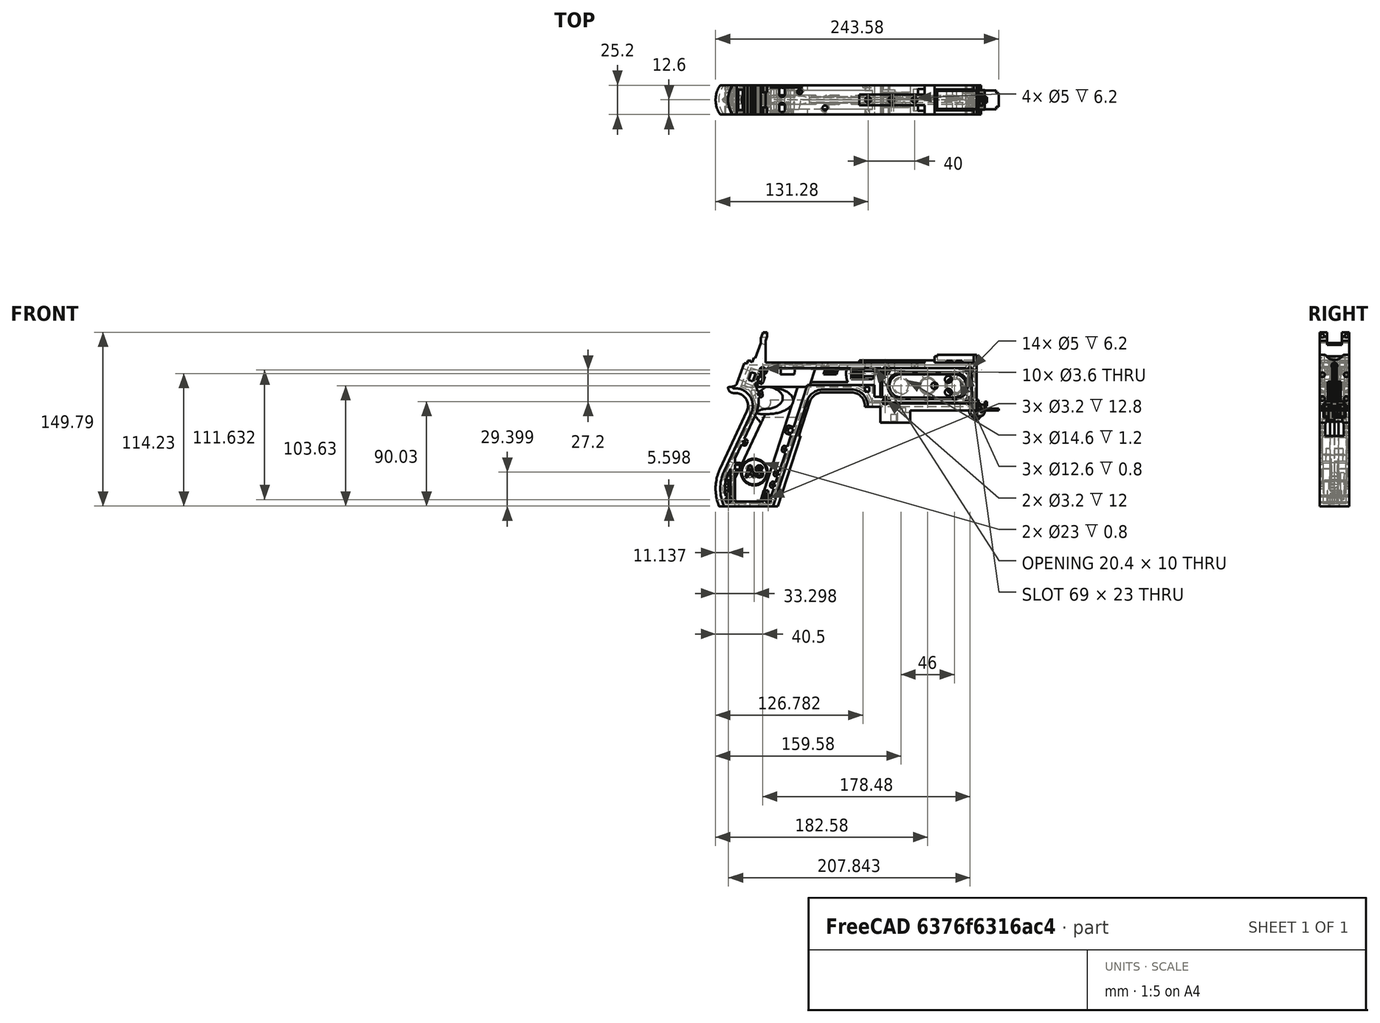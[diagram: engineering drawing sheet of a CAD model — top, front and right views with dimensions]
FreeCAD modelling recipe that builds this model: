
FCSTD DOCUMENT  (FreeCAD 1.0R39319 (Git))
Label: PICON-OF_ver_60
License: All rights reserved
LicenseURL: https://en.wikipedia.org/wiki/All_rights_reserved
objects: Sketcher::SketchObject×129, Part::Extrusion×65, Part::Cut×49, PartDesign::Pad×32, PartDesign::Pocket×21, PartDesign::Chamfer×15, PartDesign::Body×11, Part::MultiFuse×6, PartDesign::Fillet×6, Part::Part2DObjectPython×4, PartDesign::SubtractivePipe×4, PartDesign::SubtractiveLoft×4, PartDesign::Plane×3, PartDesign::SubShapeBinder×2, Part::Sweep×1, PartDesign::ShapeBinder×1, Mesh::Feature×1, PartDesign::Point×1, PartDesign::Groove×1
note: 650 computed .brp shape members not serialized (recipe doc carries the construction recipe); baked Part::Feature solids carry a one-line shape summary decoded from their .brp

FEATURE [Sketcher::SketchObject] Sketch  label="corpo principale"
  ArcFitTolerance = 1e-06
  AttacherType = Attacher::AttachEngine3D
  AttachmentSupport = -> [XZ_Plane]
  FullyConstrained = true
  MakeInternals = false
  MapMode = 5
  Placement = pos=(0,0,0) rot=(1,0,0;1.5708rad)
  sketch-geometry (65):
    g0: LineSegment StartX=0 StartY=0 StartZ=0 EndX=-57.2 EndY=0 EndZ=0
    g1: LineSegment StartX=-57.2 StartY=0 StartZ=0 EndX=-57.2 EndY=-10.4 EndZ=0
    g2: LineSegment StartX=-57.2 StartY=-10.4 StartZ=0 EndX=-82.8 EndY=-10.4 EndZ=0
    g3: LineSegment StartX=-82.8 StartY=-10.4 StartZ=0 EndX=-82.8 EndY=3.2 EndZ=0
    g4: LineSegment StartX=-82.8 StartY=3.2 StartZ=0 EndX=-93.6 EndY=3.2 EndZ=0
    g5: LineSegment StartX=-93.6 StartY=3.2 StartZ=0 EndX=-93.6 EndY=4 EndZ=0
    g6: LineSegment StartX=-107.6 StartY=18 StartZ=0 EndX=-132.428 EndY=18 EndZ=0
    g7: LineSegment StartX=-145.743 StartY=8.32624 StartZ=0 EndX=-175.232 EndY=-82.4316 EndZ=0
    g8: LineSegment StartX=-175.232 StartY=-82.4316 StartZ=0 EndX=-217.232 EndY=-82.4316 EndZ=0
    g9: LineSegment StartX=-217.232 StartY=-52.1862 StartZ=0 EndX=-193.988 EndY=-2.33927 EndZ=0
    g10: LineSegment StartX=-206.196 StartY=23.0857 StartZ=0 EndX=-199.861 EndY=40.4914 EndZ=0
    g11: LineSegment StartX=-199.861 StartY=40.4914 StartZ=0 EndX=-197.061 EndY=40.4914 EndZ=0
    g12: LineSegment StartX=-197.061 StartY=40.4914 StartZ=0 EndX=-197.061 EndY=42.8914 EndZ=0
    g13: LineSegment StartX=-197.061 StartY=42.8914 StartZ=0 EndX=-194.261 EndY=42.8914 EndZ=0
    g14: LineSegment StartX=-194.261 StartY=42.8914 StartZ=0 EndX=-194.535 EndY=42.1397 EndZ=0
    g15: LineSegment StartX=-194.535 StartY=42.1397 StartZ=0 EndX=-193.031 EndY=41.5924 EndZ=0
    g16: LineSegment StartX=-193.031 StartY=41.5924 StartZ=0 EndX=-191.663 EndY=45.3512 EndZ=0
    g17: LineSegment StartX=-191.663 StartY=45.3512 StartZ=0 EndX=-190.536 EndY=44.9408 EndZ=0
    g18: LineSegment StartX=-190.536 StartY=44.9408 StartZ=0 EndX=-185.747 EndY=58.0965 EndZ=0
    g19: LineSegment StartX=-185.747 StartY=58.0965 StartZ=0 EndX=-185.747 EndY=62.0965 EndZ=0
    g20: LineSegment StartX=-185.747 StartY=62.0965 StartZ=0 EndX=-183.832 EndY=67.3588 EndZ=0
    g21: LineSegment StartX=-183.832 StartY=67.3588 StartZ=0 EndX=-180.232 EndY=67.3588 EndZ=0
    g22: LineSegment StartX=-180.232 StartY=67.3588 StartZ=0 EndX=-180.232 EndY=63.7588 EndZ=0
    g23: LineSegment StartX=-180.232 StartY=63.7588 StartZ=0 EndX=-181.6 EndY=60 EndZ=0
    g24: LineSegment StartX=-181.6 StartY=60 StartZ=0 EndX=-181.6 EndY=41.2 EndZ=0
    g25: LineSegment StartX=-181.6 StartY=41.2 StartZ=0 EndX=-100.8 EndY=41.2 EndZ=0
    g26: LineSegment StartX=-36 StartY=43.2 StartZ=0 EndX=-36 EndY=41.2 EndZ=0
    g27: LineSegment StartX=0 StartY=48 StartZ=0 EndX=0 EndY=0 EndZ=0
    g28: LineSegment StartX=-209.901 StartY=19.85 StartZ=0 EndX=-209.901 EndY=20.1 EndZ=0
    g29: LineSegment StartX=-208.001 StartY=22 StartZ=0 EndX=-207.747 EndY=22 EndZ=0
    g30: LineSegment StartX=-207.583 StartY=19 StartZ=0 EndX=-209.051 EndY=19 EndZ=0
    g31: ArcOfCircle CenterX=-208.001 CenterY=20.1 CenterZ=0 NormalX=0 NormalY=0 NormalZ=1 AngleXU=0 Radius=1.9 StartAngle=1.5708 EndAngle=3.14159
    g32: GeomPoint [constr] X=-209.901 Y=22 Z=0
    g33: ArcOfCircle CenterX=-209.051 CenterY=19.85 CenterZ=0 NormalX=0 NormalY=0 NormalZ=1 AngleXU=0 Radius=0.85 StartAngle=3.14159 EndAngle=4.71239
    g34: GeomPoint [constr] X=-209.901 Y=19 Z=0
    g35: ArcOfCircle CenterX=-207.747 CenterY=23.65 CenterZ=0 NormalX=0 NormalY=0 NormalZ=1 AngleXU=0 Radius=1.65 StartAngle=4.71239 EndAngle=5.93412
    g36: GeomPoint [constr] X=-206.591 Y=22 Z=0
    g37: LineSegment StartX=-4 StartY=6 StartZ=0 EndX=-4 EndY=36.4 EndZ=0
    g38: LineSegment StartX=-4 StartY=36.4 StartZ=0 EndX=-185.2 EndY=36.4 EndZ=0
    g39: LineSegment StartX=-185.2 StartY=36.4 StartZ=0 EndX=-190.441 EndY=22 EndZ=0
    g40: LineSegment StartX=-214.575 StartY=-78.4316 StartZ=0 EndX=-178.142 EndY=-78.4316 EndZ=0
    g41: LineSegment StartX=-178.142 StartY=-78.4316 StartZ=0 EndX=-145.51 EndY=22 EndZ=0
    g42: LineSegment StartX=-145.51 StartY=22 StartZ=0 EndX=-87.91 EndY=22 EndZ=0
    g43: LineSegment StartX=-87.91 StartY=22 StartZ=0 EndX=-87.91 EndY=11.6 EndZ=0
    g44: LineSegment StartX=-87.91 StartY=11.6 StartZ=0 EndX=-80.11 EndY=11.6 EndZ=0
    g45: LineSegment StartX=-80.11 StartY=11.6 StartZ=0 EndX=-80.11 EndY=6 EndZ=0
    g46: LineSegment StartX=-80.11 StartY=6 StartZ=0 EndX=-4 EndY=6 EndZ=0
    g47: LineSegment StartX=-190.363 StartY=-4.02975 StartZ=0 EndX=-213.607 EndY=-53.8767 EndZ=0
    g48: ArcOfCircle CenterX=-132.428 CenterY=4 CenterZ=0 NormalX=0 NormalY=0 NormalZ=1 AngleXU=0 Radius=14 StartAngle=1.5708 EndAngle=2.82743
    g49: GeomPoint [constr] X=-142.6 Y=18 Z=0
    g50: ArcOfCircle CenterX=-107.6 CenterY=4 CenterZ=0 NormalX=0 NormalY=0 NormalZ=1 AngleXU=0 Radius=14 StartAngle=0 EndAngle=1.5708
    g51: GeomPoint [constr] X=-93.6 Y=18 Z=0
    g52: ArcOfCircle CenterX=-184.801 CenterY=-67.3089 CenterZ=0 NormalX=0 NormalY=0 NormalZ=1 AngleXU=0 Radius=35.7833 StartAngle=2.70526 EndAngle=3.57792
    g53: ArcOfCircle CenterX=-207.583 CenterY=4 CenterZ=0 NormalX=0 NormalY=0 NormalZ=1 AngleXU=0 Radius=15 StartAngle=5.84685 EndAngle=7.85398
    g54: LineSegment [constr] StartX=-213.607 StartY=-53.8767 StartZ=0 EndX=-217.232 EndY=-52.1862 EndZ=0
    g55: ArcOfCircle CenterX=-184.801 CenterY=-67.3089 CenterZ=0 NormalX=0 NormalY=0 NormalZ=1 AngleXU=0 Radius=31.7833 StartAngle=2.70526 EndAngle=3.49911
    g56: ArcOfCircle CenterX=-218.095 CenterY=8.90192 CenterZ=0 NormalX=0 NormalY=0 NormalZ=1 AngleXU=0 Radius=30.5989 StartAngle=5.84685 EndAngle=6.72553
    g57: LineSegment StartX=-44.6 StartY=43.2 StartZ=0 EndX=-36 EndY=43.2 EndZ=0
    g58: LineSegment StartX=-100.8 StartY=41.2 StartZ=0 EndX=-44.6 EndY=41.2 EndZ=0
    g59: LineSegment StartX=-44.6 StartY=41.2 StartZ=0 EndX=-44.6 EndY=43.2 EndZ=0
    g60: LineSegment StartX=-2.4 StartY=48 StartZ=0 EndX=0 EndY=48 EndZ=0
    g61: LineSegment StartX=-36 StartY=41.2 StartZ=0 EndX=-2.4 EndY=41.2 EndZ=0
    g62: LineSegment StartX=-2.4 StartY=41.2 StartZ=0 EndX=-2.4 EndY=48 EndZ=0
    g63: LineSegment [constr] StartX=-181.6 StartY=36.4 StartZ=0 EndX=-152.209 EndY=36.4 EndZ=0
    g64: LineSegment [constr] StartX=-181.6 StartY=36.4 StartZ=0 EndX=-130.41 EndY=36.4 EndZ=0
  constraints (183):
    c: Coincident(g-1,g0)
    c: PointOnObject(g0,g-1)
    c: Coincident(g0,g1)
    c: Vertical(g1)
    c: Coincident(g1,g2)
    c: Horizontal(g2)
    c: Coincident(g2,g3)
    c: Vertical(g3)
    c: Coincident(g3,g4)
    c: Coincident(g4,g5)
    c: Vertical(g5)
    c: Horizontal(g6)
    c: Coincident(g7,g8)
    c: Horizontal(g8)
    c: Coincident(g10,g11)
    c: Horizontal(g11)
    c: Coincident(g11,g12)
    c: Vertical(g12)
    c: Coincident(g12,g13)
    c: Horizontal(g13)
    c: Coincident(g13,g14)
    c: Coincident(g14,g15)
    c: Coincident(g15,g16)
    c: Coincident(g16,g17)
    c: Coincident(g17,g18)
    c: Coincident(g18,g19)
    c: Vertical(g19)
    c: Coincident(g19,g20)
    c: Coincident(g20,g21)
    c: Horizontal(g21)
    c: Coincident(g21,g22)
    c: Vertical(g22)
    c: Coincident(g22,g23)
    c: Coincident(g23,g24)
    c: Vertical(g24)
    c: Coincident(g24,g25)
    c: Horizontal(g25)
    c: Coincident(g57,g26)
    c: Vertical(g26)
    c: Coincident(g26,g61)
    c: PointOnObject(g60,g-2)
    c: Coincident(g60,g27)
    c: Coincident(g27,g0)
    c: DistanceY(g27,g27) = 48
    c: DistanceY(g1,g1) = 10.4
    c: DistanceX(g0,g0) = 57.2
    c: DistanceX(g2,g2) = 25.6
    c: Horizontal(g4)
    c: DistanceY(g3,g3) = 13.6
    c: DistanceX(g4,g4) = 10.8
    c: DistanceY(g5,g51) = 14.8
    c: DistanceX(g49,g51) = 49
    c: Distance(g7,g49) = 105.6
    c: DistanceX(g61,g60) = 36
    c: DistanceX(g25,g25) = 80.8
    c: DistanceY(g24,g24) = 18.8
    c: DistanceY(g22,g22) = 3.6
    c: Distance(g23) = 4
    c: Angle(g-1,g23) = 1.22173
    c: DistanceX(g21,g21) = 3.6
    c: Distance(g20) = 5.6
    c: Angle(g-1,g20) = 1.22173
    c: DistanceY(g19,g19) = 4
    c: Distance(g18) = 14
    c: Angle(g-1,g18) = 1.22173
    c: Distance(g17) = 1.2
    c: Distance(g16) = 4
    c: Angle(g16) = 1.22173
    c: Perpendicular(g18,g17)
    c: Distance(g15) = 1.6
    c: Perpendicular(g16,g15)
    c: Distance(g14) = 0.8
    c: DistanceX(g13,g13) = 2.8
    c: Perpendicular(g15,g14)
    c: DistanceY(g12,g12) = 2.4
    c: DistanceX(g11,g11) = 2.8
    c: Distance(g9) = 55
    c: Angle(g9,g-1) = 2.00713
    c: Horizontal(g29)
    c: Vertical(g28)
    c: Horizontal(g30)
    c: PointOnObject(g32,g29)
    c: PointOnObject(g32,g28)
    c: Tangent(g29,g31) = 1.5708
    c: Tangent(g28,g31) = 1.5708
    c: PointOnObject(g34,g28)
    c: PointOnObject(g34,g30)
    c: Tangent(g28,g33) = 1.5708
    c: Tangent(g30,g33) = 1.5708
    c: PointOnObject(g36,g29)
    c: PointOnObject(g36,g10)
    c: Tangent(g29,g35) = -1.5708
    c: Tangent(g10,g35) = -1.5708
    c: Angle(g-1,g10) = 1.22173
    c: Radius(g35) = 1.65
    c: Vertical(g37)
    c: Coincident(g37,g38)
    c: Horizontal(g38)
    c: Coincident(g38,g39)
    c: Horizontal(g40)
    c: Coincident(g40,g41)
    c: Coincident(g41,g42)
    c: Horizontal(g42)
    c: Coincident(g42,g43)
    c: Vertical(g43)
    c: Coincident(g43,g44)
    c: Horizontal(g44)
    c: Coincident(g44,g45)
    c: Vertical(g45)
    c: Coincident(g45,g46)
    c: Coincident(g46,g37)
    c: Horizontal(g46)
    c: DistanceY(g0,g37) = 6
    c: DistanceX(g37,g0) = 4
    c: DistanceY(g37,g25) = 4.8
    c: DistanceX(g38,g38) = 181.2
    c: DistanceX(g42,g42) = 57.6
    c: DistanceY(g49,g41) = 4
    c: DistanceX(g41,g49) = 2.91
    c: DistanceY(g43,g43) = 10.4
    c: DistanceX(g44,g44) = 7.8
    c: DistanceY(g7,g40) = 4
    c: Distance(g47) = 55
    c: Angle(g-1,g39) = 1.22173
    c: PointOnObject(g49,g7)
    c: PointOnObject(g49,g6)
    c: Tangent(g7,g48) = -1.5708
    c: Tangent(g6,g48) = -1.5708
    c: PointOnObject(g51,g5)
    c: PointOnObject(g51,g6)
    c: Tangent(g5,g50) = -1.5708
    c: Tangent(g6,g50) = -1.5708
    c: Radius(g50) = 14
    c: Radius(g48) = 14
    c: DistanceX(g8,g8) = 42
    c: Angle(g7,g-1) = 1.88496
    c: Parallel(g41,g7)
    c: Parallel(g47,g9)
    c: Coincident(g52,g8)
    c: Tangent(g52,g9) = 1.5708
    c: DistanceX(g9,g8) = 0
    c: Tangent(g53,g9) = -1.5708
    c: Tangent(g53,g30) = -1.5708
    c: Diameter(g53) = 30
    c: DistanceY(g53,g0) = -4
    c: Coincident(g54,g47)
    c: Distance(g54) = 4
    c: Coincident(g54,g9)
    c: Coincident(g55,g40)
    c: Tangent(g55,g47) = -1.5708
    c: Coincident(g52,g55)
    c: Coincident(g56,g39)
    c: Tangent(g56,g47) = 1.5708
    c: Horizontal(g57)
    c: DistanceX(g57,g57) = 8.6
    c: Coincident(g58,g25)
    c: Horizontal(g58)
    c: Coincident(g59,g58)
    c: Vertical(g59)
    c: DistanceY(g58,g57) = 2
    c: DistanceX(g58,g58) = 56.2
    c: Coincident(g59,g57)
    c: DistanceY(g41,g36) = 0
    c: DistanceY(g36,g39) = 0
    c: DistanceY(g28,g28) = 0.25
    c: DistanceX(g30,g36) = 2.46
    c: DistanceX(g28,g29) = 1.9
    c: Coincident(g62,g60)
    c: Horizontal(g60)
    c: DistanceX(g62,g27) = 2.4
    c: Coincident(g61,g62)
    c: DistanceY(g26,g26) = 2
    c: Vertical(g62)
    c: DistanceY(g61,g60) = 6.8
    c: Horizontal(g61)
    c: Distance(g63) = 29.391
    c: PointOnObject(g63,g38)
    c: PointOnObject(g63,g38)
    c: Distance(g64) = 51.19
    c: PointOnObject(g64,g38)
    c: PointOnObject(g64,g38)
    c: DistanceX(g24,g63) = 0
    c: DistanceX(g24,g64) = 0
FEATURE [Part::Extrusion] Extrude  label="Extrude corpo principale"
  Base = -> Sketch
  Dir = (0,-1,2e-16)
  DirMode = 2
  FaceMakerClass = Part::FaceMakerBullseye
  FaceMakerMode = 3
  LengthFwd = 25.2
  LengthRev = 12.6
  Solid = true
  Symmetric = true
FEATURE [Sketcher::SketchObject] Sketch002  label="scavo grilletto"
  ArcFitTolerance = 1e-06
  AttachmentSupport = -> [XZ_Plane]
  ExternalGeometry = -> [Sketch]
  FullyConstrained = true
  MakeInternals = false
  MapMode = 5
  Placement = pos=(0,0,0) rot=(1,0,0;1.5708rad)
  sketch-geometry (4):
    g0: LineSegment StartX=-89.51 StartY=22 StartZ=0 EndX=-152.71 EndY=22 EndZ=0
    g1: LineSegment StartX=-152.71 StartY=22 StartZ=0 EndX=-167.006 EndY=-22 EndZ=0
    g2: LineSegment StartX=-167.006 StartY=-22 StartZ=0 EndX=-89.51 EndY=-22 EndZ=0
    g3: LineSegment StartX=-89.51 StartY=-22 StartZ=0 EndX=-89.51 EndY=22 EndZ=0
  constraints (12):
    c: Horizontal(g0)
    c: Coincident(g0,g1)
    c: Coincident(g1,g2)
    c: Horizontal(g2)
    c: Coincident(g2,g3)
    c: Coincident(g3,g0)
    c: Vertical(g3)
    c: Angle(g1,g0) = 1.88496
    c: DistanceY(g3,g3) = 44
    c: DistanceX(g0,g0) = 63.2
    c: DistanceX(g0,g-3) = 1.6
    c: DistanceY(g-3,g0) = 0
FEATURE [Sketcher::SketchObject] Sketch004  label="traiettoria arrotondamento impugnatura anteriore"
  ArcFitTolerance = 1e-06
  AttachmentSupport = -> [XZ_Plane]
  ExternalGeometry = -> [Sketch]
  FullyConstrained = true
  MakeInternals = false
  MapMode = 5
  Placement = pos=(0,0,0) rot=(1,0,0;1.5708rad)
  sketch-geometry (13):
    g0: LineSegment StartX=-175.232 StartY=-82.4316 StartZ=0 EndX=-145.743 EndY=8.32624 EndZ=0
    g1: LineSegment StartX=-93.6 StartY=3.2 StartZ=0 EndX=-93.6 EndY=4 EndZ=0
    g2: LineSegment StartX=-132.428 StartY=18 StartZ=0 EndX=-107.6 EndY=18 EndZ=0
    g3: ArcOfCircle CenterX=-132.428 CenterY=4 CenterZ=0 NormalX=0 NormalY=0 NormalZ=1 AngleXU=0 Radius=14 StartAngle=1.5708 EndAngle=2.82743
    g4: ArcOfCircle CenterX=-107.6 CenterY=4 CenterZ=0 NormalX=0 NormalY=0 NormalZ=1 AngleXU=0 Radius=14 StartAngle=0 EndAngle=1.5708
    g5: LineSegment StartX=-175.232 StartY=-82.4316 StartZ=0 EndX=-217.232 EndY=-82.4316 EndZ=0
    g6: LineSegment StartX=-217.232 StartY=-52.1862 StartZ=0 EndX=-193.988 EndY=-2.33927 EndZ=0
    g7: LineSegment StartX=-209.051 StartY=19 StartZ=0 EndX=-207.583 EndY=19 EndZ=0
    g8: LineSegment StartX=-209.901 StartY=20.1 StartZ=0 EndX=-209.901 EndY=19.85 EndZ=0
    g9: ArcOfCircle CenterX=-184.801 CenterY=-67.3089 CenterZ=0 NormalX=0 NormalY=0 NormalZ=1 AngleXU=0 Radius=35.7833 StartAngle=2.70526 EndAngle=3.57792
    g10: ArcOfCircle CenterX=-207.583 CenterY=4 CenterZ=0 NormalX=0 NormalY=0 NormalZ=1 AngleXU=0 Radius=15 StartAngle=5.84685 EndAngle=7.85398
    g11: ArcOfCircle CenterX=-209.051 CenterY=19.85 CenterZ=0 NormalX=0 NormalY=0 NormalZ=1 AngleXU=0 Radius=0.85 StartAngle=3.14159 EndAngle=4.71239
    g12: ArcOfCircle CenterX=-208.001 CenterY=20.1 CenterZ=0 NormalX=0 NormalY=0 NormalZ=1 AngleXU=0 Radius=1.9 StartAngle=1.5708 EndAngle=3.14159
  constraints (26):
    c: Coincident(g0,g-3)
    c: Coincident(g0,g-6)
    c: Coincident(g1,g-8)
    c: Coincident(g1,g-7)
    c: Coincident(g2,g-5)
    c: Coincident(g2,g-4)
    c: Coincident(g3,g2)
    c: Tangent(g3,g0) = 1.5708
    c: Coincident(g4,g1)
    c: Tangent(g4,g2) = 1.5708
    c: Coincident(g5,g0)
    c: Coincident(g5,g-9)
    c: Coincident(g6,g-12)
    c: Coincident(g6,g-11)
    c: Coincident(g7,g-15)
    c: Coincident(g7,g-14)
    c: Coincident(g8,g-16)
    c: Coincident(g8,g-17)
    c: Tangent(g9,g6) = 1.5708
    c: Coincident(g9,g5)
    c: Coincident(g10,g7)
    c: Tangent(g10,g6) = -1.5708
    c: Tangent(g11,g7) = -1.5708
    c: Coincident(g11,g8)
    c: Tangent(g12,g8) = -1.5708
    c: Coincident(g12,g-17)
FEATURE [PartDesign::Plane] DatumPlane  label="Piano per disegno arrotondamento impugnatura"
  AttachmentSupport = -> [Sketch]
  Length = 73.6581
  MapMode = 7
  Placement = pos=(-145.743,1.8e-15,8.32624) rot=(0.154555,0.154555,0.97582;1.59527rad)
  ResizeMode = 0
  Width = 303.511
FEATURE [Sketcher::SketchObject] Sketch005  label="forma arrotondamento impugnatura anteriore"
  ArcFitTolerance = 1e-06
  AttachmentSupport = -> [DatumPlane]
  FullyConstrained = true
  MakeInternals = false
  MapMode = 5
  Placement = pos=(-145.743,1.8e-15,8.32624) rot=(0.154555,0.154555,0.97582;1.59527rad)
  sketch-geometry (5):
    g0: GeomPoint [constr] X=0 Y=-4 Z=0
    g1: GeomPoint [constr] X=-12.6 Y=7.1e-15 Z=0
    g2: GeomPoint [constr] X=12.6 Y=4.97e-14 Z=0
    g3: LineSegment StartX=-12.6 StartY=7.1e-15 StartZ=0 EndX=12.6 EndY=4.97e-14 EndZ=0
    g4: ArcOfCircle CenterX=-3.88e-14 CenterY=17.845 CenterZ=0 NormalX=0 NormalY=0 NormalZ=1 AngleXU=0 Radius=21.845 StartAngle=4.09759 EndAngle=5.32718
  constraints (11):
    c: DistanceY(g0,g-1) = 4
    c: DistanceX(g-1,g0) = 0
    c: DistanceX(g1,g-1) = 12.6
    c: DistanceX(g-1,g2) = 12.6
    c: DistanceY(g-1,g2) = 0
    c: DistanceY(g-1,g1) = 0
    c: Coincident(g3,g1)
    c: Coincident(g3,g2)
    c: Coincident(g4,g1)
    c: Coincident(g4,g2)
    c: PointOnObject(g0,g4)
FEATURE [Part::Sweep] Sweep  label="Sweep impugnatura"
  Frenet = true
  Sections = -> [Sketch005]
  Solid = true
  Spine = -> Sketch [Edge32,Edge33,Edge34,Edge35,Edge36,Edge37,Edge38,Edge39,Edge40,Edge41,Edge42,Edge43,Edge44]
  Transition = 1
FEATURE [Sketcher::SketchObject] Sketch008  label="buchi e pulizie varie"
  ArcFitTolerance = 1e-06
  AttachmentSupport = -> [XZ_Plane]
  ExternalGeometry = -> [Sketch]
  FullyConstrained = true
  MakeInternals = false
  MapMode = 5
  Placement = pos=(0,0,0) rot=(1,0,0;1.5708rad)
  sketch-geometry (26):
    g0: LineSegment StartX=-96.278 StartY=20.155 StartZ=0 EndX=-92.278 EndY=20.155 EndZ=0
    g1: LineSegment StartX=-92.278 StartY=20.155 StartZ=0 EndX=-92.278 EndY=16.155 EndZ=0
    g2: LineSegment StartX=-92.278 StartY=16.155 StartZ=0 EndX=-96.278 EndY=16.155 EndZ=0
    g3: LineSegment StartX=-96.278 StartY=16.155 StartZ=0 EndX=-96.278 EndY=20.155 EndZ=0
    g4: LineSegment StartX=-222.232 StartY=-82.4316 StartZ=0 EndX=-170.232 EndY=-82.4316 EndZ=0
    g5: LineSegment StartX=-170.232 StartY=-82.4316 StartZ=0 EndX=-170.232 EndY=-86.4316 EndZ=0
    g6: LineSegment StartX=-170.232 StartY=-86.4316 StartZ=0 EndX=-222.232 EndY=-86.4316 EndZ=0
    g7: LineSegment StartX=-222.232 StartY=-86.4316 StartZ=0 EndX=-222.232 EndY=-82.4316 EndZ=0
    g8: LineSegment StartX=-213.901 StartY=20.1 StartZ=0 EndX=-213.901 EndY=26 EndZ=0
    g9: LineSegment StartX=-213.901 StartY=26 StartZ=0 EndX=-206.196 EndY=26 EndZ=0
    g10: LineSegment StartX=-17.4 StartY=42.8 StartZ=0 EndX=-12.4 EndY=42.8 EndZ=0
    g11: LineSegment StartX=-12.4 StartY=42.8 StartZ=0 EndX=-12.4 EndY=41.2 EndZ=0
    g12: LineSegment StartX=-12.4 StartY=41.2 StartZ=0 EndX=-17.4 EndY=41.2 EndZ=0
    g13: LineSegment StartX=-17.4 StartY=41.2 StartZ=0 EndX=-17.4 EndY=42.8 EndZ=0
    g14: LineSegment StartX=-25.9 StartY=42.8 StartZ=0 EndX=-20.9 EndY=42.8 EndZ=0
    g15: LineSegment StartX=-20.9 StartY=42.8 StartZ=0 EndX=-20.9 EndY=41.2 EndZ=0
    g16: LineSegment StartX=-20.9 StartY=41.2 StartZ=0 EndX=-25.9 EndY=41.2 EndZ=0
    g17: LineSegment StartX=-25.9 StartY=41.2 StartZ=0 EndX=-25.9 EndY=42.8 EndZ=0
    g18: GeomPoint [constr] X=-206.196 Y=23.0857 Z=0
    g19: GeomPoint [constr] X=-213.901 Y=20.1 Z=0
    g20: BSplineCurve PolesCount=4 KnotsCount=2 Degree=3 IsPeriodic=0
    g21-g24: Circle [constr] x4 (B-spline internal-alignment scaffolding for g20; pole/knot coordinates omitted)
    g25: LineSegment StartX=-206.196 StartY=26 StartZ=0 EndX=-206.196 EndY=23.0857 EndZ=0
  constraints (73):
    c: Horizontal(g0)
    c: Coincident(g1,g0)
    c: Vertical(g1)
    c: Coincident(g2,g1)
    c: Horizontal(g2)
    c: Coincident(g3,g2)
    c: Coincident(g3,g0)
    c: Vertical(g3)
    c: DistanceX(g0,g-4) = 4.368
    c: DistanceY(g0,g-4) = 1.845
    c: DistanceY(g1,g1) = 4
    c: DistanceX(g2,g2) = 4
    c: Horizontal(g4)
    c: Coincident(g5,g4)
    c: Vertical(g5)
    c: Coincident(g6,g5)
    c: Horizontal(g6)
    c: Coincident(g7,g6)
    c: Coincident(g7,g4)
    c: Vertical(g7)
    c: DistanceY(g7,g7) = 4
    c: DistanceX(g4,g-5) = 5
    c: DistanceX(g-5,g4) = 5
    c: DistanceY(g4,g-5) = 0
    c: Coincident(g9,g8)
    c: Parallel(g9,g-6)
    c: DistanceX(g8,g-8) = 4
    c: Horizontal(g10)
    c: Coincident(g11,g10)
    c: Vertical(g11)
    c: Coincident(g12,g11)
    c: Horizontal(g12)
    c: Coincident(g13,g12)
    c: Coincident(g13,g10)
    c: Vertical(g13)
    c: Horizontal(g14)
    c: Coincident(g15,g14)
    c: Vertical(g15)
    c: Coincident(g16,g15)
    c: Horizontal(g16)
    c: Coincident(g17,g16)
    c: Coincident(g17,g14)
    c: Vertical(g17)
    c: DistanceY(g11,g10) = 1.6
    c: DistanceX(g10,g10) = 5
    c: DistanceY(g15,g14) = 1.6
    c: DistanceX(g14,g14) = 5
    c: DistanceX(g15,g12) = 3.5
    c: DistanceX(g11,g-9) = 10
    c: DistanceY(g-9,g11) = 0
    c: DistanceY(g-9,g15) = 0
    c: Perpendicular(g8,g9)
    c: DistanceY(g-7,g9) = 4
    c: DistanceY(g8,g-8) = 0
    c: InternalAlignment(g18,g20)
    c: InternalAlignment(g19,g20)
    c: InternalAlignment(g21,g20)
    c: Weight(g21) = 1
    c: InternalAlignment(g22,g20)
    c: Equal(g22,g21)
    c: InternalAlignment(g23,g20)
    c: Equal(g23,g21)
    c: InternalAlignment(g24,g20)
    c: Equal(g24,g21)
    c: Coincident(g18,g-12)
    c: Coincident(g19,g8)
    c: Coincident(g25,g9)
    c: Coincident(g25,g20)
    c: Vertical(g25)
    c: DistanceY(g20,g23) = 0
    c: DistanceY(g22,g18) = 2.26
    c: DistanceX(g22,g18) = 0.93
    c: DistanceX(g20,g23) = 2.9
FEATURE [Part::Extrusion] Extrude004  label="Extrude Buchi e pulizie varie"
  Base = -> Sketch008
  Dir = (0,-1,2e-16)
  DirMode = 2
  FaceMakerClass = Part::FaceMakerBullseye
  FaceMakerMode = 3
  LengthFwd = 25.2
  LengthRev = 0
  Solid = true
  Symmetric = true
FEATURE [Sketcher::SketchObject] Sketch009  label="rinforzi"
  ArcFitTolerance = 1e-06
  AttachmentSupport = -> [XZ_Plane]
  ExternalGeometry = -> [Sketch]
  FullyConstrained = true
  MakeInternals = false
  MapMode = 5
  Placement = pos=(0,0,0) rot=(1,0,0;1.5708rad)
  sketch-geometry (9):
    g0: LineSegment StartX=-87.91 StartY=22 StartZ=0 EndX=-87.91 EndY=36.4 EndZ=0
    g1: LineSegment StartX=-87.91 StartY=36.4 StartZ=0 EndX=-97.91 EndY=36.4 EndZ=0
    g2: LineSegment StartX=-97.91 StartY=36.4 StartZ=0 EndX=-97.91 EndY=22 EndZ=0
    g3: LineSegment StartX=-97.91 StartY=22 StartZ=0 EndX=-87.91 EndY=22 EndZ=0
    g4: LineSegment StartX=-149.713 StartY=9.06563 StartZ=0 EndX=-154.586 EndY=-5.93437 EndZ=0
    g5: LineSegment StartX=-154.586 StartY=-5.93437 StartZ=0 EndX=-191.863 EndY=-5.93437 EndZ=0
    g6: LineSegment StartX=-191.863 StartY=-5.93437 StartZ=0 EndX=-191.863 EndY=9.06563 EndZ=0
    g7: LineSegment StartX=-191.863 StartY=9.06563 StartZ=0 EndX=-149.713 EndY=9.06563 EndZ=0
    g8: LineSegment [constr] StartX=-145.51 StartY=22 StartZ=0 EndX=-149.713 EndY=9.06563 EndZ=0
  constraints (25):
    c: Vertical(g0)
    c: Coincident(g1,g0)
    c: Horizontal(g1)
    c: Coincident(g2,g1)
    c: Vertical(g2)
    c: Coincident(g3,g2)
    c: Coincident(g3,g0)
    c: Horizontal(g3)
    c: Coincident(g0,g-4)
    c: DistanceX(g3,g3) = 10
    c: DistanceY(g0,g-3) = 0
    c: Coincident(g5,g4)
    c: Horizontal(g5)
    c: Coincident(g6,g5)
    c: Vertical(g6)
    c: Coincident(g7,g6)
    c: Coincident(g7,g4)
    c: Horizontal(g7)
    c: Distance(g8) = 13.6
    c: Parallel(g-6,g8)
    c: Coincident(g-6,g8)
    c: Parallel(g4,g-6)
    c: DistanceY(g4,g4) = 15
    c: Coincident(g4,g8)
    c: DistanceX(g-5,g5) = -1.5
FEATURE [Part::Extrusion] Extrude001  label="Extrude scavo grilletto"
  Base = -> Sketch002
  Dir = (0,-1,2e-16)
  DirMode = 2
  FaceMakerClass = Part::FaceMakerBullseye
  FaceMakerMode = 3
  LengthFwd = 16
  LengthRev = 0
  Solid = true
  Symmetric = true
FEATURE [Part::Extrusion] Extrude005  label="Extrude Rinforzi"
  Base = -> Sketch009
  Dir = (0,-1,2e-16)
  DirMode = 2
  FaceMakerClass = Part::FaceMakerBullseye
  FaceMakerMode = 3
  LengthFwd = 2
  LengthRev = 0
  Placement = pos=(0,12.6,0) rot=(0,0,1;0rad)
  Solid = true
  Symmetric = false
FEATURE [PartDesign::ShapeBinder] CopyCut
  TraceSupport = false
FEATURE [PartDesign::Plane] DatumPlane001
  AttachmentSupport = -> [CopyCut]
  Length = 283.944
  MapMode = 5
  Placement = pos=(0,12.6,0) rot=(0,0.707107,0.707107;3.14159rad)
  ResizeMode = 0
  Width = 188.15
FEATURE [Sketcher::SketchObject] Sketch010  label="buco neopixel"
  ArcFitTolerance = 1e-06
  AttachmentSupport = -> [XZ_Plane]
  ExternalGeometry = -> [Sketch]
  FullyConstrained = true
  MakeInternals = false
  MapMode = 5
  Placement = pos=(0,0,0) rot=(1,0,0;1.5708rad)
  sketch-geometry (5):
    g0: LineSegment [constr] StartX=-199.861 StartY=40.4914 StartZ=0 EndX=-201.368 EndY=36.3521 EndZ=0
    g1: LineSegment StartX=-201.368 StartY=36.3521 StartZ=0 EndX=-204.932 EndY=26.5605 EndZ=0
    g2: LineSegment StartX=-201.368 StartY=36.3521 StartZ=0 EndX=-180.2 EndY=28.6477 EndZ=0
    g3: LineSegment StartX=-180.2 StartY=28.6477 StartZ=0 EndX=-183.764 EndY=18.8561 EndZ=0
    g4: LineSegment StartX=-183.764 StartY=18.8561 StartZ=0 EndX=-204.932 EndY=26.5605 EndZ=0
  constraints (14):
    c: Parallel(g0,g-3)
    c: Distance(g0) = 4.405
    c: Coincident(g0,g-3)
    c: Coincident(g2,g1)
    c: Coincident(g3,g2)
    c: Coincident(g4,g3)
    c: Coincident(g4,g1)
    c: Parallel(g1,g-3)
    c: Distance(g1) = 10.42
    c: Coincident(g1,g0)
    c: Parallel(g2,g4)
    c: Perpendicular(g1,g2)
    c: DistanceX(g-4,g2) = 5
    c: Parallel(g3,g1)
FEATURE [Part::Extrusion] Extrude006  label="Extrude buco neopixel"
  Base = -> Sketch010
  Dir = (0,-1,2e-16)
  DirMode = 2
  FaceMakerClass = Part::FaceMakerBullseye
  FaceMakerMode = 3
  LengthFwd = 17.2
  LengthRev = 0
  Solid = true
  Symmetric = true
FEATURE [Sketcher::SketchObject] Sketch011  label="fermo grilletto"
  ArcFitTolerance = 1e-06
  AttachmentSupport = -> [XZ_Plane]
  ExternalGeometry = -> [Sketch]
  FullyConstrained = true
  MakeInternals = false
  MapMode = 5
  Placement = pos=(0,0,0) rot=(1,0,0;1.5708rad)
  sketch-geometry (18):
    g0: LineSegment [constr] StartX=-145.51 StartY=22 StartZ=0 EndX=-157.347 EndY=-14.4293 EndZ=0
    g1: LineSegment [constr] StartX=-157.347 StartY=-14.4293 StartZ=0 EndX=-157.841 EndY=-15.951 EndZ=0
    g2: LineSegment StartX=-161.151 StartY=-13.1932 StartZ=0 EndX=-155.825 EndY=-14.9237 EndZ=0
    g3: LineSegment StartX=-163.167 StartY=-14.2205 StartZ=0 EndX=-164.403 EndY=-18.0247 EndZ=0
    g4: LineSegment StartX=-163.376 StartY=-20.0408 StartZ=0 EndX=-158.05 EndY=-21.7713 EndZ=0
    g5: LineSegment StartX=-158.05 StartY=-21.7713 StartZ=0 EndX=-155.825 EndY=-14.9237 EndZ=0
    g6: LineSegment StartX=-161.645 StartY=-14.7149 StartZ=0 EndX=-157.841 EndY=-15.951 EndZ=0
    g7: LineSegment StartX=-157.841 StartY=-15.951 StartZ=0 EndX=-159.077 EndY=-19.7552 EndZ=0
    g8: LineSegment StartX=-159.077 StartY=-19.7552 StartZ=0 EndX=-162.881 EndY=-18.5191 EndZ=0
    g9: LineSegment StartX=-162.881 StartY=-18.5191 StartZ=0 EndX=-161.645 EndY=-14.7149 EndZ=0
    g10: LineSegment [constr] StartX=-161.645 StartY=-14.7149 StartZ=0 EndX=-161.151 EndY=-13.1932 EndZ=0
    g11: LineSegment [constr] StartX=-159.077 StartY=-19.7552 StartZ=0 EndX=-157.555 EndY=-20.2496 EndZ=0
    g12: LineSegment [constr] StartX=-159.077 StartY=-19.7552 StartZ=0 EndX=-159.572 EndY=-21.2769 EndZ=0
    g13: LineSegment [constr] StartX=-161.645 StartY=-14.7149 StartZ=0 EndX=-163.167 EndY=-14.2205 EndZ=0
    g14: ArcOfCircle CenterX=-161.645 CenterY=-14.7149 CenterZ=0 NormalX=0 NormalY=0 NormalZ=1 AngleXU=0 Radius=1.6 StartAngle=1.25664 EndAngle=2.82743
    g15: GeomPoint [constr] X=-162.673 Y=-12.6988 Z=0
    g16: ArcOfCircle CenterX=-162.881 CenterY=-18.5191 CenterZ=0 NormalX=0 NormalY=0 NormalZ=1 AngleXU=0 Radius=1.6 StartAngle=2.82743 EndAngle=4.39823
    g17: GeomPoint [constr] X=-164.897 Y=-19.5464 Z=0
  constraints (48):
    c: Parallel(g0,g-3)
    c: Distance(g0) = 38.304
    c: Coincident(g0,g-3)
    c: Parallel(g1,g-3)
    c: Distance(g1) = 1.6
    c: Coincident(g1,g0)
    c: Coincident(g5,g4)
    c: Coincident(g5,g2)
    c: Coincident(g7,g6)
    c: Coincident(g8,g7)
    c: Coincident(g9,g8)
    c: Coincident(g9,g6)
    c: Parallel(g7,g-3)
    c: Parallel(g9,g7)
    c: Perpendicular(g6,g7)
    c: Parallel(g6,g8)
    c: Distance(g6) = 4
    c: Distance(g9) = 4
    c: Parallel(g5,g7)
    c: Parallel(g9,g3)
    c: Parallel(g2,g6)
    c: Parallel(g4,g8)
    c: Parallel(g13,g6)
    c: Parallel(g10,g9)
    c: Parallel(g11,g8)
    c: Parallel(g12,g7)
    c: Distance(g10) = 1.6
    c: Distance(g13) = 1.6
    c: Distance(g12) = 1.6
    c: Distance(g11) = 1.6
    c: Coincident(g10,g6)
    c: Coincident(g13,g6)
    c: Coincident(g12,g7)
    c: Coincident(g11,g7)
    c: Distance(g10,g15) = 1.6
    c: Distance(g15,g13) = 1.6
    c: Distance(g4,g12) = 1.6
    c: Distance(g4,g11) = 1.6
    c: PointOnObject(g15,g2)
    c: Tangent(g3,g14) = -1.5708
    c: Tangent(g2,g14) = 1.5708
    c: PointOnObject(g17,g4)
    c: PointOnObject(g17,g3)
    c: Tangent(g4,g16) = -1.5708
    c: Tangent(g3,g16) = -1.5708
    c: Equal(g16,g14)
    c: Coincident(g16,g8)
    c: Coincident(g6,g1)
FEATURE [Part::Extrusion] Extrude007  label="Extrude fermo grilletto"
  Base = -> Sketch011
  Dir = (0,-1,2e-16)
  DirMode = 2
  FaceMakerClass = Part::FaceMakerBullseye
  FaceMakerMode = 3
  LengthFwd = 25.2
  LengthRev = 0
  Solid = true
  Symmetric = true
FEATURE [Sketcher::SketchObject] Sketch012  label="buco oled"
  ArcFitTolerance = 1e-06
  AttachmentSupport = -> [XZ_Plane]
  ExternalGeometry = -> [Sketch]
  FullyConstrained = true
  MakeInternals = false
  MapMode = 5
  Placement = pos=(0,0,0) rot=(1,0,0;1.5708rad)
  sketch-geometry (4):
    g0: LineSegment StartX=-185.747 StartY=58.0965 StartZ=0 EndX=-180.232 EndY=56.0891 EndZ=0
    g1: LineSegment StartX=-185.747 StartY=58.0965 StartZ=0 EndX=-185.747 EndY=67.3588 EndZ=0
    g2: LineSegment StartX=-185.747 StartY=67.3588 StartZ=0 EndX=-180.232 EndY=67.3588 EndZ=0
    g3: LineSegment StartX=-180.232 StartY=67.3588 StartZ=0 EndX=-180.232 EndY=56.0891 EndZ=0
  constraints (10):
    c: Coincident(g1,g0)
    c: Coincident(g2,g1)
    c: Coincident(g3,g2)
    c: Coincident(g3,g0)
    c: Parallel(g1,g-5)
    c: Perpendicular(g-3,g0)
    c: Parallel(g2,g-6)
    c: Parallel(g3,g-4)
    c: Coincident(g0,g-5)
    c: Coincident(g2,g-6)
FEATURE [Part::Extrusion] Extrude008  label="Extrude buco oled"
  Base = -> Sketch012
  Dir = (0,-1,2e-16)
  DirMode = 2
  FaceMakerClass = Part::FaceMakerBullseye
  FaceMakerMode = 3
  LengthFwd = 12.8
  LengthRev = 0
  Solid = true
  Symmetric = true
FEATURE [Sketcher::SketchObject] Sketch013  label="buco pompa"
  ArcFitTolerance = 1e-06
  AttachmentSupport = -> [XZ_Plane]
  ExternalGeometry = -> [Sketch]
  FullyConstrained = true
  MakeInternals = false
  MapMode = 5
  Placement = pos=(0,0,0) rot=(1,0,0;1.5708rad)
  sketch-geometry (8):
    g0: LineSegment StartX=-82.8 StartY=-10.4 StartZ=0 EndX=-82.8 EndY=-9.6 EndZ=0
    g1: LineSegment StartX=-82.8 StartY=-9.6 StartZ=0 EndX=-67.9 EndY=-9.6 EndZ=0
    g2: LineSegment StartX=-67.9 StartY=-9.6 StartZ=0 EndX=-67.9 EndY=6 EndZ=0
    g3: LineSegment StartX=-67.9 StartY=6 StartZ=0 EndX=-65.9 EndY=6 EndZ=0
    g4: LineSegment StartX=-65.9 StartY=6 StartZ=0 EndX=-65.9 EndY=-1.7 EndZ=0
    g5: LineSegment StartX=-65.9 StartY=-1.7 StartZ=0 EndX=-57.2 EndY=-1.7 EndZ=0
    g6: LineSegment StartX=-57.2 StartY=-1.7 StartZ=0 EndX=-57.2 EndY=-10.4 EndZ=0
    g7: LineSegment StartX=-57.2 StartY=-10.4 StartZ=0 EndX=-82.8 EndY=-10.4 EndZ=0
  constraints (22):
    c: Vertical(g0)
    c: Coincident(g1,g0)
    c: Horizontal(g1)
    c: Coincident(g2,g1)
    c: Vertical(g2)
    c: Coincident(g3,g2)
    c: Horizontal(g3)
    c: Coincident(g4,g3)
    c: Vertical(g4)
    c: Coincident(g5,g4)
    c: Horizontal(g5)
    c: Coincident(g6,g5)
    c: Vertical(g6)
    c: Coincident(g7,g6)
    c: Coincident(g7,g0)
    c: DistanceY(g0,g0) = 0.8
    c: DistanceY(g6,g6) = 8.7
    c: DistanceX(g1,g1) = 14.9
    c: DistanceX(g3,g3) = 2
    c: Coincident(g0,g-4)
    c: DistanceY(g2,g-6) = 0
    c: Coincident(g6,g-5)
FEATURE [Part::Extrusion] Extrude009  label="Extrude buco pompa"
  Base = -> Sketch013
  Dir = (0,-1,2e-16)
  DirMode = 2
  FaceMakerClass = Part::FaceMakerBullseye
  FaceMakerMode = 3
  LengthFwd = 13.2
  LengthRev = 0
  Solid = true
  Symmetric = true
FEATURE [Sketcher::SketchObject] Sketch014  label="buco frontale"
  ArcFitTolerance = 1e-06
  AttachmentSupport = -> [XZ_Plane]
  ExternalGeometry = -> [Sketch]
  FullyConstrained = true
  MakeInternals = false
  MapMode = 5
  Placement = pos=(0,0,0) rot=(1,0,0;1.5708rad)
  sketch-geometry (10):
    g0: LineSegment StartX=0 StartY=0 StartZ=0 EndX=0 EndY=24.671 EndZ=0
    g1: LineSegment StartX=0 StartY=24.671 StartZ=0 EndX=-4 EndY=24.671 EndZ=0
    g2: LineSegment StartX=-4 StartY=24.671 StartZ=0 EndX=-4 EndY=16 EndZ=0
    g3: LineSegment StartX=-4 StartY=16 StartZ=0 EndX=-2.4 EndY=16 EndZ=0
    g4: LineSegment StartX=-2.4 StartY=16 StartZ=0 EndX=-2.4 EndY=10 EndZ=0
    g5: LineSegment StartX=-2.4 StartY=10 StartZ=0 EndX=-12 EndY=10 EndZ=0
    g6: LineSegment StartX=-12 StartY=10 StartZ=0 EndX=-12 EndY=6 EndZ=0
    g7: LineSegment StartX=-12 StartY=6 StartZ=0 EndX=-2.4 EndY=6 EndZ=0
    g8: LineSegment StartX=-2.4 StartY=6 StartZ=0 EndX=-2.4 EndY=0 EndZ=0
    g9: LineSegment StartX=-2.4 StartY=0 StartZ=0 EndX=0 EndY=0 EndZ=0
  constraints (29):
    c: Vertical(g0)
    c: Coincident(g1,g0)
    c: Horizontal(g1)
    c: Coincident(g2,g1)
    c: Vertical(g2)
    c: Coincident(g3,g2)
    c: Horizontal(g3)
    c: Coincident(g4,g3)
    c: Vertical(g4)
    c: Coincident(g5,g4)
    c: Horizontal(g5)
    c: Coincident(g6,g5)
    c: Vertical(g6)
    c: Coincident(g7,g6)
    c: Coincident(g8,g7)
    c: Vertical(g8)
    c: Coincident(g9,g8)
    c: Coincident(g9,g0)
    c: Horizontal(g9)
    c: DistanceY(g0,g0) = 24.671
    c: Horizontal(g7)
    c: DistanceY(g6,g6) = 4
    c: DistanceY(g4,g4) = 6
    c: DistanceX(g9,g9) = 2.4
    c: Coincident(g0,g-1)
    c: DistanceY(g-3,g7) = 0
    c: DistanceX(g8,g4) = 0
    c: DistanceX(g-3,g1) = 0
    c: DistanceX(g6,g-3) = 8
FEATURE [Part::Extrusion] Extrude010  label="Extrude buco frontale"
  Base = -> Sketch014
  Dir = (0,-1,2e-16)
  DirMode = 2
  FaceMakerClass = Part::FaceMakerBullseye
  FaceMakerMode = 3
  LengthFwd = 11.2
  LengthRev = 0
  Solid = true
  Symmetric = true
FEATURE [Sketcher::SketchObject] Sketch015  label="guida rail"
  ArcFitTolerance = 1e-06
  AttachmentSupport = -> [XZ_Plane]
  ExternalGeometry = -> [Sketch]
  FullyConstrained = true
  MakeInternals = false
  MapMode = 5
  Placement = pos=(0,0,0) rot=(1,0,0;1.5708rad)
  sketch-geometry (4):
    g0: LineSegment StartX=-100.8 StartY=43.2 StartZ=0 EndX=-44.6 EndY=43.2 EndZ=0
    g1: LineSegment StartX=-44.6 StartY=43.2 StartZ=0 EndX=-44.6 EndY=41.2 EndZ=0
    g2: LineSegment StartX=-44.6 StartY=41.2 StartZ=0 EndX=-100.8 EndY=41.2 EndZ=0
    g3: LineSegment StartX=-100.8 StartY=41.2 StartZ=0 EndX=-100.8 EndY=43.2 EndZ=0
  constraints (9):
    c: Horizontal(g0)
    c: Coincident(g1,g0)
    c: Coincident(g2,g1)
    c: Coincident(g3,g2)
    c: Coincident(g3,g0)
    c: Vertical(g3)
    c: Coincident(g2,g-3)
    c: Coincident(g1,g-3)
    c: Coincident(g0,g-4)
FEATURE [Part::Extrusion] Extrude011  label="Extrude guida rail"
  Base = -> Sketch015
  Dir = (0,-1,2e-16)
  DirMode = 2
  FaceMakerClass = Part::FaceMakerBullseye
  FaceMakerMode = 3
  LengthFwd = 9
  LengthRev = 0
  Solid = true
  Symmetric = true
FEATURE [Sketcher::SketchObject] Sketch016  label="guide per coperture laterali"
  ArcFitTolerance = 1e-06
  AttachmentSupport = -> [XZ_Plane]
  ExternalGeometry = -> [Sketch]
  FullyConstrained = true
  MakeInternals = false
  MapMode = 5
  Placement = pos=(0,0,0) rot=(1,0,0;1.5708rad)
  sketch-geometry (14):
    g0: Circle CenterX=-5.6 CenterY=7.6 CenterZ=0 NormalX=0 NormalY=0 NormalZ=1 AngleXU=0 Radius=1.6
    g1: Circle CenterX=-5.6 CenterY=7.6 CenterZ=0 NormalX=0 NormalY=0 NormalZ=1 AngleXU=0 Radius=4
    g2: Circle CenterX=-5.6 CenterY=34.8 CenterZ=0 NormalX=0 NormalY=0 NormalZ=1 AngleXU=0 Radius=1.6
    g3: Circle CenterX=-5.6 CenterY=34.8 CenterZ=0 NormalX=0 NormalY=0 NormalZ=1 AngleXU=0 Radius=4
    g4: Circle CenterX=-184.08 CenterY=34.8 CenterZ=0 NormalX=0 NormalY=0 NormalZ=1 AngleXU=0 Radius=1.6
    g5: Circle CenterX=-184.08 CenterY=34.8 CenterZ=0 NormalX=0 NormalY=0 NormalZ=1 AngleXU=0 Radius=4
    g6: Circle CenterX=-179.305 CenterY=-76.8316 CenterZ=0 NormalX=0 NormalY=0 NormalZ=1 AngleXU=0 Radius=1.6
    g7: Circle CenterX=-179.305 CenterY=-76.8316 CenterZ=0 NormalX=0 NormalY=0 NormalZ=1 AngleXU=0 Radius=4
    g8: Circle CenterX=-213.443 CenterY=-76.8316 CenterZ=0 NormalX=0 NormalY=0 NormalZ=1 AngleXU=0 Radius=1.6
    g9: Circle CenterX=-213.443 CenterY=-76.8316 CenterZ=0 NormalX=0 NormalY=0 NormalZ=1 AngleXU=0 Radius=4
    g10: Circle CenterX=-78.51 CenterY=7.6 CenterZ=0 NormalX=0 NormalY=0 NormalZ=1 AngleXU=0 Radius=1.6
    g11: Circle CenterX=-78.51 CenterY=7.6 CenterZ=0 NormalX=0 NormalY=0 NormalZ=1 AngleXU=0 Radius=4
    g12: Circle CenterX=-78.51 CenterY=34.8 CenterZ=0 NormalX=0 NormalY=0 NormalZ=1 AngleXU=0 Radius=1.6
    g13: Circle CenterX=-78.51 CenterY=34.8 CenterZ=0 NormalX=0 NormalY=0 NormalZ=1 AngleXU=0 Radius=4
  constraints (35):
    c: Diameter(g0) = 3.2
    c: Diameter(g1) = 8
    c: Coincident(g0,g1)
    c: Diameter(g2) = 3.2
    c: Diameter(g3) = 8
    c: Coincident(g3,g2)
    c: Tangent(g2,g-7)
    c: Diameter(g4) = 3.2
    c: Diameter(g5) = 8
    c: Coincident(g5,g4)
    c: Tangent(g4,g-7)
    c: Tangent(g4,g-8)
    c: Diameter(g6) = 3.2
    c: Diameter(g7) = 8
    c: Coincident(g7,g6)
    c: Tangent(g6,g-9)
    c: Tangent(g6,g-10)
    c: Diameter(g8) = 3.2
    c: Diameter(g9) = 8
    c: Coincident(g9,g8)
    c: Tangent(g8,g-10)
    c: Tangent(g8,g-11)
    c: Diameter(g10) = 3.2
    c: Diameter(g11) = 8
    c: Diameter(g12) = 3.2
    c: Diameter(g13) = 8
    c: Coincident(g12,g13)
    c: Coincident(g10,g11)
    c: Tangent(g12,g-7)
    c: DistanceX(g12,g10) = 0
    c: Tangent(g2,g-6)
    c: Tangent(g0,g-6)
    c: Tangent(g0,g-3)
    c: Tangent(g10,g-3)
    c: Tangent(g10,g-4)
FEATURE [Part::Extrusion] Extrude012  label="extrude guide per coperture laterali"
  Base = -> Sketch016
  Dir = (0,-1,2e-16)
  DirMode = 2
  FaceMakerClass = Part::FaceMakerBullseye
  FaceMakerMode = 3
  LengthFwd = 25.2
  LengthRev = 0
  Solid = true
  Symmetric = true
FEATURE [Sketcher::SketchObject] Sketch017  label="supporto CAM"
  ArcFitTolerance = 1e-06
  AttachmentSupport = -> [XZ_Plane]
  ExternalGeometry = -> [Sketch]
  FullyConstrained = true
  MakeInternals = false
  MapMode = 5
  Placement = pos=(0,0,0) rot=(1,0,0;1.5708rad)
  sketch-geometry (6):
    g0: LineSegment StartX=-2.4 StartY=48 StartZ=0 EndX=-2.4 EndY=41.2 EndZ=0
    g1: LineSegment StartX=-2.4 StartY=48 StartZ=0 EndX=-34 EndY=48 EndZ=0
    g2: LineSegment StartX=-34 StartY=48 StartZ=0 EndX=-34 EndY=46.72 EndZ=0
    g3: LineSegment StartX=-34 StartY=46.72 StartZ=0 EndX=-36 EndY=46.72 EndZ=0
    g4: LineSegment StartX=-36 StartY=46.72 StartZ=0 EndX=-36 EndY=41.2 EndZ=0
    g5: LineSegment StartX=-36 StartY=41.2 StartZ=0 EndX=-2.4 EndY=41.2 EndZ=0
  constraints (15):
    c: Coincident(g1,g0)
    c: Horizontal(g1)
    c: Coincident(g2,g1)
    c: Vertical(g2)
    c: Coincident(g3,g2)
    c: Horizontal(g3)
    c: Coincident(g4,g3)
    c: Coincident(g5,g4)
    c: DistanceX(g1,g0) = 31.6
    c: Coincident(g5,g0)
    c: Vertical(g4)
    c: DistanceY(g2,g1) = 1.28
    c: Coincident(g0,g-3)
    c: Coincident(g0,g-3)
    c: Coincident(g4,g-4)
FEATURE [Part::Extrusion] Extrude013  label="Extrude supporto CAM"
  Base = -> Sketch017
  Dir = (0,-1,2e-16)
  DirMode = 2
  FaceMakerClass = Part::FaceMakerBullseye
  FaceMakerMode = 3
  LengthFwd = 17.8
  LengthRev = 0
  Solid = true
  Symmetric = true
FEATURE [Sketcher::SketchObject] Sketch018  label="Scavo CAM"
  ArcFitTolerance = 1e-06
  AttachmentSupport = -> [YZ_Plane]
  ExternalGeometry = -> [Sketch]
  FullyConstrained = true
  MakeInternals = false
  MapMode = 5
  Placement = pos=(0,0,0) rot=(0.57735,0.57735,0.57735;2.0944rad)
  sketch-geometry (4):
    g0: LineSegment StartX=-7.73 StartY=48 StartZ=0 EndX=7.73 EndY=48 EndZ=0
    g1: LineSegment [constr] StartX=1.07e-14 StartY=48 StartZ=0 EndX=0 EndY=43.5155 EndZ=0
    g2: ArcOfCircle CenterX=9e-15 CenterY=52.42 CenterZ=0 NormalX=0 NormalY=0 NormalZ=1 AngleXU=0 Radius=8.90445 StartAngle=3.66102 EndAngle=5.76376
    g3: Circle [constr] CenterX=9e-15 CenterY=52.42 CenterZ=0 NormalX=0 NormalY=0 NormalZ=1 AngleXU=0 Radius=8.9
  constraints (13):
    c: Horizontal(g0)
    c: DistanceY(g-3,g0) = 0
    c: DistanceX(g0,g0) = 15.46
    c: DistanceX(g0,g-3) = 7.73
    c: DistanceX(g-3) = 0
    c: Coincident(g1,g-3)
    c: PointOnObject(g1,g-2)
    c: Coincident(g2,g0)
    c: Coincident(g2,g0)
    c: PointOnObject(g1,g2)
    c: Diameter(g3) = 17.8
    c: DistanceY(g1,g3) = 4.42
    c: Coincident(g2,g3)
FEATURE [Part::Extrusion] Extrude014  label="Extrude Scavo CAM"
  Base = -> Sketch018
  Dir = (1,0,0)
  DirMode = 2
  FaceMakerClass = Part::FaceMakerBullseye
  FaceMakerMode = 3
  LengthFwd = -34
  LengthRev = 0
  Solid = true
  Symmetric = false
FEATURE [Sketcher::SketchObject] Sketch019  label="scavo rumble"
  ArcFitTolerance = 1e-06
  AttachmentSupport = -> [XZ_Plane]
  ExternalGeometry = -> [Sketch]
  FullyConstrained = true
  MakeInternals = false
  MapMode = 5
  Placement = pos=(0,0,0) rot=(1,0,0;1.5708rad)
  sketch-geometry (6):
    g0: LineSegment StartX=-168.716 StartY=-37.1227 StartZ=0 EndX=-163.58 EndY=-38.7914 EndZ=0
    g1: LineSegment StartX=-163.58 StartY=-38.7914 StartZ=0 EndX=-170.687 EndY=-60.6657 EndZ=0
    g2: LineSegment StartX=-170.687 StartY=-60.6657 StartZ=0 EndX=-175.823 EndY=-58.997 EndZ=0
    g3: LineSegment StartX=-175.823 StartY=-58.997 StartZ=0 EndX=-168.716 EndY=-37.1227 EndZ=0
    g4: LineSegment [constr] StartX=-145.51 StartY=22 StartZ=0 EndX=-165.102 EndY=-38.297 EndZ=0
    g5: LineSegment [constr] StartX=-163.58 StartY=-38.7914 StartZ=0 EndX=-165.102 EndY=-38.297 EndZ=0
  constraints (17):
    c: Coincident(g1,g0)
    c: Coincident(g2,g1)
    c: Coincident(g3,g2)
    c: Coincident(g3,g0)
    c: Parallel(g3,g-3)
    c: Parallel(g3,g1)
    c: Perpendicular(g3,g0)
    c: Perpendicular(g2,g3)
    c: Distance(g2,g0) = 23
    c: Parallel(g4,g-3)
    c: Distance(g4) = 63.4
    c: Coincident(g4,g-3)
    c: Parallel(g5,g0)
    c: Coincident(g5,g0)
    c: Coincident(g5,g4)
    c: Distance(g4,g0) = 3.8
    c: Distance(g4,g0) = 1.6
FEATURE [Part::Extrusion] Extrude015  label="scavo rumble001"
  Base = -> Sketch019
  Dir = (0,-1,2e-16)
  DirMode = 2
  FaceMakerClass = Part::FaceMakerBullseye
  FaceMakerMode = 3
  LengthFwd = 21
  LengthRev = 0
  Solid = true
  Symmetric = true
FEATURE [Sketcher::SketchObject] Sketch020  label="fermo rumble"
  ArcFitTolerance = 1e-06
  AttachmentSupport = -> [XZ_Plane]
  ExternalGeometry = -> [Sketch019,Sketch]
  FullyConstrained = true
  MakeInternals = false
  MapMode = 5
  Placement = pos=(0,0,0) rot=(1,0,0;1.5708rad)
  sketch-geometry (16):
    g0: LineSegment [constr] StartX=-170.849 StartY=-55.9866 StartZ=0 EndX=-172.209 EndY=-60.1713 EndZ=0
    g1: LineSegment [constr] StartX=-172.209 StartY=-60.1713 StartZ=0 EndX=-170.687 EndY=-60.6657 EndZ=0
    g2: LineSegment StartX=-172.262 StartY=-53.2145 StartZ=0 EndX=-170.17 EndY=-53.8943 EndZ=0
    g3: LineSegment StartX=-170.17 StartY=-53.8943 StartZ=0 EndX=-170.849 EndY=-55.9866 EndZ=0
    g4: LineSegment StartX=-170.849 StartY=-55.9866 StartZ=0 EndX=-172.942 EndY=-55.3068 EndZ=0
    g5: LineSegment StartX=-172.942 StartY=-55.3068 StartZ=0 EndX=-172.262 EndY=-53.2145 EndZ=0
    g6: LineSegment StartX=-171.767 StartY=-51.6928 StartZ=0 EndX=-168.344 EndY=-52.8052 EndZ=0
    g7: LineSegment StartX=-168.344 StartY=-52.8052 StartZ=0 EndX=-169.951 EndY=-57.7507 EndZ=0
    g8: LineSegment StartX=-169.951 StartY=-57.7507 StartZ=0 EndX=-173.374 EndY=-56.6383 EndZ=0
    g9: LineSegment StartX=-174.402 StartY=-54.6222 StartZ=0 EndX=-173.784 EndY=-52.72 EndZ=0
    g10: LineSegment [constr] StartX=-173.784 StartY=-52.72 StartZ=0 EndX=-173.289 EndY=-51.1984 EndZ=0
    g11: LineSegment [constr] StartX=-173.289 StartY=-51.1984 StartZ=0 EndX=-171.767 EndY=-51.6928 EndZ=0
    g12: ArcOfCircle CenterX=-172.88 CenterY=-55.1166 CenterZ=0 NormalX=0 NormalY=0 NormalZ=1 AngleXU=0 Radius=1.6 StartAngle=2.82743 EndAngle=4.39823
    g13: GeomPoint [constr] X=-174.896 Y=-56.1438 Z=0
    g14: ArcOfCircle CenterX=-172.262 CenterY=-53.2145 CenterZ=0 NormalX=0 NormalY=0 NormalZ=1 AngleXU=0 Radius=1.6 StartAngle=1.25664 EndAngle=2.82743
    g15: GeomPoint [constr] X=-173.289 Y=-51.1984 Z=0
  constraints (42):
    c: Parallel(g0,g-4)
    c: Distance(g0) = 4.4
    c: Coincident(g1,g0)
    c: Perpendicular(g0,g1)
    c: Distance(g1) = 1.6
    c: Coincident(g1,g-5)
    c: Coincident(g3,g2)
    c: Coincident(g4,g3)
    c: Coincident(g5,g4)
    c: Coincident(g5,g2)
    c: Parallel(g3,g-4)
    c: Parallel(g3,g5)
    c: Perpendicular(g2,g3)
    c: Parallel(g4,g2)
    c: Distance(g2) = 2.2
    c: Distance(g3) = 2.2
    c: Coincident(g7,g6)
    c: Coincident(g8,g7)
    c: Parallel(g7,g-4)
    c: Parallel(g7,g9)
    c: Perpendicular(g6,g7)
    c: Parallel(g6,g8)
    c: Distance(g6,g15) = 5.2
    c: Distance(g7) = 5.2
    c: Coincident(g11,g10)
    c: Parallel(g10,g9)
    c: Parallel(g11,g6)
    c: Distance(g10) = 1.6
    c: Distance(g11) = 1.6
    c: Coincident(g10,g15)
    c: Distance(g11,g2) = 1.6
    c: Distance(g2,g10) = 1.6
    c: PointOnObject(g13,g8)
    c: PointOnObject(g13,g9)
    c: Tangent(g8,g12) = 1.5708
    c: Tangent(g9,g12) = 1.5708
    c: PointOnObject(g15,g9)
    c: Tangent(g6,g14) = 1.5708
    c: Tangent(g9,g14) = 1.5708
    c: Equal(g12,g14)
    c: Coincident(g6,g11)
    c: Coincident(g3,g0)
FEATURE [Part::Extrusion] Extrude016  label="Extrude fermo rumble"
  Base = -> Sketch020
  Dir = (0,-1,2e-16)
  DirMode = 2
  FaceMakerClass = Part::FaceMakerBullseye
  FaceMakerMode = 3
  LengthFwd = 25.2
  LengthRev = 0
  Solid = true
  Symmetric = true
FEATURE [Sketcher::SketchObject] Sketch021  label="perno fermo rumble001"
  ArcFitTolerance = 1e-06
  AttachmentSupport = -> [XZ_Plane001]
  FullyConstrained = true
  MakeInternals = false
  MapMode = 5
  Placement = pos=(0,0,0) rot=(1,0,0;1.5708rad)
  sketch-geometry (16):
    g0: LineSegment StartX=0 StartY=0.45 StartZ=0 EndX=0 EndY=1.55 EndZ=0
    g1: LineSegment StartX=0.45 StartY=2 StartZ=0 EndX=1.55 EndY=2 EndZ=0
    g2: LineSegment StartX=2 StartY=1.55 StartZ=0 EndX=2 EndY=0.45 EndZ=0
    g3: LineSegment StartX=1.55 StartY=0 StartZ=0 EndX=0.45 EndY=0 EndZ=0
    g4: ArcOfCircle [constr] CenterX=0.45 CenterY=1.55 CenterZ=0 NormalX=0 NormalY=0 NormalZ=1 AngleXU=0 Radius=0.45 StartAngle=1.5708 EndAngle=3.14159
    g5: GeomPoint [constr] X=0 Y=2 Z=0
    g6: LineSegment StartX=0.45 StartY=2 StartZ=0 EndX=0 EndY=1.55 EndZ=0
    g7: ArcOfCircle [constr] CenterX=1.55 CenterY=1.55 CenterZ=0 NormalX=0 NormalY=0 NormalZ=1 AngleXU=0 Radius=0.45 StartAngle=0 EndAngle=1.5708
    g8: GeomPoint [constr] X=2 Y=2 Z=0
    g9: LineSegment StartX=2 StartY=1.55 StartZ=0 EndX=1.55 EndY=2 EndZ=0
    g10: ArcOfCircle [constr] CenterX=1.55 CenterY=0.45 CenterZ=0 NormalX=0 NormalY=0 NormalZ=1 AngleXU=0 Radius=0.45 StartAngle=4.71239 EndAngle=6.28319
    g11: GeomPoint [constr] X=2 Y=0 Z=0
    g12: LineSegment StartX=1.55 StartY=0 StartZ=0 EndX=2 EndY=0.45 EndZ=0
    g13: ArcOfCircle [constr] CenterX=0.45 CenterY=0.45 CenterZ=0 NormalX=0 NormalY=0 NormalZ=1 AngleXU=0 Radius=0.45 StartAngle=3.14159 EndAngle=4.71239
    g14: GeomPoint [constr] X=0 Y=0 Z=0
    g15: LineSegment StartX=0 StartY=0.45 StartZ=0 EndX=0.45 EndY=0 EndZ=0
  constraints (35):
    c: Coincident(g14,g-1)
    c: PointOnObject(g5,g-2)
    c: Horizontal(g1)
    c: Vertical(g2)
    c: Horizontal(g3)
    c: DistanceX(g5,g8) = 2
    c: DistanceY(g11,g8) = 2
    c: PointOnObject(g5,g0)
    c: PointOnObject(g5,g1)
    c: Tangent(g0,g4) = 1.5708
    c: Tangent(g1,g4) = 1.5708
    c: Coincident(g6,g0)
    c: Coincident(g6,g1)
    c: PointOnObject(g8,g2)
    c: PointOnObject(g8,g1)
    c: Tangent(g2,g7) = 1.5708
    c: Tangent(g1,g7) = 1.5708
    c: Coincident(g9,g2)
    c: Coincident(g9,g1)
    c: PointOnObject(g11,g2)
    c: PointOnObject(g11,g3)
    c: Tangent(g2,g10) = 1.5708
    c: Tangent(g3,g10) = 1.5708
    c: Coincident(g12,g2)
    c: Coincident(g12,g3)
    c: PointOnObject(g14,g0)
    c: PointOnObject(g14,g3)
    c: Tangent(g0,g13) = 1.5708
    c: Tangent(g3,g13) = 1.5708
    c: Coincident(g15,g0)
    c: Coincident(g15,g3)
    c: Equal(g6,g9)
    c: Equal(g9,g12)
    c: Equal(g12,g15)
    c: DistanceX(g14,g3) = 0.45
FEATURE [Sketcher::SketchObject] Sketch022  label="fori per M3x5(OD)x6(L)"
  ArcFitTolerance = 1e-06
  AttachmentSupport = -> [XZ_Plane]
  ExternalGeometry = -> [Sketch016]
  FullyConstrained = true
  MakeInternals = false
  MapMode = 5
  Placement = pos=(0,0,0) rot=(1,0,0;1.5708rad)
  sketch-geometry (7):
    g0: Circle CenterX=-5.6 CenterY=34.8 CenterZ=0 NormalX=0 NormalY=0 NormalZ=1 AngleXU=0 Radius=2.5
    g1: Circle CenterX=-5.6 CenterY=7.6 CenterZ=0 NormalX=0 NormalY=0 NormalZ=1 AngleXU=0 Radius=2.5
    g2: Circle CenterX=-78.51 CenterY=34.8 CenterZ=0 NormalX=0 NormalY=0 NormalZ=1 AngleXU=0 Radius=2.5
    g3: Circle CenterX=-78.51 CenterY=7.6 CenterZ=0 NormalX=0 NormalY=0 NormalZ=1 AngleXU=0 Radius=2.5
    g4: Circle CenterX=-184.08 CenterY=34.8 CenterZ=0 NormalX=0 NormalY=0 NormalZ=1 AngleXU=0 Radius=2.5
    g5: Circle CenterX=-179.305 CenterY=-76.8316 CenterZ=0 NormalX=0 NormalY=0 NormalZ=1 AngleXU=0 Radius=2.5
    g6: Circle CenterX=-213.443 CenterY=-76.8316 CenterZ=0 NormalX=0 NormalY=0 NormalZ=1 AngleXU=0 Radius=2.5
  constraints (14):
    c: Diameter(g0) = 5
    c: Diameter(g1) = 5
    c: Diameter(g2) = 5
    c: Diameter(g3) = 5
    c: Diameter(g4) = 5
    c: Diameter(g5) = 5
    c: Diameter(g6) = 5
    c: Coincident(g0,g-8)
    c: Coincident(g1,g-9)
    c: Coincident(g2,g-6)
    c: Coincident(g3,g-7)
    c: Coincident(g4,g-5)
    c: Coincident(g5,g-4)
    c: Coincident(g6,g-3)
FEATURE [Part::Extrusion] Extrude018  label="Extrude fori M3x5x6 - dx"
  Base = -> Sketch022
  Dir = (0,-1,2e-16)
  DirMode = 2
  FaceMakerClass = Part::FaceMakerBullseye
  FaceMakerMode = 3
  LengthFwd = 6.2
  LengthRev = 0
  Placement = pos=(0,-9.5,0) rot=(0,0,1;0rad)
  Solid = true
  Symmetric = true
FEATURE [Part::Extrusion] Extrude019  label="Extrude fori M3x5x6 - sx"
  Base = -> Sketch022
  Dir = (0,-1,2e-16)
  DirMode = 2
  FaceMakerClass = Part::FaceMakerBullseye
  FaceMakerMode = 3
  LengthFwd = 6.2
  LengthRev = 0
  Placement = pos=(0,9.5,0) rot=(0,0,1;0rad)
  Solid = true
  Symmetric = true
FEATURE [Sketcher::SketchObject] Sketch023  label="foro anteriore M3x5x6"
  ArcFitTolerance = 1e-06
  AttachmentSupport = -> [YZ_Plane]
  FullyConstrained = true
  MakeInternals = false
  MapMode = 5
  Placement = pos=(0,0,0) rot=(0.57735,0.57735,0.57735;2.0944rad)
  sketch-geometry (2):
    g0: LineSegment [constr] StartX=0 StartY=0 StartZ=0 EndX=0 EndY=38.6 EndZ=0
    g1: Circle CenterX=0 CenterY=38.6 CenterZ=0 NormalX=0 NormalY=0 NormalZ=1 AngleXU=0 Radius=2.5
  constraints (5):
    c: Coincident(g0,g-1)
    c: PointOnObject(g0,g-2)
    c: DistanceY(g0,g0) = 38.6
    c: Diameter(g1) = 5
    c: Coincident(g1,g0)
FEATURE [Part::Extrusion] Extrude020  label="Extrude foro anteriore M3x5x6"
  Base = -> Sketch023
  Dir = (1,0,0)
  DirMode = 2
  FaceMakerClass = Part::FaceMakerBullseye
  FaceMakerMode = 3
  LengthFwd = -6.2
  LengthRev = 0
  Solid = true
  Symmetric = false
FEATURE [Sketcher::SketchObject] Sketch024  label="fori per viti frontale"
  ArcFitTolerance = 1e-06
  AttachmentSupport = -> [YZ_Plane]
  FullyConstrained = true
  MakeInternals = false
  MapMode = 5
  Placement = pos=(0,0,0) rot=(0.57735,0.57735,0.57735;2.0944rad)
  sketch-geometry (9):
    g0: LineSegment [constr] StartX=-10.3 StartY=30.721 StartZ=0 EndX=10.3 EndY=30.721 EndZ=0
    g1: LineSegment [constr] StartX=10.3 StartY=30.721 StartZ=0 EndX=10.3 EndY=10.121 EndZ=0
    g2: LineSegment [constr] StartX=10.3 StartY=10.121 StartZ=0 EndX=-10.3 EndY=10.121 EndZ=0
    g3: LineSegment [constr] StartX=-10.3 StartY=10.121 StartZ=0 EndX=-10.3 EndY=30.721 EndZ=0
    g4: LineSegment [constr] StartX=0 StartY=0 StartZ=0 EndX=0 EndY=10.121 EndZ=0
    g5: Circle CenterX=-10.3 CenterY=30.721 CenterZ=0 NormalX=0 NormalY=0 NormalZ=1 AngleXU=0 Radius=2
    g6: Circle CenterX=10.3 CenterY=30.721 CenterZ=0 NormalX=0 NormalY=0 NormalZ=1 AngleXU=0 Radius=2
    g7: Circle CenterX=-10.3 CenterY=10.121 CenterZ=0 NormalX=0 NormalY=0 NormalZ=1 AngleXU=0 Radius=2
    g8: Circle CenterX=10.3 CenterY=10.121 CenterZ=0 NormalX=0 NormalY=0 NormalZ=1 AngleXU=0 Radius=2
  constraints (22):
    c: Horizontal(g0)
    c: Coincident(g1,g0)
    c: Vertical(g1)
    c: Coincident(g2,g1)
    c: Horizontal(g2)
    c: Coincident(g3,g2)
    c: Coincident(g3,g0)
    c: Vertical(g3)
    c: DistanceX(g0,g0) = 20.6
    c: DistanceY(g3,g3) = 20.6
    c: Coincident(g4,g-1)
    c: PointOnObject(g4,g-2)
    c: DistanceY(g4,g4) = 10.121
    c: Symmetric(g2,g2,g4)
    c: Diameter(g5) = 4
    c: Diameter(g6) = 4
    c: Diameter(g7) = 4
    c: Diameter(g8) = 4
    c: Coincident(g5,g0)
    c: Coincident(g6,g0)
    c: Coincident(g7,g2)
    c: Coincident(g8,g1)
FEATURE [Part::Extrusion] Extrude021  label="Extrude fori per viti frontale"
  Base = -> Sketch024
  Dir = (1,0,0)
  DirMode = 2
  FaceMakerClass = Part::FaceMakerBullseye
  FaceMakerMode = 3
  LengthFwd = -2.4
  LengthRev = 0
  Solid = true
  Symmetric = false
FEATURE [Sketcher::SketchObject] Sketch025  label="foro per filo CAM"
  ArcFitTolerance = 1e-06
  AttachmentSupport = -> [XZ_Plane]
  ExternalGeometry = -> [Sketch]
  FullyConstrained = true
  MakeInternals = false
  MapMode = 5
  Placement = pos=(0,0,0) rot=(1,0,0;1.5708rad)
  sketch-geometry (4):
    g0: LineSegment StartX=-44.6 StartY=41.2 StartZ=0 EndX=-44.6 EndY=36.4 EndZ=0
    g1: LineSegment StartX=-44.6 StartY=36.4 StartZ=0 EndX=-54.6 EndY=36.4 EndZ=0
    g2: LineSegment StartX=-54.6 StartY=36.4 StartZ=0 EndX=-50.4 EndY=41.2 EndZ=0
    g3: LineSegment StartX=-50.4 StartY=41.2 StartZ=0 EndX=-44.6 EndY=41.2 EndZ=0
  constraints (11):
    c: Vertical(g0)
    c: Coincident(g1,g0)
    c: Horizontal(g1)
    c: Coincident(g2,g1)
    c: Coincident(g3,g2)
    c: Coincident(g3,g0)
    c: Horizontal(g3)
    c: Coincident(g0,g-3)
    c: DistanceY(g0,g-4) = 0
    c: DistanceX(g3,g3) = 5.8
    c: DistanceX(g1,g1) = 10
FEATURE [Part::Extrusion] Extrude022  label="Extrude foro per filo CAM dx"
  Base = -> Sketch025
  Dir = (0,-1,2e-16)
  DirMode = 2
  FaceMakerClass = Part::FaceMakerBullseye
  FaceMakerMode = 3
  LengthFwd = 4.9
  LengthRev = 0
  Placement = pos=(0,6.95,0) rot=(0,0,1;0rad)
  Solid = true
  Symmetric = true
FEATURE [Part::Extrusion] Extrude023  label="Extrude foro per filo CAM sx"
  Base = -> Sketch025
  Dir = (0,-1,2e-16)
  DirMode = 2
  FaceMakerClass = Part::FaceMakerBullseye
  FaceMakerMode = 3
  LengthFwd = 4.9
  LengthRev = 0
  Placement = pos=(0,-6.95,0) rot=(0,0,1;0rad)
  Solid = true
  Symmetric = true
FEATURE [Sketcher::SketchObject] Sketch026  label="foro sotto anteriore M3x5x6"
  ArcFitTolerance = 1e-06
  AttachmentSupport = -> [XY_Plane]
  FullyConstrained = true
  MakeInternals = false
  MapMode = 5
  sketch-geometry (2):
    g0: LineSegment [constr] StartX=0 StartY=0 StartZ=0 EndX=-16.5 EndY=0 EndZ=0
    g1: Circle CenterX=-16.5 CenterY=0 CenterZ=0 NormalX=0 NormalY=0 NormalZ=1 AngleXU=0 Radius=2.5
  constraints (5):
    c: Distance(g0) = 16.5
    c: Coincident(g0,g-1)
    c: PointOnObject(g0,g-1)
    c: Diameter(g1) = 5
    c: Coincident(g0,g1)
FEATURE [Sketcher::SketchObject] Sketch027  label="foro sotto posteriore M3x5x6"
  ArcFitTolerance = 1e-06
  AttachmentSupport = -> [XY_Plane]
  ExternalGeometry = -> [Sketch]
  FullyConstrained = true
  MakeInternals = false
  MapMode = 5
  sketch-geometry (2):
    g0: LineSegment [constr] StartX=-82.8 StartY=2e-16 StartZ=0 EndX=-71.3 EndY=2e-16 EndZ=0
    g1: Circle CenterX=-71.3 CenterY=2e-16 CenterZ=0 NormalX=0 NormalY=0 NormalZ=1 AngleXU=0 Radius=2.5
  constraints (5):
    c: Distance(g0) = 11.5
    c: Coincident(g0,g-3)
    c: PointOnObject(g0,g-3)
    c: Diameter(g1) = 5
    c: Coincident(g1,g0)
FEATURE [Sketcher::SketchObject] Sketch029  label="fori sotto impugnatura"
  ArcFitTolerance = 1e-06
  AttachmentSupport = -> [XY_Plane]
  ExternalGeometry = -> [Sketch]
  FullyConstrained = true
  MakeInternals = false
  MapMode = 5
  sketch-geometry (15):
    g0: LineSegment [constr] StartX=-175.232 StartY=-1.83e-14 StartZ=0 EndX=-191.232 EndY=0 EndZ=0
    g1: Circle CenterX=-191.232 CenterY=0 CenterZ=0 NormalX=0 NormalY=0 NormalZ=1 AngleXU=0 Radius=3.95
    g2: LineSegment [constr] StartX=-175.232 StartY=-1.83e-14 StartZ=0 EndX=-204.275 EndY=0 EndZ=0
    g3: LineSegment StartX=-204.275 StartY=3.525 StartZ=0 EndX=-204.275 EndY=-3.525 EndZ=0
    g4: LineSegment StartX=-205.4 StartY=-4.65 StartZ=0 EndX=-206.65 EndY=-4.65 EndZ=0
    g5: LineSegment StartX=-207.775 StartY=-3.525 StartZ=0 EndX=-207.775 EndY=3.525 EndZ=0
    g6: LineSegment StartX=-206.65 StartY=4.65 StartZ=0 EndX=-205.4 EndY=4.65 EndZ=0
    g7: ArcOfCircle CenterX=-206.65 CenterY=3.525 CenterZ=0 NormalX=0 NormalY=0 NormalZ=1 AngleXU=0 Radius=1.125 StartAngle=1.5708 EndAngle=3.14159
    g8: GeomPoint [constr] X=-207.775 Y=4.65 Z=0
    g9: ArcOfCircle CenterX=-205.4 CenterY=3.525 CenterZ=0 NormalX=0 NormalY=0 NormalZ=1 AngleXU=0 Radius=1.125 StartAngle=0 EndAngle=1.5708
    g10: GeomPoint [constr] X=-204.275 Y=4.65 Z=0
    g11: ArcOfCircle CenterX=-205.4 CenterY=-3.525 CenterZ=0 NormalX=0 NormalY=0 NormalZ=1 AngleXU=0 Radius=1.125 StartAngle=4.71239 EndAngle=6.28319
    g12: GeomPoint [constr] X=-204.275 Y=-4.65 Z=0
    g13: ArcOfCircle CenterX=-206.65 CenterY=-3.525 CenterZ=0 NormalX=0 NormalY=0 NormalZ=1 AngleXU=0 Radius=1.125 StartAngle=3.14159 EndAngle=4.71239
    g14: GeomPoint [constr] X=-207.775 Y=-4.65 Z=0
  constraints (35):
    c: Distance(g0) = 16
    c: Coincident(g0,g-3)
    c: PointOnObject(g0,g-1)
    c: Diameter(g1) = 7.9
    c: Coincident(g1,g0)
    c: Coincident(g2,g0)
    c: PointOnObject(g2,g-1)
    c: Vertical(g3)
    c: Horizontal(g4)
    c: Vertical(g5)
    c: Horizontal(g6)
    c: DistanceY(g12,g10) = 9.3
    c: DistanceX(g8,g10) = 3.5
    c: Symmetric(g10,g12,g2)
    c: PointOnObject(g8,g5)
    c: PointOnObject(g8,g6)
    c: Tangent(g5,g7) = 1.5708
    c: Tangent(g6,g7) = 1.5708
    c: PointOnObject(g10,g3)
    c: PointOnObject(g10,g6)
    c: Tangent(g3,g9) = 1.5708
    c: Tangent(g6,g9) = 1.5708
    c: PointOnObject(g12,g3)
    c: PointOnObject(g12,g4)
    c: Tangent(g3,g11) = 1.5708
    c: Tangent(g4,g11) = 1.5708
    c: PointOnObject(g14,g4)
    c: PointOnObject(g14,g5)
    c: Tangent(g4,g13) = 1.5708
    c: Tangent(g5,g13) = 1.5708
    c: Equal(g7,g9)
    c: Equal(g9,g11)
    c: Equal(g11,g13)
    c: DistanceX(g6,g6) = 1.25
    c: DistanceX(g-5,g5) = 6.8
FEATURE [Sketcher::SketchObject] Sketch030  label="fori superiori per solenoide e oled"
  ArcFitTolerance = 1e-06
  AttachmentSupport = -> [XY_Plane]
  ExternalGeometry = -> [Sketch]
  FullyConstrained = true
  MakeInternals = false
  MapMode = 5
  sketch-geometry (33):
    g0: LineSegment [constr] StartX=-181.6 StartY=1.12e-14 StartZ=0 EndX=-169.91 EndY=0 EndZ=0
    g1: LineSegment [constr] StartX=-169.91 StartY=0 StartZ=0 EndX=-169.91 EndY=-2.6 EndZ=0
    g2: LineSegment [constr] StartX=-169.91 StartY=0 StartZ=0 EndX=-169.91 EndY=2.6 EndZ=0
    g3: LineSegment StartX=-169.91 StartY=4.975 StartZ=0 EndX=-169.91 EndY=8.225 EndZ=0
    g4: LineSegment StartX=-167.535 StartY=10.6 StartZ=0 EndX=-167.285 EndY=10.6 EndZ=0
    g5: LineSegment StartX=-164.91 StartY=8.225 StartZ=0 EndX=-164.91 EndY=4.975 EndZ=0
    g6: LineSegment StartX=-167.285 StartY=2.6 StartZ=0 EndX=-167.535 EndY=2.6 EndZ=0
    g7: LineSegment StartX=-169.91 StartY=-4.975 StartZ=0 EndX=-169.91 EndY=-8.225 EndZ=0
    g8: LineSegment StartX=-167.535 StartY=-10.6 StartZ=0 EndX=-167.285 EndY=-10.6 EndZ=0
    g9: LineSegment StartX=-164.91 StartY=-8.225 StartZ=0 EndX=-164.91 EndY=-4.975 EndZ=0
    g10: LineSegment StartX=-167.285 StartY=-2.6 StartZ=0 EndX=-167.535 EndY=-2.6 EndZ=0
    g11: ArcOfCircle CenterX=-167.535 CenterY=8.225 CenterZ=0 NormalX=0 NormalY=0 NormalZ=1 AngleXU=0 Radius=2.375 StartAngle=1.5708 EndAngle=3.14159
    g12: GeomPoint [constr] X=-169.91 Y=10.6 Z=0
    g13: ArcOfCircle CenterX=-167.285 CenterY=8.225 CenterZ=0 NormalX=0 NormalY=0 NormalZ=1 AngleXU=0 Radius=2.375 StartAngle=0 EndAngle=1.5708
    g14: GeomPoint [constr] X=-164.91 Y=10.6 Z=0
    g15: ArcOfCircle CenterX=-167.285 CenterY=4.975 CenterZ=0 NormalX=0 NormalY=0 NormalZ=1 AngleXU=0 Radius=2.375 StartAngle=4.71239 EndAngle=6.28319
    g16: GeomPoint [constr] X=-164.91 Y=2.6 Z=0
    g17: ArcOfCircle CenterX=-167.535 CenterY=4.975 CenterZ=0 NormalX=0 NormalY=0 NormalZ=1 AngleXU=0 Radius=2.375 StartAngle=3.14159 EndAngle=4.71239
    g18: GeomPoint [constr] X=-169.91 Y=2.6 Z=0
    g19: ArcOfCircle CenterX=-167.535 CenterY=-4.975 CenterZ=0 NormalX=0 NormalY=0 NormalZ=1 AngleXU=0 Radius=2.375 StartAngle=1.5708 EndAngle=3.14159
    g20: GeomPoint [constr] X=-169.91 Y=-2.6 Z=0
    g21: ArcOfCircle CenterX=-167.285 CenterY=-4.975 CenterZ=0 NormalX=0 NormalY=0 NormalZ=1 AngleXU=0 Radius=2.375 StartAngle=0 EndAngle=1.5708
    g22: GeomPoint [constr] X=-164.91 Y=-2.6 Z=0
    g23: ArcOfCircle CenterX=-167.285 CenterY=-8.225 CenterZ=0 NormalX=0 NormalY=0 NormalZ=1 AngleXU=0 Radius=2.375 StartAngle=4.71239 EndAngle=6.28319
    g24: GeomPoint [constr] X=-164.91 Y=-10.6 Z=0
    g25: ArcOfCircle CenterX=-167.535 CenterY=-8.225 CenterZ=0 NormalX=0 NormalY=0 NormalZ=1 AngleXU=0 Radius=2.375 StartAngle=3.14159 EndAngle=4.71239
    g26: GeomPoint [constr] X=-169.91 Y=-10.6 Z=0
    g27: LineSegment [constr] StartX=-181.6 StartY=1.12e-14 StartZ=0 EndX=-152.209 EndY=0 EndZ=0
    g28: LineSegment [constr] StartX=-181.6 StartY=1.12e-14 StartZ=0 EndX=-130.41 EndY=0 EndZ=0
    g29: LineSegment [constr] StartX=-152.209 StartY=0 StartZ=0 EndX=-152.209 EndY=6.95 EndZ=0
    g30: LineSegment [constr] StartX=-130.41 StartY=0 StartZ=0 EndX=-130.41 EndY=-6.95 EndZ=0
    g31: Circle CenterX=-152.209 CenterY=6.95 CenterZ=0 NormalX=0 NormalY=0 NormalZ=1 AngleXU=0 Radius=2.1
    g32: Circle CenterX=-130.41 CenterY=-6.95 CenterZ=0 NormalX=0 NormalY=0 NormalZ=1 AngleXU=0 Radius=2.1
  constraints (79):
    c: Distance(g0) = 11.69
    c: PointOnObject(g0,g-1)
    c: Coincident(g-4,g0)
    c: Distance(g1) = 2.6
    c: Coincident(g1,g0)
    c: Vertical(g1)
    c: Distance(g2) = 2.6
    c: Coincident(g2,g0)
    c: Vertical(g2)
    c: Distance(g18,g12) = 8
    c: Coincident(g18,g2)
    c: Vertical(g3)
    c: Distance(g14,g12) = 5
    c: Horizontal(g4)
    c: Distance(g16,g14) = 8
    c: Vertical(g5)
    c: Distance(g26,g20) = 8
    c: Coincident(g20,g1)
    c: Vertical(g7)
    c: Distance(g26,g24) = 5
    c: Horizontal(g8)
    c: Distance(g24,g22) = 8
    c: Vertical(g9)
    c: PointOnObject(g12,g3)
    c: PointOnObject(g12,g4)
    c: Tangent(g3,g11) = 1.5708
    c: Tangent(g4,g11) = 1.5708
    c: PointOnObject(g14,g5)
    c: PointOnObject(g14,g4)
    c: Tangent(g5,g13) = 1.5708
    c: Tangent(g4,g13) = 1.5708
    c: PointOnObject(g16,g5)
    c: PointOnObject(g16,g6)
    c: Tangent(g5,g15) = 1.5708
    c: Tangent(g6,g15) = 1.5708
    c: PointOnObject(g18,g3)
    c: PointOnObject(g18,g6)
    c: Tangent(g3,g17) = 1.5708
    c: Tangent(g6,g17) = 1.5708
    c: Equal(g11,g13)
    c: Equal(g13,g15)
    c: Equal(g15,g17)
    c: DistanceX(g4,g4) = 0.25
    c: PointOnObject(g20,g7)
    c: PointOnObject(g20,g10)
    c: Tangent(g7,g19) = -1.5708
    c: Tangent(g10,g19) = -1.5708
    c: PointOnObject(g22,g9)
    c: PointOnObject(g22,g10)
    c: Tangent(g9,g21) = -1.5708
    c: Tangent(g10,g21) = -1.5708
    c: PointOnObject(g24,g9)
    c: PointOnObject(g24,g8)
    c: Tangent(g9,g23) = -1.5708
    c: Tangent(g8,g23) = -1.5708
    c: PointOnObject(g26,g8)
    c: PointOnObject(g26,g7)
    c: Tangent(g8,g25) = -1.5708
    c: Tangent(g7,g25) = -1.5708
    c: Equal(g19,g21)
    c: Equal(g21,g23)
    c: Equal(g23,g25)
    c: DistanceX(g10,g10) = 0.25
    c: Distance(g27) = 29.391
    c: Coincident(g27,g0)
    c: PointOnObject(g27,g-1)
    c: Distance(g28) = 51.19
    c: Coincident(g28,g0)
    c: PointOnObject(g28,g-1)
    c: Distance(g29) = 6.95
    c: Coincident(g29,g27)
    c: Vertical(g29)
    c: Distance(g30) = 6.95
    c: Coincident(g30,g28)
    c: Vertical(g30)
    c: Diameter(g31) = 4.2
    c: Diameter(g32) = 4.2
    c: Coincident(g32,g30)
    c: Coincident(g31,g29)
FEATURE [Sketcher::SketchObject] Sketch031  label="fori inferiori switch pompa"
  ArcFitTolerance = 1e-06
  AttachmentSupport = -> [XY_Plane]
  ExternalGeometry = -> [Sketch]
  FullyConstrained = true
  MakeInternals = false
  MapMode = 5
  sketch-geometry (4):
    g0: LineSegment [constr] StartX=-57.2 StartY=1.9e-15 StartZ=0 EndX=-62.45 EndY=1.9e-15 EndZ=0
    g1: LineSegment [constr] StartX=-62.45 StartY=3.25 StartZ=0 EndX=-62.45 EndY=-3.25 EndZ=0
    g2: Circle CenterX=-62.45 CenterY=3.25 CenterZ=0 NormalX=0 NormalY=0 NormalZ=1 AngleXU=0 Radius=1.6
    g3: Circle CenterX=-62.45 CenterY=-3.25 CenterZ=0 NormalX=0 NormalY=0 NormalZ=1 AngleXU=0 Radius=1.6
  constraints (10):
    c: Distance(g0) = 5.25
    c: Coincident(g0,g-3)
    c: PointOnObject(g0,g-3)
    c: Vertical(g1)
    c: DistanceY(g1,g1) = 6.5
    c: Symmetric(g1,g1,g0)
    c: Diameter(g2) = 3.2
    c: Diameter(g3) = 3.2
    c: Coincident(g2,g1)
    c: Coincident(g3,g1)
FEATURE [Sketcher::SketchObject] Sketch032  label="spazio per PILA 18650"
  ArcFitTolerance = 1e-06
  AttachmentSupport = -> [XY_Plane]
  ExternalGeometry = -> [Sketch]
  FullyConstrained = true
  MakeInternals = false
  MapMode = 5
  sketch-geometry (2):
    g0: LineSegment [constr] StartX=-178.142 StartY=-1.74e-14 StartZ=0 EndX=-191.142 EndY=-1.83e-14 EndZ=0
    g1: Circle CenterX=-191.142 CenterY=-1.83e-14 CenterZ=0 NormalX=0 NormalY=0 NormalZ=1 AngleXU=0 Radius=10.5
  constraints (5):
    c: Distance(g0) = 13
    c: Coincident(g0,g-3)
    c: PointOnObject(g0,g-4)
    c: Diameter(g1) = 21
    c: Coincident(g1,g0)
FEATURE [Part::Extrusion] Extrude030  label="Extrude spazio per PILA 18650"
  Base = -> Sketch032
  Dir = (0,0,1)
  DirLink = -> Sketch [Edge45]
  DirMode = 2
  FaceMakerClass = Part::FaceMakerBullseye
  FaceMakerMode = 3
  LengthFwd = 76
  LengthRev = 0
  Placement = pos=(6,0,-72) rot=(0,0,1;0rad)
  Solid = true
  Symmetric = false
FEATURE [Sketcher::SketchObject] Sketch033  label="fermo per scheda micro"
  ArcFitTolerance = 1e-06
  AttachmentSupport = -> [XZ_Plane]
  ExternalGeometry = -> [Sketch]
  FullyConstrained = true
  MakeInternals = false
  MapMode = 5
  Placement = pos=(0,0,0) rot=(1,0,0;1.5708rad)
  sketch-geometry (12):
    g0: LineSegment StartX=-11.6 StartY=6 StartZ=0 EndX=-4 EndY=6 EndZ=0
    g1: LineSegment StartX=-4 StartY=6 StartZ=0 EndX=-4 EndY=36.4 EndZ=0
    g2: LineSegment StartX=-4 StartY=36.4 StartZ=0 EndX=-11.6 EndY=36.4 EndZ=0
    g3: LineSegment StartX=-11.6 StartY=36.4 StartZ=0 EndX=-11.6 EndY=6 EndZ=0
    g4: LineSegment StartX=-80.11 StartY=11.6 StartZ=0 EndX=-70.51 EndY=11.6 EndZ=0
    g5: LineSegment StartX=-70.51 StartY=11.6 StartZ=0 EndX=-70.51 EndY=6 EndZ=0
    g6: LineSegment StartX=-70.51 StartY=6 StartZ=0 EndX=-80.11 EndY=6 EndZ=0
    g7: LineSegment StartX=-80.11 StartY=6 StartZ=0 EndX=-80.11 EndY=11.6 EndZ=0
    g8: LineSegment StartX=-78.51 StartY=36.4 StartZ=0 EndX=-70.51 EndY=36.4 EndZ=0
    g9: LineSegment StartX=-70.51 StartY=36.4 StartZ=0 EndX=-70.51 EndY=30.8 EndZ=0
    g10: LineSegment StartX=-70.51 StartY=30.8 StartZ=0 EndX=-78.51 EndY=30.8 EndZ=0
    g11: LineSegment StartX=-78.51 StartY=30.8 StartZ=0 EndX=-78.51 EndY=36.4 EndZ=0
  constraints (33):
    c: Horizontal(g0)
    c: Coincident(g1,g0)
    c: Coincident(g2,g1)
    c: Horizontal(g2)
    c: Coincident(g3,g2)
    c: Coincident(g3,g0)
    c: Vertical(g3)
    c: DistanceX(g2,g2) = 7.6
    c: Coincident(g1,g-3)
    c: Coincident(g0,g-3)
    c: Horizontal(g4)
    c: Coincident(g5,g4)
    c: Vertical(g5)
    c: Coincident(g6,g5)
    c: Horizontal(g6)
    c: Coincident(g7,g6)
    c: Coincident(g7,g4)
    c: Vertical(g7)
    c: DistanceY(g5,g5) = 5.6
    c: DistanceX(g4,g4) = 9.6
    c: Coincident(g9,g8)
    c: Vertical(g9)
    c: Coincident(g10,g9)
    c: Horizontal(g10)
    c: Coincident(g11,g10)
    c: Coincident(g11,g8)
    c: Vertical(g11)
    c: DistanceY(g9,g9) = 5.6
    c: DistanceX(g10,g10) = 8
    c: Coincident(g4,g-4)
    c: DistanceX(g4,g10) = 1.6
    c: Horizontal(g8)
    c: DistanceY(g8,g1) = 0
FEATURE [Sketcher::SketchObject] Sketch034  label="buchi guida rail"
  ArcFitTolerance = 1e-06
  AttachmentSupport = -> [XY_Plane]
  ExternalGeometry = -> [Sketch]
  FullyConstrained = true
  MakeInternals = false
  MapMode = 5
  sketch-geometry (6):
    g0: LineSegment [constr] StartX=-100.8 StartY=9.1e-15 StartZ=0 EndX=-93.3 EndY=0 EndZ=0
    g1: LineSegment [constr] StartX=-93.3 StartY=0 StartZ=0 EndX=-73.3 EndY=0 EndZ=0
    g2: LineSegment [constr] StartX=-73.3 StartY=0 StartZ=0 EndX=-53.3 EndY=0 EndZ=0
    g3: Circle CenterX=-93.3 CenterY=0 CenterZ=0 NormalX=0 NormalY=0 NormalZ=1 AngleXU=0 Radius=2.5
    g4: Circle CenterX=-73.3 CenterY=0 CenterZ=0 NormalX=0 NormalY=0 NormalZ=1 AngleXU=0 Radius=2.5
    g5: Circle CenterX=-53.3 CenterY=0 CenterZ=0 NormalX=0 NormalY=0 NormalZ=1 AngleXU=0 Radius=2.5
  constraints (15):
    c: Distance(g0) = 7.5
    c: Coincident(g0,g-3)
    c: PointOnObject(g0,g-1)
    c: Distance(g1) = 20
    c: Coincident(g1,g0)
    c: PointOnObject(g1,g-1)
    c: Distance(g2) = 20
    c: Coincident(g2,g1)
    c: PointOnObject(g2,g-1)
    c: Diameter(g3) = 5
    c: Diameter(g4) = 5
    c: Diameter(g5) = 5
    c: Coincident(g3,g0)
    c: Coincident(g4,g1)
    c: Coincident(g5,g2)
FEATURE [Part::Extrusion] Extrude032  label="Extrude buchi guida rail"
  Base = -> Sketch034
  Dir = (0,0,1)
  DirMode = 2
  FaceMakerClass = Part::FaceMakerBullseye
  FaceMakerMode = 3
  LengthFwd = -6.2
  LengthRev = 0
  Placement = pos=(0,0,43.2) rot=(0,0,1;0rad)
  Solid = true
  Symmetric = false
FEATURE [Part::Extrusion] Extrude033  label="Extrude fori superiori per solenoide e oled001"
  Base = -> Sketch030
  Dir = (0,0,1)
  DirMode = 2
  FaceMakerClass = Part::FaceMakerBullseye
  FaceMakerMode = 3
  LengthFwd = -4.8
  LengthRev = 0
  Placement = pos=(0,0,41.2) rot=(0,0,1;0rad)
  Solid = true
  Symmetric = false
FEATURE [Part::Extrusion] Extrude034  label="Extrude fori sotto impugnatura001"
  Base = -> Sketch029
  Dir = (0,0,1)
  DirMode = 2
  FaceMakerClass = Part::FaceMakerBullseye
  FaceMakerMode = 3
  LengthFwd = 5
  LengthRev = 0
  Placement = pos=(0,0,-83) rot=(0,0,1;0rad)
  Solid = true
  Symmetric = false
FEATURE [Part::Extrusion] Extrude035  label="Extrude fori inferiori switch pompa001"
  Base = -> Sketch031
  Dir = (0,0,1)
  DirMode = 2
  FaceMakerClass = Part::FaceMakerBullseye
  FaceMakerMode = 3
  LengthFwd = 4
  LengthRev = 0
  Placement = pos=(0,0,-1.7) rot=(0,0,1;0rad)
  Solid = true
  Symmetric = false
FEATURE [Part::Extrusion] Extrude036  label="Extrude foro sotto posteriore M3x5x007"
  Base = -> Sketch027
  Dir = (0,0,1)
  DirMode = 2
  FaceMakerClass = Part::FaceMakerBullseye
  FaceMakerMode = 3
  LengthFwd = 6.2
  LengthRev = 0
  Placement = pos=(0,0,-9.6) rot=(0,0,1;0rad)
  Solid = true
  Symmetric = false
FEATURE [Part::Extrusion] Extrude037  label="Extrude foro sotto anteriore M3x5x007"
  Base = -> Sketch026
  Dir = (0,0,1)
  DirMode = 2
  FaceMakerClass = Part::FaceMakerBullseye
  FaceMakerMode = 3
  LengthFwd = 6.2
  LengthRev = 0
  Solid = true
  Symmetric = false
FEATURE [Sketcher::SketchObject] Sketch035  label="foro per fissaggio micro"
  ArcFitTolerance = 1e-06
  AttachmentSupport = -> [XZ_Plane]
  ExternalGeometry = -> [Sketch,Sketch033]
  FullyConstrained = true
  MakeInternals = false
  MapMode = 5
  Placement = pos=(0,0,0) rot=(1,0,0;1.5708rad)
  sketch-geometry (3):
    g0: Circle CenterX=-7.8 CenterY=21.2 CenterZ=0 NormalX=0 NormalY=0 NormalZ=1 AngleXU=0 Radius=1.6
    g1: GeomPoint [constr] X=-4 Y=21.2 Z=0
    g2: LineSegment [constr] StartX=-4 StartY=21.2 StartZ=0 EndX=-11.6 EndY=21.2 EndZ=0
  constraints (6):
    c: Diameter(g0) = 3.2
    c: Symmetric(g-3,g-3,g1)
    c: Coincident(g2,g1)
    c: Horizontal(g2)
    c: DistanceX(g-4,g2) = 0
    c: Symmetric(g2,g1,g0)
FEATURE [Part::Extrusion] Extrude038  label="Extrude foro per fissaggio micro"
  Base = -> Sketch035
  Dir = (0,-1,2e-16)
  DirMode = 2
  FaceMakerClass = Part::FaceMakerBullseye
  FaceMakerMode = 3
  LengthFwd = 3
  LengthRev = 0
  Placement = pos=(0,8.6,0) rot=(0,0,1;0rad)
  Solid = true
  Symmetric = false
FEATURE [Sketcher::SketchObject] Sketch036  label="supporto per alimentatore"
  ArcFitTolerance = 1e-06
  AttachmentSupport = -> [XZ_Plane]
  ExternalGeometry = -> [Sketch,Sketch016,Sketch022]
  FullyConstrained = true
  MakeInternals = false
  MapMode = 5
  Placement = pos=(0,0,0) rot=(1,0,0;1.5708rad)
  sketch-geometry (5):
    g0: LineSegment StartX=-211.843 StartY=-50.0944 StartZ=0 EndX=-211.843 EndY=-80.4316 EndZ=0
    g1: LineSegment StartX=-211.843 StartY=-50.0944 StartZ=0 EndX=-207.775 EndY=-41.3701 EndZ=0
    g2: LineSegment [constr] StartX=-209.443 StartY=-50.0944 StartZ=0 EndX=-209.443 EndY=-80.4316 EndZ=0
    g3: LineSegment StartX=-207.775 StartY=-41.3701 StartZ=0 EndX=-207.775 EndY=-80.4316 EndZ=0
    g4: LineSegment StartX=-211.843 StartY=-80.4316 StartZ=0 EndX=-207.775 EndY=-80.4316 EndZ=0
  constraints (15):
    c: Vertical(g0)
    c: Coincident(g1,g0)
    c: Vertical(g2)
    c: Tangent(g2,g-5)
    c: Coincident(g3,g1)
    c: Vertical(g3)
    c: DistanceY(g-3,g3) = -2
    c: Tangent(g1,g-8)
    c: DistanceY(g-3,g0) = -2
    c: Coincident(g4,g0)
    c: Coincident(g4,g3)
    c: Tangent(g0,g-6)
    c: DistanceY(g-3,g2) = -2
    c: DistanceY(g2,g0) = 0
    c: DistanceX(g-3,g3) = 6.8
FEATURE [Part::Extrusion] Extrude039  label="Extrude039 supporto alimentatore"
  Base = -> Sketch036
  Dir = (0,-1,2e-16)
  DirMode = 2
  FaceMakerClass = Part::FaceMakerBullseye
  FaceMakerMode = 3
  LengthFwd = 25.2
  LengthRev = 0
  Solid = true
  Symmetric = true
FEATURE [Sketcher::SketchObject] Sketch037  label="scavo per alimentatore"
  ArcFitTolerance = 1e-06
  AttachmentSupport = -> [XZ_Plane]
  ExternalGeometry = -> [Sketch036]
  FullyConstrained = true
  MakeInternals = false
  MapMode = 5
  Placement = pos=(0,0,0) rot=(1,0,0;1.5708rad)
  sketch-geometry (4):
    g0: LineSegment StartX=-209.575 StartY=-50.4316 StartZ=0 EndX=-209.575 EndY=-80.4316 EndZ=0
    g1: LineSegment StartX=-209.575 StartY=-50.4316 StartZ=0 EndX=-207.775 EndY=-50.4316 EndZ=0
    g2: LineSegment StartX=-207.775 StartY=-50.4316 StartZ=0 EndX=-207.775 EndY=-80.4316 EndZ=0
    g3: LineSegment StartX=-207.775 StartY=-80.4316 StartZ=0 EndX=-209.575 EndY=-80.4316 EndZ=0
  constraints (11):
    c: Vertical(g0)
    c: Coincident(g1,g0)
    c: Horizontal(g1)
    c: Coincident(g2,g1)
    c: Vertical(g2)
    c: Coincident(g3,g2)
    c: Coincident(g3,g0)
    c: Horizontal(g3)
    c: DistanceX(g1,g1) = 1.8
    c: Coincident(g2,g-3)
    c: DistanceY(g2,g2) = 30
FEATURE [Part::Extrusion] Extrude040  label="Extrude040 scavo alimentatore"
  Base = -> Sketch037
  Dir = (0,-1,2e-16)
  DirMode = 2
  FaceMakerClass = Part::FaceMakerBullseye
  FaceMakerMode = 3
  LengthFwd = 19.5
  LengthRev = 0
  Solid = true
  Symmetric = true
FEATURE [Part::Extrusion] Extrude031  label="Extrude fermo per scheda micro"
  Base = -> Sketch033
  Dir = (0,-1,2e-16)
  DirMode = 2
  FaceMakerClass = Part::FaceMakerBullseye
  FaceMakerMode = 3
  LengthFwd = 3
  LengthRev = 0
  Placement = pos=(0,8.6,0) rot=(0,0,1;0rad)
  Solid = true
  Symmetric = false
FEATURE [Sketcher::SketchObject] Sketch038  label="scavo driver solenoide"
  ArcFitTolerance = 1e-06
  AttachmentSupport = -> [XZ_Plane]
  ExternalGeometry = -> [Sketch,Sketch036]
  FullyConstrained = true
  MakeInternals = false
  MapMode = 5
  Placement = pos=(0,0,0) rot=(1,0,0;1.5708rad)
  sketch-geometry (7):
    g0: LineSegment StartX=-192.222 StartY=-8.0175 StartZ=0 EndX=-194.941 EndY=-6.74965 EndZ=0
    g1: LineSegment StartX=-194.941 StartY=-6.74965 StartZ=0 EndX=-212.269 EndY=-43.9083 EndZ=0
    g2: LineSegment StartX=-192.222 StartY=-8.0175 StartZ=0 EndX=-188.779 EndY=-9.62345 EndZ=0
    g3: LineSegment StartX=-188.779 StartY=-9.62345 StartZ=0 EndX=-205.357 EndY=-45.1761 EndZ=0
    g4: LineSegment StartX=-205.357 StartY=-45.1761 StartZ=0 EndX=-209.55 EndY=-45.1761 EndZ=0
    g5: LineSegment [constr] StartX=-212.269 StartY=-43.9083 StartZ=0 EndX=-209.55 EndY=-45.1761 EndZ=0
    g6: LineSegment StartX=-212.269 StartY=-43.9083 StartZ=0 EndX=-209.55 EndY=-45.1761 EndZ=0
  constraints (20):
    c: Coincident(g1,g0)
    c: Coincident(g3,g2)
    c: Coincident(g4,g3)
    c: Distance(g2) = 3.8
    c: Distance(g1) = 41
    c: Coincident(g5,g1)
    c: Distance(g5) = 3
    c: Perpendicular(g5,g-3)
    c: Parallel(g1,g-3)
    c: Perpendicular(g1,g0)
    c: Distance(g0) = 3
    c: Coincident(g6,g1)
    c: Parallel(g3,g-3)
    c: Perpendicular(g2,g3)
    c: Coincident(g2,g0)
    c: Perpendicular(g-4,g4)
    c: PointOnObject(g5,g-3)
    c: Distance(g-3,g5) = 9.6
    c: Coincident(g4,g5)
    c: Coincident(g6,g4)
FEATURE [Part::Extrusion] Extrude041  label="Extrude scavo driver solenoide"
  Base = -> Sketch038
  Dir = (0,-1,2e-16)
  DirMode = 2
  FaceMakerClass = Part::FaceMakerBullseye
  FaceMakerMode = 3
  LengthFwd = 20.6
  LengthRev = 0
  Solid = true
  Symmetric = true
FEATURE [Sketcher::SketchObject] Sketch039  label="scavo per cavo usb per micro"
  ArcFitTolerance = 1e-06
  AttachmentSupport = -> [XZ_Plane]
  ExternalGeometry = -> [Sketch,Sketch016]
  FullyConstrained = true
  MakeInternals = false
  MapMode = 5
  Placement = pos=(0,0,0) rot=(1,0,0;1.5708rad)
  sketch-geometry (4):
    g0: LineSegment StartX=-82.51 StartY=36.4 StartZ=0 EndX=-74.51 EndY=36.4 EndZ=0
    g1: LineSegment StartX=-74.51 StartY=36.4 StartZ=0 EndX=-74.51 EndY=30.8 EndZ=0
    g2: LineSegment StartX=-74.51 StartY=30.8 StartZ=0 EndX=-82.51 EndY=30.8 EndZ=0
    g3: LineSegment StartX=-82.51 StartY=30.8 StartZ=0 EndX=-82.51 EndY=36.4 EndZ=0
  constraints (11):
    c: Coincident(g1,g0)
    c: Vertical(g1)
    c: Coincident(g2,g1)
    c: Horizontal(g2)
    c: Coincident(g3,g2)
    c: Coincident(g3,g0)
    c: Vertical(g3)
    c: Tangent(g0,g-3)
    c: Tangent(g2,g-4)
    c: Tangent(g3,g-4)
    c: Tangent(g1,g-4)
FEATURE [Part::Extrusion] Extrude042  label="Extrude scavo per cavo usb per micro"
  Base = -> Sketch039
  Dir = (0,-1,2e-16)
  DirMode = 2
  FaceMakerClass = Part::FaceMakerBullseye
  FaceMakerMode = 3
  LengthFwd = 11.2
  LengthRev = 0
  Solid = true
  Symmetric = true
FEATURE [Sketcher::SketchObject] Sketch040  label="scavo saldature alimentatore connettore 5v"
  ArcFitTolerance = 1e-06
  AttachmentSupport = -> [XZ_Plane]
  ExternalGeometry = -> [Sketch037]
  FullyConstrained = true
  MakeInternals = false
  MapMode = 5
  Placement = pos=(0,0,0) rot=(1,0,0;1.5708rad)
  sketch-geometry (4):
    g0: LineSegment StartX=-211.175 StartY=-52.4316 StartZ=0 EndX=-211.175 EndY=-56.4316 EndZ=0
    g1: LineSegment StartX=-211.175 StartY=-52.4316 StartZ=0 EndX=-209.575 EndY=-52.4316 EndZ=0
    g2: LineSegment StartX=-209.575 StartY=-52.4316 StartZ=0 EndX=-209.575 EndY=-56.4316 EndZ=0
    g3: LineSegment StartX=-209.575 StartY=-56.4316 StartZ=0 EndX=-211.175 EndY=-56.4316 EndZ=0
  constraints (11):
    c: Vertical(g0)
    c: Coincident(g1,g0)
    c: Horizontal(g1)
    c: Coincident(g2,g1)
    c: Coincident(g3,g2)
    c: Coincident(g3,g0)
    c: Horizontal(g3)
    c: DistanceX(g1,g1) = 1.6
    c: DistanceY(g2,g2) = 4
    c: Tangent(g2,g-3)
    c: DistanceY(g1,g-3) = 2
FEATURE [Part::Extrusion] Extrude043  label="Extrude scavo saldature alimentatore connettore 5v"
  Base = -> Sketch040
  Dir = (0,-1,2e-16)
  DirMode = 2
  FaceMakerClass = Part::FaceMakerBullseye
  FaceMakerMode = 3
  LengthFwd = 8
  LengthRev = 0
  Solid = true
  Symmetric = true
FEATURE [Sketcher::SketchObject] Sketch041  label="scavo saldature alimentatore connettore 5v verticali"
  ArcFitTolerance = 1e-06
  AttachmentSupport = -> [XZ_Plane]
  ExternalGeometry = -> [Sketch037]
  FullyConstrained = true
  MakeInternals = false
  MapMode = 5
  Placement = pos=(0,0,0) rot=(1,0,0;1.5708rad)
  sketch-geometry (4):
    g0: LineSegment StartX=-211.175 StartY=-53.6316 StartZ=0 EndX=-209.575 EndY=-53.6316 EndZ=0
    g1: LineSegment StartX=-209.575 StartY=-53.6316 StartZ=0 EndX=-209.575 EndY=-76.6316 EndZ=0
    g2: LineSegment StartX=-209.575 StartY=-76.6316 StartZ=0 EndX=-211.175 EndY=-76.6316 EndZ=0
    g3: LineSegment StartX=-211.175 StartY=-76.6316 StartZ=0 EndX=-211.175 EndY=-53.6316 EndZ=0
  constraints (11):
    c: Horizontal(g0)
    c: Coincident(g1,g0)
    c: Coincident(g2,g1)
    c: Horizontal(g2)
    c: Coincident(g3,g2)
    c: Coincident(g3,g0)
    c: Vertical(g3)
    c: DistanceY(g3,g3) = 23
    c: DistanceX(g0,g0) = 1.6
    c: Tangent(g1,g-3)
    c: DistanceY(g0,g-3) = 3.2
FEATURE [Part::Extrusion] Extrude044  label="Extrude scavo saldature alimentatore connettore 5v verticali"
  Base = -> Sketch041
  Dir = (0,-1,2e-16)
  DirMode = 2
  FaceMakerClass = Part::FaceMakerBullseye
  FaceMakerMode = 3
  LengthFwd = 3.2
  LengthRev = 0
  Placement = pos=(0,8.3,0) rot=(0,0,1;0rad)
  Solid = true
  Symmetric = false
FEATURE [Sketcher::SketchObject] Sketch042  label="fermi per driver solenoide e alimentatore"
  ArcFitTolerance = 1e-06
  AttachmentSupport = -> [XZ_Plane]
  ExternalGeometry = -> [Sketch036,Sketch037,Sketch,Sketch038]
  FullyConstrained = true
  MakeInternals = false
  MapMode = 5
  Placement = pos=(0,0,0) rot=(1,0,0;1.5708rad)
  sketch-geometry (27):
    g0: LineSegment StartX=-200.506 StartY=-25.7811 StartZ=0 EndX=-201.436 EndY=-27.775 EndZ=0
    g1: LineSegment StartX=-201.436 StartY=-27.775 StartZ=0 EndX=-199.442 EndY=-28.7048 EndZ=0
    g2: LineSegment StartX=-199.442 StartY=-28.7048 StartZ=0 EndX=-198.512 EndY=-26.7109 EndZ=0
    g3: LineSegment StartX=-198.512 StartY=-26.7109 StartZ=0 EndX=-200.506 EndY=-25.7811 EndZ=0
    g4: LineSegment StartX=-201.28 StartY=-23.6549 StartZ=0 EndX=-203.562 EndY=-28.5489 EndZ=0
    g5: LineSegment StartX=-203.562 StartY=-28.5489 StartZ=0 EndX=-200.118 EndY=-30.1549 EndZ=0
    g6: LineSegment StartX=-197.992 StartY=-29.381 StartZ=0 EndX=-197.062 EndY=-27.3871 EndZ=0
    g7: LineSegment StartX=-197.836 StartY=-25.2608 StartZ=0 EndX=-201.28 EndY=-23.6549 EndZ=0
    g8: LineSegment [constr] StartX=-198.668 StartY=-30.8311 StartZ=0 EndX=-197.992 EndY=-29.381 EndZ=0
    g9: LineSegment [constr] StartX=-198.668 StartY=-30.8311 StartZ=0 EndX=-200.118 EndY=-30.1549 EndZ=0
    g10: ArcOfCircle CenterX=-198.512 CenterY=-26.7109 CenterZ=0 NormalX=0 NormalY=0 NormalZ=1 AngleXU=0 Radius=1.6 StartAngle=5.84685 EndAngle=7.41765
    g11: GeomPoint [constr] X=-196.386 Y=-25.937 Z=0
    g12: ArcOfCircle CenterX=-199.442 CenterY=-28.7048 CenterZ=0 NormalX=0 NormalY=0 NormalZ=1 AngleXU=0 Radius=1.6 StartAngle=4.27606 EndAngle=5.84685
    g13: GeomPoint [constr] X=-198.668 Y=-30.8311 Z=0
    g14: LineSegment StartX=-207.775 StartY=-46.8316 StartZ=0 EndX=-207.775 EndY=-50.8316 EndZ=0
    g15: LineSegment StartX=-207.775 StartY=-46.8316 StartZ=0 EndX=-203.775 EndY=-46.8316 EndZ=0
    g16: LineSegment StartX=-203.775 StartY=-46.8316 StartZ=0 EndX=-203.775 EndY=-50.8316 EndZ=0
    g17: LineSegment StartX=-207.775 StartY=-50.8316 StartZ=0 EndX=-203.775 EndY=-50.8316 EndZ=0
    g18: LineSegment StartX=-209.375 StartY=-52.4316 StartZ=0 EndX=-203.775 EndY=-52.4316 EndZ=0
    g19: LineSegment StartX=-202.175 StartY=-50.8316 StartZ=0 EndX=-202.175 EndY=-46.8316 EndZ=0
    g20: LineSegment StartX=-203.775 StartY=-45.2316 StartZ=0 EndX=-209.375 EndY=-45.2316 EndZ=0
    g21: LineSegment StartX=-209.375 StartY=-45.2316 StartZ=0 EndX=-209.375 EndY=-52.4316 EndZ=0
    g22: ArcOfCircle CenterX=-203.775 CenterY=-46.8316 CenterZ=0 NormalX=0 NormalY=0 NormalZ=1 AngleXU=0 Radius=1.6 StartAngle=1.8e-15 EndAngle=1.5708
    g23: GeomPoint [constr] X=-202.175 Y=-45.2316 Z=0
    g24: ArcOfCircle CenterX=-203.775 CenterY=-50.8316 CenterZ=0 NormalX=0 NormalY=0 NormalZ=1 AngleXU=0 Radius=1.6 StartAngle=4.71239 EndAngle=6.28319
    g25: GeomPoint [constr] X=-202.175 Y=-52.4316 Z=0
    g26: LineSegment [constr] StartX=-207.775 StartY=-50.4316 StartZ=0 EndX=-207.775 EndY=-50.8316 EndZ=0
  constraints (69):
    c: Coincident(g1,g0)
    c: Coincident(g2,g1)
    c: Coincident(g3,g2)
    c: Coincident(g3,g0)
    c: Parallel(g0,g2)
    c: Perpendicular(g3,g0)
    c: Perpendicular(g1,g0)
    c: Coincident(g5,g4)
    c: Coincident(g7,g4)
    c: Distance(g3) = 2.2
    c: Distance(g2) = 2.2
    c: Parallel(g6,g2)
    c: Parallel(g6,g4)
    c: Perpendicular(g5,g6)
    c: Perpendicular(g7,g6)
    c: Distance(g13,g11) = 5.4
    c: Distance(g5,g13) = 5.4
    c: Coincident(g9,g8)
    c: Distance(g8) = 1.6
    c: Distance(g9) = 1.6
    c: Perpendicular(g9,g8)
    c: Parallel(g8,g6)
    c: Coincident(g8,g13)
    c: Distance(g8,g1) = 1.6
    c: Distance(g9,g1) = 1.6
    c: Tangent(g0,g-5)
    c: Distance(g0,g-6) = 19.2
    c: PointOnObject(g11,g7)
    c: PointOnObject(g11,g6)
    c: Tangent(g7,g10) = -1.5708
    c: Tangent(g6,g10) = -1.5708
    c: PointOnObject(g13,g5)
    c: Tangent(g5,g12) = -1.5708
    c: Tangent(g6,g12) = -1.5708
    c: Equal(g10,g12)
    c: Coincident(g10,g2)
    c: Vertical(g14)
    c: Coincident(g15,g14)
    c: Horizontal(g15)
    c: Coincident(g16,g15)
    c: Vertical(g16)
    c: Coincident(g17,g14)
    c: Coincident(g17,g16)
    c: Horizontal(g17)
    c: Distance(g16) = 4
    c: Distance(g15) = 4
    c: Horizontal(g18)
    c: Vertical(g19)
    c: Horizontal(g20)
    c: Coincident(g21,g20)
    c: Coincident(g21,g18)
    c: Vertical(g21)
    c: Distance(g20,g23) = 7.2
    c: Distance(g25,g23) = 7.2
    c: DistanceY(g18,g14) = 1.6
    c: DistanceX(g18,g14) = 1.6
    c: PointOnObject(g23,g20)
    c: PointOnObject(g23,g19)
    c: Tangent(g20,g22) = -1.5708
    c: Tangent(g19,g22) = -1.5708
    c: PointOnObject(g25,g19)
    c: Tangent(g18,g24) = -1.5708
    c: Tangent(g19,g24) = -1.5708
    c: Equal(g22,g24)
    c: Coincident(g22,g15)
    c: Vertical(g26)
    c: Distance(g26) = 0.4
    c: Coincident(g26,g-4)
    c: Coincident(g14,g26)
FEATURE [Part::Extrusion] Extrude045  label="Extrude fermi per driver solenoide e alimentatore"
  Base = -> Sketch042
  Dir = (0,-1,2e-16)
  DirMode = 2
  FaceMakerClass = Part::FaceMakerBullseye
  FaceMakerMode = 3
  LengthFwd = 25.2
  LengthRev = 0
  Solid = true
  Symmetric = true
FEATURE [Sketcher::SketchObject] Sketch043  label="scavo pulizia fermo alimentatore"
  ArcFitTolerance = 1e-06
  AttachmentSupport = -> [XZ_Plane]
  ExternalGeometry = -> [Sketch042,Sketch036,Sketch037]
  FullyConstrained = true
  MakeInternals = false
  MapMode = 5
  Placement = pos=(0,0,0) rot=(1,0,0;1.5708rad)
  sketch-geometry (6):
    g0: LineSegment StartX=-209.375 StartY=-52.4316 StartZ=0 EndX=-209.375 EndY=-50.4316 EndZ=0
    g1: LineSegment StartX=-209.375 StartY=-50.4316 StartZ=0 EndX=-207.775 EndY=-50.4316 EndZ=0
    g2: LineSegment StartX=-207.775 StartY=-50.4316 StartZ=0 EndX=-207.775 EndY=-45.2316 EndZ=0
    g3: LineSegment StartX=-207.775 StartY=-45.2316 StartZ=0 EndX=-202.175 EndY=-45.2316 EndZ=0
    g4: LineSegment StartX=-202.175 StartY=-45.2316 StartZ=0 EndX=-202.175 EndY=-52.4316 EndZ=0
    g5: LineSegment StartX=-202.175 StartY=-52.4316 StartZ=0 EndX=-209.375 EndY=-52.4316 EndZ=0
  constraints (13):
    c: Vertical(g0)
    c: Coincident(g1,g0)
    c: Coincident(g2,g1)
    c: Coincident(g3,g2)
    c: Coincident(g4,g3)
    c: Coincident(g5,g4)
    c: Coincident(g5,g0)
    c: Horizontal(g5)
    c: Coincident(g0,g-6)
    c: Tangent(g1,g-8)
    c: Tangent(g2,g-4)
    c: Tangent(g3,g-7)
    c: Tangent(g4,g-3)
FEATURE [Part::Extrusion] Extrude046  label="Extrude scavo pulizia fermo alimentatore"
  Base = -> Sketch043
  Dir = (0,-1,2e-16)
  DirMode = 2
  FaceMakerClass = Part::FaceMakerBullseye
  FaceMakerMode = 3
  LengthFwd = 19.5
  LengthRev = 0
  Solid = true
  Symmetric = true
FEATURE [Sketcher::SketchObject] Sketch044  label="buchini per fissaggio oled"
  ArcFitTolerance = 1e-06
  AttachmentSupport = -> [YZ_Plane]
  ExternalGeometry = -> [Sketch]
  FullyConstrained = true
  MakeInternals = false
  MapMode = 5
  Placement = pos=(0,0,0) rot=(0.57735,0.57735,0.57735;2.0944rad)
  sketch-geometry (5):
    g0: LineSegment [constr] StartX=1.5e-14 StartY=67.3588 StartZ=0 EndX=0 EndY=64.3588 EndZ=0
    g1: LineSegment [constr] StartX=0 StartY=64.3588 StartZ=0 EndX=10.4 EndY=64.3588 EndZ=0
    g2: LineSegment [constr] StartX=0 StartY=64.3588 StartZ=0 EndX=-10.4 EndY=64.3588 EndZ=0
    g3: Circle CenterX=10.4 CenterY=64.3588 CenterZ=0 NormalX=0 NormalY=0 NormalZ=1 AngleXU=0 Radius=1.5
    g4: Circle CenterX=-10.4 CenterY=64.3588 CenterZ=0 NormalX=0 NormalY=0 NormalZ=1 AngleXU=0 Radius=1.5
  constraints (13):
    c: Distance(g0) = 3
    c: PointOnObject(g0,g-2)
    c: Coincident(g1,g0)
    c: Horizontal(g1)
    c: Coincident(g2,g0)
    c: Horizontal(g2)
    c: DistanceX(g1,g1) = 10.4
    c: Coincident(g3,g1)
    c: Diameter(g4) = 3
    c: Coincident(g4,g2)
    c: Coincident(g0,g-7)
    c: Equal(g1,g2)
    c: Equal(g4,g3)
FEATURE [Part::Extrusion] Extrude047  label="Extrude buchini per fissaggio oled"
  Base = -> Sketch044
  Dir = (1,0,0)
  DirMode = 2
  FaceMakerClass = Part::FaceMakerBullseye
  FaceMakerMode = 3
  LengthFwd = 10
  LengthRev = 0
  Placement = pos=(-186,0,0) rot=(0,0,1;0rad)
  Solid = true
  Symmetric = false
FEATURE [Sketcher::SketchObject] Sketch046  label="scavo 5x5 neopixel"
  ArcFitTolerance = 1e-06
  AttachmentSupport = -> [YZ_Plane002]
  FullyConstrained = true
  MakeInternals = false
  MapMode = 5
  Placement = pos=(0,0,0) rot=(0.57735,0.57735,0.57735;2.0944rad)
  sketch-geometry (4):
    g0: LineSegment StartX=-2.7 StartY=2.7 StartZ=0 EndX=2.7 EndY=2.7 EndZ=0
    g1: LineSegment StartX=2.7 StartY=2.7 StartZ=0 EndX=2.7 EndY=-2.7 EndZ=0
    g2: LineSegment StartX=2.7 StartY=-2.7 StartZ=0 EndX=-2.7 EndY=-2.7 EndZ=0
    g3: LineSegment StartX=-2.7 StartY=-2.7 StartZ=0 EndX=-2.7 EndY=2.7 EndZ=0
  constraints (11):
    c: Horizontal(g0)
    c: Coincident(g1,g0)
    c: Vertical(g1)
    c: Coincident(g2,g1)
    c: Horizontal(g2)
    c: Coincident(g3,g2)
    c: Coincident(g3,g0)
    c: Vertical(g3)
    c: DistanceX(g0,g0) = 5.4
    c: DistanceY(g1,g1) = 5.4
    c: Symmetric(g0,g1,g-1)
FEATURE [Sketcher::SketchObject] Sketch047  label="scavo 10x10 neopixel corpo"
  ArcFitTolerance = 1e-06
  AttachmentOffset = pos=(0,0,1) rot=(0,0,1;0rad)
  AttachmentSupport = -> [YZ_Plane002]
  FullyConstrained = true
  MakeInternals = false
  MapMode = 5
  Placement = pos=(1,0,0) rot=(0.57735,0.57735,0.57735;2.0944rad)
  sketch-geometry (4):
    g0: LineSegment StartX=-5 StartY=5.1 StartZ=0 EndX=5 EndY=5.1 EndZ=0
    g1: LineSegment StartX=5 StartY=5.1 StartZ=0 EndX=5 EndY=-5.1 EndZ=0
    g2: LineSegment StartX=5 StartY=-5.1 StartZ=0 EndX=-5 EndY=-5.1 EndZ=0
    g3: LineSegment StartX=-5 StartY=-5.1 StartZ=0 EndX=-5 EndY=5.1 EndZ=0
  constraints (11):
    c: Horizontal(g0)
    c: Coincident(g1,g0)
    c: Vertical(g1)
    c: Coincident(g2,g1)
    c: Horizontal(g2)
    c: Coincident(g3,g2)
    c: Coincident(g3,g0)
    c: Vertical(g3)
    c: DistanceX(g0,g0) = 10
    c: DistanceY(g1,g1) = 10.2
    c: Symmetric(g0,g2,g-1)
FEATURE [Sketcher::SketchObject] Sketch048  label="buco per perno blocco neopixel"
  ArcFitTolerance = 1e-06
  AttachmentSupport = -> [XZ_Plane002]
  FullyConstrained = true
  MakeInternals = false
  MapMode = 5
  Placement = pos=(0,0,0) rot=(1,0,0;1.5708rad)
  sketch-geometry (4):
    g0: LineSegment StartX=3 StartY=1.2 StartZ=0 EndX=3 EndY=-1.2 EndZ=0
    g1: LineSegment StartX=3 StartY=-1.2 StartZ=0 EndX=5.4 EndY=-1.2 EndZ=0
    g2: LineSegment StartX=5.4 StartY=-1.2 StartZ=0 EndX=5.4 EndY=1.2 EndZ=0
    g3: LineSegment StartX=5.4 StartY=1.2 StartZ=0 EndX=3 EndY=1.2 EndZ=0
  constraints (11):
    c: Coincident(g1,g0)
    c: Horizontal(g1)
    c: Coincident(g2,g1)
    c: Vertical(g2)
    c: Coincident(g3,g2)
    c: Coincident(g3,g0)
    c: Horizontal(g3)
    c: DistanceX(g1,g1) = 2.4
    c: DistanceY(g2,g2) = 2.4
    c: Symmetric(g0,g0,g-1)
    c: DistanceX(g-1,g0) = 3
FEATURE [Sketcher::SketchObject] Sketch045  label="blocco principale per neopixel"
  ArcFitTolerance = 1e-06
  AttachmentSupport = -> [XZ_Plane002]
  ExternalGeometry = -> [Sketch048]
  FullyConstrained = true
  MakeInternals = false
  MapMode = 5
  Placement = pos=(0,0,0) rot=(1,0,0;1.5708rad)
  sketch-geometry (6):
    g0: LineSegment StartX=0 StartY=5.1 StartZ=0 EndX=0 EndY=-5.1 EndZ=0
    g1: LineSegment StartX=0 StartY=-5.1 StartZ=0 EndX=3 EndY=-5.1 EndZ=0
    g2: LineSegment StartX=7 StartY=-1.1 StartZ=0 EndX=7 EndY=5.1 EndZ=0
    g3: LineSegment StartX=7 StartY=5.1 StartZ=0 EndX=0 EndY=5.1 EndZ=0
    g4: ArcOfCircle CenterX=3 CenterY=-1.1 CenterZ=0 NormalX=0 NormalY=0 NormalZ=1 AngleXU=0 Radius=4 StartAngle=4.71239 EndAngle=6.28319
    g5: GeomPoint [constr] X=7 Y=-5.1 Z=0
  constraints (15):
    c: Vertical(g0)
    c: Coincident(g1,g0)
    c: Horizontal(g1)
    c: Vertical(g2)
    c: Coincident(g3,g2)
    c: Coincident(g3,g0)
    c: Horizontal(g3)
    c: DistanceY(g0,g0) = 10.2
    c: Symmetric(g0,g0,g-1)
    c: DistanceX(g3,g3) = 7
    c: PointOnObject(g5,g2)
    c: PointOnObject(g5,g1)
    c: Tangent(g2,g4) = -1.5708
    c: Tangent(g1,g4) = -1.5708
    c: DistanceX(g-3,g1) = 0
FEATURE [Sketcher::SketchObject] Sketch049  label="rinforzi esterni per corpo neopoixel"
  ArcFitTolerance = 1e-06
  AttachmentSupport = -> [XZ_Plane002]
  ExternalGeometry = -> [Sketch045]
  FullyConstrained = true
  MakeInternals = false
  MapMode = 5
  Placement = pos=(0,0,0) rot=(1,0,0;1.5708rad)
  sketch-geometry (8):
    g0: LineSegment StartX=1 StartY=-4.1 StartZ=0 EndX=2 EndY=-4.1 EndZ=0
    g1: LineSegment StartX=2 StartY=-4.1 StartZ=0 EndX=2 EndY=-5.1 EndZ=0
    g2: LineSegment StartX=2 StartY=-5.1 StartZ=0 EndX=1 EndY=-5.1 EndZ=0
    g3: LineSegment StartX=1 StartY=-5.1 StartZ=0 EndX=1 EndY=-4.1 EndZ=0
    g4: LineSegment StartX=1 StartY=5.1 StartZ=0 EndX=2 EndY=5.1 EndZ=0
    g5: LineSegment StartX=2 StartY=5.1 StartZ=0 EndX=2 EndY=4.1 EndZ=0
    g6: LineSegment StartX=2 StartY=4.1 StartZ=0 EndX=1 EndY=4.1 EndZ=0
    g7: LineSegment StartX=1 StartY=4.1 StartZ=0 EndX=1 EndY=5.1 EndZ=0
  constraints (24):
    c: Horizontal(g0)
    c: Coincident(g1,g0)
    c: Vertical(g1)
    c: Coincident(g2,g1)
    c: Horizontal(g2)
    c: Coincident(g3,g2)
    c: Coincident(g3,g0)
    c: Vertical(g3)
    c: Horizontal(g4)
    c: Coincident(g5,g4)
    c: Vertical(g5)
    c: Coincident(g6,g5)
    c: Horizontal(g6)
    c: Coincident(g7,g6)
    c: Coincident(g7,g4)
    c: Vertical(g7)
    c: DistanceX(g4,g4) = 1
    c: DistanceY(g5,g5) = 1
    c: DistanceX(g0,g0) = 1
    c: DistanceY(g1,g1) = 1
    c: DistanceX(g-3,g4) = 1
    c: DistanceY(g-3,g4) = 0
    c: DistanceX(g-4,g2) = 1
    c: DistanceY(g2,g-4) = 0
FEATURE [Sketcher::SketchObject] Sketch052  label="scavo saldature driver solenoide"
  ArcFitTolerance = 1e-06
  AttachmentSupport = -> [XZ_Plane]
  ExternalGeometry = -> [Sketch038]
  FullyConstrained = true
  MakeInternals = false
  MapMode = 5
  Placement = pos=(0,0,0) rot=(1,0,0;1.5708rad)
  sketch-geometry (4):
    g0: LineSegment StartX=-195.304 StartY=-6.5806 StartZ=0 EndX=-196.994 EndY=-10.2058 EndZ=0
    g1: LineSegment StartX=-196.994 StartY=-10.2058 StartZ=0 EndX=-196.632 EndY=-10.3749 EndZ=0
    g2: LineSegment StartX=-196.632 StartY=-10.3749 StartZ=0 EndX=-194.941 EndY=-6.74965 EndZ=0
    g3: LineSegment StartX=-194.941 StartY=-6.74965 StartZ=0 EndX=-195.304 EndY=-6.5806 EndZ=0
  constraints (11):
    c: Coincident(g1,g0)
    c: Coincident(g2,g1)
    c: Coincident(g3,g2)
    c: Coincident(g3,g0)
    c: Parallel(g2,g0)
    c: Perpendicular(g2,g3)
    c: Perpendicular(g1,g2,g1) = 1.5708
    c: Parallel(g2,g-3)
    c: Distance(g2) = 4
    c: Distance(g3) = 0.4
    c: Coincident(g2,g-3)
FEATURE [Part::Extrusion] Extrude055  label="Extrude scavo saldature driver solenoide"
  Base = -> Sketch052
  Dir = (0,-1,2e-16)
  DirMode = 2
  FaceMakerClass = Part::FaceMakerBullseye
  FaceMakerMode = 3
  LengthFwd = 6
  LengthRev = 0
  Solid = true
  Symmetric = true
FEATURE [Sketcher::SketchObject] Sketch053  label="scavo saldature rumble"
  ArcFitTolerance = 1e-06
  AttachmentSupport = -> [XZ_Plane]
  ExternalGeometry = -> [Sketch019]
  FullyConstrained = true
  MakeInternals = false
  MapMode = 5
  Placement = pos=(0,0,0) rot=(1,0,0;1.5708rad)
  sketch-geometry (4):
    g0: LineSegment StartX=-169.451 StartY=-56.8615 StartZ=0 EndX=-170.687 EndY=-60.6657 EndZ=0
    g1: LineSegment StartX=-170.687 StartY=-60.6657 StartZ=0 EndX=-169.546 EndY=-61.0365 EndZ=0
    g2: LineSegment StartX=-169.546 StartY=-61.0365 StartZ=0 EndX=-168.31 EndY=-57.2323 EndZ=0
    g3: LineSegment StartX=-168.31 StartY=-57.2323 StartZ=0 EndX=-169.451 EndY=-56.8615 EndZ=0
  constraints (11):
    c: Coincident(g1,g0)
    c: Coincident(g2,g1)
    c: Coincident(g3,g2)
    c: Coincident(g3,g0)
    c: Parallel(g0,g2)
    c: Perpendicular(g3,g0)
    c: Perpendicular(g1,g0)
    c: Parallel(g0,g-3)
    c: Distance(g0) = 4
    c: Coincident(g0,g-3)
    c: Distance(g1) = 1.2
FEATURE [Part::Extrusion] Extrude056  label="Extrude scavo saldature rumble"
  Base = -> Sketch053
  Dir = (0,-1,2e-16)
  DirMode = 2
  FaceMakerClass = Part::FaceMakerBullseye
  FaceMakerMode = 3
  LengthFwd = 8.4
  LengthRev = 0
  Solid = true
  Symmetric = true
FEATURE [Sketcher::SketchObject] Sketch054  label="scavo saldature alimentatore connettore USB"
  ArcFitTolerance = 1e-06
  AttachmentSupport = -> [XZ_Plane]
  ExternalGeometry = -> [Sketch037]
  FullyConstrained = true
  MakeInternals = false
  MapMode = 5
  Placement = pos=(0,0,0) rot=(1,0,0;1.5708rad)
  sketch-geometry (4):
    g0: LineSegment StartX=-209.575 StartY=-80.4316 StartZ=0 EndX=-210.375 EndY=-80.4316 EndZ=0
    g1: LineSegment StartX=-210.375 StartY=-80.4316 StartZ=0 EndX=-210.375 EndY=-72.4316 EndZ=0
    g2: LineSegment StartX=-210.375 StartY=-72.4316 StartZ=0 EndX=-209.575 EndY=-72.4316 EndZ=0
    g3: LineSegment StartX=-209.575 StartY=-72.4316 StartZ=0 EndX=-209.575 EndY=-80.4316 EndZ=0
  constraints (11):
    c: Horizontal(g0)
    c: Coincident(g1,g0)
    c: Vertical(g1)
    c: Coincident(g2,g1)
    c: Horizontal(g2)
    c: Coincident(g3,g2)
    c: Coincident(g3,g0)
    c: Vertical(g3)
    c: DistanceX(g0,g0) = 0.8
    c: DistanceY(g3,g3) = 8
    c: Coincident(g0,g-4)
FEATURE [Part::Extrusion] Extrude057  label="Extrude scavo saldature alimentatore connettore USB"
  Base = -> Sketch054
  Dir = (0,-1,2e-16)
  DirMode = 2
  FaceMakerClass = Part::FaceMakerBullseye
  FaceMakerMode = 3
  LengthFwd = 11
  LengthRev = 0
  Solid = true
  Symmetric = true
FEATURE [Sketcher::SketchObject] Sketch055  label="buco interno per micro switch"
  ArcFitTolerance = 1e-06
  AttachmentSupport = -> [XZ_Plane]
  ExternalGeometry = -> [Sketch]
  FullyConstrained = true
  MakeInternals = false
  MapMode = 5
  Placement = pos=(0,0,0) rot=(1,0,0;1.5708rad)
  sketch-geometry (11):
    g0: LineSegment [constr] StartX=-194.483 StartY=34.2854 StartZ=0 EndX=-196.022 EndY=30.0568 EndZ=0
    g1: LineSegment [constr] StartX=-196.022 StartY=30.0568 StartZ=0 EndX=-197.561 EndY=25.8282 EndZ=0
    g2: LineSegment [constr] StartX=-196.022 StartY=30.0568 StartZ=0 EndX=-194.143 EndY=29.3727 EndZ=0
    g3: LineSegment [constr] StartX=-196.022 StartY=30.0568 StartZ=0 EndX=-197.902 EndY=30.7408 EndZ=0
    g4: LineSegment StartX=-196.362 StartY=34.9694 StartZ=0 EndX=-192.604 EndY=33.6014 EndZ=0
    g5: LineSegment StartX=-199.441 StartY=26.5122 StartZ=0 EndX=-195.682 EndY=25.1441 EndZ=0
    g6: LineSegment StartX=-192.604 StartY=33.6014 StartZ=0 EndX=-195.682 EndY=25.1441 EndZ=0
    g7: LineSegment StartX=-196.362 StartY=34.9694 StartZ=0 EndX=-199.441 EndY=26.5122 EndZ=0
    g8: GeomPoint [constr] X=-187.821 Y=29.2 Z=0
    g9: LineSegment [constr] StartX=-188.505 StartY=27.3206 StartZ=0 EndX=-196.022 EndY=30.0568 EndZ=0
    g10: LineSegment [constr] StartX=-187.821 StartY=29.2 StartZ=0 EndX=-188.505 EndY=27.3206 EndZ=0
  constraints (27):
    c: Coincident(g2,g0)
    c: Parallel(g0,g-3)
    c: Tangent(g1,g0) = -1.5708
    c: Perpendicular(g0,g2)
    c: Tangent(g2,g3)
    c: Distance(g0,g1) = 9
    c: Equal(g0,g1)
    c: Distance(g3,g2) = 4
    c: Equal(g2,g3)
    c: Parallel(g3,g4)
    c: Symmetric(g4,g4,g0)
    c: Parallel(g6,g1)
    c: Parallel(g7,g1)
    c: Symmetric(g6,g6,g2)
    c: Symmetric(g5,g5,g1)
    c: Symmetric(g7,g7,g3)
    c: Coincident(g7,g4)
    c: Coincident(g6,g4)
    c: Coincident(g5,g6)
    c: Symmetric(g-3,g-3,g8)
    c: Perpendicular(g-3,g9)
    c: Distance(g9) = 8
    c: Coincident(g3,g9)
    c: Coincident(g10,g8)
    c: Parallel(g10,g-3)
    c: Distance(g10) = 2
    c: Coincident(g10,g9)
FEATURE [Sketcher::SketchObject] Sketch056  label="buco esterno per micro switch"
  ArcFitTolerance = 1e-06
  AttachmentSupport = -> [XZ_Plane]
  ExternalGeometry = -> [Sketch055]
  FullyConstrained = true
  MakeInternals = false
  MapMode = 5
  Placement = pos=(0,0,0) rot=(1,0,0;1.5708rad)
  sketch-geometry (17):
    g0: GeomPoint [constr] X=-194.143 Y=29.3727 Z=0
    g1: GeomPoint [constr] X=-194.483 Y=34.2854 Z=0
    g2: GeomPoint [constr] X=-197.902 Y=30.7408 Z=0
    g3: GeomPoint [constr] X=-197.561 Y=25.8282 Z=0
    g4: GeomPoint [constr] X=-196.022 Y=30.0568 Z=0
    g5: LineSegment [constr] StartX=-194.483 StartY=34.2854 StartZ=0 EndX=-196.022 EndY=30.0568 EndZ=0
    g6: LineSegment [constr] StartX=-196.022 StartY=30.0568 StartZ=0 EndX=-197.561 EndY=25.8282 EndZ=0
    g7: LineSegment [constr] StartX=-197.902 StartY=30.7408 StartZ=0 EndX=-196.022 EndY=30.0568 EndZ=0
    g8: LineSegment [constr] StartX=-196.022 StartY=30.0568 StartZ=0 EndX=-194.143 EndY=29.3727 EndZ=0
    g9: LineSegment [constr] StartX=-195.338 StartY=31.9362 StartZ=0 EndX=-196.022 EndY=30.0568 EndZ=0
    g10: LineSegment [constr] StartX=-196.022 StartY=30.0568 StartZ=0 EndX=-196.706 EndY=28.1774 EndZ=0
    g11: LineSegment [constr] StartX=-196.022 StartY=30.0568 StartZ=0 EndX=-196.821 EndY=30.3475 EndZ=0
    g12: LineSegment [constr] StartX=-196.022 StartY=30.0568 StartZ=0 EndX=-195.223 EndY=29.7661 EndZ=0
    g13: LineSegment StartX=-194.539 StartY=31.6454 StartZ=0 EndX=-195.907 EndY=27.8867 EndZ=0
    g14: LineSegment StartX=-196.137 StartY=32.2269 StartZ=0 EndX=-197.505 EndY=28.4681 EndZ=0
    g15: LineSegment StartX=-196.137 StartY=32.2269 StartZ=0 EndX=-194.539 EndY=31.6454 EndZ=0
    g16: LineSegment StartX=-197.505 StartY=28.4681 StartZ=0 EndX=-195.907 EndY=27.8867 EndZ=0
  constraints (34):
    c: Symmetric(g-5,g-5,g1)
    c: Symmetric(g-5,g-6,g0)
    c: Symmetric(g-6,g-6,g3)
    c: Symmetric(g-5,g-6,g2)
    c: Coincident(g5,g1)
    c: Coincident(g5,g4)
    c: Coincident(g6,g4)
    c: Coincident(g6,g3)
    c: Equal(g5,g6)
    c: Coincident(g7,g2)
    c: Coincident(g7,g4)
    c: Coincident(g8,g4)
    c: Coincident(g8,g0)
    c: Equal(g7,g8)
    c: Coincident(g11,g9)
    c: Coincident(g12,g9)
    c: Tangent(g10,g9) = -1.5708
    c: Perpendicular(g11,g9)
    c: Parallel(g9,g-4)
    c: Equal(g9,g10)
    c: Parallel(g12,g11)
    c: Equal(g11,g12)
    c: Distance(g11,g12) = 1.7
    c: Distance(g9,g10) = 4
    c: Symmetric(g13,g13,g12)
    c: Parallel(g13,g9)
    c: Symmetric(g14,g14,g11)
    c: Symmetric(g15,g15,g9)
    c: Parallel(g15,g11)
    c: Symmetric(g16,g16,g10)
    c: Coincident(g16,g14)
    c: Coincident(g15,g14)
    c: Coincident(g13,g15)
    c: Coincident(g9,g4)
FEATURE [Sketcher::SketchObject] Sketch057  label="buco interno per SWITCH"
  ArcFitTolerance = 1e-06
  AttachmentSupport = -> [XZ_Plane]
  ExternalGeometry = -> [Sketch]
  FullyConstrained = true
  MakeInternals = false
  MapMode = 5
  Placement = pos=(0,0,0) rot=(1,0,0;1.5708rad)
  sketch-geometry (10):
    g0: GeomPoint [constr] X=-187.821 Y=29.2 Z=0
    g1: LineSegment [constr] StartX=-188.505 StartY=27.3206 StartZ=0 EndX=-193.203 EndY=29.0307 EndZ=0
    g2: LineSegment [constr] StartX=-190.809 StartY=35.6086 StartZ=0 EndX=-195.597 EndY=22.4529 EndZ=0
    g3: GeomPoint [constr] X=-193.203 Y=29.0307 Z=0
    g4: LineSegment [constr] StartX=-196.492 StartY=30.2278 StartZ=0 EndX=-189.914 EndY=27.8336 EndZ=0
    g5: LineSegment StartX=-194.098 StartY=36.8056 StartZ=0 EndX=-187.52 EndY=34.4115 EndZ=0
    g6: LineSegment StartX=-194.098 StartY=36.8056 StartZ=0 EndX=-198.886 EndY=23.6499 EndZ=0
    g7: LineSegment StartX=-187.52 StartY=34.4115 StartZ=0 EndX=-192.308 EndY=21.2558 EndZ=0
    g8: LineSegment StartX=-198.886 StartY=23.6499 StartZ=0 EndX=-192.308 EndY=21.2558 EndZ=0
    g9: LineSegment [constr] StartX=-187.821 StartY=29.2 StartZ=0 EndX=-188.505 EndY=27.3206 EndZ=0
  constraints (23):
    c: Symmetric(g-3,g-3,g0)
    c: Perpendicular(g1,g-3)
    c: Parallel(g2,g-3)
    c: Symmetric(g2,g2,g3)
    c: Perpendicular(g2,g4)
    c: Symmetric(g4,g4,g3)
    c: Distance(g2) = 14
    c: Distance(g4) = 7
    c: Distance(g1) = 5
    c: Parallel(g5,g4)
    c: Parallel(g7,g2)
    c: Symmetric(g5,g5,g2)
    c: Symmetric(g6,g6,g4)
    c: Symmetric(g7,g7,g4)
    c: Symmetric(g8,g8,g2)
    c: Coincident(g6,g5)
    c: Coincident(g7,g5)
    c: Coincident(g8,g7)
    c: Coincident(g3,g1)
    c: Coincident(g9,g0)
    c: Parallel(g9,g-3)
    c: Distance(g9) = 2
    c: Coincident(g1,g9)
FEATURE [Sketcher::SketchObject] Sketch058  label="buco esterno per SWITCH"
  ArcFitTolerance = 1e-06
  AttachmentSupport = -> [XZ_Plane]
  ExternalGeometry = -> [Sketch057]
  FullyConstrained = true
  MakeInternals = false
  MapMode = 5
  Placement = pos=(0,0,0) rot=(1,0,0;1.5708rad)
  sketch-geometry (12):
    g0: GeomPoint [constr] X=-190.809 Y=35.6086 Z=0
    g1: GeomPoint [constr] X=-196.492 Y=30.2278 Z=0
    g2: GeomPoint [constr] X=-189.914 Y=27.8336 Z=0
    g3: GeomPoint [constr] X=-195.597 Y=22.4529 Z=0
    g4: GeomPoint [constr] X=-193.203 Y=29.0307 Z=0
    g5: LineSegment [constr] StartX=-192.006 StartY=32.3196 StartZ=0 EndX=-194.4 EndY=25.7418 EndZ=0
    g6: GeomPoint [constr] X=-193.203 Y=29.0307 Z=0
    g7: LineSegment [constr] StartX=-195.082 StartY=29.7148 StartZ=0 EndX=-191.324 EndY=28.3467 EndZ=0
    g8: LineSegment StartX=-193.885 StartY=33.0037 StartZ=0 EndX=-190.127 EndY=31.6356 EndZ=0
    g9: LineSegment StartX=-190.127 StartY=31.6356 StartZ=0 EndX=-192.521 EndY=25.0578 EndZ=0
    g10: LineSegment StartX=-196.28 StartY=26.4258 StartZ=0 EndX=-192.521 EndY=25.0578 EndZ=0
    g11: LineSegment StartX=-193.885 StartY=33.0037 StartZ=0 EndX=-196.28 EndY=26.4258 EndZ=0
  constraints (21):
    c: Symmetric(g-6,g-6,g3)
    c: Symmetric(g-4,g-6,g2)
    c: Symmetric(g-5,g-4,g0)
    c: Symmetric(g-5,g-6,g1)
    c: Symmetric(g1,g2,g4)
    c: Parallel(g5,g-4)
    c: Symmetric(g5,g5,g6)
    c: Perpendicular(g7,g5)
    c: Symmetric(g7,g7,g6)
    c: Distance(g5) = 7
    c: Distance(g7) = 4
    c: Parallel(g8,g7)
    c: Parallel(g11,g5)
    c: Symmetric(g8,g8,g5)
    c: Symmetric(g9,g9,g7)
    c: Symmetric(g10,g10,g5)
    c: Symmetric(g11,g11,g7)
    c: Coincident(g11,g8)
    c: Coincident(g9,g8)
    c: Coincident(g9,g10)
    c: Coincident(g6,g4)
FEATURE [Part::Extrusion] Extrude060  label="Extrude buco interno per SWITCH destro"
  Base = -> Sketch057
  Dir = (0,-1,2e-16)
  DirMode = 2
  FaceMakerClass = Part::FaceMakerBullseye
  FaceMakerMode = 3
  LengthFwd = 13.2
  LengthRev = 0
  Placement = pos=(0,2.6,0) rot=(0,0,1;0rad)
  Solid = true
  Symmetric = false
FEATURE [Part::Extrusion] Extrude061  label="Extrude buco esterno per SWITCH destro"
  Base = -> Sketch058
  Dir = (0,-1,2e-16)
  DirMode = 2
  FaceMakerClass = Part::FaceMakerBullseye
  FaceMakerMode = 3
  LengthFwd = 2
  LengthRev = 0
  Placement = pos=(0,-10.6,0) rot=(0,0,1;0rad)
  Solid = true
  Symmetric = false
FEATURE [Sketcher::SketchObject] Sketch059  label="buco per spazio introduzione SWITCH"
  ArcFitTolerance = 1e-06
  AttachmentSupport = -> [XZ_Plane]
  ExternalGeometry = -> [Sketch057,Sketch010]
  FullyConstrained = true
  MakeInternals = false
  MapMode = 5
  Placement = pos=(0,0,0) rot=(1,0,0;1.5708rad)
  sketch-geometry (8):
    g0: LineSegment [constr] StartX=-201.368 StartY=36.3521 StartZ=0 EndX=-195.094 EndY=34.0687 EndZ=0
    g1: LineSegment [constr] StartX=-194.098 StartY=36.8056 StartZ=0 EndX=-195.094 EndY=34.0687 EndZ=0
    g2: LineSegment StartX=-198.658 StartY=24.2771 StartZ=0 EndX=-199.654 EndY=21.5401 EndZ=0
    g3: LineSegment StartX=-199.654 StartY=21.5401 StartZ=0 EndX=-181.196 EndY=14.822 EndZ=0
    g4: LineSegment StartX=-181.196 StartY=14.822 StartZ=0 EndX=-180.2 EndY=17.559 EndZ=0
    g5: LineSegment StartX=-180.2 StartY=17.559 StartZ=0 EndX=-198.658 EndY=24.2771 EndZ=0
    g6: LineSegment [constr] StartX=-204.932 StartY=26.5605 StartZ=0 EndX=-198.658 EndY=24.2771 EndZ=0
    g7: LineSegment [constr] StartX=-198.658 StartY=24.2771 StartZ=0 EndX=-199.654 EndY=21.5401 EndZ=0
  constraints (20):
    c: Parallel(g1,g-3)
    c: Parallel(g0,g-4)
    c: Coincident(g0,g-4)
    c: Coincident(g1,g-3)
    c: Coincident(g0,g1)
    c: Coincident(g3,g2)
    c: Coincident(g4,g3)
    c: Coincident(g5,g4)
    c: Coincident(g5,g2)
    c: Parallel(g5,g-5)
    c: Parallel(g3,g-5)
    c: Parallel(g4,g-6)
    c: DistanceX(g-6,g4) = 0
    c: Coincident(g6,g-5)
    c: Equal(g6,g0)
    c: Coincident(g7,g6)
    c: Equal(g7,g1)
    c: Tangent(g7,g-3)
    c: Coincident(g2,g6)
    c: Coincident(g2,g7)
FEATURE [Part::Extrusion] Extrude062  label="Extrude buco per spazio introduzione SWITCH"
  Base = -> Sketch059
  Dir = (0,-1,2e-16)
  DirMode = 2
  FaceMakerClass = Part::FaceMakerBullseye
  FaceMakerMode = 3
  LengthFwd = 13.2
  LengthRev = 0
  Solid = true
  Symmetric = true
FEATURE [Part::Extrusion] Extrude063  label="Extrude buco interno per SWITCH sinistro"
  Base = -> Sketch057
  Dir = (0,-1,2e-16)
  DirMode = 2
  FaceMakerClass = Part::FaceMakerBullseye
  FaceMakerMode = 3
  LengthFwd = 13.2
  LengthRev = 0
  Placement = pos=(0,10.6,0) rot=(0,0,1;0rad)
  Solid = true
  Symmetric = false
FEATURE [Part::Extrusion] Extrude064  label="Extrude buco esterno per SWITCH sinistro"
  Base = -> Sketch058
  Dir = (0,-1,2e-16)
  DirMode = 2
  FaceMakerClass = Part::FaceMakerBullseye
  FaceMakerMode = 3
  LengthFwd = 2
  LengthRev = 0
  Placement = pos=(0,12.6,0) rot=(0,0,1;0rad)
  Solid = true
  Symmetric = false
FEATURE [Sketcher::SketchObject] Sketch061  label="struttura esterna blocco switch"
  ArcFitTolerance = 1e-06
  AttachmentSupport = -> [XZ_Plane003]
  FullyConstrained = true
  MakeInternals = false
  MapMode = 5
  Placement = pos=(0,0,0) rot=(1,0,0;1.5708rad)
  sketch-geometry (5):
    g0: LineSegment StartX=-1 StartY=-5.1 StartZ=0 EndX=1 EndY=-5.1 EndZ=0
    g1: LineSegment StartX=1 StartY=-5.1 StartZ=0 EndX=1 EndY=5.1 EndZ=0
    g2: LineSegment StartX=1 StartY=5.1 StartZ=0 EndX=-1 EndY=5.1 EndZ=0
    g3: LineSegment StartX=-1 StartY=5.1 StartZ=0 EndX=-1 EndY=-5.1 EndZ=0
    g4: GeomPoint [constr] X=0 Y=0 Z=0
  constraints (12):
    c: Coincident(g0,g1)
    c: Coincident(g1,g2)
    c: Coincident(g2,g3)
    c: Coincident(g3,g0)
    c: Horizontal(g0)
    c: Horizontal(g2)
    c: Vertical(g1)
    c: Vertical(g3)
    c: Symmetric(g2,g0,g4)
    c: Distance(g1,g3) = 2
    c: Distance(g0,g2) = 10.2
    c: Coincident(g4,g-1)
FEATURE [Sketcher::SketchObject] Sketch062  label="struttura interna blocco switch"
  ArcFitTolerance = 1e-06
  AttachmentSupport = -> [XZ_Plane003]
  ExternalGeometry = -> [Sketch061]
  FullyConstrained = true
  MakeInternals = false
  MapMode = 5
  Placement = pos=(0,0,0) rot=(1,0,0;1.5708rad)
  sketch-geometry (5):
    g0: LineSegment StartX=-1 StartY=3.1 StartZ=0 EndX=-1 EndY=-3.1 EndZ=0
    g1: LineSegment StartX=-1 StartY=-3.1 StartZ=0 EndX=1 EndY=-3.1 EndZ=0
    g2: LineSegment StartX=1 StartY=-3.1 StartZ=0 EndX=1 EndY=3.1 EndZ=0
    g3: LineSegment StartX=1 StartY=3.1 StartZ=0 EndX=-1 EndY=3.1 EndZ=0
    g4: GeomPoint [constr] X=0 Y=0 Z=0
  constraints (12):
    c: Coincident(g0,g1)
    c: Coincident(g1,g2)
    c: Coincident(g2,g3)
    c: Coincident(g3,g0)
    c: Vertical(g0)
    c: Vertical(g2)
    c: Horizontal(g1)
    c: Horizontal(g3)
    c: Symmetric(g2,g0,g4)
    c: Coincident(g4,g-1)
    c: Distance(g0) = 6.2
    c: Equal(g3,g-3)
FEATURE [Sketcher::SketchObject] Sketch063  label="blocchi tra switch"
  ArcFitTolerance = 1e-06
  AttachmentSupport = -> [XZ_Plane003]
  ExternalGeometry = -> [Sketch061,Sketch062]
  FullyConstrained = true
  MakeInternals = false
  MapMode = 5
  Placement = pos=(0,0,0) rot=(1,0,0;1.5708rad)
  sketch-geometry (8):
    g0: LineSegment StartX=-3 StartY=5.1 StartZ=0 EndX=-1 EndY=5.1 EndZ=0
    g1: LineSegment StartX=-1 StartY=5.1 StartZ=0 EndX=-1 EndY=3.1 EndZ=0
    g2: LineSegment StartX=-1 StartY=3.1 StartZ=0 EndX=-3 EndY=3.1 EndZ=0
    g3: LineSegment StartX=-3 StartY=3.1 StartZ=0 EndX=-3 EndY=5.1 EndZ=0
    g4: LineSegment StartX=-3 StartY=-3.1 StartZ=0 EndX=-1 EndY=-3.1 EndZ=0
    g5: LineSegment StartX=-1 StartY=-3.1 StartZ=0 EndX=-1 EndY=-5.1 EndZ=0
    g6: LineSegment StartX=-1 StartY=-5.1 StartZ=0 EndX=-3 EndY=-5.1 EndZ=0
    g7: LineSegment StartX=-3 StartY=-5.1 StartZ=0 EndX=-3 EndY=-3.1 EndZ=0
  constraints (20):
    c: Horizontal(g0)
    c: Coincident(g1,g0)
    c: Coincident(g2,g1)
    c: Horizontal(g2)
    c: Coincident(g3,g2)
    c: Coincident(g3,g0)
    c: Vertical(g3)
    c: Horizontal(g4)
    c: Coincident(g5,g4)
    c: Coincident(g6,g5)
    c: Horizontal(g6)
    c: Coincident(g7,g6)
    c: Coincident(g7,g4)
    c: Vertical(g7)
    c: Coincident(g0,g-4)
    c: Coincident(g1,g-5)
    c: Coincident(g4,g-6)
    c: Coincident(g5,g-7)
    c: Distance(g0) = 2
    c: Distance(g4) = 2
FEATURE [Sketcher::SketchObject] Sketch066  label="piano per rampino"
  ArcFitTolerance = 1e-06
  AttachmentSupport = -> [XZ_Plane002]
  ExternalGeometry = -> [Sketch045]
  FullyConstrained = true
  MakeInternals = false
  MapMode = 5
  Placement = pos=(0,0,0) rot=(1,0,0;1.5708rad)
  sketch-geometry (4):
    g0: LineSegment StartX=5.4 StartY=5.1 StartZ=0 EndX=5.4 EndY=3.9 EndZ=0
    g1: LineSegment StartX=5.4 StartY=3.9 StartZ=0 EndX=7 EndY=3.9 EndZ=0
    g2: LineSegment StartX=7 StartY=3.9 StartZ=0 EndX=7 EndY=5.1 EndZ=0
    g3: LineSegment StartX=7 StartY=5.1 StartZ=0 EndX=5.4 EndY=5.1 EndZ=0
  constraints (11):
    c: Coincident(g0,g1)
    c: Coincident(g1,g2)
    c: Coincident(g2,g3)
    c: Coincident(g3,g0)
    c: Vertical(g0)
    c: Vertical(g2)
    c: Horizontal(g1)
    c: Horizontal(g3)
    c: Distance(g0,g2) = 1.6
    c: Distance(g1,g3) = 1.2
    c: Coincident(g2,g-3)
FEATURE [Sketcher::SketchObject] Sketch064  label="rampini_per_serraggio_struttura"
  ArcFitTolerance = 1e-06
  AttachmentSupport = -> [XZ_Plane002]
  ExternalGeometry = -> [Sketch066,Sketch045]
  FullyConstrained = true
  MakeInternals = false
  MapMode = 5
  Placement = pos=(0,0,0) rot=(1,0,0;1.5708rad)
  sketch-geometry (7):
    g0: LineSegment StartX=7 StartY=5.1 StartZ=0 EndX=7 EndY=3.9 EndZ=0
    g1: LineSegment StartX=7 StartY=3.9 StartZ=0 EndX=9 EndY=3.9 EndZ=0
    g2: LineSegment StartX=7 StartY=5.1 StartZ=0 EndX=7 EndY=5.1 EndZ=0
    g3: LineSegment StartX=7 StartY=5.1 StartZ=0 EndX=7 EndY=7.5 EndZ=0
    g4: LineSegment StartX=9 StartY=5.1 StartZ=0 EndX=9 EndY=3.9 EndZ=0
    g5: LineSegment StartX=7 StartY=7.5 StartZ=0 EndX=9 EndY=7.5 EndZ=0
    g6: LineSegment StartX=9 StartY=7.5 StartZ=0 EndX=9 EndY=5.1 EndZ=0
  constraints (20):
    c: Vertical(g0)
    c: Coincident(g1,g0)
    c: Horizontal(g1)
    c: Coincident(g2,g0)
    c: Horizontal(g2)
    c: Coincident(g3,g2)
    c: Vertical(g3)
    c: Coincident(g5,g3)
    c: Coincident(g4,g6)
    c: Coincident(g4,g1)
    c: Vertical(g4)
    c: Coincident(g0,g-3)
    c: DistanceY(g-4,g3) = 2.4
    c: DistanceX(g1,g1) = 2
    c: DistanceY(g2,g6) = 0
    c: DistanceX(g2,g2) = 0
    c: DistanceY(g0,g0) = 1.2
    c: Coincident(g5,g6)
    c: Horizontal(g5)
    c: Vertical(g6)
FEATURE [Sketcher::SketchObject] Sketch067  label="perno per blocco switch"
  ArcFitTolerance = 1e-06
  AttachmentSupport = -> [XZ_Plane]
  ExternalGeometry = -> [Sketch,Sketch010]
  FullyConstrained = true
  MakeInternals = false
  MapMode = 5
  Placement = pos=(0,0,0) rot=(1,0,0;1.5708rad)
  sketch-geometry (14):
    g0: LineSegment StartX=-191.073 StartY=24.9429 StartZ=0 EndX=-185.81 EndY=23.0276 EndZ=0
    g1: LineSegment StartX=-183.76 StartY=23.9839 StartZ=0 EndX=-182.392 EndY=27.7427 EndZ=0
    g2: LineSegment StartX=-183.348 StartY=29.7934 StartZ=0 EndX=-188.61 EndY=31.7087 EndZ=0
    g3: LineSegment StartX=-188.61 StartY=31.7087 StartZ=0 EndX=-191.073 EndY=24.9429 EndZ=0
    g4: GeomPoint [constr] X=-186.459 Y=27.0946 Z=0
    g5: LineSegment StartX=-189.022 StartY=25.8992 StartZ=0 EndX=-185.263 EndY=24.5311 EndZ=0
    g6: LineSegment StartX=-185.263 StartY=24.5311 StartZ=0 EndX=-183.895 EndY=28.2899 EndZ=0
    g7: LineSegment StartX=-183.895 StartY=28.2899 StartZ=0 EndX=-187.654 EndY=29.658 EndZ=0
    g8: LineSegment StartX=-187.654 StartY=29.658 StartZ=0 EndX=-189.022 EndY=25.8992 EndZ=0
    g9: GeomPoint [constr] X=-186.459 Y=27.0946 Z=0
    g10: ArcOfCircle CenterX=-185.263 CenterY=24.5311 CenterZ=0 NormalX=0 NormalY=0 NormalZ=1 AngleXU=0 Radius=1.6 StartAngle=4.36332 EndAngle=5.93412
    g11: GeomPoint [constr] X=-184.307 Y=22.4804 Z=0
    g12: ArcOfCircle CenterX=-183.895 CenterY=28.2899 CenterZ=0 NormalX=0 NormalY=0 NormalZ=1 AngleXU=0 Radius=1.6 StartAngle=5.93412 EndAngle=7.50492
    g13: GeomPoint [constr] X=-181.844 Y=29.2462 Z=0
  constraints (30):
    c: Coincident(g2,g3)
    c: Coincident(g3,g0)
    c: Symmetric(g13,g0,g4)
    c: Distance(g11,g3) = 7.2
    c: Distance(g0,g2) = 7.2
    c: Parallel(g3,g1)
    c: Parallel(g2,g0)
    c: Perpendicular(g2,g3)
    c: Coincident(g5,g6)
    c: Coincident(g6,g7)
    c: Coincident(g7,g8)
    c: Coincident(g8,g5)
    c: Symmetric(g7,g5,g9)
    c: Distance(g6,g8) = 4
    c: Distance(g5,g7) = 4
    c: Coincident(g9,g4)
    c: Parallel(g8,g6)
    c: Parallel(g7,g5)
    c: Perpendicular(g7,g8)
    c: Tangent(g8,g-3)
    c: Tangent(g2,g-4)
    c: PointOnObject(g11,g1)
    c: PointOnObject(g11,g0)
    c: Tangent(g1,g10) = -1.5708
    c: Tangent(g0,g10) = -1.5708
    c: PointOnObject(g13,g1)
    c: Tangent(g1,g12) = -1.5708
    c: Tangent(g2,g12) = -1.5708
    c: Equal(g10,g12)
    c: Coincident(g10,g5)
FEATURE [Part::Extrusion] Extrude072  label="Extrude perno per blocco switch"
  Base = -> Sketch067
  Dir = (0,-1,2e-16)
  DirMode = 2
  FaceMakerClass = Part::FaceMakerBullseye
  FaceMakerMode = 3
  LengthFwd = 25.2
  LengthRev = 0
  Solid = true
  Symmetric = true
FEATURE [Part::MultiFuse] Fusion
  Refine = true
  Shapes = -> [Extrude,Sweep,Extrude007,Extrude011,Extrude005,Extrude012,Extrude013,Extrude016,Extrude031,Extrude039,Extrude045,Extrude072]
FEATURE [Part::Cut] Cut
  Base = -> Fusion
  Refine = true
  Tool = -> Extrude001
FEATURE [Part::Cut] Cut001
  Base = -> Cut
  Refine = true
  Tool = -> Extrude004
FEATURE [Part::Cut] Cut002
  Base = -> Cut001
  Refine = true
  Tool = -> Extrude006
FEATURE [Part::Cut] Cut003
  Base = -> Cut002
  Refine = true
  Tool = -> Extrude008
FEATURE [Part::Cut] Cut004
  Base = -> Cut003
  Refine = true
  Tool = -> Extrude009
FEATURE [Part::Cut] Cut005
  Base = -> Cut004
  Refine = true
  Tool = -> Extrude010
FEATURE [Part::Cut] Cut006
  Base = -> Cut005
  Refine = true
  Tool = -> Extrude014
FEATURE [Part::Cut] Cut007
  Base = -> Cut006
  Refine = true
  Tool = -> Extrude015
FEATURE [Part::Cut] Cut008
  Base = -> Cut007
  Refine = true
  Tool = -> Extrude018
FEATURE [Part::Cut] Cut009
  Base = -> Cut008
  Refine = true
  Tool = -> Extrude019
FEATURE [Part::Cut] Cut010
  Base = -> Cut009
  Refine = true
  Tool = -> Extrude020
FEATURE [Part::Cut] Cut011
  Base = -> Cut010
  Refine = true
  Tool = -> Extrude021
FEATURE [Part::Cut] Cut012
  Base = -> Cut011
  Refine = true
  Tool = -> Extrude022
FEATURE [Part::Cut] Cut013
  Base = -> Cut012
  Refine = true
  Tool = -> Extrude023
FEATURE [Part::Cut] Cut014
  Base = -> Cut013
  Refine = true
  Tool = -> Extrude032
FEATURE [Part::Cut] Cut015
  Base = -> Cut014
  Refine = true
  Tool = -> Extrude033
FEATURE [Part::Cut] Cut016
  Base = -> Cut015
  Refine = true
  Tool = -> Extrude034
FEATURE [Part::Cut] Cut017
  Base = -> Cut016
  Refine = true
  Tool = -> Extrude035
FEATURE [Part::Cut] Cut018
  Base = -> Cut017
  Refine = true
  Tool = -> Extrude036
FEATURE [Part::Cut] Cut019
  Base = -> Cut018
  Refine = true
  Tool = -> Extrude037
FEATURE [Part::Cut] Cut020
  Base = -> Cut019
  Refine = true
  Tool = -> Extrude030
FEATURE [Part::Cut] Cut022
  Base = -> Cut020
  Refine = true
  Tool = -> Extrude038
FEATURE [Part::Cut] Cut023
  Base = -> Cut022
  Refine = true
  Tool = -> Extrude041
FEATURE [Part::Cut] Cut024
  Base = -> Cut023
  Refine = true
  Tool = -> Extrude040
FEATURE [Part::Cut] Cut025
  Base = -> Cut024
  Refine = true
  Tool = -> Extrude042
FEATURE [Part::Cut] Cut026
  Base = -> Cut025
  Refine = true
  Tool = -> Extrude043
FEATURE [Part::Cut] Cut027
  Base = -> Cut026
  Refine = true
  Tool = -> Extrude044
FEATURE [Part::Cut] Cut028
  Base = -> Cut027
  Refine = true
  Tool = -> Extrude046
FEATURE [Part::Cut] Cut029
  Base = -> Cut028
  Refine = true
  Tool = -> Extrude047
FEATURE [Part::Cut] Cut033
  Base = -> Cut029
  Refine = true
  Tool = -> Extrude055
FEATURE [Part::Cut] Cut034
  Base = -> Cut033
  Refine = true
  Tool = -> Extrude056
FEATURE [Part::Cut] Cut035
  Base = -> Cut034
  Refine = true
  Tool = -> Extrude057
FEATURE [Part::Cut] Cut037
  Base = -> Cut035
  Refine = true
  Tool = -> Extrude060
FEATURE [Part::Cut] Cut038
  Base = -> Cut037
  Refine = true
  Tool = -> Extrude061
FEATURE [Part::Cut] Cut039
  Base = -> Cut038
  Refine = true
  Tool = -> Extrude063
FEATURE [Part::Cut] Cut040
  Base = -> Cut039
  Refine = true
  Tool = -> Extrude064
FEATURE [Part::Cut] Cut041
  Base = -> Cut040
  Refine = true
  Tool = -> Extrude062
FEATURE [Sketcher::SketchObject] Sketch068  label="base con smusso sopra neopixel"
  ArcFitTolerance = 1e-06
  AttachmentSupport = -> [YZ_Plane002]
  FullyConstrained = true
  MakeInternals = false
  MapMode = 5
  Placement = pos=(0,0,0) rot=(0.57735,0.57735,0.57735;2.0944rad)
  sketch-geometry (5):
    g0: LineSegment StartX=-9.5 StartY=-6.1 StartZ=0 EndX=9.5 EndY=-6.1 EndZ=0
    g1: LineSegment StartX=9.5 StartY=-6.1 StartZ=0 EndX=9.5 EndY=6.1 EndZ=0
    g2: LineSegment StartX=9.5 StartY=6.1 StartZ=0 EndX=-9.5 EndY=6.1 EndZ=0
    g3: LineSegment StartX=-9.5 StartY=6.1 StartZ=0 EndX=-9.5 EndY=-6.1 EndZ=0
    g4: GeomPoint [constr] X=0 Y=0 Z=0
  constraints (12):
    c: Coincident(g0,g1)
    c: Coincident(g1,g2)
    c: Coincident(g2,g3)
    c: Coincident(g3,g0)
    c: Horizontal(g0)
    c: Horizontal(g2)
    c: Vertical(g1)
    c: Vertical(g3)
    c: Symmetric(g2,g0,g4)
    c: Distance(g1,g3) = 19
    c: Distance(g0,g2) = 12.2
    c: Coincident(g4,g-1)
FEATURE [Sketcher::SketchObject] Sketch069  label="cilindro minore"
  ArcFitTolerance = 1e-06
  AttachmentSupport = -> [XZ_Plane004]
  FullyConstrained = true
  MakeInternals = false
  MapMode = 5
  Placement = pos=(0,0,0) rot=(1,0,0;1.5708rad)
  sketch-geometry (1):
    g0: Circle CenterX=0 CenterY=0 CenterZ=0 NormalX=0 NormalY=0 NormalZ=1 AngleXU=0 Radius=5.8
  constraints (2):
    c: Diameter(g0) = 11.6
    c: Coincident(g0,g-1)
FEATURE [Sketcher::SketchObject] Sketch070  label="cilindro maggiore"
  ArcFitTolerance = 1e-06
  AttachmentSupport = -> [XZ_Plane004]
  ExternalGeometry = -> [Sketch069]
  FullyConstrained = true
  MakeInternals = false
  MapMode = 5
  Placement = pos=(0,0,0) rot=(1,0,0;1.5708rad)
  sketch-geometry (1):
    g0: Circle CenterX=0 CenterY=0 CenterZ=0 NormalX=0 NormalY=0 NormalZ=1 AngleXU=0 Radius=6.5
  constraints (2):
    c: Coincident(g0,g-1)
    c: Diameter(g0) = 13
FEATURE [Sketcher::SketchObject] Sketch071  label="buco interno"
  ArcFitTolerance = 1e-06
  AttachmentSupport = -> [XZ_Plane004]
  ExternalGeometry = -> [Sketch069]
  FullyConstrained = true
  MakeInternals = false
  MapMode = 5
  Placement = pos=(0,0,0) rot=(1,0,0;1.5708rad)
  sketch-geometry (1):
    g0: Circle CenterX=0 CenterY=0 CenterZ=0 NormalX=0 NormalY=0 NormalZ=1 AngleXU=0 Radius=5
  constraints (2):
    c: Coincident(g0,g-1)
    c: Diameter(g0) = 10
FEATURE [PartDesign::Pad] Pad
  Direction = (0,-1,2e-16)
  Length = 1.2
  Length2 = 10
  Placement = pos=(0,0,0) rot=(1,0,0;1.5708rad)
  Profile = -> Sketch070
  ReferenceAxis = -> Sketch070 [N_Axis]
  Refine = true
  Suppressed = false
  Type = 0
FEATURE [PartDesign::Pad] Pad001
  BaseFeature = -> Pad
  Direction = (0,-1,2e-16)
  Length = 5.6
  Length2 = 10
  Placement = pos=(0,0,0) rot=(1,0,0;1.5708rad)
  Profile = -> Sketch069
  ReferenceAxis = -> Sketch069 [N_Axis]
  Refine = true
  Suppressed = false
  Type = 0
FEATURE [PartDesign::Pocket] Pocket
  BaseFeature = -> Pad001
  Direction = (0,1,-2e-16)
  Length = 7
  Length2 = 5
  Midplane = true
  Placement = pos=(0,0,0) rot=(1,0,0;1.5708rad)
  Profile = -> Sketch071
  ReferenceAxis = -> Sketch071 [N_Axis]
  Refine = true
  Suppressed = false
  Type = 0
FEATURE [PartDesign::Fillet] Fillet
  Base = -> Pocket [Face7]
  BaseFeature = -> Pocket
  Placement = pos=(0,0,0) rot=(1,0,0;1.5708rad)
  Radius = 1
  Refine = true
  SupportTransform = false
  Suppressed = false
  UseAllEdges = false
FEATURE [PartDesign::Body] Body004  label="pulsanti lato sinistro"
  AllowCompound = false
  Group = -> [Sketch069,Sketch070,Sketch071,Pad,Pad001,Pocket,Fillet]
  Origin = -> Origin004
  Tip = -> Fillet
FEATURE [Sketcher::SketchObject] Sketch072  label="buco per saldature e diodo driver solenoide"
  ArcFitTolerance = 1e-06
  AttachmentSupport = -> [XZ_Plane]
  ExternalGeometry = -> [Sketch038]
  FullyConstrained = true
  MakeInternals = false
  MapMode = 5
  Placement = pos=(0,0,0) rot=(1,0,0;1.5708rad)
  sketch-geometry (4):
    g0: LineSegment StartX=-212.269 StartY=-43.9083 StartZ=0 EndX=-207.197 EndY=-33.0326 EndZ=0
    g1: LineSegment StartX=-207.197 StartY=-33.0326 StartZ=0 EndX=-207.56 EndY=-32.8635 EndZ=0
    g2: LineSegment StartX=-207.56 StartY=-32.8635 StartZ=0 EndX=-212.631 EndY=-43.7392 EndZ=0
    g3: LineSegment StartX=-212.631 StartY=-43.7392 StartZ=0 EndX=-212.269 EndY=-43.9083 EndZ=0
  constraints (11):
    c: Coincident(g1,g0)
    c: Coincident(g2,g1)
    c: Coincident(g3,g2)
    c: Coincident(g3,g0)
    c: Parallel(g-3,g0)
    c: Parallel(g0,g2)
    c: Perpendicular(g0,g3)
    c: Perpendicular(g1,g0)
    c: Distance(g3) = 0.4
    c: Distance(g2) = 12
    c: Coincident(g0,g-3)
FEATURE [Part::Extrusion] Extrude074  label="Extrude buco per saldature e diodo driver solenoide"
  Base = -> Sketch072
  Dir = (0,-1,2e-16)
  DirMode = 2
  FaceMakerClass = Part::FaceMakerBullseye
  FaceMakerMode = 3
  LengthFwd = 14.6
  LengthRev = 0
  Solid = true
  Symmetric = true
FEATURE [Part::Cut] Cut042
  Base = -> Cut041
  Refine = true
  Tool = -> Extrude074
FEATURE [Sketcher::SketchObject] Sketch073  label="fori slargati blocco solenoide"
  ArcFitTolerance = 1e-06
  AttachmentSupport = -> [XY_Plane]
  ExternalGeometry = -> [Sketch030]
  FullyConstrained = true
  MakeInternals = false
  MapMode = 5
  sketch-geometry (2):
    g0: Circle CenterX=-152.209 CenterY=6.95 CenterZ=0 NormalX=0 NormalY=0 NormalZ=1 AngleXU=0 Radius=3.7
    g1: Circle CenterX=-130.41 CenterY=-6.95 CenterZ=0 NormalX=0 NormalY=0 NormalZ=1 AngleXU=0 Radius=3.7
  constraints (4):
    c: Diameter(g0) = 7.4
    c: Coincident(g0,g-3)
    c: Diameter(g1) = 7.4
    c: Coincident(g1,g-4)
FEATURE [Part::Extrusion] Extrude075  label="Extrude fori slargati blocco solenoide"
  Base = -> Sketch073
  Dir = (0,0,1)
  DirMode = 2
  FaceMakerClass = Part::FaceMakerBullseye
  FaceMakerMode = 3
  LengthFwd = 1.5
  LengthRev = 0
  Placement = pos=(0,0,36.4) rot=(0,0,1;0rad)
  Solid = true
  Symmetric = false
FEATURE [Part::Cut] Cut043
  Base = -> Cut042
  Refine = true
  Tool = -> Extrude075
FEATURE [Sketcher::SketchObject] Sketch074  label="lato sx pistola"
  ArcFitTolerance = 1e-06
  AttachmentSupport = -> [XZ_Plane]
  ExternalGeometry = -> [Sketch016,Sketch,Sketch058]
  FullyConstrained = true
  MakeInternals = false
  MapMode = 5
  Placement = pos=(0,0,0) rot=(1,0,0;1.5708rad)
  sketch-geometry (37):
    g0: LineSegment StartX=-82.8 StartY=3.2 StartZ=0 EndX=0 EndY=3.2 EndZ=0
    g1: LineSegment StartX=-82.8 StartY=3.2 StartZ=0 EndX=-82.8 EndY=6.2 EndZ=0
    g2: LineSegment [constr] StartX=-107.6 StartY=18 StartZ=0 EndX=-107.6 EndY=20 EndZ=0
    g3: LineSegment [constr] StartX=-132.428 StartY=18 StartZ=0 EndX=-132.428 EndY=20 EndZ=0
    g4: LineSegment StartX=-132.428 StartY=20 StartZ=0 EndX=-107.6 EndY=20 EndZ=0
    g5: ArcOfCircle CenterX=-107.6 CenterY=4 CenterZ=0 NormalX=0 NormalY=0 NormalZ=1 AngleXU=0 Radius=16 StartAngle=0.137937 EndAngle=1.5708
    g6: LineSegment StartX=-82.8 StartY=6.2 StartZ=0 EndX=-91.752 EndY=6.2 EndZ=0
    g7: LineSegment [constr] StartX=-145.743 StartY=8.32624 StartZ=0 EndX=-147.645 EndY=8.94427 EndZ=0
    g8: ArcOfCircle CenterX=-132.428 CenterY=4 CenterZ=0 NormalX=0 NormalY=0 NormalZ=1 AngleXU=0 Radius=16 StartAngle=1.5708 EndAngle=2.82743
    g9: LineSegment StartX=-215.932 StartY=-80.4316 StartZ=0 EndX=-176.685 EndY=-80.4316 EndZ=0
    g10: LineSegment StartX=-147.645 StartY=8.94427 StartZ=0 EndX=-176.685 EndY=-80.4316 EndZ=0
    g11: LineSegment [constr] StartX=-193.988 StartY=-2.33927 StartZ=0 EndX=-192.176 EndY=-3.18451 EndZ=0
    g12: LineSegment [constr] StartX=-217.232 StartY=-52.1862 StartZ=0 EndX=-215.42 EndY=-53.0314 EndZ=0
    g13: LineSegment StartX=-192.176 StartY=-3.18451 StartZ=0 EndX=-215.42 EndY=-53.0314 EndZ=0
    g14: ArcOfCircle CenterX=-184.801 CenterY=-67.3089 CenterZ=0 NormalX=0 NormalY=0 NormalZ=1 AngleXU=0 Radius=33.7833 StartAngle=2.70526 EndAngle=3.54053
    g15: ArcOfCircle CenterX=-207.583 CenterY=4 CenterZ=0 NormalX=0 NormalY=0 NormalZ=1 AngleXU=0 Radius=17 StartAngle=5.84685 EndAngle=7.56663
    g16: LineSegment StartX=-202.765 StartY=20.303 StartZ=0 EndX=-195.887 EndY=39.2 EndZ=0
    g17: LineSegment [constr] StartX=-193.885 StartY=33.0037 StartZ=0 EndX=-197.644 EndY=34.3718 EndZ=0
    g18: LineSegment StartX=-195.887 StartY=39.2 StartZ=0 EndX=0 EndY=39.2 EndZ=0
    g19: LineSegment StartX=0 StartY=3.2 StartZ=0 EndX=0 EndY=39.2 EndZ=0
    g20: LineSegment StartX=-189.939 StartY=31.5672 StartZ=0 EndX=-192.333 EndY=24.9893 EndZ=0
    g21: LineSegment StartX=-196.467 StartY=26.4942 StartZ=0 EndX=-194.073 EndY=33.0721 EndZ=0
    g22: Circle CenterX=-213.443 CenterY=-76.8316 CenterZ=0 NormalX=0 NormalY=0 NormalZ=1 AngleXU=0 Radius=1.8
    g23: Circle CenterX=-179.305 CenterY=-76.8316 CenterZ=0 NormalX=0 NormalY=0 NormalZ=1 AngleXU=0 Radius=1.8
    g24: Circle CenterX=-184.08 CenterY=34.8 CenterZ=0 NormalX=0 NormalY=0 NormalZ=1 AngleXU=0 Radius=1.8
    g25: Circle CenterX=-78.51 CenterY=34.8 CenterZ=0 NormalX=0 NormalY=0 NormalZ=1 AngleXU=0 Radius=1.8
    g26: Circle CenterX=-78.51 CenterY=7.6 CenterZ=0 NormalX=0 NormalY=0 NormalZ=1 AngleXU=0 Radius=1.8
    g27: Circle CenterX=-5.6 CenterY=34.8 CenterZ=0 NormalX=0 NormalY=0 NormalZ=1 AngleXU=0 Radius=1.8
    g28: Circle CenterX=-5.6 CenterY=7.6 CenterZ=0 NormalX=0 NormalY=0 NormalZ=1 AngleXU=0 Radius=1.8
    g29: LineSegment StartX=-190.127 StartY=31.6356 StartZ=0 EndX=-189.939 EndY=31.5672 EndZ=0
    g30: LineSegment StartX=-194.073 StartY=33.0721 StartZ=0 EndX=-193.885 EndY=33.0037 EndZ=0
    g31: LineSegment StartX=-193.885 StartY=33.0037 StartZ=0 EndX=-190.127 EndY=31.6356 EndZ=0
    g32: LineSegment StartX=-196.467 StartY=26.4942 StartZ=0 EndX=-192.333 EndY=24.9893 EndZ=0
    g33: Circle CenterX=-19 CenterY=21.2 CenterZ=0 NormalX=0 NormalY=0 NormalZ=1 AngleXU=0 Radius=6.3
    g34: Circle CenterX=-42 CenterY=21.2 CenterZ=0 NormalX=0 NormalY=0 NormalZ=1 AngleXU=0 Radius=6.3
    g35: Circle CenterX=-65 CenterY=21.2 CenterZ=0 NormalX=0 NormalY=0 NormalZ=1 AngleXU=0 Radius=6.3
    g36: LineSegment [constr] StartX=-4 StartY=21.2 StartZ=0 EndX=-65 EndY=21.2 EndZ=0
  constraints (96):
    c: Coincident(g0,g-41)
    c: Horizontal(g0)
    c: PointOnObject(g0,g-39)
    c: Coincident(g1,g0)
    c: Vertical(g1)
    c: DistanceY(g1,g1) = 3
    c: Coincident(g2,g-17)
    c: Vertical(g2)
    c: Coincident(g3,g-16)
    c: Vertical(g3)
    c: DistanceY(g2,g2) = 2
    c: DistanceY(g3,g3) = 2
    c: Coincident(g4,g3)
    c: Coincident(g4,g2)
    c: Coincident(g5,g-17)
    c: Coincident(g5,g2)
    c: Coincident(g6,g1)
    c: Horizontal(g6)
    c: Coincident(g6,g5)
    c: Coincident(g7,g-15)
    c: Coincident(g8,g7)
    c: Coincident(g8,g3)
    c: Coincident(g8,g-15)
    c: Horizontal(g9)
    c: DistanceY(g-13,g9) = 2
    c: Coincident(g10,g7)
    c: Parallel(g10,g-14)
    c: Coincident(g9,g10)
    c: Distance(g11) = 2
    c: Coincident(g11,g-11)
    c: Perpendicular(g-11,g11)
    c: Distance(g12) = 2
    c: Coincident(g12,g-12)
    c: Perpendicular(g-11,g12)
    c: Coincident(g13,g11)
    c: Coincident(g13,g12)
    c: Coincident(g14,g-32)
    c: Coincident(g14,g12)
    c: Coincident(g14,g9)
    c: Coincident(g15,g-10)
    c: Coincident(g15,g11)
    c: Parallel(g16,g-22)
    c: Distance(g17) = 4
    c: PointOnObject(g17,g16)
    c: Coincident(g15,g16)
    c: Horizontal(g18)
    c: Coincident(g18,g16)
    c: Coincident(g19,g0)
    c: PointOnObject(g19,g-39)
    c: DistanceY(g19,g-36) = 2
    c: Coincident(g18,g19)
    c: Diameter(g22) = 3.6
    c: Coincident(g22,g-9)
    c: Diameter(g23) = 3.6
    c: Coincident(g23,g-8)
    c: Diameter(g24) = 3.6
    c: Diameter(g25) = 3.6
    c: Diameter(g26) = 3.6
    c: Diameter(g27) = 3.6
    c: Diameter(g28) = 3.6
    c: Coincident(g27,g-4)
    c: Coincident(g28,g-3)
    c: Coincident(g25,g-6)
    c: Coincident(g26,g-5)
    c: Coincident(g24,g-7)
    c: Parallel(g20,g-21)
    c: Equal(g20,g-21)
    c: Parallel(g21,g-19)
    c: Equal(g21,g-19)
    c: Distance(g29) = 0.2
    c: Distance(g30) = 0.2
    c: Parallel(g29,g-20)
    c: Parallel(g31,g-20)
    c: Equal(g31,g-20)
    c: Coincident(g30,g31)
    c: Coincident(g31,g29)
    c: Coincident(g29,g-21)
    c: Parallel(g30,g31)
    c: Coincident(g17,g30)
    c: Coincident(g20,g29)
    c: Coincident(g21,g30)
    c: Perpendicular(g16,g17)
    c: Coincident(g32,g21)
    c: Coincident(g32,g20)
    c: Perpendicular(g10,g7)
    c: Diameter(g33) = 12.6
    c: Diameter(g34) = 12.6
    c: Diameter(g35) = 12.6
    c: Horizontal(g36)
    c: PointOnObject(g33,g36)
    c: PointOnObject(g34,g36)
    c: DistanceX(g34,g33) = 23
    c: DistanceX(g35,g34) = 23
    c: DistanceX(g33,g36) = 15
    c: Symmetric(g-24,g-24,g36)
    c: Coincident(g36,g35)
FEATURE [Sketcher::SketchObject] Sketch075  label="lato dx pistola"
  ArcFitTolerance = 1e-06
  AttachmentSupport = -> [XZ_Plane]
  ExternalGeometry = -> [Sketch016,Sketch,Sketch058,Sketch074]
  FullyConstrained = true
  MakeInternals = false
  MapMode = 5
  Placement = pos=(0,0,0) rot=(1,0,0;1.5708rad)
  sketch-geometry (61):
    g0: LineSegment StartX=-82.8 StartY=3.2 StartZ=0 EndX=0 EndY=3.2 EndZ=0
    g1: LineSegment StartX=-82.8 StartY=3.2 StartZ=0 EndX=-82.8 EndY=6.2 EndZ=0
    g2: LineSegment [constr] StartX=-107.6 StartY=18 StartZ=0 EndX=-107.6 EndY=20 EndZ=0
    g3: LineSegment [constr] StartX=-132.428 StartY=18 StartZ=0 EndX=-132.428 EndY=20 EndZ=0
    g4: LineSegment StartX=-132.428 StartY=20 StartZ=0 EndX=-107.6 EndY=20 EndZ=0
    g5: ArcOfCircle CenterX=-107.6 CenterY=4 CenterZ=0 NormalX=0 NormalY=0 NormalZ=1 AngleXU=0 Radius=16 StartAngle=0.137937 EndAngle=1.5708
    g6: LineSegment StartX=-82.8 StartY=6.2 StartZ=0 EndX=-91.752 EndY=6.2 EndZ=0
    g7: LineSegment [constr] StartX=-145.743 StartY=8.32624 StartZ=0 EndX=-147.645 EndY=8.94427 EndZ=0
    g8: ArcOfCircle CenterX=-132.428 CenterY=4 CenterZ=0 NormalX=0 NormalY=0 NormalZ=1 AngleXU=0 Radius=16 StartAngle=1.5708 EndAngle=2.82743
    g9: LineSegment StartX=-215.932 StartY=-80.4316 StartZ=0 EndX=-176.685 EndY=-80.4316 EndZ=0
    g10: LineSegment StartX=-147.645 StartY=8.94427 StartZ=0 EndX=-176.685 EndY=-80.4316 EndZ=0
    g11: LineSegment [constr] StartX=-193.988 StartY=-2.33927 StartZ=0 EndX=-192.176 EndY=-3.18451 EndZ=0
    g12: LineSegment [constr] StartX=-217.232 StartY=-52.1862 StartZ=0 EndX=-215.42 EndY=-53.0314 EndZ=0
    g13: LineSegment StartX=-192.176 StartY=-3.18451 StartZ=0 EndX=-215.42 EndY=-53.0314 EndZ=0
    g14: ArcOfCircle CenterX=-184.801 CenterY=-67.3089 CenterZ=0 NormalX=0 NormalY=0 NormalZ=1 AngleXU=0 Radius=33.7833 StartAngle=2.70526 EndAngle=3.54053
    g15: ArcOfCircle CenterX=-207.583 CenterY=4 CenterZ=0 NormalX=0 NormalY=0 NormalZ=1 AngleXU=0 Radius=17 StartAngle=5.84685 EndAngle=7.56663
    g16: LineSegment StartX=-202.765 StartY=20.303 StartZ=0 EndX=-195.887 EndY=39.2 EndZ=0
    g17: LineSegment [constr] StartX=-193.885 StartY=33.0037 StartZ=0 EndX=-197.644 EndY=34.3718 EndZ=0
    g18: LineSegment StartX=-195.887 StartY=39.2 StartZ=0 EndX=0 EndY=39.2 EndZ=0
    g19: LineSegment StartX=0 StartY=3.2 StartZ=0 EndX=0 EndY=39.2 EndZ=0
    g20: LineSegment StartX=-189.939 StartY=31.5672 StartZ=0 EndX=-192.333 EndY=24.9893 EndZ=0
    g21: LineSegment StartX=-196.467 StartY=26.4942 StartZ=0 EndX=-194.073 EndY=33.0721 EndZ=0
    g22: Circle CenterX=-213.443 CenterY=-76.8316 CenterZ=0 NormalX=0 NormalY=0 NormalZ=1 AngleXU=0 Radius=1.8
    g23: Circle CenterX=-179.305 CenterY=-76.8316 CenterZ=0 NormalX=0 NormalY=0 NormalZ=1 AngleXU=0 Radius=1.8
    g24: Circle CenterX=-184.08 CenterY=34.8 CenterZ=0 NormalX=0 NormalY=0 NormalZ=1 AngleXU=0 Radius=1.8
    g25: Circle CenterX=-78.51 CenterY=34.8 CenterZ=0 NormalX=0 NormalY=0 NormalZ=1 AngleXU=0 Radius=1.8
    g26: Circle CenterX=-78.51 CenterY=7.6 CenterZ=0 NormalX=0 NormalY=0 NormalZ=1 AngleXU=0 Radius=1.8
    g27: Circle CenterX=-5.6 CenterY=34.8 CenterZ=0 NormalX=0 NormalY=0 NormalZ=1 AngleXU=0 Radius=1.8
    g28: Circle CenterX=-5.6 CenterY=7.6 CenterZ=0 NormalX=0 NormalY=0 NormalZ=1 AngleXU=0 Radius=1.8
    g29: LineSegment StartX=-190.127 StartY=31.6356 StartZ=0 EndX=-189.939 EndY=31.5672 EndZ=0
    g30: LineSegment StartX=-194.073 StartY=33.0721 StartZ=0 EndX=-193.885 EndY=33.0037 EndZ=0
    g31: LineSegment StartX=-193.885 StartY=33.0037 StartZ=0 EndX=-190.127 EndY=31.6356 EndZ=0
    g32: LineSegment StartX=-196.467 StartY=26.4942 StartZ=0 EndX=-192.333 EndY=24.9893 EndZ=0
    g33: LineSegment [constr] StartX=-4 StartY=21.2 StartZ=0 EndX=-87.91 EndY=21.2 EndZ=0
    g34: GeomPoint [constr] X=-4 Y=21.2 Z=0
    g35: LineSegment [constr] StartX=-15.2 StartY=33.7 StartZ=0 EndX=-15.2 EndY=8.7 EndZ=0
    g36: LineSegment [constr] StartX=-15.2 StartY=33.7 StartZ=0 EndX=-56.2 EndY=33.7 EndZ=0
    g37: LineSegment [constr] StartX=-15.2 StartY=8.7 StartZ=0 EndX=-56.2 EndY=8.7 EndZ=0
    g38: LineSegment [constr] StartX=-56.2 StartY=33.7 StartZ=0 EndX=-56.2 EndY=8.7 EndZ=0
    g39: Circle CenterX=-18.6 CenterY=30.3 CenterZ=0 NormalX=0 NormalY=0 NormalZ=1 AngleXU=0 Radius=3.4
    g40: Circle CenterX=-18.6 CenterY=12.1 CenterZ=0 NormalX=0 NormalY=0 NormalZ=1 AngleXU=0 Radius=3.4
    g41: Circle CenterX=-43.2 CenterY=30.3 CenterZ=0 NormalX=0 NormalY=0 NormalZ=1 AngleXU=0 Radius=3.4
    g42: Circle CenterX=-43.2 CenterY=12.1 CenterZ=0 NormalX=0 NormalY=0 NormalZ=1 AngleXU=0 Radius=3.4
    g43: LineSegment [constr] StartX=-4 StartY=21.2 StartZ=0 EndX=-15.2 EndY=21.2 EndZ=0
    g44: LineSegment [constr] StartX=-15.2 StartY=21.2 StartZ=0 EndX=-36.2 EndY=21.2 EndZ=0
    g45: LineSegment [constr] StartX=-41.5 StartY=16.2 StartZ=0 EndX=-30.9 EndY=16.2 EndZ=0
    g46: LineSegment [constr] StartX=-30.9 StartY=16.2 StartZ=0 EndX=-30.9 EndY=26.2 EndZ=0
    g47: LineSegment [constr] StartX=-30.9 StartY=26.2 StartZ=0 EndX=-41.5 EndY=26.2 EndZ=0
    g48: LineSegment [constr] StartX=-41.5 StartY=26.2 StartZ=0 EndX=-41.5 EndY=16.2 EndZ=0
    g49: GeomPoint [constr] X=-36.2 Y=21.2 Z=0
    g50: Circle CenterX=-36.2 CenterY=21.2 CenterZ=0 NormalX=0 NormalY=0 NormalZ=1 AngleXU=0 Radius=2.8
    g51: LineSegment [constr] StartX=-24.2 StartY=26.7 StartZ=0 EndX=-24.2 EndY=15.7 EndZ=0
    g52: Circle CenterX=-24.2 CenterY=26.7 CenterZ=0 NormalX=0 NormalY=0 NormalZ=1 AngleXU=0 Radius=3
    g53: Circle CenterX=-24.2 CenterY=15.7 CenterZ=0 NormalX=0 NormalY=0 NormalZ=1 AngleXU=0 Radius=3
    g54: GeomPoint X=-18.6 Y=30.3 Z=0
    g55: GeomPoint X=-18.6 Y=12.1 Z=0
    g56: GeomPoint X=-43.2 Y=12.1 Z=0
    g57: GeomPoint X=-43.2 Y=30.3 Z=0
    g58: Circle CenterX=-65 CenterY=21.2 CenterZ=0 NormalX=0 NormalY=0 NormalZ=1 AngleXU=0 Radius=1.5
    g59: Circle CenterX=-42 CenterY=21.2 CenterZ=0 NormalX=0 NormalY=0 NormalZ=1 AngleXU=0 Radius=1.5
    g60: Circle CenterX=-19 CenterY=21.2 CenterZ=0 NormalX=0 NormalY=0 NormalZ=1 AngleXU=0 Radius=1.5
  constraints (149):
    c: Coincident(g0,g-41)
    c: Horizontal(g0)
    c: PointOnObject(g0,g-39)
    c: Coincident(g1,g0)
    c: Vertical(g1)
    c: DistanceY(g1,g1) = 3
    c: Coincident(g2,g-17)
    c: Vertical(g2)
    c: Coincident(g3,g-16)
    c: Vertical(g3)
    c: DistanceY(g2,g2) = 2
    c: DistanceY(g3,g3) = 2
    c: Coincident(g4,g3)
    c: Coincident(g4,g2)
    c: Coincident(g5,g-17)
    c: Coincident(g5,g2)
    c: Coincident(g6,g1)
    c: Horizontal(g6)
    c: Coincident(g6,g5)
    c: Coincident(g7,g-15)
    c: Coincident(g8,g7)
    c: Coincident(g8,g3)
    c: Coincident(g8,g-15)
    c: Horizontal(g9)
    c: DistanceY(g-13,g9) = 2
    c: Coincident(g10,g7)
    c: Parallel(g10,g-14)
    c: Coincident(g9,g10)
    c: Distance(g11) = 2
    c: Coincident(g11,g-11)
    c: Perpendicular(g-11,g11)
    c: Distance(g12) = 2
    c: Coincident(g12,g-12)
    c: Perpendicular(g-11,g12)
    c: Coincident(g13,g11)
    c: Coincident(g13,g12)
    c: Coincident(g14,g-32)
    c: Coincident(g14,g12)
    c: Coincident(g14,g9)
    c: Coincident(g15,g-10)
    c: Coincident(g15,g11)
    c: Parallel(g16,g-22)
    c: Distance(g17) = 4
    c: PointOnObject(g17,g16)
    c: Coincident(g15,g16)
    c: Horizontal(g18)
    c: Coincident(g18,g16)
    c: Coincident(g19,g0)
    c: PointOnObject(g19,g-39)
    c: DistanceY(g19,g-36) = 2
    c: Coincident(g18,g19)
    c: Diameter(g22) = 3.6
    c: Coincident(g22,g-9)
    c: Diameter(g23) = 3.6
    c: Coincident(g23,g-8)
    c: Diameter(g24) = 3.6
    c: Diameter(g25) = 3.6
    c: Diameter(g26) = 3.6
    c: Diameter(g27) = 3.6
    c: Diameter(g28) = 3.6
    c: Coincident(g27,g-4)
    c: Coincident(g28,g-3)
    c: Coincident(g25,g-6)
    c: Coincident(g26,g-5)
    c: Coincident(g24,g-7)
    c: Parallel(g20,g-21)
    c: Equal(g20,g-21)
    c: Parallel(g21,g-19)
    c: Equal(g21,g-19)
    c: Distance(g29) = 0.2
    c: Distance(g30) = 0.2
    c: Parallel(g29,g-20)
    c: Parallel(g31,g-20)
    c: Equal(g31,g-20)
    c: Coincident(g30,g31)
    c: Coincident(g31,g29)
    c: Coincident(g29,g-21)
    c: Parallel(g30,g31)
    c: Coincident(g17,g30)
    c: Coincident(g20,g29)
    c: Coincident(g21,g30)
    c: Perpendicular(g16,g17)
    c: Coincident(g32,g21)
    c: Coincident(g32,g20)
    c: Perpendicular(g10,g7)
    c: Horizontal(g33)
    c: Symmetric(g-24,g-24,g33)
    c: PointOnObject(g33,g-28)
    c: Symmetric(g-24,g-24,g34)
    c: DistanceY(g35,g35) = 25
    c: Symmetric(g35,g35,g33)
    c: Distance(g36) = 41
    c: Coincident(g36,g35)
    c: Horizontal(g36)
    c: Coincident(g37,g35)
    c: Horizontal(g37)
    c: Coincident(g38,g36)
    c: Vertical(g38)
    c: Coincident(g37,g38)
    c: Diameter(g39) = 6.8
    c: Diameter(g40) = 6.8
    c: Tangent(g39,g36)
    c: Tangent(g40,g37)
    c: Tangent(g39,g35)
    c: Tangent(g40,g35)
    c: Diameter(g41) = 6.8
    c: Diameter(g42) = 6.8
    c: Tangent(g41,g36)
    c: Tangent(g42,g37)
    c: DistanceX(g41,g39) = 24.6
    c: DistanceX(g42,g40) = 24.6
    c: Distance(g43) = 11.2
    c: Coincident(g43,g33)
    c: PointOnObject(g43,g33)
    c: PointOnObject(g43,g35)
    c: Distance(g44) = 21
    c: Coincident(g44,g43)
    c: PointOnObject(g44,g33)
    c: Coincident(g45,g46)
    c: Coincident(g46,g47)
    c: Coincident(g47,g48)
    c: Coincident(g48,g45)
    c: Horizontal(g45)
    c: Horizontal(g47)
    c: Vertical(g46)
    c: Vertical(g48)
    c: Symmetric(g47,g45,g49)
    c: Distance(g46,g48) = 10.6
    c: Distance(g45,g47) = 10
    c: Coincident(g49,g44)
    c: Diameter(g50) = 5.6
    c: Coincident(g50,g44)
    c: Distance(g51) = 11
    c: Symmetric(g51,g51,g33)
    c: DistanceX(g51,g43) = 9
    c: Diameter(g52) = 6
    c: Coincident(g52,g51)
    c: Diameter(g53) = 6
    c: Coincident(g53,g51)
    c: Coincident(g40,g55)
    c: Coincident(g39,g54)
    c: Coincident(g41,g57)
    c: Coincident(g42,g56)
    c: Diameter(g58) = 3
    c: Diameter(g59) = 3
    c: Diameter(g60) = 3
    c: Coincident(g58,g-44)
    c: Coincident(g59,g-46)
    c: Coincident(g60,g-45)
FEATURE [Sketcher::SketchObject] Sketch078
  ArcFitTolerance = 1e-06
  AttachmentSupport = -> [XZ_Plane005]
  FullyConstrained = true
  MakeInternals = false
  MapMode = 5
  Placement = pos=(0,0,0) rot=(1,0,0;1.5708rad)
  sketch-geometry (5):
    g0: LineSegment [constr] StartX=0 StartY=5.5 StartZ=0 EndX=0 EndY=-5.5 EndZ=0
    g1: ArcOfCircle CenterX=0 CenterY=5.5 CenterZ=0 NormalX=0 NormalY=0 NormalZ=1 AngleXU=0 Radius=2.7 StartAngle=0 EndAngle=3.14159
    g2: ArcOfCircle CenterX=0 CenterY=-5.5 CenterZ=0 NormalX=0 NormalY=0 NormalZ=1 AngleXU=0 Radius=2.7 StartAngle=3.1416 EndAngle=6.28318
    g3: LineSegment StartX=-2.7 StartY=5.5 StartZ=0 EndX=-2.7 EndY=-5.50001 EndZ=0
    g4: LineSegment StartX=2.7 StartY=5.5 StartZ=0 EndX=2.7 EndY=-5.50001 EndZ=0
  constraints (13):
    c: Distance(g0) = 11
    c: Vertical(g0)
    c: Symmetric(g0,g0,g-1)
    c: Radius(g1) = 2.7
    c: Coincident(g1,g0)
    c: Radius(g2) = 2.7
    c: Coincident(g2,g0)
    c: Vertical(g3)
    c: Vertical(g4)
    c: Coincident(g2,g4)
    c: Coincident(g2,g3)
    c: Tangent(g3,g1) = -1.5708
    c: Tangent(g4,g1) = 1.5708
FEATURE [PartDesign::Pad] Pad002
  Direction = (0,-1,2e-16)
  Length = 0.8
  Length2 = 10
  Placement = pos=(0,0,0) rot=(1,0,0;1.5708rad)
  Profile = -> Sketch078
  ReferenceAxis = -> Sketch078 [N_Axis]
  Refine = true
  Suppressed = false
  Type = 0
FEATURE [Sketcher::SketchObject] Sketch079
  ArcFitTolerance = 1e-06
  AttachmentSupport = -> [XZ_Plane005]
  ExternalGeometry = -> [Sketch078]
  FullyConstrained = true
  MakeInternals = false
  MapMode = 5
  Placement = pos=(0,0,0) rot=(1,0,0;1.5708rad)
  sketch-geometry (2):
    g0: Circle CenterX=-1e-16 CenterY=5.5 CenterZ=0 NormalX=0 NormalY=0 NormalZ=1 AngleXU=0 Radius=2.7
    g1: Circle CenterX=0 CenterY=-5.5 CenterZ=0 NormalX=0 NormalY=0 NormalZ=1 AngleXU=0 Radius=2.7
  constraints (4):
    c: Coincident(g0,g-3)
    c: PointOnObject(g-3,g0)
    c: Coincident(g1,g-4)
    c: Equal(g1,g-4)
FEATURE [PartDesign::Pad] Pad003
  BaseFeature = -> Pad002
  Direction = (0,-1,2e-16)
  Length = 5
  Length2 = 10
  Placement = pos=(0,0,0) rot=(1,0,0;1.5708rad)
  Profile = -> Sketch079
  ReferenceAxis = -> Sketch079 [N_Axis]
  Refine = true
  Suppressed = false
  Type = 0
FEATURE [PartDesign::Fillet] Fillet001
  Base = -> Pad003 [Edge16,Edge14]
  BaseFeature = -> Pad003
  Placement = pos=(0,0,0) rot=(1,0,0;1.5708rad)
  Radius = 0.4
  Refine = true
  SupportTransform = false
  Suppressed = false
  UseAllEdges = false
FEATURE [PartDesign::Body] Body005  label="pulsanti lato destro"
  AllowCompound = false
  Group = -> [Sketch078,Pad002,Sketch079,Pad003,Fillet001]
  Origin = -> Origin005
  Tip = -> Fillet001
FEATURE [PartDesign::SubShapeBinder] Binder
  BindCopyOnChange = 0
  BindMode = 0
  ClaimChildren = false
  Context = -> Body006 [Binder.]
  Fuse = false
  MakeFace = true
  OffsetFill = false
  OffsetIntersection = false
  OffsetJoinType = 0
  OffsetOpenResult = false
  PartialLoad = false
  Refine = true
  Relative = true
  Support = -> [Body[Sketch074.]]
  _Version = 2
FEATURE [PartDesign::SubShapeBinder] Binder001
  BindCopyOnChange = 0
  BindMode = 0
  ClaimChildren = false
  Context = -> Body007 [Binder001.]
  Fuse = false
  MakeFace = true
  OffsetFill = false
  OffsetIntersection = false
  OffsetJoinType = 0
  OffsetOpenResult = false
  PartialLoad = false
  Refine = true
  Relative = true
  Support = -> [Body[Sketch075.]]
  _Version = 2
FEATURE [Mesh::Feature] logo_per_PCB_definitivo_positivo
  Placement = pos=(-191,17,-66) rot=(0,1,1;0rad)
FEATURE [Sketcher::SketchObject] Sketch114  label="Sketch114 - base lato DX"
  ArcFitTolerance = 1e-06
  AttachmentSupport = -> [Binder001]
  ExternalGeometry = -> [Binder001]
  FullyConstrained = true
  MakeInternals = false
  MapMode = 5
  Placement = pos=(0,1e-15,0) rot=(0,0.707107,0.707107;3.14159rad)
  sketch-geometry (30):
    g0: Circle CenterX=5.6 CenterY=34.8 CenterZ=0 NormalX=0 NormalY=0 NormalZ=1 AngleXU=0 Radius=1.8
    g1: Circle CenterX=5.6 CenterY=7.6 CenterZ=0 NormalX=0 NormalY=0 NormalZ=1 AngleXU=0 Radius=1.8
    g2: Circle CenterX=24.2 CenterY=26.7 CenterZ=0 NormalX=0 NormalY=0 NormalZ=1 AngleXU=0 Radius=3
    g3: Circle CenterX=24.2 CenterY=15.7 CenterZ=0 NormalX=0 NormalY=0 NormalZ=1 AngleXU=0 Radius=3
    g4: Circle CenterX=36.2 CenterY=21.2 CenterZ=0 NormalX=0 NormalY=0 NormalZ=1 AngleXU=0 Radius=2.8
    g5: Circle CenterX=78.51 CenterY=34.8 CenterZ=0 NormalX=0 NormalY=0 NormalZ=1 AngleXU=0 Radius=1.8
    g6: Circle CenterX=78.51 CenterY=7.6 CenterZ=0 NormalX=0 NormalY=0 NormalZ=1 AngleXU=0 Radius=1.8
    g7: Circle CenterX=184.08 CenterY=34.8 CenterZ=0 NormalX=0 NormalY=0 NormalZ=1 AngleXU=0 Radius=1.8
    g8: Circle CenterX=213.443 CenterY=-76.8316 CenterZ=0 NormalX=0 NormalY=0 NormalZ=1 AngleXU=0 Radius=1.8
    g9: Circle CenterX=179.305 CenterY=-76.8316 CenterZ=0 NormalX=0 NormalY=0 NormalZ=1 AngleXU=0 Radius=1.8
    g10: ArcOfCircle [constr] CenterX=132.428 CenterY=4 CenterZ=0 NormalX=0 NormalY=0 NormalZ=1 AngleXU=0 Radius=16 StartAngle=0.314159 EndAngle=1.5708
    g11: ArcOfCircle CenterX=107.6 CenterY=4 CenterZ=0 NormalX=0 NormalY=0 NormalZ=1 AngleXU=0 Radius=16 StartAngle=1.5708 EndAngle=3.00366
    g12: ArcOfCircle CenterX=207.583 CenterY=4 CenterZ=0 NormalX=0 NormalY=0 NormalZ=1 AngleXU=0 Radius=17 StartAngle=1.85815 EndAngle=3.57792
    g13: ArcOfCircle CenterX=184.801 CenterY=-67.3089 CenterZ=0 NormalX=0 NormalY=0 NormalZ=1 AngleXU=0 Radius=33.7833 StartAngle=5.88425 EndAngle=6.71952
    g14: LineSegment StartX=0 StartY=39.2 StartZ=0 EndX=0 EndY=3.2 EndZ=0
    g15: LineSegment StartX=0 StartY=3.2 StartZ=0 EndX=82.8 EndY=3.2 EndZ=0
    g16: LineSegment StartX=82.8 StartY=3.2 StartZ=0 EndX=82.8 EndY=6.2 EndZ=0
    g17: LineSegment StartX=82.8 StartY=6.2 StartZ=0 EndX=91.752 EndY=6.2 EndZ=0
    g18: LineSegment StartX=107.6 StartY=20 StartZ=0 EndX=132.428 EndY=20 EndZ=0
    g19: LineSegment StartX=147.645 StartY=8.94427 StartZ=0 EndX=176.685 EndY=-80.4316 EndZ=0
    g20: LineSegment StartX=176.685 StartY=-80.4316 StartZ=0 EndX=215.932 EndY=-80.4316 EndZ=0
    g21: LineSegment StartX=215.42 StartY=-53.0314 StartZ=0 EndX=192.176 EndY=-3.18451 EndZ=0
    g22: LineSegment StartX=202.765 StartY=20.303 StartZ=0 EndX=195.887 EndY=39.2 EndZ=0
    g23: LineSegment StartX=195.887 StartY=39.2 StartZ=0 EndX=0 EndY=39.2 EndZ=0
    g24: LineSegment StartX=196.467 StartY=26.4942 StartZ=0 EndX=194.073 EndY=33.0721 EndZ=0
    g25: LineSegment StartX=194.073 StartY=33.0721 StartZ=0 EndX=189.939 EndY=31.5672 EndZ=0
    g26: LineSegment StartX=189.939 StartY=31.5672 StartZ=0 EndX=192.333 EndY=24.9893 EndZ=0
    g27: LineSegment StartX=192.333 StartY=24.9893 StartZ=0 EndX=196.467 EndY=26.4942 EndZ=0
    g28: LineSegment StartX=132.428 StartY=20 StartZ=0 EndX=144.053 EndY=20 EndZ=0
    g29: LineSegment StartX=144.053 StartY=20 StartZ=0 EndX=147.645 EndY=8.94427 EndZ=0
  constraints (65):
    c: Equal(g0,g-25)
    c: Equal(g2,g-29)
    c: Equal(g3,g-30)
    c: Equal(g4,g-28)
    c: Equal(g1,g-26)
    c: Coincident(g0,g-25)
    c: Coincident(g1,g-26)
    c: Coincident(g2,g-29)
    c: Coincident(g3,g-30)
    c: Coincident(g4,g-28)
    c: Equal(g5,g-23)
    c: Equal(g6,g-24)
    c: Coincident(g5,g-23)
    c: Coincident(g6,g-24)
    c: Equal(g7,g-20)
    c: Coincident(g7,g-20)
    c: Equal(g9,g-22)
    c: Coincident(g9,g-22)
    c: Equal(g8,g-21)
    c: Coincident(g8,g-21)
    c: Equal(g13,g-12)
    c: Equal(g12,g-14)
    c: Equal(g10,g-9)
    c: Equal(g11,g-7)
    c: Coincident(g14,g-27)
    c: Coincident(g14,g-27)
    c: Coincident(g15,g14)
    c: Coincident(g15,g-5)
    c: Coincident(g16,g15)
    c: Coincident(g16,g-6)
    c: Coincident(g17,g16)
    c: Coincident(g17,g-7)
    c: Coincident(g11,g17)
    c: Coincident(g11,g-8)
    c: Coincident(g18,g11)
    c: Coincident(g18,g-9)
    c: Coincident(g10,g18)
    c: Coincident(g10,g-10)
    c: Coincident(g19,g10)
    c: Coincident(g19,g-11)
    c: Coincident(g20,g19)
    c: Coincident(g20,g-12)
    c: Coincident(g13,g20)
    c: Coincident(g13,g-13)
    c: Coincident(g21,g13)
    c: Coincident(g21,g-14)
    c: Coincident(g12,g21)
    c: Coincident(g12,g-15)
    c: Coincident(g22,g12)
    c: Coincident(g22,g-15)
    c: Coincident(g23,g22)
    c: Coincident(g23,g14)
    c: Coincident(g24,g-18)
    c: Coincident(g24,g-16)
    c: Coincident(g25,g24)
    c: Coincident(g25,g-19)
    c: Coincident(g26,g25)
    c: Coincident(g26,g-19)
    c: Coincident(g27,g26)
    c: Coincident(g27,g24)
    c: Coincident(g29,g10)
    c: Coincident(g28,g10)
    c: Coincident(g29,g28)
    c: Parallel(g28,g18)
    c: Parallel(g29,g19)
FEATURE [PartDesign::Pad] Pad011
  Direction = (0,1,-2e-16)
  Length = 2
  Length2 = 10
  Profile = -> Sketch114
  ReferenceAxis = -> Sketch114 [N_Axis]
  Refine = true
  Reversed = true
  Suppressed = false
  Type = 0
FEATURE [Sketcher::SketchObject] Sketch115
  ArcFitTolerance = 1e-06
  AttachmentSupport = -> [Pad011]
  ExternalGeometry = -> [Binder001]
  FullyConstrained = true
  MakeInternals = false
  MapMode = 5
  Placement = pos=(0,1.7e-15,0) rot=(0,0.707107,0.707107;3.14159rad)
  sketch-geometry (4):
    g0: ArcOfCircle CenterX=24.2 CenterY=26.7 CenterZ=0 NormalX=0 NormalY=0 NormalZ=1 AngleXU=0 Radius=3 StartAngle=4.48384e-08 EndAngle=3.14159
    g1: ArcOfCircle CenterX=24.2 CenterY=15.7 CenterZ=0 NormalX=0 NormalY=0 NormalZ=1 AngleXU=0 Radius=3 StartAngle=3.14159 EndAngle=6.28318
    g2: LineSegment StartX=21.2 StartY=26.7 StartZ=0 EndX=21.2 EndY=15.7 EndZ=0
    g3: LineSegment StartX=27.2 StartY=26.7 StartZ=0 EndX=27.2 EndY=15.7 EndZ=0
  constraints (12):
    c: Equal(g1,g-4)
    c: Equal(g0,g-3)
    c: Coincident(g0,g-3)
    c: Coincident(g1,g-4)
    c: Vertical(g2)
    c: Vertical(g3)
    c: Tangent(g3,g-3)
    c: Tangent(g2,g-3)
    c: Coincident(g0,g2)
    c: Coincident(g0,g3)
    c: Coincident(g1,g2)
    c: Coincident(g3,g1)
FEATURE [Sketcher::SketchObject] Sketch117  label="Sketch117 - fori per inserto M3 x 3 x 4.5"
  ArcFitTolerance = 1e-06
  AttachmentSupport = -> [Pad011]
  ExternalGeometry = -> [Binder001]
  FullyConstrained = true
  MakeInternals = false
  MapMode = 5
  Placement = pos=(0,1.7e-15,0) rot=(0,0.707107,0.707107;3.14159rad)
  sketch-geometry (4):
    g0: Circle CenterX=43.2 CenterY=30.3 CenterZ=0 NormalX=0 NormalY=0 NormalZ=1 AngleXU=0 Radius=2.25
    g1: Circle CenterX=43.2 CenterY=12.1 CenterZ=0 NormalX=0 NormalY=0 NormalZ=1 AngleXU=0 Radius=2.25
    g2: Circle CenterX=18.6 CenterY=30.3 CenterZ=0 NormalX=0 NormalY=0 NormalZ=1 AngleXU=0 Radius=2.25
    g3: Circle CenterX=18.6 CenterY=12.1 CenterZ=0 NormalX=0 NormalY=0 NormalZ=1 AngleXU=0 Radius=2.25
  constraints (8):
    c: Diameter(g0) = 4.5
    c: Diameter(g1) = 4.5
    c: Diameter(g2) = 4.5
    c: Diameter(g3) = 4.5
    c: Coincident(g2,g-3)
    c: Coincident(g3,g-6)
    c: Coincident(g0,g-4)
    c: Coincident(g1,g-5)
FEATURE [Sketcher::SketchObject] Sketch118
  ArcFitTolerance = 1e-06
  AttachmentSupport = -> [Pad011]
  ExternalGeometry = -> [Binder001]
  FullyConstrained = true
  MakeInternals = false
  MapMode = 5
  Placement = pos=(0,-2,0) rot=(1,0,0;1.5708rad)
  sketch-geometry (12):
    g0: Circle CenterX=-78.51 CenterY=34.8 CenterZ=0 NormalX=0 NormalY=0 NormalZ=1 AngleXU=0 Radius=1.8
    g1: Circle CenterX=-78.51 CenterY=7.6 CenterZ=0 NormalX=0 NormalY=0 NormalZ=1 AngleXU=0 Radius=1.8
    g2: Circle CenterX=-5.6 CenterY=34.8 CenterZ=0 NormalX=0 NormalY=0 NormalZ=1 AngleXU=0 Radius=1.8
    g3: Circle CenterX=-5.6 CenterY=7.6 CenterZ=0 NormalX=0 NormalY=0 NormalZ=1 AngleXU=0 Radius=1.8
    g4: LineSegment StartX=0 StartY=39.2 StartZ=0 EndX=0 EndY=3.2 EndZ=0
    g5: LineSegment StartX=0 StartY=3.2 StartZ=0 EndX=-82.8 EndY=3.2 EndZ=0
    g6: LineSegment StartX=-82.8 StartY=3.2 StartZ=0 EndX=-82.8 EndY=39.2 EndZ=0
    g7: LineSegment StartX=-82.8 StartY=39.2 StartZ=0 EndX=0 EndY=39.2 EndZ=0
    g8: ArcOfCircle CenterX=-65 CenterY=21.2 CenterZ=0 NormalX=0 NormalY=0 NormalZ=1 AngleXU=0 Radius=10 StartAngle=1.5708 EndAngle=4.71239
    g9: ArcOfCircle CenterX=-19 CenterY=21.2 CenterZ=0 NormalX=0 NormalY=0 NormalZ=1 AngleXU=0 Radius=10 StartAngle=4.71239 EndAngle=7.85398
    g10: LineSegment StartX=-65 StartY=31.2 StartZ=0 EndX=-19 EndY=31.2 EndZ=0
    g11: LineSegment StartX=-65 StartY=11.2 StartZ=0 EndX=-19 EndY=11.2 EndZ=0
  constraints (25):
    c: Equal(g2,g-5)
    c: Equal(g3,g-7)
    c: Equal(g1,g-6)
    c: Equal(g0,g-4)
    c: Coincident(g0,g-4)
    c: Coincident(g1,g-6)
    c: Coincident(g3,g-7)
    c: Coincident(g2,g-5)
    c: Coincident(g4,g-8)
    c: Coincident(g4,g-9)
    c: Coincident(g5,g4)
    c: Coincident(g5,g-10)
    c: Coincident(g6,g5)
    c: PointOnObject(g6,g-3)
    c: Vertical(g6)
    c: Coincident(g7,g6)
    c: Coincident(g7,g4)
    c: Tangent(g8,g10) = 1.5708
    c: Tangent(g8,g11) = -1.5708
    c: Tangent(g9,g10) = 1.5708
    c: Tangent(g9,g11) = -1.5708
    c: Equal(g8,g9)
    c: Radius(g8) = 10
    c: Coincident(g8,g-11)
    c: Coincident(g9,g-12)
FEATURE [Sketcher::SketchObject] Sketch120
  ArcFitTolerance = 1e-06
  AttachmentSupport = -> [Pad011]
  ExternalGeometry = -> [Binder001]
  FullyConstrained = true
  MakeInternals = false
  MapMode = 5
  Placement = pos=(0,-2,0) rot=(1,0,0;1.5708rad)
  sketch-geometry (4):
    g0: LineSegment StartX=-137.815 StartY=39.2 StartZ=0 EndX=-142.655 EndY=24.303 EndZ=0
    g1: LineSegment StartX=-137.815 StartY=39.2 StartZ=0 EndX=-110.815 EndY=39.2 EndZ=0
    g2: LineSegment StartX=-142.655 StartY=24.303 StartZ=0 EndX=-110.815 EndY=24.303 EndZ=0
    g3: ArcOfCircle CenterX=-92.2534 CenterY=31.7515 CenterZ=0 NormalX=0 NormalY=0 NormalZ=1 AngleXU=0 Radius=20 StartAngle=2.75997 EndAngle=3.52321
  constraints (12):
    c: PointOnObject(g0,g-3)
    c: Coincident(g1,g0)
    c: PointOnObject(g1,g-3)
    c: Coincident(g2,g0)
    c: Horizontal(g2)
    c: Tangent(g0,g-4)
    c: Vertical(g2,g1)
    c: DistanceX(g1,g1) = 27
    c: DistanceY(g-6,g0) = 4
    c: Radius(g3) = 20
    c: Coincident(g3,g1)
    c: Coincident(g3,g2)
FEATURE [Sketcher::SketchObject] Sketch121
  ArcFitTolerance = 1e-06
  AttachmentSupport = -> [Pad011]
  ExternalGeometry = -> [Binder001]
  FullyConstrained = true
  MakeInternals = false
  MapMode = 5
  Placement = pos=(0,-2,0) rot=(1,0,0;1.5708rad)
  sketch-geometry (15):
    g0: LineSegment StartX=-137.815 StartY=39.2 StartZ=0 EndX=-143.955 EndY=20.303 EndZ=0
    g1: LineSegment StartX=-143.955 StartY=20.303 StartZ=0 EndX=-190.141 EndY=20.303 EndZ=0
    g2: LineSegment StartX=-190.141 StartY=20.303 StartZ=0 EndX=-186.139 EndY=31.3 EndZ=0
    g3: LineSegment StartX=-178.754 StartY=39.2 StartZ=0 EndX=-180.791 EndY=33.6029 EndZ=0
    g4: ArcOfCircle CenterX=-184.08 CenterY=34.8 CenterZ=0 NormalX=0 NormalY=0 NormalZ=1 AngleXU=0 Radius=3.5 StartAngle=4.71239 EndAngle=5.93412
    g5: LineSegment StartX=-184.08 StartY=31.3 StartZ=0 EndX=-186.139 EndY=31.3 EndZ=0
    g6: LineSegment StartX=-137.815 StartY=39.2 StartZ=0 EndX=-156.815 EndY=39.2 EndZ=0
    g7: LineSegment StartX=-168.815 StartY=39.2 StartZ=0 EndX=-178.754 EndY=39.2 EndZ=0
    g8: LineSegment StartX=-157.815 StartY=39.2 StartZ=0 EndX=-167.815 EndY=39.2 EndZ=0
    g9: LineSegment StartX=-168.815 StartY=31.2 StartZ=0 EndX=-156.815 EndY=31.2 EndZ=0
    g10: LineSegment StartX=-167.436 StartY=36.2 StartZ=0 EndX=-157.436 EndY=36.2 EndZ=0
    g11: ArcOfCircle CenterX=-176.411 CenterY=35.2 CenterZ=0 NormalX=0 NormalY=0 NormalZ=1 AngleXU=0 Radius=20 StartAngle=6.08183 EndAngle=6.48454
    g12: ArcOfCircle CenterX=-188.411 CenterY=35.2 CenterZ=0 NormalX=0 NormalY=0 NormalZ=1 AngleXU=0 Radius=20 StartAngle=6.08183 EndAngle=6.48454
    g13: ArcOfCircle CenterX=-177.411 CenterY=35.2 CenterZ=0 NormalX=0 NormalY=0 NormalZ=1 AngleXU=0 Radius=20 StartAngle=0.0500209 EndAngle=0.201358
    g14: ArcOfCircle CenterX=-187.411 CenterY=35.2 CenterZ=0 NormalX=0 NormalY=0 NormalZ=1 AngleXU=0 Radius=20 StartAngle=0.0500209 EndAngle=0.201358
  constraints (46):
    c: PointOnObject(g0,g-3)
    c: Tangent(g0,g-5)
    c: Coincident(g1,g0)
    c: Horizontal(g1)
    c: Coincident(g2,g1)
    c: PointOnObject(g3,g-3)
    c: Parallel(g3,g-6)
    c: Parallel(g2,g-6)
    c: Radius(g4) = 3.5
    c: Coincident(g4,g-7)
    c: Tangent(g3,g4) = 1.5708
    c: Horizontal(g5)
    c: Tangent(g5,g4) = 1.5708
    c: DistanceX(g-8,g5) = 3.8
    c: Coincident(g2,g5)
    c: Coincident(g6,g0)
    c: PointOnObject(g6,g-3)
    c: DistanceX(g6,g6) = 19
    c: PointOnObject(g7,g-3)
    c: DistanceX(g7,g6) = 12
    c: Coincident(g7,g3)
    c: PointOnObject(g8,g-3)
    c: PointOnObject(g8,g-3)
    c: DistanceX(g8,g8) = 10
    c: DistanceX(g8,g6) = 1
    c: Horizontal(g9)
    c: Vertical(g7,g9)
    c: Vertical(g6,g9)
    c: DistanceY(g9,g7) = 8
    c: Horizontal(g10)
    c: Equal(g8,g10)
    c: DistanceY(g10,g8) = 3
    c: Radius(g11) = 20
    c: Coincident(g11,g6)
    c: Coincident(g11,g9)
    c: Radius(g12) = 20
    c: Coincident(g12,g7)
    c: Coincident(g12,g9)
    c: Equal(g13,g11)
    c: Coincident(g13,g8)
    c: Coincident(g13,g10)
    c: Horizontal(g13,g11)
    c: Equal(g14,g12)
    c: Coincident(g14,g8)
    c: Coincident(g14,g10)
    c: Horizontal(g1,g-6)
FEATURE [Sketcher::SketchObject] Sketch122
  ArcFitTolerance = 1e-06
  AttachmentSupport = -> [Pad011]
  ExternalGeometry = -> [Binder001]
  FullyConstrained = true
  MakeInternals = false
  MapMode = 5
  Placement = pos=(0,-2,0) rot=(1,0,0;1.5708rad)
  sketch-geometry (8):
    g0: ArcOfCircle CenterX=-184.801 CenterY=-67.3089 CenterZ=0 NormalX=0 NormalY=0 NormalZ=1 AngleXU=0 Radius=33.7833 StartAngle=2.70526 EndAngle=3.54053
    g1: LineSegment StartX=-176.685 StartY=-80.4316 StartZ=0 EndX=-215.932 EndY=-80.4316 EndZ=0
    g2: LineSegment StartX=-215.42 StartY=-53.0314 StartZ=0 EndX=-192.176 EndY=-3.18454 EndZ=0
    g3: ArcOfCircle CenterX=-207.583 CenterY=4 CenterZ=0 NormalX=0 NormalY=0 NormalZ=1 AngleXU=0 Radius=17 StartAngle=5.84685 EndAngle=7.56663
    g4: Circle CenterX=-213.443 CenterY=-76.8316 CenterZ=0 NormalX=0 NormalY=0 NormalZ=1 AngleXU=0 Radius=3
    g5: Circle CenterX=-179.305 CenterY=-76.8316 CenterZ=0 NormalX=0 NormalY=0 NormalZ=1 AngleXU=0 Radius=3
    g6: LineSegment StartX=-143.955 StartY=20.303 StartZ=0 EndX=-176.685 EndY=-80.4316 EndZ=0
    g7: LineSegment StartX=-202.765 StartY=20.303 StartZ=0 EndX=-143.955 EndY=20.303 EndZ=0
  constraints (18):
    c: Coincident(g0,g-7)
    c: Coincident(g0,g-8)
    c: Coincident(g1,g0)
    c: Tangent(g2,g-5)
    c: Coincident(g3,g-6)
    c: Coincident(g2,g3)
    c: Coincident(g0,g2)
    c: Diameter(g4) = 6
    c: Diameter(g5) = 6
    c: Coincident(g4,g-9)
    c: Coincident(g5,g-10)
    c: Horizontal(g1)
    c: Coincident(g6,g1)
    c: Tangent(g6,g-4)
    c: Coincident(g3,g-6)
    c: Coincident(g7,g3)
    c: Horizontal(g7)
    c: Coincident(g7,g6)
FEATURE [Sketcher::SketchObject] Sketch123
  ArcFitTolerance = 1e-06
  AttachmentSupport = -> [Pad011]
  ExternalGeometry = -> [Binder001]
  FullyConstrained = true
  MakeInternals = false
  MapMode = 5
  Placement = pos=(0,-2,0) rot=(1,0,0;1.5708rad)
  sketch-geometry (4):
    g0: LineSegment StartX=-108 StartY=36.8 StartZ=0 EndX=-90 EndY=36.8 EndZ=0
    g1: LineSegment StartX=-108 StartY=36.8 StartZ=0 EndX=-108 EndY=26.8 EndZ=0
    g2: LineSegment StartX=-108 StartY=26.8 StartZ=0 EndX=-90 EndY=26.8 EndZ=0
    g3: ArcOfCircle CenterX=-94 CenterY=31.8 CenterZ=0 NormalX=0 NormalY=0 NormalZ=1 AngleXU=0 Radius=6.40312 StartAngle=5.38713 EndAngle=7.17924
  constraints (13):
    c: Horizontal(g0)
    c: Coincident(g1,g0)
    c: Vertical(g1)
    c: Coincident(g2,g1)
    c: Horizontal(g2)
    c: DistanceX(g0,g0) = 18
    c: DistanceY(g1,g1) = 10
    c: Equal(g0,g2)
    c: DistanceX(g0,g-3) = 90
    c: DistanceY(g0,g-3) = 2.4
    c: Coincident(g3,g0)
    c: Coincident(g3,g2)
    c: DistanceX(g3,g0) = 4
FEATURE [PartDesign::Chamfer] Chamfer014
  Angle = 45
  Base = -> Pad011 [Edge80,Edge4,Edge7]
  BaseFeature = -> Pad011
  ChamferType = 0
  FlipDirection = false
  Refine = true
  Size = 1.9
  Size2 = 1
  SupportTransform = false
  Suppressed = false
  UseAllEdges = false
FEATURE [PartDesign::Pocket] Pocket006
  BaseFeature = -> Chamfer014
  Direction = (0,-1,2e-16)
  Length = 1.2
  Length2 = 5
  Profile = -> Sketch115
  ReferenceAxis = -> Sketch115 [N_Axis]
  Refine = true
  Suppressed = false
  Type = 0
FEATURE [Sketcher::SketchObject] Sketch116  label="Sketch116 - pieno per inserto M3 x 3 x 4,5"
  ArcFitTolerance = 1e-06
  AttachmentSupport = -> [Pocket006]
  ExternalGeometry = -> [Binder001]
  FullyConstrained = true
  MakeInternals = false
  MapMode = 5
  Placement = pos=(0,1.7e-15,0) rot=(0,0.707107,0.707107;3.14159rad)
  sketch-geometry (4):
    g0: Circle CenterX=43.2 CenterY=30.3 CenterZ=0 NormalX=0 NormalY=0 NormalZ=1 AngleXU=0 Radius=3.4
    g1: Circle CenterX=43.2 CenterY=12.1 CenterZ=0 NormalX=0 NormalY=0 NormalZ=1 AngleXU=0 Radius=3.4
    g2: Circle CenterX=18.6 CenterY=30.3 CenterZ=0 NormalX=0 NormalY=0 NormalZ=1 AngleXU=0 Radius=3.4
    g3: Circle CenterX=18.6 CenterY=12.1 CenterZ=0 NormalX=0 NormalY=0 NormalZ=1 AngleXU=0 Radius=3.4
  constraints (8):
    c: Diameter(g0) = 6.8
    c: Diameter(g1) = 6.8
    c: Diameter(g2) = 6.8
    c: Diameter(g3) = 6.8
    c: Coincident(g2,g-3)
    c: Coincident(g0,g-4)
    c: Coincident(g3,g-6)
    c: Coincident(g1,g-5)
FEATURE [PartDesign::Pad] Pad012
  BaseFeature = -> Pocket006
  Direction = (0,1,-2e-16)
  Length = 2.4
  Length2 = 10
  Profile = -> Sketch116
  ReferenceAxis = -> Sketch116 [N_Axis]
  Refine = true
  Suppressed = false
  Type = 0
FEATURE [PartDesign::Pocket] Pocket007
  BaseFeature = -> Pad012
  Direction = (0,-1,2e-16)
  Length = 0.6
  Length2 = 2.4
  Profile = -> Sketch117
  ReferenceAxis = -> Sketch117 [N_Axis]
  Refine = true
  Suppressed = false
  Type = 4
FEATURE [PartDesign::Pad] Pad013
  BaseFeature = -> Pocket007
  Direction = (0,-1,2e-16)
  Length = 1.6
  Length2 = 10
  Profile = -> Sketch118
  ReferenceAxis = -> Sketch118 [N_Axis]
  Refine = true
  Suppressed = false
  Type = 0
FEATURE [Sketcher::SketchObject] Sketch119
  ArcFitTolerance = 1e-06
  AttachmentSupport = -> [Pad013]
  ExternalGeometry = -> [Binder001]
  FullyConstrained = true
  MakeInternals = false
  MapMode = 5
  Placement = pos=(0,-3.6,0) rot=(1,0,0;1.5708rad)
  sketch-geometry (21):
    g0: LineSegment [constr] StartX=-82.8 StartY=3.2 StartZ=0 EndX=-82.8 EndY=39.2 EndZ=0
    g1: ArcOfCircle CenterX=-78.51 CenterY=34.8 CenterZ=0 NormalX=0 NormalY=0 NormalZ=1 AngleXU=0 Radius=3.5 StartAngle=4.71239 EndAngle=6.28319
    g2: ArcOfCircle CenterX=-78.51 CenterY=7.6 CenterZ=0 NormalX=0 NormalY=0 NormalZ=1 AngleXU=0 Radius=3.5 StartAngle=0 EndAngle=1.5708
    g3: ArcOfCircle CenterX=-5.6 CenterY=34.8 CenterZ=0 NormalX=0 NormalY=0 NormalZ=1 AngleXU=0 Radius=3.5 StartAngle=3.14159 EndAngle=4.71239
    g4: ArcOfCircle CenterX=-5.6 CenterY=7.6 CenterZ=0 NormalX=0 NormalY=0 NormalZ=1 AngleXU=0 Radius=3.5 StartAngle=1.5708 EndAngle=3.14159
    g5: LineSegment StartX=0 StartY=39.2 StartZ=0 EndX=0 EndY=31.3 EndZ=0
    g6: LineSegment StartX=0 StartY=39.2 StartZ=0 EndX=-9.1 EndY=39.2 EndZ=0
    g7: LineSegment StartX=0 StartY=3.2 StartZ=0 EndX=0 EndY=11.1 EndZ=0
    g8: LineSegment StartX=0 StartY=3.2 StartZ=0 EndX=-9.1 EndY=3.2 EndZ=0
    g9: LineSegment StartX=-82.8 StartY=3.2 StartZ=0 EndX=-75.01 EndY=3.2 EndZ=0
    g10: LineSegment StartX=-82.8 StartY=3.2 StartZ=0 EndX=-82.8 EndY=11.1 EndZ=0
    g11: LineSegment StartX=-82.8 StartY=39.2 StartZ=0 EndX=-82.8 EndY=31.3 EndZ=0
    g12: LineSegment StartX=-82.8 StartY=39.2 StartZ=0 EndX=-75.01 EndY=39.2 EndZ=0
    g13: LineSegment StartX=-82.8 StartY=31.3 StartZ=0 EndX=-78.51 EndY=31.3 EndZ=0
    g14: LineSegment StartX=-75.01 StartY=39.2 StartZ=0 EndX=-75.01 EndY=34.8 EndZ=0
    g15: LineSegment StartX=-82.8 StartY=11.1 StartZ=0 EndX=-78.51 EndY=11.1 EndZ=0
    g16: LineSegment StartX=-75.01 StartY=3.2 StartZ=0 EndX=-75.01 EndY=7.6 EndZ=0
    g17: LineSegment StartX=-9.1 StartY=39.2 StartZ=0 EndX=-9.1 EndY=34.8 EndZ=0
    g18: LineSegment StartX=0 StartY=31.3 StartZ=0 EndX=-5.6 EndY=31.3 EndZ=0
    g19: LineSegment StartX=0 StartY=11.1 StartZ=0 EndX=-5.6 EndY=11.1 EndZ=0
    g20: LineSegment StartX=-9.1 StartY=3.2 StartZ=0 EndX=-9.1 EndY=7.6 EndZ=0
  constraints (51):
    c: Coincident(g0,g-10)
    c: PointOnObject(g0,g-8)
    c: Vertical(g0)
    c: Coincident(g1,g-3)
    c: Coincident(g2,g-4)
    c: Coincident(g3,g-5)
    c: Coincident(g4,g-6)
    c: Radius(g4) = 3.5
    c: Radius(g3) = 3.5
    c: Radius(g1) = 3.5
    c: Radius(g2) = 3.5
    c: Coincident(g5,g-9)
    c: PointOnObject(g5,g-9)
    c: Coincident(g6,g5)
    c: PointOnObject(g6,g-8)
    c: Coincident(g7,g-9)
    c: PointOnObject(g7,g-9)
    c: Coincident(g8,g7)
    c: PointOnObject(g8,g-7)
    c: Coincident(g9,g0)
    c: PointOnObject(g9,g-7)
    c: Coincident(g10,g0)
    c: PointOnObject(g10,g0)
    c: Coincident(g11,g0)
    c: PointOnObject(g11,g0)
    c: Coincident(g12,g0)
    c: PointOnObject(g12,g-8)
    c: Coincident(g13,g11)
    c: Horizontal(g13)
    c: Coincident(g14,g12)
    c: Vertical(g14)
    c: Coincident(g15,g10)
    c: Horizontal(g15)
    c: Coincident(g16,g9)
    c: Vertical(g16)
    c: Coincident(g17,g6)
    c: Vertical(g17)
    c: Coincident(g18,g5)
    c: Horizontal(g18)
    c: Coincident(g19,g7)
    c: Horizontal(g19)
    c: Coincident(g20,g8)
    c: Vertical(g20)
    c: Tangent(g20,g4) = 1.5708
    c: Tangent(g4,g19) = -1.5708
    c: Tangent(g18,g3) = 1.5708
    c: Tangent(g3,g17) = -1.5708
    c: Tangent(g13,g1) = -1.5708
    c: Tangent(g1,g14) = 1.5708
    c: Tangent(g16,g2) = -1.5708
    c: Tangent(g2,g15) = 1.5708
FEATURE [PartDesign::Pocket] Pocket008
  BaseFeature = -> Pad013
  Direction = (0,1,-2e-16)
  Length = 1.6
  Length2 = 5
  Profile = -> Sketch119
  ReferenceAxis = -> Sketch119 [N_Axis]
  Refine = true
  Suppressed = false
  Type = 0
FEATURE [PartDesign::Pad] Pad017
  BaseFeature = -> Pocket008
  Direction = (0,-1,2e-16)
  Length = 1.6
  Length2 = 10
  Profile = -> Sketch123
  ReferenceAxis = -> Sketch123 [N_Axis]
  Refine = true
  Suppressed = false
  Type = 0
FEATURE [Sketcher::SketchObject] Sketch125
  ArcFitTolerance = 1e-06
  AttachmentSupport = -> [Pad017]
  ExternalGeometry = -> [Pad017]
  FullyConstrained = true
  MakeInternals = false
  MapMode = 5
  Placement = pos=(0,-3.6,8e-16) rot=(1,0,0;1.5708rad)
  sketch-geometry (20):
    g0: LineSegment StartX=-108 StartY=35.8 StartZ=0 EndX=-108 EndY=35 EndZ=0
    g1: LineSegment StartX=-108 StartY=35 StartZ=0 EndX=-97 EndY=35 EndZ=0
    g2: LineSegment StartX=-97 StartY=35 StartZ=0 EndX=-97 EndY=35.8 EndZ=0
    g3: LineSegment StartX=-97 StartY=35.8 StartZ=0 EndX=-108 EndY=35.8 EndZ=0
    g4: LineSegment StartX=-108 StartY=28.6 StartZ=0 EndX=-108 EndY=27.8 EndZ=0
    g5: LineSegment StartX=-108 StartY=27.8 StartZ=0 EndX=-97 EndY=27.8 EndZ=0
    g6: LineSegment StartX=-97 StartY=27.8 StartZ=0 EndX=-97 EndY=28.6 EndZ=0
    g7: LineSegment StartX=-97 StartY=28.6 StartZ=0 EndX=-108 EndY=28.6 EndZ=0
    g8: LineSegment StartX=-108 StartY=30.4 StartZ=0 EndX=-108 EndY=29.6 EndZ=0
    g9: LineSegment StartX=-108 StartY=29.6 StartZ=0 EndX=-97 EndY=29.6 EndZ=0
    g10: LineSegment StartX=-97 StartY=29.6 StartZ=0 EndX=-97 EndY=30.4 EndZ=0
    g11: LineSegment StartX=-97 StartY=30.4 StartZ=0 EndX=-108 EndY=30.4 EndZ=0
    g12: LineSegment StartX=-108 StartY=32.2 StartZ=0 EndX=-108 EndY=31.4 EndZ=0
    g13: LineSegment StartX=-108 StartY=31.4 StartZ=0 EndX=-97 EndY=31.4 EndZ=0
    g14: LineSegment StartX=-97 StartY=31.4 StartZ=0 EndX=-97 EndY=32.2 EndZ=0
    g15: LineSegment StartX=-97 StartY=32.2 StartZ=0 EndX=-108 EndY=32.2 EndZ=0
    g16: LineSegment StartX=-108 StartY=34 StartZ=0 EndX=-108 EndY=33.2 EndZ=0
    g17: LineSegment StartX=-108 StartY=33.2 StartZ=0 EndX=-97 EndY=33.2 EndZ=0
    g18: LineSegment StartX=-97 StartY=33.2 StartZ=0 EndX=-97 EndY=34 EndZ=0
    g19: LineSegment StartX=-97 StartY=34 StartZ=0 EndX=-108 EndY=34 EndZ=0
  constraints (55):
    c: Coincident(g1,g0)
    c: Horizontal(g1)
    c: Coincident(g2,g1)
    c: Vertical(g2)
    c: Coincident(g3,g2)
    c: Horizontal(g3)
    c: Coincident(g3,g0)
    c: DistanceX(g1,g1) = 11
    c: DistanceY(g2,g2) = 0.8
    c: Coincident(g5,g4)
    c: Horizontal(g5)
    c: Coincident(g6,g5)
    c: Vertical(g6)
    c: Coincident(g7,g6)
    c: Horizontal(g7)
    c: Coincident(g7,g4)
    c: Coincident(g9,g8)
    c: Horizontal(g9)
    c: Coincident(g10,g9)
    c: Vertical(g10)
    c: Coincident(g11,g10)
    c: Horizontal(g11)
    c: Coincident(g11,g8)
    c: Coincident(g13,g12)
    c: Horizontal(g13)
    c: Coincident(g14,g13)
    c: Vertical(g14)
    c: Coincident(g15,g14)
    c: Horizontal(g15)
    c: Coincident(g15,g12)
    c: Coincident(g17,g16)
    c: Horizontal(g17)
    c: Coincident(g18,g17)
    c: Vertical(g18)
    c: Coincident(g19,g18)
    c: Horizontal(g19)
    c: Coincident(g19,g16)
    c: Equal(g3,g19)
    c: Equal(g3,g15)
    c: Equal(g3,g11)
    c: Equal(g3,g7)
    c: Equal(g2,g18)
    c: Equal(g2,g14)
    c: Equal(g2,g10)
    c: Equal(g2,g6)
    c: DistanceY(g-4,g4) = 1
    c: DistanceY(g4,g8) = 1
    c: DistanceY(g8,g12) = 1
    c: DistanceY(g12,g16) = 1
    c: DistanceY(g16,g0) = 1
    c: Tangent(g0,g-5)
    c: Tangent(g16,g-5)
    c: Tangent(g12,g-5)
    c: Tangent(g8,g-5)
    c: Tangent(g4,g-5)
FEATURE [PartDesign::Chamfer] Chamfer009
  Angle = 45
  Base = -> Pad017 [Edge151,Edge154]
  BaseFeature = -> Pad017
  ChamferType = 1
  FlipDirection = false
  Refine = true
  Size = 1.5
  Size2 = 2.8
  SupportTransform = false
  Suppressed = false
  UseAllEdges = false
FEATURE [PartDesign::Pocket] Pocket009
  BaseFeature = -> Chamfer009
  Direction = (0,1,-2e-16)
  Length = 1
  Length2 = 5
  Profile = -> Sketch125
  ReferenceAxis = -> Sketch125 [N_Axis]
  Refine = true
  Suppressed = false
  Type = 0
FEATURE [PartDesign::Pad] Pad014
  BaseFeature = -> Pocket009
  Direction = (0,-1,2e-16)
  Length = 0.8
  Length2 = 10
  Profile = -> Sketch120
  ReferenceAxis = -> Sketch120 [N_Axis]
  Refine = true
  Suppressed = false
  Type = 0
FEATURE [Sketcher::SketchObject] Sketch124
  ArcFitTolerance = 1e-06
  AttachmentSupport = -> [Pad014]
  ExternalGeometry = -> [Binder001]
  FullyConstrained = true
  MakeInternals = false
  MapMode = 5
  Placement = pos=(0,-2.8,6e-16) rot=(1,0,0;1.5708rad)
  sketch-geometry (4):
    g0: LineSegment StartX=-129 StartY=39.2 StartZ=0 EndX=-131.599 EndY=31.2 EndZ=0
    g1: LineSegment StartX=-118 StartY=39.2 StartZ=0 EndX=-120.599 EndY=31.2 EndZ=0
    g2: LineSegment StartX=-129 StartY=39.2 StartZ=0 EndX=-118 EndY=39.2 EndZ=0
    g3: LineSegment StartX=-120.599 StartY=31.2 StartZ=0 EndX=-131.599 EndY=31.2 EndZ=0
  constraints (12):
    c: PointOnObject(g0,g-3)
    c: PointOnObject(g1,g-3)
    c: Parallel(g-4,g0)
    c: Parallel(g-4,g1)
    c: Coincident(g2,g0)
    c: Coincident(g2,g1)
    c: DistanceX(g2,g2) = 11
    c: DistanceY(g1,g1) = 8
    c: Coincident(g3,g1)
    c: Horizontal(g3)
    c: Coincident(g3,g0)
    c: DistanceX(g1,g-3) = 118
FEATURE [PartDesign::Pad] Pad018
  BaseFeature = -> Pad014
  Direction = (0,-1,2e-16)
  Length = 1.2
  Length2 = 10
  Profile = -> Sketch124
  ReferenceAxis = -> Sketch124 [N_Axis]
  Refine = true
  Suppressed = false
  Type = 0
FEATURE [Sketcher::SketchObject] Sketch126
  ArcFitTolerance = 1e-06
  AttachmentSupport = -> [Pad018]
  ExternalGeometry = -> [Pad018]
  FullyConstrained = true
  MakeInternals = false
  MapMode = 5
  Placement = pos=(0,-4,0) rot=(1,0,0;1.5708rad)
  sketch-geometry (8):
    g0: LineSegment StartX=-129.877 StartY=36.5 StartZ=0 EndX=-130.137 EndY=35.7 EndZ=0
    g1: LineSegment StartX=-130.69 StartY=34 StartZ=0 EndX=-130.95 EndY=33.2 EndZ=0
    g2: LineSegment StartX=-129.877 StartY=36.5 StartZ=0 EndX=-118.877 EndY=36.5 EndZ=0
    g3: LineSegment StartX=-130.137 StartY=35.7 StartZ=0 EndX=-119.137 EndY=35.7 EndZ=0
    g4: LineSegment StartX=-130.69 StartY=34 StartZ=0 EndX=-119.69 EndY=34 EndZ=0
    g5: LineSegment StartX=-130.95 StartY=33.2 StartZ=0 EndX=-119.95 EndY=33.2 EndZ=0
    g6: LineSegment StartX=-118.877 StartY=36.5 StartZ=0 EndX=-119.137 EndY=35.7 EndZ=0
    g7: LineSegment StartX=-119.69 StartY=34 StartZ=0 EndX=-119.95 EndY=33.2 EndZ=0
  constraints (20):
    c: Coincident(g2,g0)
    c: Horizontal(g2)
    c: Coincident(g3,g0)
    c: Horizontal(g3)
    c: Coincident(g4,g1)
    c: Horizontal(g4)
    c: Coincident(g5,g1)
    c: Horizontal(g5)
    c: Coincident(g6,g2)
    c: Coincident(g6,g3)
    c: Coincident(g7,g4)
    c: Coincident(g7,g5)
    c: Tangent(g0,g-4)
    c: Tangent(g6,g-5)
    c: Tangent(g1,g-4)
    c: Tangent(g7,g-5)
    c: DistanceY(g3,g2) = 0.8
    c: DistanceY(g5,g4) = 0.8
    c: DistanceY(g-6,g1) = 2
    c: DistanceY(g-6,g0) = 4.5
FEATURE [PartDesign::Chamfer] Chamfer008
  Angle = 45
  Base = -> Pad018 [Edge257]
  BaseFeature = -> Pad018
  ChamferType = 1
  FlipDirection = false
  Refine = true
  Size = 1
  Size2 = 6
  SupportTransform = false
  Suppressed = false
  UseAllEdges = false
FEATURE [PartDesign::Pocket] Pocket010
  BaseFeature = -> Chamfer008
  Direction = (0,1,-2e-16)
  Length = 1
  Length2 = 5
  Profile = -> Sketch126
  ReferenceAxis = -> Sketch126 [N_Axis]
  Refine = true
  Suppressed = false
  Type = 0
FEATURE [PartDesign::Pad] Pad015
  BaseFeature = -> Pocket010
  Direction = (0,-1,2e-16)
  Length = 2
  Length2 = 10
  Profile = -> Sketch121
  ReferenceAxis = -> Sketch121 [N_Axis]
  Refine = true
  Suppressed = false
  Type = 0
FEATURE [PartDesign::Pad] Pad016
  BaseFeature = -> Pad015
  Direction = (0,-1,2e-16)
  Length = 1.6
  Length2 = 10
  Profile = -> Sketch122
  ReferenceAxis = -> Sketch122 [N_Axis]
  Refine = true
  Suppressed = false
  Type = 0
FEATURE [Sketcher::SketchObject] Sketch129
  ArcFitTolerance = 1e-06
  AttachmentSupport = -> [Pad016]
  ExternalGeometry = -> [Binder001]
  FullyConstrained = true
  MakeInternals = false
  MapMode = 5
  Placement = pos=(0,-3.6,0) rot=(1,0,0;1.5708rad)
  sketch-geometry (12):
    g0: LineSegment [constr] StartX=-192.176 StartY=-3.18451 StartZ=0 EndX=-181.223 EndY=20.303 EndZ=0
    g1: LineSegment [constr] StartX=-202.765 StartY=20.303 StartZ=0 EndX=-181.223 EndY=20.303 EndZ=0
    g2: LineSegment StartX=-202.765 StartY=20.303 StartZ=0 EndX=-181.223 EndY=20.303 EndZ=0
    g3: LineSegment StartX=-192.176 StartY=-3.18451 StartZ=0 EndX=-196.804 EndY=-13.1107 EndZ=0
    g4: ArcOfCircle CenterX=-207.583 CenterY=4 CenterZ=0 NormalX=0 NormalY=0 NormalZ=1 AngleXU=0 Radius=17 StartAngle=5.84685 EndAngle=7.56663
    g5: ArcOfEllipse CenterX=-181.223 CenterY=8.55923 CenterZ=0 NormalX=0 NormalY=0 NormalZ=1 MajorRadius=23.4779 MinorRadius=11.7437 AngleXU=2e-16 StartAngle=4.71239 EndAngle=7.85398
    g6: LineSegment [constr] StartX=-157.745 StartY=8.55923 StartZ=0 EndX=-204.701 EndY=8.55923 EndZ=0
    g7: LineSegment [constr] StartX=-181.223 StartY=20.303 StartZ=0 EndX=-181.223 EndY=-3.18451 EndZ=0
    g8: GeomPoint [constr] X=-160.894 Y=8.55923 Z=0
    g9: GeomPoint [constr] X=-201.553 Y=8.55923 Z=0
    g10: ArcOfCircle CenterX=-181.223 CenterY=-20.3763 CenterZ=0 NormalX=0 NormalY=0 NormalZ=1 AngleXU=0 Radius=17.1918 StartAngle=1.57079 EndAngle=2.70526
    g11: GeomPoint [constr] X=-181.223 Y=-3.18451 Z=0
  constraints (23):
    c: Coincident(g0,g-5)
    c: Coincident(g1,g-6)
    c: Horizontal(g1)
    c: Coincident(g1,g0)
    c: Parallel(g0,g-4)
    c: Coincident(g2,g1)
    c: Coincident(g2,g0)
    c: Coincident(g3,g0)
    c: Equal(g4,g-5)
    c: Coincident(g4,g1)
    c: Coincident(g4,g0)
    c: InternalAlignment(g6-g9 -> g5) x4
    c: Vertical(g5,g0)
    c: Horizontal(g6)
    c: Coincident(g5,g0)
    c: DistanceX(g6,g-3) = 10.1
    c: Tangent(g10,g3) = -1.5708
    c: PointOnObject(g11,g10)
    c: Tangent(g5,g10,g11) = 1.5708
    c: Coincident(g10,g5)
    c: Coincident(g11,g7)
    c: Parallel(g3,g-4)
    c: Horizontal(g5,g0)
FEATURE [Sketcher::SketchObject] Sketch130
  ArcFitTolerance = 1e-06
  AttachmentOffset = pos=(0,0,-1.6) rot=(0,0,1;0rad)
  AttachmentSupport = -> [Pad016]
  ExternalGeometry = -> [Binder001]
  FullyConstrained = true
  MakeInternals = false
  MapMode = 5
  Placement = pos=(0,-2,-4e-16) rot=(1,0,0;1.5708rad)
  sketch-geometry (12):
    g0: LineSegment [constr] StartX=-192.176 StartY=-3.18451 StartZ=0 EndX=-181.223 EndY=20.303 EndZ=0
    g1: LineSegment [constr] StartX=-202.765 StartY=20.303 StartZ=0 EndX=-181.223 EndY=20.303 EndZ=0
    g2: LineSegment StartX=-202.765 StartY=20.303 StartZ=0 EndX=-181.223 EndY=20.303 EndZ=0
    g3: LineSegment StartX=-192.176 StartY=-3.18451 StartZ=0 EndX=-193.827 EndY=-6.72678 EndZ=0
    g4: ArcOfCircle CenterX=-207.583 CenterY=4 CenterZ=0 NormalX=0 NormalY=0 NormalZ=1 AngleXU=0 Radius=17 StartAngle=5.84685 EndAngle=7.56663
    g5: ArcOfEllipse CenterX=-181.223 CenterY=10.803 CenterZ=0 NormalX=0 NormalY=0 NormalZ=1 MajorRadius=14.4779 MinorRadius=9.5 AngleXU=0 StartAngle=4.71239 EndAngle=7.85398
    g6: LineSegment [constr] StartX=-166.745 StartY=10.803 StartZ=0 EndX=-195.701 EndY=10.803 EndZ=0
    g7: LineSegment [constr] StartX=-181.223 StartY=20.303 StartZ=0 EndX=-181.223 EndY=1.30297 EndZ=0
    g8: GeomPoint [constr] X=-170.298 Y=10.803 Z=0
    g9: GeomPoint [constr] X=-192.148 Y=10.803 Z=0
    g10: ArcOfCircle CenterX=-181.223 CenterY=-12.6042 CenterZ=0 NormalX=0 NormalY=0 NormalZ=1 AngleXU=0 Radius=13.9072 StartAngle=1.5708 EndAngle=2.70526
    g11: GeomPoint [constr] X=-181.223 Y=1.30297 Z=0
  constraints (23):
    c: Coincident(g0,g-5)
    c: Coincident(g1,g-6)
    c: Horizontal(g1)
    c: Coincident(g1,g0)
    c: Parallel(g0,g-4)
    c: Coincident(g2,g1)
    c: Coincident(g2,g0)
    c: Coincident(g3,g0)
    c: Equal(g4,g-5)
    c: Coincident(g4,g1)
    c: Coincident(g4,g0)
    c: InternalAlignment(g6-g9 -> g5) x4
    c: Vertical(g5,g0)
    c: Horizontal(g6)
    c: Coincident(g5,g0)
    c: DistanceX(g6,g-3) = 19.1
    c: Tangent(g10,g3) = -1.5708
    c: PointOnObject(g11,g10)
    c: Tangent(g5,g10,g11) = 1.5708
    c: Coincident(g10,g5)
    c: Coincident(g11,g7)
    c: Parallel(g3,g-4)
    c: DistanceY(g5,g0) = 19
FEATURE [Part::Part2DObjectPython] Clone2D001  label="Sketch130 (2D)"  # Draft 2D object (typed FeaturePython)
  Fuse = false
  Objects = -> [Sketch130]
  Placement = pos=(0,-2,-4e-16) rot=(1,0,0;1.5708rad)
  Scale = (1,1,1)
FEATURE [Sketcher::SketchObject] Sketch131
  ArcFitTolerance = 1e-06
  AttachmentOffset = pos=(0,0,-3.5) rot=(0,0,1;0rad)
  AttachmentSupport = -> [Pad016]
  ExternalGeometry = -> [Binder001]
  FullyConstrained = true
  MakeInternals = false
  MapMode = 5
  Placement = pos=(0,-0.1,-8e-16) rot=(1,0,0;1.5708rad)
  sketch-geometry (1):
    g0: GeomPoint X=-197.47 Y=8.55923 Z=0
  constraints (1):
    c: Symmetric(g-6,g-4,g0)
FEATURE [Sketcher::SketchObject] Sketch132
  ArcFitTolerance = 1e-06
  AttachmentSupport = -> [Pad016]
  ExternalGeometry = -> [Binder001]
  FullyConstrained = true
  MakeInternals = false
  MapMode = 5
  Placement = pos=(0,-3.6,0) rot=(1,0,0;1.5708rad)
  sketch-geometry (3):
    g0: LineSegment [constr] StartX=-215.42 StartY=-53.0314 StartZ=0 EndX=-167.782 EndY=-53.0314 EndZ=0
    g1: Circle CenterX=-191.282 CenterY=-53.0314 CenterZ=0 NormalX=0 NormalY=0 NormalZ=1 AngleXU=0 Radius=11.5
    g2: Circle CenterX=-191.282 CenterY=-53.0314 CenterZ=0 NormalX=0 NormalY=0 NormalZ=1 AngleXU=0 Radius=10.7
  constraints (8):
    c: Coincident(g0,g-3)
    c: PointOnObject(g0,g-4)
    c: Horizontal(g0)
    c: Diameter(g1) = 23
    c: PointOnObject(g1,g0)
    c: DistanceX(g1,g0) = 23.5
    c: Diameter(g2) = 21.4
    c: Coincident(g2,g1)
FEATURE [Part::Part2DObjectPython] ShapeString  # Draft 2D object (typed FeaturePython)
  FontFile = <path>
  Fuse = false
  Justification = 6
  JustificationReference = 0
  KeepLeftMargin = false
  MakeFace = true
  ObliqueAngle = 0
  Placement = pos=(-199,-3.6,-57.5) rot=(1,0,0;1.5708rad)
  ScaleToSize = true
  Size = 10
  String = AS
  Tracking = 0
FEATURE [Sketcher::SketchObject] Sketch133
  ArcFitTolerance = 1e-06
  AttachmentSupport = -> [Binder]
  ExternalGeometry = -> [Binder]
  FullyConstrained = true
  MakeInternals = false
  MapMode = 5
  Placement = pos=(0,9e-16,0) rot=(0,0.707107,0.707107;3.14159rad)
  sketch-geometry (30):
    g0: LineSegment StartX=0 StartY=39.2 StartZ=0 EndX=0 EndY=3.2 EndZ=0
    g1: LineSegment StartX=0 StartY=3.2 StartZ=0 EndX=82.8 EndY=3.2 EndZ=0
    g2: LineSegment StartX=82.8 StartY=3.2 StartZ=0 EndX=82.8 EndY=6.2 EndZ=0
    g3: LineSegment StartX=82.8 StartY=6.2 StartZ=0 EndX=91.752 EndY=6.2 EndZ=0
    g4: LineSegment StartX=0 StartY=39.2 StartZ=0 EndX=195.887 EndY=39.2 EndZ=0
    g5: LineSegment StartX=195.887 StartY=39.2 StartZ=0 EndX=202.765 EndY=20.303 EndZ=0
    g6: LineSegment StartX=192.333 StartY=24.9893 StartZ=0 EndX=196.467 EndY=26.4942 EndZ=0
    g7: LineSegment StartX=196.467 StartY=26.4942 StartZ=0 EndX=194.073 EndY=33.0721 EndZ=0
    g8: LineSegment StartX=194.073 StartY=33.0721 StartZ=0 EndX=189.939 EndY=31.5672 EndZ=0
    g9: LineSegment StartX=189.939 StartY=31.5672 StartZ=0 EndX=192.333 EndY=24.9893 EndZ=0
    g10: ArcOfCircle CenterX=107.6 CenterY=4 CenterZ=0 NormalX=0 NormalY=0 NormalZ=1 AngleXU=0 Radius=16 StartAngle=1.5708 EndAngle=3.00366
    g11: LineSegment StartX=107.6 StartY=20 StartZ=0 EndX=132.428 EndY=20 EndZ=0
    g12: ArcOfCircle [constr] CenterX=132.428 CenterY=4 CenterZ=0 NormalX=0 NormalY=0 NormalZ=1 AngleXU=0 Radius=16 StartAngle=0.314159 EndAngle=1.5708
    g13: LineSegment StartX=147.645 StartY=8.94427 StartZ=0 EndX=176.685 EndY=-80.4316 EndZ=0
    g14: LineSegment StartX=176.685 StartY=-80.4316 StartZ=0 EndX=215.932 EndY=-80.4316 EndZ=0
    g15: ArcOfCircle CenterX=207.583 CenterY=4 CenterZ=0 NormalX=0 NormalY=0 NormalZ=1 AngleXU=0 Radius=17 StartAngle=1.85815 EndAngle=3.57792
    g16: ArcOfCircle CenterX=184.801 CenterY=-67.3089 CenterZ=0 NormalX=0 NormalY=0 NormalZ=1 AngleXU=0 Radius=33.7833 StartAngle=5.88425 EndAngle=6.71952
    g17: LineSegment StartX=192.176 StartY=-3.18451 StartZ=0 EndX=215.42 EndY=-53.0314 EndZ=0
    g18: Circle CenterX=5.6 CenterY=34.8 CenterZ=0 NormalX=0 NormalY=0 NormalZ=1 AngleXU=0 Radius=1.8
    g19: Circle CenterX=5.6 CenterY=7.6 CenterZ=0 NormalX=0 NormalY=0 NormalZ=1 AngleXU=0 Radius=1.8
    g20: Circle CenterX=78.51 CenterY=34.8 CenterZ=0 NormalX=0 NormalY=0 NormalZ=1 AngleXU=0 Radius=1.8
    g21: Circle CenterX=78.51 CenterY=7.6 CenterZ=0 NormalX=0 NormalY=0 NormalZ=1 AngleXU=0 Radius=1.8
    g22: Circle CenterX=184.08 CenterY=34.8 CenterZ=0 NormalX=0 NormalY=0 NormalZ=1 AngleXU=0 Radius=1.8
    g23: Circle CenterX=179.305 CenterY=-76.8316 CenterZ=0 NormalX=0 NormalY=0 NormalZ=1 AngleXU=0 Radius=1.8
    g24: Circle CenterX=213.443 CenterY=-76.8316 CenterZ=0 NormalX=0 NormalY=0 NormalZ=1 AngleXU=0 Radius=1.8
    g25: Circle CenterX=19 CenterY=21.2 CenterZ=0 NormalX=0 NormalY=0 NormalZ=1 AngleXU=0 Radius=6.3
    g26: Circle CenterX=42 CenterY=21.2 CenterZ=0 NormalX=0 NormalY=0 NormalZ=1 AngleXU=0 Radius=6.3
    g27: Circle CenterX=65 CenterY=21.2 CenterZ=0 NormalX=0 NormalY=0 NormalZ=1 AngleXU=0 Radius=6.3
    g28: LineSegment StartX=132.428 StartY=20 StartZ=0 EndX=144.053 EndY=20 EndZ=0
    g29: LineSegment StartX=147.645 StartY=8.94427 StartZ=0 EndX=144.053 EndY=20 EndZ=0
  constraints (65):
    c: Coincident(g0,g-4)
    c: Coincident(g0,g-5)
    c: Coincident(g1,g0)
    c: Coincident(g1,g-6)
    c: Coincident(g2,g1)
    c: Coincident(g2,g-7)
    c: Coincident(g3,g2)
    c: Coincident(g3,g-8)
    c: Coincident(g4,g0)
    c: Coincident(g4,g-16)
    c: Coincident(g5,g4)
    c: Coincident(g5,g-16)
    c: Coincident(g6,g-20)
    c: Coincident(g6,g-21)
    c: Coincident(g7,g6)
    c: Coincident(g7,g-23)
    c: Coincident(g8,g7)
    c: Coincident(g8,g-22)
    c: Coincident(g9,g8)
    c: Coincident(g9,g6)
    c: Equal(g10,g-8)
    c: Coincident(g10,g3)
    c: Coincident(g10,g-9)
    c: Coincident(g11,g10)
    c: Coincident(g11,g-10)
    c: Equal(g12,g-10)
    c: Coincident(g12,g11)
    c: Coincident(g12,g-11)
    c: Coincident(g13,g12)
    c: Coincident(g13,g-12)
    c: Coincident(g14,g13)
    c: Coincident(g14,g-13)
    c: Equal(g15,g-15)
    c: Coincident(g15,g5)
    c: Coincident(g15,g-15)
    c: Equal(g16,g-13)
    c: Coincident(g16,g14)
    c: Coincident(g16,g-14)
    c: Coincident(g17,g15)
    c: Coincident(g17,g16)
    c: Equal(g18,g-28)
    c: Equal(g19,g-29)
    c: Equal(g20,g-26)
    c: Equal(g21,g-27)
    c: Equal(g22,g-17)
    c: Equal(g24,g-25)
    c: Equal(g23,g-24)
    c: Coincident(g23,g-24)
    c: Coincident(g24,g-25)
    c: Coincident(g22,g-17)
    c: Coincident(g20,g-26)
    c: Coincident(g21,g-27)
    c: Coincident(g18,g-28)
    c: Coincident(g19,g-29)
    c: Equal(g25,g-30)
    c: Equal(g26,g-31)
    c: Equal(g27,g-32)
    c: Coincident(g25,g-30)
    c: Coincident(g26,g-31)
    c: Coincident(g27,g-32)
    c: Parallel(g28,g11)
    c: Parallel(g29,g13)
    c: Coincident(g28,g11)
    c: Coincident(g29,g12)
    c: Coincident(g29,g28)
FEATURE [PartDesign::Pad] Pad019
  Direction = (0,1,-2e-16)
  Length = 2
  Length2 = 10
  Profile = -> Sketch133
  ReferenceAxis = -> Sketch133 [N_Axis]
  Refine = true
  Suppressed = false
  Type = 0
FEATURE [Sketcher::SketchObject] Sketch091  label="Sketch091 - forma anteriore"
  ArcFitTolerance = 1e-06
  AttachmentSupport = -> [Pad019]
  ExternalGeometry = -> [Binder]
  FullyConstrained = true
  MakeInternals = false
  MapMode = 5
  Placement = pos=(0,2,0) rot=(0,0.707107,0.707107;3.14159rad)
  sketch-geometry (12):
    g0: Circle CenterX=5.6 CenterY=34.8 CenterZ=0 NormalX=0 NormalY=0 NormalZ=1 AngleXU=0 Radius=1.8
    g1: Circle CenterX=5.6 CenterY=7.6 CenterZ=0 NormalX=0 NormalY=0 NormalZ=1 AngleXU=0 Radius=1.8
    g2: Circle CenterX=78.51 CenterY=34.8 CenterZ=0 NormalX=0 NormalY=0 NormalZ=1 AngleXU=0 Radius=1.8
    g3: Circle CenterX=78.51 CenterY=7.6 CenterZ=0 NormalX=0 NormalY=0 NormalZ=1 AngleXU=0 Radius=1.8
    g4: LineSegment StartX=0 StartY=39.2 StartZ=0 EndX=0 EndY=3.2 EndZ=0
    g5: LineSegment StartX=0 StartY=3.2 StartZ=0 EndX=82.8 EndY=3.2 EndZ=0
    g6: LineSegment StartX=82.8 StartY=3.2 StartZ=0 EndX=82.8 EndY=39.2 EndZ=0
    g7: LineSegment StartX=82.8 StartY=39.2 StartZ=0 EndX=0 EndY=39.2 EndZ=0
    g8: ArcOfCircle CenterX=19 CenterY=21.2 CenterZ=0 NormalX=0 NormalY=0 NormalZ=1 AngleXU=0 Radius=10 StartAngle=1.5708 EndAngle=4.71239
    g9: ArcOfCircle CenterX=65 CenterY=21.2 CenterZ=0 NormalX=0 NormalY=0 NormalZ=1 AngleXU=0 Radius=10 StartAngle=4.71239 EndAngle=7.85398
    g10: LineSegment StartX=19 StartY=31.2 StartZ=0 EndX=65 EndY=31.2 EndZ=0
    g11: LineSegment StartX=19 StartY=11.2 StartZ=0 EndX=65 EndY=11.2 EndZ=0
  constraints (25):
    c: Equal(g2,g-7)
    c: Equal(g3,g-8)
    c: Equal(g1,g-13)
    c: Equal(g0,g-12)
    c: Coincident(g0,g-12)
    c: Coincident(g1,g-13)
    c: Coincident(g3,g-8)
    c: Coincident(g2,g-7)
    c: Coincident(g4,g-4)
    c: Coincident(g4,g-5)
    c: Coincident(g5,g4)
    c: Coincident(g5,g-6)
    c: Coincident(g6,g5)
    c: PointOnObject(g6,g-3)
    c: Vertical(g6)
    c: Coincident(g7,g6)
    c: Coincident(g7,g4)
    c: Tangent(g8,g10) = 1.5708
    c: Tangent(g8,g11) = -1.5708
    c: Tangent(g9,g10) = 1.5708
    c: Tangent(g9,g11) = -1.5708
    c: Equal(g8,g9)
    c: Radius(g8) = 10
    c: Coincident(g8,g-11)
    c: Coincident(g9,g-9)
FEATURE [Sketcher::SketchObject] Sketch093  label="Sketch093 - scavi interni pulsanti"
  ArcFitTolerance = 1e-06
  AttachmentSupport = -> [Pad019]
  ExternalGeometry = -> [Binder]
  FullyConstrained = true
  MakeInternals = false
  MapMode = 5
  Placement = pos=(0,1.8e-15,0) rot=(1,0,0;1.5708rad)
  sketch-geometry (3):
    g0: Circle CenterX=-65 CenterY=21.2 CenterZ=0 NormalX=0 NormalY=0 NormalZ=1 AngleXU=0 Radius=7.3
    g1: Circle CenterX=-42 CenterY=21.2 CenterZ=0 NormalX=0 NormalY=0 NormalZ=1 AngleXU=0 Radius=7.3
    g2: Circle CenterX=-19 CenterY=21.2 CenterZ=0 NormalX=0 NormalY=0 NormalZ=1 AngleXU=0 Radius=7.3
  constraints (6):
    c: Coincident(g0,g-3)
    c: Coincident(g1,g-4)
    c: Coincident(g2,g-5)
    c: Diameter(g0) = 14.6
    c: Diameter(g1) = 14.6
    c: Diameter(g2) = 14.6
FEATURE [Sketcher::SketchObject] Sketch094  label="Sketch094 - forma centrale"
  ArcFitTolerance = 1e-06
  AttachmentSupport = -> [Pad019]
  ExternalGeometry = -> [Binder]
  FullyConstrained = true
  MakeInternals = false
  MapMode = 5
  Placement = pos=(0,2,0) rot=(0,0.707107,0.707107;3.14159rad)
  sketch-geometry (4):
    g0: LineSegment StartX=137.815 StartY=39.2 StartZ=0 EndX=142.655 EndY=24.303 EndZ=0
    g1: LineSegment StartX=110.815 StartY=24.303 StartZ=0 EndX=142.655 EndY=24.303 EndZ=0
    g2: LineSegment StartX=137.815 StartY=39.2 StartZ=0 EndX=110.815 EndY=39.2 EndZ=0
    g3: ArcOfCircle CenterX=92.2534 CenterY=31.7515 CenterZ=0 NormalX=0 NormalY=0 NormalZ=1 AngleXU=0 Radius=20 StartAngle=5.90156 EndAngle=6.66481
  constraints (12):
    c: PointOnObject(g0,g-3)
    c: Tangent(g0,g-5)
    c: Horizontal(g1)
    c: Coincident(g1,g0)
    c: Coincident(g2,g0)
    c: PointOnObject(g2,g-3)
    c: DistanceX(g2,g2) = 27
    c: Vertical(g1,g2)
    c: Coincident(g3,g2)
    c: Radius(g3) = 20
    c: Coincident(g3,g1)
    c: DistanceY(g-6,g0) = 4
FEATURE [Sketcher::SketchObject] Sketch095  label="Sketch095 - forma posteriore"
  ArcFitTolerance = 1e-06
  AttachmentSupport = -> [Pad019]
  ExternalGeometry = -> [Binder]
  FullyConstrained = true
  MakeInternals = false
  MapMode = 5
  Placement = pos=(0,2,0) rot=(0,0.707107,0.707107;3.14159rad)
  sketch-geometry (15):
    g0: LineSegment StartX=137.815 StartY=39.2 StartZ=0 EndX=143.955 EndY=20.303 EndZ=0
    g1: LineSegment StartX=143.955 StartY=20.303 StartZ=0 EndX=190.141 EndY=20.303 EndZ=0
    g2: ArcOfCircle CenterX=184.08 CenterY=34.8 CenterZ=0 NormalX=0 NormalY=0 NormalZ=1 AngleXU=0 Radius=3.5 StartAngle=3.49066 EndAngle=4.71239
    g3: LineSegment StartX=180.791 StartY=33.6029 StartZ=0 EndX=178.754 EndY=39.2 EndZ=0
    g4: LineSegment StartX=184.08 StartY=31.3 StartZ=0 EndX=186.139 EndY=31.3 EndZ=0
    g5: LineSegment StartX=190.141 StartY=20.303 StartZ=0 EndX=186.139 EndY=31.3 EndZ=0
    g6: LineSegment StartX=137.815 StartY=39.2 StartZ=0 EndX=156.815 EndY=39.2 EndZ=0
    g7: LineSegment StartX=178.754 StartY=39.2 StartZ=0 EndX=168.815 EndY=39.2 EndZ=0
    g8: LineSegment StartX=156.815 StartY=31.2 StartZ=0 EndX=168.815 EndY=31.2 EndZ=0
    g9: ArcOfCircle CenterX=176.411 CenterY=35.2 CenterZ=0 NormalX=0 NormalY=0 NormalZ=1 AngleXU=0 Radius=20 StartAngle=2.94023 EndAngle=3.34295
    g10: ArcOfCircle CenterX=188.411 CenterY=35.2 CenterZ=0 NormalX=0 NormalY=0 NormalZ=1 AngleXU=0 Radius=20 StartAngle=2.94023 EndAngle=3.34295
    g11: LineSegment StartX=157.815 StartY=39.2 StartZ=0 EndX=167.815 EndY=39.2 EndZ=0
    g12: LineSegment StartX=157.436 StartY=36.2 StartZ=0 EndX=167.436 EndY=36.2 EndZ=0
    g13: ArcOfCircle CenterX=177.411 CenterY=35.2 CenterZ=0 NormalX=0 NormalY=0 NormalZ=1 AngleXU=0 Radius=20 StartAngle=2.94023 EndAngle=3.09157
    g14: ArcOfCircle CenterX=187.411 CenterY=35.2 CenterZ=0 NormalX=0 NormalY=0 NormalZ=1 AngleXU=0 Radius=20 StartAngle=2.94023 EndAngle=3.09157
  constraints (46):
    c: PointOnObject(g0,g-3)
    c: Tangent(g0,g-6)
    c: Coincident(g1,g0)
    c: Horizontal(g1)
    c: Radius(g2) = 3.5
    c: Coincident(g2,g-5)
    c: PointOnObject(g3,g-3)
    c: Parallel(g3,g-4)
    c: Tangent(g3,g2) = 1.5708
    c: Horizontal(g4)
    c: Tangent(g4,g2) = -1.5708
    c: Coincident(g5,g1)
    c: Parallel(g5,g-4)
    c: Coincident(g5,g4)
    c: DistanceX(g4,g-8) = 3.8
    c: Coincident(g6,g0)
    c: PointOnObject(g6,g-3)
    c: Coincident(g7,g3)
    c: PointOnObject(g7,g-3)
    c: Horizontal(g8)
    c: DistanceX(g6,g7) = 12
    c: Vertical(g8,g6)
    c: Vertical(g7,g8)
    c: DistanceY(g8,g6) = 8
    c: Coincident(g9,g8)
    c: Coincident(g9,g6)
    c: Coincident(g10,g7)
    c: Coincident(g10,g8)
    c: Radius(g9) = 20
    c: Radius(g10) = 20
    c: PointOnObject(g11,g-3)
    c: PointOnObject(g11,g-3)
    c: DistanceX(g11,g11) = 10
    c: DistanceX(g6,g11) = 1
    c: Horizontal(g12)
    c: Equal(g12,g11)
    c: DistanceY(g12,g11) = 3
    c: Coincident(g13,g11)
    c: Coincident(g13,g12)
    c: Radius(g13) = 20
    c: Coincident(g14,g11)
    c: Coincident(g14,g12)
    c: Radius(g14) = 20
    c: DistanceX(g0,g6) = 19
    c: Horizontal(g9,g13)
    c: Horizontal(g0,g-4)
FEATURE [Sketcher::SketchObject] Sketch096  label="Sketch096 - forma impugnatura"
  ArcFitTolerance = 1e-06
  AttachmentSupport = -> [Pad019]
  ExternalGeometry = -> [Binder]
  FullyConstrained = true
  MakeInternals = false
  MapMode = 5
  Placement = pos=(0,2,0) rot=(0,0.707107,0.707107;3.14159rad)
  sketch-geometry (8):
    g0: LineSegment StartX=176.685 StartY=-80.4316 StartZ=0 EndX=143.955 EndY=20.303 EndZ=0
    g1: LineSegment StartX=176.685 StartY=-80.4316 StartZ=0 EndX=215.932 EndY=-80.4316 EndZ=0
    g2: Circle CenterX=179.305 CenterY=-76.8316 CenterZ=0 NormalX=0 NormalY=0 NormalZ=1 AngleXU=0 Radius=3
    g3: Circle CenterX=213.443 CenterY=-76.8316 CenterZ=0 NormalX=0 NormalY=0 NormalZ=1 AngleXU=0 Radius=3
    g4: LineSegment StartX=143.955 StartY=20.303 StartZ=0 EndX=202.765 EndY=20.303 EndZ=0
    g5: LineSegment StartX=215.42 StartY=-53.0314 StartZ=0 EndX=192.176 EndY=-3.18451 EndZ=0
    g6: ArcOfCircle CenterX=184.801 CenterY=-67.3089 CenterZ=0 NormalX=0 NormalY=0 NormalZ=1 AngleXU=0 Radius=33.7833 StartAngle=5.88425 EndAngle=6.71952
    g7: ArcOfCircle CenterX=207.583 CenterY=4 CenterZ=0 NormalX=0 NormalY=0 NormalZ=1 AngleXU=0 Radius=17 StartAngle=1.85815 EndAngle=3.57792
  constraints (19):
    c: Coincident(g0,g-4)
    c: PointOnObject(g0,g-3)
    c: Horizontal(g0,g-7)
    c: Coincident(g1,g0)
    c: Coincident(g1,g-5)
    c: Diameter(g2) = 6
    c: Diameter(g3) = 6
    c: Coincident(g2,g-9)
    c: Coincident(g3,g-10)
    c: Coincident(g4,g0)
    c: Coincident(g5,g-6)
    c: Coincident(g6,g1)
    c: Coincident(g6,g5)
    c: Equal(g-5,g6)
    c: Coincident(g5,g-7)
    c: Coincident(g4,g-7)
    c: Tangent(g7,g-7)
    c: Coincident(g7,g4)
    c: Coincident(g7,g5)
FEATURE [Sketcher::SketchObject] Sketch097
  ArcFitTolerance = 1e-06
  AttachmentSupport = -> [Pad019]
  ExternalGeometry = -> [Binder]
  FullyConstrained = true
  MakeInternals = false
  MapMode = 5
  Placement = pos=(0,2,0) rot=(0,0.707107,0.707107;3.14159rad)
  sketch-geometry (4):
    g0: LineSegment StartX=90 StartY=36.8 StartZ=0 EndX=108 EndY=36.8 EndZ=0
    g1: LineSegment StartX=108 StartY=36.8 StartZ=0 EndX=108 EndY=26.8 EndZ=0
    g2: LineSegment StartX=108 StartY=26.8 StartZ=0 EndX=90 EndY=26.8 EndZ=0
    g3: ArcOfCircle CenterX=94 CenterY=31.8 CenterZ=0 NormalX=0 NormalY=0 NormalZ=1 AngleXU=0 Radius=6.40312 StartAngle=2.24554 EndAngle=4.03765
  constraints (13):
    c: Horizontal(g0)
    c: Coincident(g1,g0)
    c: Vertical(g1)
    c: DistanceX(g0,g0) = 18
    c: DistanceY(g1,g1) = 10
    c: Coincident(g2,g1)
    c: Horizontal(g2)
    c: Equal(g2,g0)
    c: DistanceY(g0,g-3) = 2.4
    c: Coincident(g3,g0)
    c: Coincident(g3,g2)
    c: DistanceX(g2,g3) = 4
    c: DistanceX(g-3,g0) = 90
FEATURE [PartDesign::Chamfer] Chamfer015
  Angle = 45
  Base = -> Pad019 [Edge19,Edge22,Edge79]
  BaseFeature = -> Pad019
  ChamferType = 0
  FlipDirection = false
  Refine = true
  Size = 1.9
  Size2 = 1
  SupportTransform = false
  Suppressed = false
  UseAllEdges = false
FEATURE [PartDesign::Pocket] Pocket002
  BaseFeature = -> Chamfer015
  Direction = (0,1,-2e-16)
  Length = 1.2
  Length2 = 5
  Profile = -> Sketch093
  ReferenceAxis = -> Sketch093 [N_Axis]
  Refine = true
  Suppressed = false
  Type = 0
FEATURE [PartDesign::Pad] Pad005
  BaseFeature = -> Pocket002
  Direction = (0,1,-2e-16)
  Length = 1.6
  Length2 = 10
  Profile = -> Sketch091
  ReferenceAxis = -> Sketch091 [N_Axis]
  Refine = true
  Suppressed = false
  Type = 0
FEATURE [Sketcher::SketchObject] Sketch092  label="Sketch092 - scavi per viti anteriori"
  ArcFitTolerance = 1e-06
  AttachmentSupport = -> [Pad005]
  ExternalGeometry = -> [Binder]
  FullyConstrained = true
  MakeInternals = false
  MapMode = 5
  Placement = pos=(0,3.6,0) rot=(0,0.707107,0.707107;3.14159rad)
  sketch-geometry (20):
    g0: ArcOfCircle CenterX=5.6 CenterY=7.6 CenterZ=0 NormalX=0 NormalY=0 NormalZ=1 AngleXU=0 Radius=3.5 StartAngle=0 EndAngle=1.5708
    g1: ArcOfCircle CenterX=5.6 CenterY=34.8 CenterZ=0 NormalX=0 NormalY=0 NormalZ=1 AngleXU=0 Radius=3.5 StartAngle=4.71239 EndAngle=6.28319
    g2: ArcOfCircle CenterX=78.51 CenterY=34.8 CenterZ=0 NormalX=0 NormalY=0 NormalZ=1 AngleXU=0 Radius=3.5 StartAngle=3.14159 EndAngle=4.71239
    g3: ArcOfCircle CenterX=78.51 CenterY=7.6 CenterZ=0 NormalX=0 NormalY=0 NormalZ=1 AngleXU=0 Radius=3.5 StartAngle=1.5708 EndAngle=3.14159
    g4: LineSegment StartX=0 StartY=3.2 StartZ=0 EndX=0 EndY=11.1 EndZ=0
    g5: LineSegment StartX=0 StartY=11.1 StartZ=0 EndX=5.6 EndY=11.1 EndZ=0
    g6: LineSegment StartX=0 StartY=3.2 StartZ=0 EndX=9.1 EndY=3.2 EndZ=0
    g7: LineSegment StartX=9.1 StartY=3.2 StartZ=0 EndX=9.1 EndY=7.6 EndZ=0
    g8: LineSegment StartX=0 StartY=39.2 StartZ=0 EndX=0 EndY=31.3 EndZ=0
    g9: LineSegment StartX=0 StartY=31.3 StartZ=0 EndX=5.6 EndY=31.3 EndZ=0
    g10: LineSegment StartX=0 StartY=39.2 StartZ=0 EndX=9.1 EndY=39.2 EndZ=0
    g11: LineSegment StartX=9.1 StartY=39.2 StartZ=0 EndX=9.1 EndY=34.8 EndZ=0
    g12: LineSegment StartX=82.8 StartY=39.2 StartZ=0 EndX=75.01 EndY=39.2 EndZ=0
    g13: LineSegment StartX=82.8 StartY=39.2 StartZ=0 EndX=82.8 EndY=31.3 EndZ=0
    g14: LineSegment StartX=82.8 StartY=31.3 StartZ=0 EndX=78.51 EndY=31.3 EndZ=0
    g15: LineSegment StartX=82.8 StartY=3.2 StartZ=0 EndX=75.01 EndY=3.2 EndZ=0
    g16: LineSegment StartX=75.01 StartY=3.2 StartZ=0 EndX=75.01 EndY=7.6 EndZ=0
    g17: LineSegment StartX=82.8 StartY=3.2 StartZ=0 EndX=82.8 EndY=11.1 EndZ=0
    g18: LineSegment StartX=82.8 StartY=11.1 StartZ=0 EndX=78.51 EndY=11.1 EndZ=0
    g19: LineSegment StartX=75.01 StartY=39.2 StartZ=0 EndX=75.01 EndY=34.8 EndZ=0
  constraints (48):
    c: Radius(g0) = 3.5
    c: Coincident(g0,g-10)
    c: Radius(g1) = 3.5
    c: Coincident(g1,g-9)
    c: Radius(g2) = 3.5
    c: Coincident(g2,g-8)
    c: Radius(g3) = 3.5
    c: Coincident(g3,g-7)
    c: Coincident(g4,g-5)
    c: PointOnObject(g4,g-4)
    c: Coincident(g5,g4)
    c: Horizontal(g5)
    c: Coincident(g6,g4)
    c: PointOnObject(g6,g-5)
    c: Coincident(g7,g6)
    c: Vertical(g7)
    c: Coincident(g8,g-4)
    c: PointOnObject(g8,g-4)
    c: Coincident(g9,g8)
    c: Horizontal(g9)
    c: Coincident(g10,g8)
    c: PointOnObject(g10,g-3)
    c: Coincident(g11,g10)
    c: Vertical(g11)
    c: PointOnObject(g12,g-3)
    c: PointOnObject(g12,g-3)
    c: Coincident(g13,g12)
    c: Vertical(g13)
    c: Coincident(g14,g13)
    c: Horizontal(g14)
    c: Coincident(g15,g-6)
    c: PointOnObject(g15,g-5)
    c: Coincident(g16,g15)
    c: Vertical(g16)
    c: Coincident(g17,g15)
    c: Coincident(g18,g17)
    c: Horizontal(g18)
    c: Tangent(g3,g18) = -1.5708
    c: Tangent(g16,g3) = 1.5708
    c: Coincident(g19,g12)
    c: Vertical(g19)
    c: Tangent(g2,g19) = -1.5708
    c: Tangent(g2,g14) = 1.5708
    c: Tangent(g0,g7) = -1.5708
    c: Tangent(g0,g5) = 1.5708
    c: Tangent(g9,g1) = -1.5708
    c: Tangent(g1,g11) = 1.5708
    c: Tangent(g17,g13)
FEATURE [PartDesign::Pocket] Pocket001
  BaseFeature = -> Pad005
  Direction = (0,-1,2e-16)
  Length = 1.6
  Length2 = 5
  Profile = -> Sketch092
  ReferenceAxis = -> Sketch092 [N_Axis]
  Refine = true
  Suppressed = false
  Type = 0
FEATURE [PartDesign::Pad] Pad006
  BaseFeature = -> Pocket001
  Direction = (0,1,-2e-16)
  Length = 0.8
  Length2 = 10
  Profile = -> Sketch094
  ReferenceAxis = -> Sketch094 [N_Axis]
  Refine = true
  Suppressed = false
  Type = 0
FEATURE [PartDesign::Pad] Pad007
  BaseFeature = -> Pad006
  Direction = (0,1,-2e-16)
  Length = 2
  Length2 = 10
  Profile = -> Sketch095
  ReferenceAxis = -> Sketch095 [N_Axis]
  Refine = true
  Suppressed = false
  Type = 0
FEATURE [PartDesign::Pad] Pad008  label="Pad008 - forma impugnatura"
  BaseFeature = -> Pad007
  Direction = (0,1,-2e-16)
  Length = 1.6
  Length2 = 10
  Profile = -> Sketch096
  ReferenceAxis = -> Sketch096 [N_Axis]
  Refine = true
  Suppressed = false
  Type = 0
FEATURE [PartDesign::Pad] Pad009
  BaseFeature = -> Pad008
  Direction = (0,1,-2e-16)
  Length = 1.6
  Length2 = 10
  Profile = -> Sketch097
  ReferenceAxis = -> Sketch097 [N_Axis]
  Refine = true
  Suppressed = false
  Type = 0
FEATURE [Sketcher::SketchObject] Sketch098
  ArcFitTolerance = 1e-06
  AttachmentSupport = -> [Pad006]
  ExternalGeometry = -> [Binder]
  FullyConstrained = true
  MakeInternals = false
  MapMode = 5
  Placement = pos=(0,2.8,-7e-16) rot=(0,0.707107,0.707107;3.14159rad)
  sketch-geometry (4):
    g0: LineSegment StartX=118 StartY=39.2 StartZ=0 EndX=129 EndY=39.2 EndZ=0
    g1: LineSegment StartX=120.599 StartY=31.2 StartZ=0 EndX=131.599 EndY=31.2 EndZ=0
    g2: LineSegment StartX=129 StartY=39.2 StartZ=0 EndX=131.599 EndY=31.2 EndZ=0
    g3: LineSegment StartX=118 StartY=39.2 StartZ=0 EndX=120.599 EndY=31.2 EndZ=0
  constraints (12):
    c: PointOnObject(g0,g-3)
    c: PointOnObject(g0,g-3)
    c: DistanceX(g0,g0) = 11
    c: Horizontal(g1)
    c: Equal(g1,g0)
    c: Coincident(g2,g0)
    c: Coincident(g3,g0)
    c: Parallel(g-4,g2)
    c: Coincident(g1,g2)
    c: Coincident(g1,g3)
    c: DistanceY(g1,g0) = 8
    c: DistanceX(g-3,g0) = 118
FEATURE [Sketcher::SketchObject] Sketch099
  ArcFitTolerance = 1e-06
  AttachmentSupport = -> [Pad008]
  ExternalGeometry = -> [Binder]
  FullyConstrained = true
  MakeInternals = false
  MapMode = 5
  Placement = pos=(0,3.6,0) rot=(0,0.707107,0.707107;3.14159rad)
  sketch-geometry (13):
    g0: LineSegment StartX=192.176 StartY=-3.18451 StartZ=0 EndX=196.804 EndY=-13.1108 EndZ=0
    g1: LineSegment [constr] StartX=202.765 StartY=20.303 StartZ=0 EndX=181.223 EndY=20.303 EndZ=0
    g2: LineSegment [constr] StartX=181.223 StartY=20.303 StartZ=0 EndX=181.223 EndY=-3.18451 EndZ=0
    g3: ArcOfCircle CenterX=181.223 CenterY=-20.3764 CenterZ=0 NormalX=0 NormalY=0 NormalZ=1 AngleXU=0 Radius=17.1918 StartAngle=0.436332 EndAngle=1.57079
    g4: ArcOfEllipse CenterX=181.223 CenterY=8.55923 CenterZ=0 NormalX=0 NormalY=0 NormalZ=1 MajorRadius=23.4779 MinorRadius=11.7437 AngleXU=0 StartAngle=1.5708 EndAngle=4.71239
    g5: LineSegment [constr] StartX=204.701 StartY=8.55923 StartZ=0 EndX=157.745 EndY=8.55923 EndZ=0
    g6: LineSegment [constr] StartX=181.223 StartY=20.303 StartZ=0 EndX=181.223 EndY=-3.18451 EndZ=0
    g7: GeomPoint [constr] X=201.553 Y=8.55923 Z=0
    g8: GeomPoint [constr] X=160.894 Y=8.55923 Z=0
    g9: GeomPoint [constr] X=181.223 Y=-3.18451 Z=0
    g10: LineSegment StartX=181.223 StartY=20.303 StartZ=0 EndX=202.765 EndY=20.303 EndZ=0
    g11: ArcOfCircle CenterX=207.583 CenterY=4 CenterZ=0 NormalX=0 NormalY=0 NormalZ=1 AngleXU=0 Radius=17 StartAngle=1.85815 EndAngle=3.57792
    g12: LineSegment [constr] StartX=172.411 StartY=39.2 StartZ=0 EndX=192.176 EndY=-3.18451 EndZ=0
  constraints (27):
    c: Coincident(g1,g-7)
    c: Horizontal(g1)
    c: Coincident(g2,g1)
    c: Vertical(g2)
    c: Horizontal(g2,g0)
    c: Coincident(g3,g0)
    c: Coincident(g3,g2)
    c: InternalAlignment(g5-g8 -> g4) x4
    c: Horizontal(g5)
    c: PointOnObject(g4,g2)
    c: Coincident(g4,g1)
    c: DistanceX(g-3,g5) = 10.1
    c: Coincident(g4,g2)
    c: Tangent(g3,g-5)
    c: PointOnObject(g9,g4)
    c: PointOnObject(g9,g3)
    c: Tangent(g4,g3,g9) = 1.5708
    c: Coincident(g10,g1)
    c: Coincident(g10,g1)
    c: Equal(g11,g-4)
    c: Coincident(g11,g1)
    c: Coincident(g11,g0)
    c: PointOnObject(g12,g-6)
    c: PointOnObject(g1,g12)
    c: Tangent(g12,g-5) = -1.5708
    c: Tangent(g0,g-5) = -1.5708
    c: Horizontal(g9,g12)
FEATURE [Sketcher::SketchObject] Sketch106  label="Sketch106 - smusso impuniatura interno"
  ArcFitTolerance = 1e-06
  AttachmentSupport = -> [Pad008]
  ExternalGeometry = -> [Pad008]
  FullyConstrained = true
  MakeInternals = false
  MapMode = 5
  Placement = pos=(0,-1.585e-13,-80.4316) rot=(1,0,0;3.14159rad)
  sketch-geometry (9):
    g0: LineSegment StartX=-176.685 StartY=-3.6 StartZ=0 EndX=-176.685 EndY=2.07763e-11 EndZ=0
    g1: LineSegment [constr] StartX=-176.685 StartY=-1.416e-13 StartZ=0 EndX=-176.685 EndY=2.07762e-11 EndZ=0
    g2: LineSegment [constr] StartX=-186.685 StartY=-3.6 StartZ=0 EndX=-186.685 EndY=2.07763e-11 EndZ=0
    g3: ArcOfEllipse CenterX=-186.685 CenterY=2.07762e-11 CenterZ=0 NormalX=0 NormalY=0 NormalZ=1 MajorRadius=10 MinorRadius=3.6 AngleXU=-3.14159 StartAngle=1.5708 EndAngle=3.14159
    g4: LineSegment [constr] StartX=-196.685 StartY=-1.416e-13 StartZ=0 EndX=-176.685 EndY=-1.416e-13 EndZ=0
    g5: LineSegment [constr] StartX=-186.685 StartY=-3.6 StartZ=0 EndX=-186.685 EndY=3.6 EndZ=0
    g6: GeomPoint [constr] X=-196.015 Y=-1.45e-13 Z=0
    g7: GeomPoint [constr] X=-177.356 Y=-1.415e-13 Z=0
    g8: LineSegment StartX=-176.685 StartY=-3.6 StartZ=0 EndX=-186.685 EndY=-3.6 EndZ=0
  constraints (15):
    c: PointOnObject(g2,g-3)
    c: Coincident(g1,g-5)
    c: DistanceY(g1,g1) = 0
    c: Coincident(g0,g1)
    c: DistanceX(g2,g-5) = 10
    c: Vertical(g2)
    c: Horizontal(g2,g0)
    c: InternalAlignment(g4-g7 -> g3) x4
    c: Coincident(g3,g2)
    c: Horizontal(g4)
    c: Coincident(g3,g0)
    c: Tangent(g0,g-5) = 1.5708
    c: Coincident(g3,g2)
    c: Coincident(g8,g0)
    c: Coincident(g8,g2)
FEATURE [Sketcher::SketchObject] Sketch107  label="Sketch107 - smusso impugnatura esterno"
  ArcFitTolerance = 1e-06
  AttachmentSupport = -> [Pad008]
  ExternalGeometry = -> [Pad008]
  FullyConstrained = true
  MakeInternals = false
  MapMode = 5
  Placement = pos=(0,-1.585e-13,-80.4316) rot=(1,0,0;3.14159rad)
  sketch-geometry (9):
    g0: LineSegment [constr] StartX=-215.932 StartY=-1.416e-13 StartZ=0 EndX=-215.932 EndY=-5.3e-14 EndZ=0
    g1: LineSegment StartX=-215.932 StartY=-3.6 StartZ=0 EndX=-215.932 EndY=-5.28e-14 EndZ=0
    g2: LineSegment StartX=-215.932 StartY=-3.6 StartZ=0 EndX=-205.932 EndY=-3.6 EndZ=0
    g3: LineSegment [constr] StartX=-205.932 StartY=-3.6 StartZ=0 EndX=-205.932 EndY=-5.28e-14 EndZ=0
    g4: ArcOfEllipse CenterX=-205.932 CenterY=-5.3e-14 CenterZ=0 NormalX=0 NormalY=0 NormalZ=1 MajorRadius=10 MinorRadius=3.6 AngleXU=-3.14159 StartAngle=-2.66e-14 EndAngle=1.5708
    g5: LineSegment [constr] StartX=-215.932 StartY=-1.416e-13 StartZ=0 EndX=-195.932 EndY=-1.416e-13 EndZ=0
    g6: LineSegment [constr] StartX=-205.932 StartY=-3.6 StartZ=0 EndX=-205.932 EndY=3.6 EndZ=0
    g7: GeomPoint [constr] X=-215.262 Y=-1.425e-13 Z=0
    g8: GeomPoint [constr] X=-196.602 Y=-1.551e-13 Z=0
  constraints (16):
    c: Coincident(g0,g-6)
    c: PointOnObject(g0,g-6)
    c: DistanceY(g0,g0) = 0
    c: Coincident(g1,g-6)
    c: Coincident(g1,g0)
    c: Tangent(g2,g-3)
    c: DistanceX(g2,g2) = 10
    c: Coincident(g3,g2)
    c: Vertical(g3)
    c: Horizontal(g3,g0)
    c: InternalAlignment(g5-g8 -> g4) x4
    c: Coincident(g4,g3)
    c: Horizontal(g5)
    c: Coincident(g4,g0)
    c: Coincident(g4,g2)
    c: PointOnObject(g2,g1)
FEATURE [Sketcher::SketchObject] Sketch108
  ArcFitTolerance = 1e-06
  AttachmentOffset = pos=(0,0,-1.6) rot=(0,0,1;0rad)
  AttachmentSupport = -> [Pad008]
  ExternalGeometry = -> [Binder]
  FullyConstrained = true
  MakeInternals = false
  MapMode = 5
  Placement = pos=(0,2,4e-16) rot=(0,0.707107,0.707107;3.14159rad)
  sketch-geometry (14):
    g0: LineSegment StartX=192.176 StartY=-3.18451 StartZ=0 EndX=193.827 EndY=-6.72678 EndZ=0
    g1: LineSegment [constr] StartX=202.765 StartY=20.303 StartZ=0 EndX=181.223 EndY=20.303 EndZ=0
    g2: LineSegment [constr] StartX=181.223 StartY=20.303 StartZ=0 EndX=181.223 EndY=1.30297 EndZ=0
    g3: ArcOfCircle CenterX=181.223 CenterY=-12.6042 CenterZ=0 NormalX=0 NormalY=0 NormalZ=1 AngleXU=0 Radius=13.9072 StartAngle=0.436332 EndAngle=1.5708
    g4: ArcOfEllipse CenterX=181.223 CenterY=10.803 CenterZ=0 NormalX=0 NormalY=0 NormalZ=1 MajorRadius=14.4779 MinorRadius=9.5 AngleXU=0 StartAngle=1.5708 EndAngle=4.71239
    g5: LineSegment [constr] StartX=195.701 StartY=10.803 StartZ=0 EndX=166.745 EndY=10.803 EndZ=0
    g6: LineSegment [constr] StartX=181.223 StartY=20.303 StartZ=0 EndX=181.223 EndY=1.30297 EndZ=0
    g7: GeomPoint [constr] X=192.148 Y=10.803 Z=0
    g8: GeomPoint [constr] X=170.298 Y=10.803 Z=0
    g9: LineSegment StartX=181.223 StartY=20.303 StartZ=0 EndX=202.765 EndY=20.303 EndZ=0
    g10: ArcOfCircle CenterX=207.583 CenterY=4 CenterZ=0 NormalX=0 NormalY=0 NormalZ=1 AngleXU=0 Radius=17 StartAngle=1.85815 EndAngle=3.57792
    g11: LineSegment [constr] StartX=172.411 StartY=39.2 StartZ=0 EndX=192.176 EndY=-3.18451 EndZ=0
    g12: GeomPoint [constr] X=181.223 Y=1.30297 Z=0
    g13: GeomPoint [constr] X=181.223 Y=1.30297 Z=0
  constraints (28):
    c: Coincident(g1,g-7)
    c: Horizontal(g1)
    c: Coincident(g2,g1)
    c: Vertical(g2)
    c: Coincident(g3,g2)
    c: InternalAlignment(g5-g8 -> g4) x4
    c: Horizontal(g5)
    c: PointOnObject(g4,g2)
    c: Coincident(g4,g1)
    c: DistanceX(g-3,g5) = 19.1
    c: Coincident(g4,g2)
    c: Coincident(g9,g1)
    c: Coincident(g9,g1)
    c: Coincident(g10,g1)
    c: Coincident(g10,g0)
    c: PointOnObject(g11,g-6)
    c: PointOnObject(g1,g11)
    c: DistanceY(g2,g1) = 19
    c: Coincident(g10,g-4)
    c: PointOnObject(g12,g4)
    c: PointOnObject(g12,g3)
    c: Tangent(g11,g-5) = -1.5708
    c: Tangent(g0,g-5) = -1.5708
    c: Tangent(g3,g0) = 1.5708
    c: PointOnObject(g13,g4)
    c: PointOnObject(g13,g3)
    c: Tangent(g4,g3,g13) = 1.5708
    c: Horizontal(g11,g0)
FEATURE [Part::Part2DObjectPython] Clone2D  label="Sketch108 (2D)"  # Draft 2D object (typed FeaturePython)
  Fuse = false
  Objects = -> [Sketch108]
  Placement = pos=(0,2,4e-16) rot=(0,0.707107,0.707107;3.14159rad)
  Scale = (1,1,1)
FEATURE [Sketcher::SketchObject] Sketch109
  ArcFitTolerance = 1e-06
  AttachmentOffset = pos=(0,0,-3.5) rot=(0,0,1;0rad)
  AttachmentSupport = -> [Pad008]
  ExternalGeometry = -> [Binder]
  FullyConstrained = true
  MakeInternals = false
  MapMode = 5
  Placement = pos=(0,0.1,8e-16) rot=(0,0.707107,0.707107;3.14159rad)
  sketch-geometry (1):
    g0: GeomPoint X=197.47 Y=8.55923 Z=0
  constraints (1):
    c: Symmetric(g-7,g-5,g0)
FEATURE [PartDesign::Chamfer] Chamfer005
  Angle = 45
  Base = -> Pad009 [Edge215,Edge212]
  BaseFeature = -> Pad009
  ChamferType = 1
  FlipDirection = false
  Refine = true
  Size = 1.5
  Size2 = 2.8
  SupportTransform = false
  Suppressed = false
  UseAllEdges = false
FEATURE [Sketcher::SketchObject] Sketch111
  ArcFitTolerance = 1e-06
  AttachmentSupport = -> [Pad009]
  ExternalGeometry = -> [Pad009]
  FullyConstrained = true
  MakeInternals = false
  MapMode = 5
  Placement = pos=(0,3.6,-8e-16) rot=(0,0.707107,0.707107;3.14159rad)
  sketch-geometry (21):
    g0: LineSegment [constr] StartX=97 StartY=36.8 StartZ=0 EndX=97 EndY=26.8 EndZ=0
    g1: LineSegment StartX=97 StartY=28.6 StartZ=0 EndX=97 EndY=27.8 EndZ=0
    g2: LineSegment StartX=97 StartY=27.8 StartZ=0 EndX=108 EndY=27.8 EndZ=0
    g3: LineSegment StartX=108 StartY=27.8 StartZ=0 EndX=108 EndY=28.6 EndZ=0
    g4: LineSegment StartX=108 StartY=28.6 StartZ=0 EndX=97 EndY=28.6 EndZ=0
    g5: LineSegment StartX=97 StartY=35.8 StartZ=0 EndX=97 EndY=35 EndZ=0
    g6: LineSegment StartX=97 StartY=35 StartZ=0 EndX=108 EndY=35 EndZ=0
    g7: LineSegment StartX=108 StartY=35 StartZ=0 EndX=108 EndY=35.8 EndZ=0
    g8: LineSegment StartX=108 StartY=35.8 StartZ=0 EndX=97 EndY=35.8 EndZ=0
    g9: LineSegment StartX=97 StartY=30.4 StartZ=0 EndX=97 EndY=29.6 EndZ=0
    g10: LineSegment StartX=97 StartY=29.6 StartZ=0 EndX=108 EndY=29.6 EndZ=0
    g11: LineSegment StartX=108 StartY=29.6 StartZ=0 EndX=108 EndY=30.4 EndZ=0
    g12: LineSegment StartX=108 StartY=30.4 StartZ=0 EndX=97 EndY=30.4 EndZ=0
    g13: LineSegment StartX=97 StartY=34 StartZ=0 EndX=97 EndY=33.2 EndZ=0
    g14: LineSegment StartX=97 StartY=33.2 StartZ=0 EndX=108 EndY=33.2 EndZ=0
    g15: LineSegment StartX=108 StartY=33.2 StartZ=0 EndX=108 EndY=34 EndZ=0
    g16: LineSegment StartX=108 StartY=34 StartZ=0 EndX=97 EndY=34 EndZ=0
    g17: LineSegment StartX=97 StartY=32.2 StartZ=0 EndX=97 EndY=31.4 EndZ=0
    g18: LineSegment StartX=97 StartY=31.4 StartZ=0 EndX=108 EndY=31.4 EndZ=0
    g19: LineSegment StartX=108 StartY=31.4 StartZ=0 EndX=108 EndY=32.2 EndZ=0
    g20: LineSegment StartX=108 StartY=32.2 StartZ=0 EndX=97 EndY=32.2 EndZ=0
  constraints (54):
    c: Vertical(g0)
    c: PointOnObject(g0,g-3)
    c: PointOnObject(g0,g-4)
    c: DistanceX(g0,g-5) = 11
    c: Coincident(g1,g2)
    c: Coincident(g2,g3)
    c: Coincident(g3,g4)
    c: Coincident(g4,g1)
    c: Horizontal(g2)
    c: Horizontal(g4)
    c: Tangent(g1,g0)
    c: Tangent(g3,g-5)
    c: DistanceY(g2,g3) = 0.8
    c: Coincident(g5,g6)
    c: Coincident(g6,g7)
    c: Coincident(g7,g8)
    c: Coincident(g8,g5)
    c: Horizontal(g6)
    c: Horizontal(g8)
    c: DistanceY(g6,g7) = 0.8
    c: Coincident(g9,g10)
    c: Coincident(g10,g11)
    c: Coincident(g11,g12)
    c: Coincident(g12,g9)
    c: Horizontal(g10)
    c: Horizontal(g12)
    c: DistanceY(g10,g11) = 0.8
    c: Tangent(g5,g0)
    c: Tangent(g7,g-5)
    c: Tangent(g9,g0)
    c: Tangent(g11,g-5)
    c: Coincident(g13,g14)
    c: Coincident(g14,g15)
    c: Coincident(g15,g16)
    c: Coincident(g16,g13)
    c: Horizontal(g14)
    c: Horizontal(g16)
    c: DistanceY(g14,g15) = 0.8
    c: Tangent(g13,g0)
    c: Tangent(g15,g-5)
    c: Coincident(g17,g18)
    c: Coincident(g18,g19)
    c: Coincident(g19,g20)
    c: Coincident(g20,g17)
    c: Horizontal(g18)
    c: Horizontal(g20)
    c: DistanceY(g18,g19) = 0.8
    c: Tangent(g17,g0)
    c: Tangent(g19,g-5)
    c: DistanceY(g1,g9) = 1
    c: DistanceY(g9,g17) = 1
    c: DistanceY(g17,g13) = 1
    c: DistanceY(g13,g5) = 1
    c: DistanceY(g0,g1) = 1
FEATURE [PartDesign::Pocket] Pocket004
  BaseFeature = -> Chamfer005
  Direction = (0,-1,2e-16)
  Length = 1
  Length2 = 5
  Profile = -> Sketch111
  ReferenceAxis = -> Sketch111 [N_Axis]
  Refine = true
  Suppressed = false
  Type = 0
FEATURE [PartDesign::Pad] Pad010
  BaseFeature = -> Pocket004
  Direction = (0,1,-2e-16)
  Length = 1.2
  Length2 = 10
  Profile = -> Sketch098
  ReferenceAxis = -> Sketch098 [N_Axis]
  Refine = true
  Suppressed = false
  Type = 0
FEATURE [PartDesign::Chamfer] Chamfer006
  Angle = 45
  Base = -> Pad010 [Edge291]
  BaseFeature = -> Pad010
  ChamferType = 1
  FlipDirection = false
  Refine = true
  Size = 1
  Size2 = 6
  SupportTransform = false
  Suppressed = false
  UseAllEdges = false
FEATURE [Sketcher::SketchObject] Sketch110
  ArcFitTolerance = 1e-06
  AttachmentSupport = -> [Pad010]
  ExternalGeometry = -> [Sketch098]
  FullyConstrained = true
  MakeInternals = false
  MapMode = 5
  Placement = pos=(0,4,-9e-16) rot=(0,0.707107,0.707107;3.14159rad)
  sketch-geometry (8):
    g0: LineSegment StartX=119.69 StartY=34 StartZ=0 EndX=130.69 EndY=34 EndZ=0
    g1: LineSegment StartX=119.95 StartY=33.2 StartZ=0 EndX=130.95 EndY=33.2 EndZ=0
    g2: LineSegment StartX=119.137 StartY=35.7 StartZ=0 EndX=130.137 EndY=35.7 EndZ=0
    g3: LineSegment StartX=118.877 StartY=36.5 StartZ=0 EndX=129.877 EndY=36.5 EndZ=0
    g4: LineSegment StartX=118.877 StartY=36.5 StartZ=0 EndX=119.137 EndY=35.7 EndZ=0
    g5: LineSegment StartX=129.877 StartY=36.5 StartZ=0 EndX=130.137 EndY=35.7 EndZ=0
    g6: LineSegment StartX=119.69 StartY=34 StartZ=0 EndX=119.95 EndY=33.2 EndZ=0
    g7: LineSegment StartX=130.69 StartY=34 StartZ=0 EndX=130.95 EndY=33.2 EndZ=0
  constraints (24):
    c: Horizontal(g0)
    c: Horizontal(g1)
    c: Horizontal(g2)
    c: Horizontal(g3)
    c: Equal(g1,g-5)
    c: Equal(g0,g-5)
    c: Equal(g2,g-5)
    c: Equal(g3,g-5)
    c: PointOnObject(g0,g-3)
    c: PointOnObject(g1,g-3)
    c: PointOnObject(g2,g-3)
    c: PointOnObject(g3,g-3)
    c: Coincident(g4,g3)
    c: Coincident(g4,g2)
    c: Coincident(g5,g3)
    c: Coincident(g5,g2)
    c: Coincident(g6,g0)
    c: Coincident(g6,g1)
    c: Coincident(g7,g0)
    c: Coincident(g7,g1)
    c: DistanceY(g1,g0) = 0.8
    c: DistanceY(g2,g3) = 0.8
    c: DistanceY(g-5,g1) = 2
    c: DistanceY(g-5,g2) = 4.5
FEATURE [PartDesign::Pocket] Pocket003
  BaseFeature = -> Chamfer006
  Direction = (0,-1,2e-16)
  Length = 1
  Length2 = 5
  Profile = -> Sketch110
  ReferenceAxis = -> Sketch110 [N_Axis]
  Refine = true
  Suppressed = false
  Type = 0
FEATURE [PartDesign::SubtractivePipe] SubtractivePipe
  AuxilleryCurvelinear = true
  AuxillerySpineTangent = false
  BaseFeature = -> Pocket003
  Binormal = (0,0,0)
  Mode = 0
  Profile = -> Sketch106
  Refine = true
  Spine = -> Pad008 [Edge215]
  SpineTangent = false
  Suppressed = false
  Transformation = 0
  Transition = 0
FEATURE [PartDesign::SubtractivePipe] SubtractivePipe001
  AuxilleryCurvelinear = true
  AuxillerySpineTangent = false
  BaseFeature = -> SubtractivePipe
  Binormal = (0,0,0)
  Mode = 0
  Profile = -> Sketch107
  Refine = true
  Spine = -> Pad008 [Edge213,Edge216,Edge210]
  SpineTangent = false
  Suppressed = false
  Transformation = 0
  Transition = 0
FEATURE [PartDesign::SubtractiveLoft] SubtractiveLoft
  BaseFeature = -> SubtractivePipe001
  Closed = false
  Profile = -> Sketch099
  Refine = true
  Ruled = false
  Sections = -> [Sketch108]
  Suppressed = false
FEATURE [PartDesign::SubtractiveLoft] SubtractiveLoft001
  BaseFeature = -> SubtractiveLoft
  Closed = false
  Profile = -> Clone2D
  Refine = true
  Ruled = false
  Sections = -> [Sketch109]
  Suppressed = false
FEATURE [Sketcher::SketchObject] Sketch112
  ArcFitTolerance = 1e-06
  AttachmentSupport = -> [Pad008]
  ExternalGeometry = -> [Binder]
  FullyConstrained = true
  MakeInternals = false
  MapMode = 5
  Placement = pos=(0,3.6,0) rot=(0,0.707107,0.707107;3.14159rad)
  sketch-geometry (4):
    g0: LineSegment [constr] StartX=167.782 StartY=-53.0314 StartZ=0 EndX=215.42 EndY=-53.0314 EndZ=0
    g1: GeomPoint [constr] X=191.282 Y=-53.0314 Z=0
    g2: Circle CenterX=191.282 CenterY=-53.0314 CenterZ=0 NormalX=0 NormalY=0 NormalZ=1 AngleXU=0 Radius=11.5
    g3: Circle CenterX=191.282 CenterY=-53.0314 CenterZ=0 NormalX=0 NormalY=0 NormalZ=1 AngleXU=0 Radius=10.7
  constraints (9):
    c: Horizontal(g0)
    c: PointOnObject(g0,g-3)
    c: Diameter(g2) = 23
    c: Coincident(g2,g1)
    c: Diameter(g3) = 21.4
    c: Coincident(g3,g1)
    c: DistanceX(g0,g1) = 23.5
    c: PointOnObject(g1,g0)
    c: Coincident(g0,g-4)
FEATURE [PartDesign::Chamfer] Chamfer016
  Angle = 45
  Base = -> SubtractiveLoft001 [Edge118,Edge117,Edge119,Edge120,Edge109]
  BaseFeature = -> SubtractiveLoft001
  ChamferType = 0
  FlipDirection = false
  Refine = true
  Size = 1.5
  Size2 = 1
  SupportTransform = false
  Suppressed = false
  UseAllEdges = false
FEATURE [PartDesign::Chamfer] Chamfer017
  Angle = 45
  Base = -> Chamfer016 [Edge15]
  BaseFeature = -> Chamfer016
  ChamferType = 0
  FlipDirection = false
  Refine = true
  Size = 1.6
  Size2 = 1
  SupportTransform = false
  Suppressed = false
  UseAllEdges = false
FEATURE [PartDesign::Chamfer] Chamfer018
  Angle = 45
  Base = -> Chamfer017 [Edge10]
  BaseFeature = -> Chamfer017
  ChamferType = 0
  FlipDirection = false
  Refine = true
  Size = 3.5
  Size2 = 1
  SupportTransform = false
  Suppressed = false
  UseAllEdges = false
FEATURE [PartDesign::Chamfer] Chamfer019
  Angle = 45
  Base = -> Chamfer018 [Edge94]
  BaseFeature = -> Chamfer018
  ChamferType = 0
  FlipDirection = false
  Refine = true
  Size = 1.9
  Size2 = 1
  SupportTransform = false
  Suppressed = false
  UseAllEdges = false
FEATURE [PartDesign::Fillet] Fillet009
  Base = -> Chamfer019 [Edge83]
  BaseFeature = -> Chamfer019
  Radius = 1.1
  Refine = true
  SupportTransform = false
  Suppressed = false
  UseAllEdges = false
FEATURE [PartDesign::Fillet] Fillet010
  Base = -> Fillet009 [Edge76]
  BaseFeature = -> Fillet009
  Radius = 1.9
  Refine = true
  SupportTransform = false
  Suppressed = false
  UseAllEdges = false
FEATURE [PartDesign::Pocket] Pocket005
  BaseFeature = -> Fillet010
  Direction = (0,-1,2e-16)
  Length = 0.8
  Length2 = 5
  Profile = -> Sketch112
  ReferenceAxis = -> Sketch112 [N_Axis]
  Refine = true
  Suppressed = false
  Type = 0
FEATURE [Part::Part2DObjectPython] ShapeString001  # Draft 2D object (typed FeaturePython)
  FontFile = <path>
  Fuse = false
  Justification = 6
  JustificationReference = 0
  KeepLeftMargin = false
  MakeFace = true
  ObliqueAngle = 0
  Placement = pos=(-183.5,3.6,-57.5) rot=(0,0.707107,0.707107;3.14159rad)
  ScaleToSize = true
  Size = 10
  String = AS
  Tracking = 0
FEATURE [PartDesign::Pocket] Pocket013
  BaseFeature = -> Pocket005
  Direction = (-1e-16,-1,2e-16)
  Length = 1
  Length2 = 5
  Profile = -> ShapeString001
  ReferenceAxis = -> ShapeString001 [N_Axis]
  Refine = true
  Suppressed = false
  Type = 0
FEATURE [PartDesign::Pad] Pad020
  Direction = (0,-1,2e-16)
  Length = 25.2
  Length2 = 10
  Midplane = true
  Placement = pos=(0,0,0) rot=(1,0,0;1.5708rad)
  Profile = -> Sketch021
  ReferenceAxis = -> Sketch021 [N_Axis]
  Refine = true
  Suppressed = false
  Type = 0
FEATURE [PartDesign::Body] Body001  label="perno fermo rumble e driver solenoide"
  AllowCompound = false
  Group = -> [Sketch021,Pad020]
  Origin = -> Origin001
  Tip = -> Pad020
FEATURE [PartDesign::Pad] Pad021
  Direction = (0,-1,2e-16)
  Length = 16.8
  Length2 = 10
  Midplane = true
  Placement = pos=(0,0,0) rot=(1,0,0;1.5708rad)
  Profile = -> Sketch061
  ReferenceAxis = -> Sketch061 [N_Axis]
  Refine = true
  Suppressed = false
  Type = 0
FEATURE [PartDesign::Pocket] Pocket014
  BaseFeature = -> Pad021
  Direction = (0,1,-2e-16)
  Length = 12.8
  Length2 = 5
  Midplane = true
  Placement = pos=(0,0,0) rot=(1,0,0;1.5708rad)
  Profile = -> Sketch062
  ReferenceAxis = -> Sketch062 [N_Axis]
  Refine = true
  Suppressed = false
  Type = 0
FEATURE [PartDesign::Pad] Pad022
  BaseFeature = -> Pocket014
  Direction = (0,-1,2e-16)
  Length = 7.6
  Length2 = 10
  Midplane = true
  Placement = pos=(0,0,0) rot=(1,0,0;1.5708rad)
  Profile = -> Sketch063
  ReferenceAxis = -> Sketch063 [N_Axis]
  Refine = true
  Suppressed = false
  Type = 0
FEATURE [PartDesign::Body] Body003  label="blocco switch"
  AllowCompound = false
  Group = -> [Sketch061,Sketch062,Sketch063,Pad021,Pocket014,Pad022]
  Origin = -> Origin003
  Tip = -> Pad022
FEATURE [PartDesign::Pad] Pad024
  Direction = (0,-1,2e-16)
  Length = 17
  Length2 = 10
  Midplane = true
  Placement = pos=(0,0,0) rot=(1,0,0;1.5708rad)
  Profile = -> Sketch045
  ReferenceAxis = -> Sketch045 [N_Axis]
  Refine = true
  Suppressed = false
  Type = 0
FEATURE [PartDesign::Pocket] Pocket015
  BaseFeature = -> Pad024
  Direction = (-1,0,0)
  Length = 8
  Length2 = 5
  Placement = pos=(0,0,0) rot=(1,0,0;1.5708rad)
  Profile = -> Sketch047
  ReferenceAxis = -> Sketch047 [N_Axis]
  Refine = true
  Reversed = true
  Suppressed = false
  Type = 0
FEATURE [PartDesign::Pocket] Pocket016
  BaseFeature = -> Pocket015
  Direction = (-1,0,0)
  Length = 1
  Length2 = 5
  Placement = pos=(0,0,0) rot=(1,0,0;1.5708rad)
  Profile = -> Sketch046
  ReferenceAxis = -> Sketch046 [N_Axis]
  Refine = true
  Reversed = true
  Suppressed = false
  Type = 0
FEATURE [PartDesign::Pocket] Pocket017
  BaseFeature = -> Pocket016
  Direction = (0,1,-2e-16)
  Length = 17
  Length2 = 5
  Midplane = true
  Placement = pos=(0,0,0) rot=(1,0,0;1.5708rad)
  Profile = -> Sketch048
  ReferenceAxis = -> Sketch048 [N_Axis]
  Refine = true
  Suppressed = false
  Type = 0
FEATURE [PartDesign::Pad] Pad025
  BaseFeature = -> Pocket017
  Direction = (0,-1,2e-16)
  Length = 17
  Length2 = 10
  Midplane = true
  Placement = pos=(0,0,0) rot=(1,0,0;1.5708rad)
  Profile = -> Sketch049
  ReferenceAxis = -> Sketch049 [N_Axis]
  Refine = true
  Suppressed = false
  Type = 0
FEATURE [PartDesign::Pad] Pad026
  BaseFeature = -> Pad025
  Direction = (0,-1,2e-16)
  Length = 17
  Length2 = 10
  Midplane = true
  Placement = pos=(0,0,0) rot=(1,0,0;1.5708rad)
  Profile = -> Sketch066
  ReferenceAxis = -> Sketch066 [N_Axis]
  Refine = true
  Suppressed = false
  Type = 0
FEATURE [PartDesign::Pad] Pad027
  BaseFeature = -> Pad026
  Direction = (0,-1,2e-16)
  Length = 5
  Length2 = 10
  Midplane = true
  Placement = pos=(0,0,0) rot=(1,0,0;1.5708rad)
  Profile = -> Sketch064
  ReferenceAxis = -> Sketch064 [N_Axis]
  Refine = true
  Suppressed = false
  Type = 0
FEATURE [PartDesign::Pad] Pad028
  BaseFeature = -> Pad027
  Direction = (1,0,0)
  Length = 1
  Length2 = 10
  Placement = pos=(0,0,0) rot=(1,0,0;1.5708rad)
  Profile = -> Sketch068
  ReferenceAxis = -> Sketch068 [N_Axis]
  Refine = true
  Reversed = true
  Suppressed = false
  Type = 0
FEATURE [PartDesign::Chamfer] Chamfer020
  Angle = 45
  Base = -> Pad028 [Edge73,Edge75,Edge78,Edge77]
  BaseFeature = -> Pad028
  ChamferType = 0
  FlipDirection = false
  Placement = pos=(0,0,0) rot=(1,0,0;1.5708rad)
  Refine = true
  Size = 0.5
  Size2 = 1
  SupportTransform = false
  Suppressed = false
  UseAllEdges = false
FEATURE [PartDesign::Body] Body002  label="supporto per neopixel"
  AllowCompound = false
  Group = -> [Sketch045,Sketch047,Sketch046,Sketch048,Sketch049,Sketch066,Sketch064,Sketch068,Pad024,Pocket015,Pocket016,Pocket017,Pad025,Pad026,Pad027,Pad028,Chamfer020]
  Origin = -> Origin002
  Tip = -> Chamfer020
FEATURE [Sketcher::SketchObject] Sketch134  label="perno fermo rumble002"
  ArcFitTolerance = 1e-06
  AttachmentSupport = -> [XZ_Plane008]
  FullyConstrained = true
  MakeInternals = false
  MapMode = 5
  Placement = pos=(0,0,0) rot=(1,0,0;1.5708rad)
  sketch-geometry (16):
    g0: LineSegment StartX=0 StartY=0.45 StartZ=0 EndX=0 EndY=1.55 EndZ=0
    g1: LineSegment StartX=0.45 StartY=2 StartZ=0 EndX=1.55 EndY=2 EndZ=0
    g2: LineSegment StartX=2 StartY=1.55 StartZ=0 EndX=2 EndY=0.45 EndZ=0
    g3: LineSegment StartX=1.55 StartY=0 StartZ=0 EndX=0.45 EndY=0 EndZ=0
    g4: ArcOfCircle [constr] CenterX=0.45 CenterY=1.55 CenterZ=0 NormalX=0 NormalY=0 NormalZ=1 AngleXU=0 Radius=0.45 StartAngle=1.5708 EndAngle=3.14159
    g5: GeomPoint [constr] X=0 Y=2 Z=0
    g6: LineSegment StartX=0.45 StartY=2 StartZ=0 EndX=0 EndY=1.55 EndZ=0
    g7: ArcOfCircle [constr] CenterX=1.55 CenterY=1.55 CenterZ=0 NormalX=0 NormalY=0 NormalZ=1 AngleXU=0 Radius=0.45 StartAngle=0 EndAngle=1.5708
    g8: GeomPoint [constr] X=2 Y=2 Z=0
    g9: LineSegment StartX=2 StartY=1.55 StartZ=0 EndX=1.55 EndY=2 EndZ=0
    g10: ArcOfCircle [constr] CenterX=1.55 CenterY=0.45 CenterZ=0 NormalX=0 NormalY=0 NormalZ=1 AngleXU=0 Radius=0.45 StartAngle=4.71239 EndAngle=6.28319
    g11: GeomPoint [constr] X=2 Y=0 Z=0
    g12: LineSegment StartX=1.55 StartY=0 StartZ=0 EndX=2 EndY=0.45 EndZ=0
    g13: ArcOfCircle [constr] CenterX=0.45 CenterY=0.45 CenterZ=0 NormalX=0 NormalY=0 NormalZ=1 AngleXU=0 Radius=0.45 StartAngle=3.14159 EndAngle=4.71239
    g14: GeomPoint [constr] X=0 Y=0 Z=0
    g15: LineSegment StartX=0 StartY=0.45 StartZ=0 EndX=0.45 EndY=0 EndZ=0
  constraints (35):
    c: Coincident(g14,g-1)
    c: PointOnObject(g5,g-2)
    c: Horizontal(g1)
    c: Vertical(g2)
    c: Horizontal(g3)
    c: DistanceX(g5,g8) = 2
    c: DistanceY(g11,g8) = 2
    c: PointOnObject(g5,g0)
    c: PointOnObject(g5,g1)
    c: Tangent(g0,g4) = 1.5708
    c: Tangent(g1,g4) = 1.5708
    c: Coincident(g6,g0)
    c: Coincident(g6,g1)
    c: PointOnObject(g8,g2)
    c: PointOnObject(g8,g1)
    c: Tangent(g2,g7) = 1.5708
    c: Tangent(g1,g7) = 1.5708
    c: Coincident(g9,g2)
    c: Coincident(g9,g1)
    c: PointOnObject(g11,g2)
    c: PointOnObject(g11,g3)
    c: Tangent(g2,g10) = 1.5708
    c: Tangent(g3,g10) = 1.5708
    c: Coincident(g12,g2)
    c: Coincident(g12,g3)
    c: PointOnObject(g14,g0)
    c: PointOnObject(g14,g3)
    c: Tangent(g0,g13) = 1.5708
    c: Tangent(g3,g13) = 1.5708
    c: Coincident(g15,g0)
    c: Coincident(g15,g3)
    c: Equal(g6,g9)
    c: Equal(g9,g12)
    c: Equal(g12,g15)
    c: DistanceX(g14,g3) = 0.45
FEATURE [PartDesign::Pad] Pad029
  Direction = (0,-1,2e-16)
  Length = 17
  Length2 = 10
  Midplane = true
  Placement = pos=(0,0,0) rot=(1,0,0;1.5708rad)
  Profile = -> Sketch134
  ReferenceAxis = -> Sketch134 [N_Axis]
  Refine = true
  Suppressed = false
  Type = 0
FEATURE [PartDesign::Body] Body008  label="perno fermo neopixel"
  AllowCompound = false
  Group = -> [Sketch134,Pad029]
  Origin = -> Origin008
  Tip = -> Pad029
FEATURE [Sketcher::SketchObject] Sketch135  label="perno fermo rumble003"
  ArcFitTolerance = 1e-06
  AttachmentSupport = -> [XZ_Plane009]
  FullyConstrained = true
  MakeInternals = false
  MapMode = 5
  Placement = pos=(0,0,0) rot=(1,0,0;1.5708rad)
  sketch-geometry (16):
    g0: LineSegment StartX=4.69e-14 StartY=0.8 StartZ=0 EndX=-3.04e-14 EndY=3.1 EndZ=0
    g1: LineSegment StartX=0.8 StartY=3.9 StartZ=0 EndX=3.1 EndY=3.9 EndZ=0
    g2: LineSegment StartX=3.9 StartY=3.1 StartZ=0 EndX=3.9 EndY=0.8 EndZ=0
    g3: LineSegment StartX=3.1 StartY=0 StartZ=0 EndX=0.8 EndY=0 EndZ=0
    g4: ArcOfCircle [constr] CenterX=0.8 CenterY=3.1 CenterZ=0 NormalX=0 NormalY=0 NormalZ=1 AngleXU=0 Radius=0.8 StartAngle=1.5708 EndAngle=3.14159
    g5: GeomPoint [constr] X=0 Y=3.9 Z=0
    g6: LineSegment StartX=0.8 StartY=3.9 StartZ=0 EndX=-3.04e-14 EndY=3.1 EndZ=0
    g7: ArcOfCircle [constr] CenterX=3.1 CenterY=3.1 CenterZ=0 NormalX=0 NormalY=0 NormalZ=1 AngleXU=0 Radius=0.8 StartAngle=-2.4e-14 EndAngle=1.5708
    g8: GeomPoint [constr] X=3.9 Y=3.9 Z=0
    g9: LineSegment StartX=3.9 StartY=3.1 StartZ=0 EndX=3.1 EndY=3.9 EndZ=0
    g10: ArcOfCircle [constr] CenterX=3.1 CenterY=0.8 CenterZ=0 NormalX=0 NormalY=0 NormalZ=1 AngleXU=0 Radius=0.8 StartAngle=4.71239 EndAngle=6.28319
    g11: GeomPoint [constr] X=3.9 Y=0 Z=0
    g12: LineSegment StartX=3.1 StartY=0 StartZ=0 EndX=3.9 EndY=0.8 EndZ=0
    g13: ArcOfCircle [constr] CenterX=0.8 CenterY=0.8 CenterZ=0 NormalX=0 NormalY=0 NormalZ=1 AngleXU=0 Radius=0.8 StartAngle=3.14159 EndAngle=4.71239
    g14: GeomPoint [constr] X=0 Y=0 Z=0
    g15: LineSegment StartX=4.69e-14 StartY=0.8 StartZ=0 EndX=0.8 EndY=0 EndZ=0
  constraints (35):
    c: Coincident(g14,g-1)
    c: PointOnObject(g5,g-2)
    c: Horizontal(g1)
    c: Vertical(g2)
    c: Horizontal(g3)
    c: DistanceX(g5,g8) = 3.9
    c: DistanceY(g11,g8) = 3.9
    c: PointOnObject(g5,g0)
    c: PointOnObject(g5,g1)
    c: Tangent(g0,g4) = 1.5708
    c: Tangent(g1,g4) = 1.5708
    c: Coincident(g6,g0)
    c: Coincident(g6,g1)
    c: PointOnObject(g8,g2)
    c: PointOnObject(g8,g1)
    c: Tangent(g2,g7) = 1.5708
    c: Tangent(g1,g7) = 1.5708
    c: Coincident(g9,g2)
    c: Coincident(g9,g1)
    c: PointOnObject(g11,g2)
    c: PointOnObject(g11,g3)
    c: Tangent(g2,g10) = 1.5708
    c: Tangent(g3,g10) = 1.5708
    c: Coincident(g12,g2)
    c: Coincident(g12,g3)
    c: PointOnObject(g14,g0)
    c: PointOnObject(g14,g3)
    c: Tangent(g0,g13) = 1.5708
    c: Tangent(g3,g13) = 1.5708
    c: Coincident(g15,g0)
    c: Coincident(g15,g3)
    c: Equal(g6,g9)
    c: Equal(g9,g12)
    c: Equal(g12,g15)
    c: DistanceX(g14,g3) = 0.8
FEATURE [PartDesign::Pad] Pad030
  Direction = (0,-1,2e-16)
  Length = 25.2
  Length2 = 10
  Midplane = true
  Placement = pos=(0,0,0) rot=(1,0,0;1.5708rad)
  Profile = -> Sketch135
  ReferenceAxis = -> Sketch135 [N_Axis]
  Refine = true
  Suppressed = false
  Type = 0
FEATURE [PartDesign::Body] Body009  label="perno fermo switch - caricabatterie - grilletto"
  AllowCompound = false
  Group = -> [Sketch135,Pad030]
  Origin = -> Origin009
  Tip = -> Pad030
FEATURE [Sketcher::SketchObject] Sketch136  label="scavo_rele"
  ArcFitTolerance = 1e-06
  AttachmentSupport = -> [XZ_Plane]
  ExternalGeometry = -> [Sketch]
  FullyConstrained = true
  MakeInternals = false
  MapMode = 5
  Placement = pos=(0,0,0) rot=(1,0,0;1.5708rad)
  sketch-geometry (7):
    g0: LineSegment [constr] StartX=-172.456 StartY=-60.9321 StartZ=0 EndX=-176.597 EndY=-73.6763 EndZ=0
    g1: LineSegment [constr] StartX=-172.456 StartY=-60.9321 StartZ=0 EndX=-170.364 EndY=-61.612 EndZ=0
    g2: LineSegment [constr] StartX=-172.456 StartY=-60.9321 StartZ=0 EndX=-176.07 EndY=-59.7579 EndZ=0
    g3: LineSegment StartX=-176.07 StartY=-59.7579 StartZ=0 EndX=-170.364 EndY=-61.612 EndZ=0
    g4: LineSegment StartX=-176.07 StartY=-59.7579 StartZ=0 EndX=-180.211 EndY=-72.502 EndZ=0
    g5: LineSegment StartX=-170.364 StartY=-61.612 StartZ=0 EndX=-174.505 EndY=-74.3561 EndZ=0
    g6: LineSegment StartX=-180.211 StartY=-72.502 StartZ=0 EndX=-174.505 EndY=-74.3561 EndZ=0
  constraints (19):
    c: Tangent(g0,g-3)
    c: Distance(g0,g-3) = 87.2
    c: Distance(g0,g0) = 13.4
    c: Coincident(g1,g0)
    c: Coincident(g2,g0)
    c: Distance(g2) = 3.8
    c: Distance(g1) = 2.2
    c: Perpendicular(g0,g1)
    c: Perpendicular(g0,g2)
    c: Coincident(g3,g2)
    c: Coincident(g3,g1)
    c: Equal(g4,g0)
    c: Equal(g5,g0)
    c: Parallel(g4,g0)
    c: Parallel(g5,g0)
    c: Coincident(g4,g2)
    c: Coincident(g5,g1)
    c: Coincident(g6,g4)
    c: Coincident(g6,g5)
FEATURE [Part::Extrusion] Extrude076  label="Extrude076 - scavo_rele"
  Base = -> Sketch136
  Dir = (0,-1,2e-16)
  DirMode = 2
  FaceMakerClass = Part::FaceMakerBullseye
  FaceMakerMode = 3
  LengthFwd = 18.2
  LengthRev = 0
  Solid = true
  Symmetric = true
FEATURE [Sketcher::SketchObject] Sketch137  label="scavo_nuovo_driver"
  ArcFitTolerance = 1e-06
  AttachmentSupport = -> [XZ_Plane]
  ExternalGeometry = -> [Sketch]
  FullyConstrained = true
  MakeInternals = false
  MapMode = 5
  Placement = pos=(0,0,0) rot=(1,0,0;1.5708rad)
  sketch-geometry (7):
    g0: LineSegment [constr] StartX=-160.034 StartY=-22.6997 StartZ=0 EndX=-164.854 EndY=-37.5361 EndZ=0
    g1: LineSegment [constr] StartX=-160.034 StartY=-22.6997 StartZ=0 EndX=-156.99 EndY=-23.6885 EndZ=0
    g2: LineSegment [constr] StartX=-160.034 StartY=-22.6997 StartZ=0 EndX=-163.648 EndY=-21.5254 EndZ=0
    g3: LineSegment StartX=-163.648 StartY=-21.5254 StartZ=0 EndX=-156.99 EndY=-23.6885 EndZ=0
    g4: LineSegment StartX=-163.648 StartY=-21.5254 StartZ=0 EndX=-168.468 EndY=-36.3619 EndZ=0
    g5: LineSegment StartX=-156.99 StartY=-23.6885 StartZ=0 EndX=-161.811 EndY=-38.525 EndZ=0
    g6: LineSegment StartX=-168.468 StartY=-36.3619 StartZ=0 EndX=-161.811 EndY=-38.525 EndZ=0
  constraints (19):
    c: Distance(g0,g-3) = 47
    c: Distance(g0) = 15.6
    c: Tangent(g0,g-3)
    c: Coincident(g1,g0)
    c: Coincident(g2,g0)
    c: Distance(g1) = 3.2
    c: Distance(g2) = 3.8
    c: Perpendicular(g0,g1)
    c: Perpendicular(g0,g2)
    c: Coincident(g3,g2)
    c: Coincident(g3,g1)
    c: Equal(g4,g0)
    c: Equal(g5,g0)
    c: Parallel(g4,g0)
    c: Parallel(g5,g0)
    c: Coincident(g4,g2)
    c: Coincident(g5,g1)
    c: Coincident(g6,g4)
    c: Coincident(g6,g5)
FEATURE [Part::Extrusion] Extrude077  label="Extrude077 - scavo_nuovo_driver"
  Base = -> Sketch137
  Dir = (0,-1,2e-16)
  DirMode = 2
  FaceMakerClass = Part::FaceMakerBullseye
  FaceMakerMode = 3
  LengthFwd = 20.8
  LengthRev = 0
  Solid = true
  Symmetric = true
FEATURE [Sketcher::SketchObject] Sketch138  label="scavo_nuovo_driver_alto"
  ArcFitTolerance = 1e-06
  AttachmentSupport = -> [XZ_Plane]
  ExternalGeometry = -> [Sketch]
  FullyConstrained = true
  MakeInternals = false
  MapMode = 5
  Placement = pos=(0,0,0) rot=(1,0,0;1.5708rad)
  sketch-geometry (7):
    g0: LineSegment [constr] StartX=-188.796 StartY=17.7274 StartZ=0 EndX=-187.75 EndY=4.97025 EndZ=0
    g1: LineSegment StartX=-187.75 StartY=4.97025 StartZ=0 EndX=-189.743 EndY=4.8067 EndZ=0
    g2: LineSegment StartX=-187.75 StartY=4.97025 StartZ=0 EndX=-182.766 EndY=5.37913 EndZ=0
    g3: LineSegment StartX=-190.79 StartY=17.5638 StartZ=0 EndX=-189.743 EndY=4.8067 EndZ=0
    g4: LineSegment StartX=-183.813 StartY=18.1363 StartZ=0 EndX=-182.766 EndY=5.37913 EndZ=0
    g5: LineSegment StartX=-190.79 StartY=17.5638 StartZ=0 EndX=-188.796 EndY=17.7274 EndZ=0
    g6: LineSegment StartX=-188.796 StartY=17.7274 StartZ=0 EndX=-183.813 EndY=18.1363 EndZ=0
  constraints (20):
    c: Distance(g0) = 12.8
    c: DistanceY(g-3,g0) = 9
    c: PointOnObject(g0,g-4)
    c: PointOnObject(g0,g-4)
    c: Coincident(g1,g0)
    c: Coincident(g2,g0)
    c: Distance(g1) = 2
    c: Distance(g2) = 5
    c: Perpendicular(g0,g1)
    c: Perpendicular(g0,g2)
    c: Equal(g3,g0)
    c: Parallel(g3,g0)
    c: Coincident(g3,g1)
    c: Equal(g4,g0)
    c: Parallel(g4,g0)
    c: Coincident(g4,g2)
    c: Coincident(g5,g3)
    c: Coincident(g5,g0)
    c: Coincident(g6,g0)
    c: Coincident(g6,g4)
FEATURE [Part::Extrusion] Extrude078  label="Extrude078 - scavo_nuovo_driver_alto"
  Base = -> Sketch138
  Dir = (0,-1,2e-16)
  DirMode = 2
  FaceMakerClass = Part::FaceMakerBullseye
  FaceMakerMode = 3
  LengthFwd = 16.6
  LengthRev = 0
  Solid = true
  Symmetric = true
FEATURE [Sketcher::SketchObject] Sketch139  label="fermi_nuovo_driver_alto"
  ArcFitTolerance = 1e-06
  AttachmentSupport = -> [XZ_Plane]
  ExternalGeometry = -> [Sketch138,Sketch]
  FullyConstrained = true
  MakeInternals = false
  MapMode = 5
  Placement = pos=(0,0,0) rot=(1,0,0;1.5708rad)
  sketch-geometry (17):
    g0: LineSegment [constr] StartX=-188.314 StartY=16.4295 StartZ=0 EndX=-187.885 EndY=13.7638 EndZ=0
    g1: LineSegment [constr] StartX=-187.885 StartY=13.7638 StartZ=0 EndX=-187.456 EndY=11.0981 EndZ=0
    g2: LineSegment StartX=-187.885 StartY=13.7638 StartZ=0 EndX=-187.71 EndY=12.6778 EndZ=0
    g3: LineSegment StartX=-187.885 StartY=13.7638 StartZ=0 EndX=-188.06 EndY=14.8499 EndZ=0
    g4: LineSegment StartX=-187.71 StartY=12.6778 StartZ=0 EndX=-185.538 EndY=13.0274 EndZ=0
    g5: LineSegment StartX=-188.06 StartY=14.8499 StartZ=0 EndX=-185.888 EndY=15.1994 EndZ=0
    g6: LineSegment StartX=-185.888 StartY=15.1994 StartZ=0 EndX=-185.538 EndY=13.0274 EndZ=0
    g7: LineSegment StartX=-187.456 StartY=11.0981 StartZ=0 EndX=-189.035 EndY=10.8439 EndZ=0
    g8: LineSegment StartX=-188.314 StartY=16.4295 StartZ=0 EndX=-189.893 EndY=16.1753 EndZ=0
    g9: LineSegment StartX=-189.893 StartY=16.1753 StartZ=0 EndX=-189.035 EndY=10.8439 EndZ=0
    g10: LineSegment StartX=-187.456 StartY=11.0981 StartZ=0 EndX=-185.284 EndY=11.4477 EndZ=0
    g11: LineSegment StartX=-188.314 StartY=16.4295 StartZ=0 EndX=-186.142 EndY=16.7791 EndZ=0
    g12: LineSegment StartX=-184.308 StartY=15.4537 StartZ=0 EndX=-183.958 EndY=13.2816 EndZ=0
    g13: ArcOfCircle CenterX=-185.888 CenterY=15.1994 CenterZ=0 NormalX=0 NormalY=0 NormalZ=1 AngleXU=0 Radius=1.6 StartAngle=0.15957 EndAngle=1.73037
    g14: GeomPoint [constr] X=-184.562 Y=17.0333 Z=0
    g15: ArcOfCircle CenterX=-185.538 CenterY=13.0274 CenterZ=0 NormalX=0 NormalY=0 NormalZ=1 AngleXU=0 Radius=1.6 StartAngle=4.87196 EndAngle=6.44276
    g16: GeomPoint [constr] X=-183.704 Y=11.7019 Z=0
  constraints (43):
    c: Tangent(g1,g0) = -1.5708
    c: Distance(g0) = 2.7
    c: Equal(g1,g0)
    c: Tangent(g1,g-5)
    c: Coincident(g2,g0)
    c: Coincident(g3,g0)
    c: Distance(g2) = 1.1
    c: Equal(g3,g2)
    c: PointOnObject(g3,g2)
    c: Coincident(g4,g2)
    c: Coincident(g5,g3)
    c: Distance(g4) = 2.2
    c: Equal(g4,g5)
    c: Perpendicular(g1,g4)
    c: Perpendicular(g0,g5)
    c: Coincident(g6,g5)
    c: Coincident(g6,g4)
    c: Coincident(g7,g1)
    c: Coincident(g8,g0)
    c: Distance(g7) = 1.6
    c: Equal(g7,g8)
    c: Perpendicular(g1,g7)
    c: Perpendicular(g8,g0)
    c: Coincident(g9,g8)
    c: Coincident(g9,g7)
    c: Coincident(g10,g1)
    c: Coincident(g11,g0)
    c: Distance(g10,g16) = 3.8
    c: Perpendicular(g1,g10)
    c: Perpendicular(g1,g11)
    c: DistanceY(g0,g-4) = 3.8
    c: PointOnObject(g14,g12)
    c: PointOnObject(g14,g11)
    c: Tangent(g12,g13) = 1.5708
    c: Tangent(g11,g13) = 1.5708
    c: PointOnObject(g16,g12)
    c: PointOnObject(g16,g10)
    c: Tangent(g12,g15) = 1.5708
    c: Tangent(g10,g15) = -1.5708
    c: Equal(g13,g15)
    c: Coincident(g13,g5)
    c: Parallel(g2,g0)
    c: PointOnObject(g0,g-5)
FEATURE [Part::Extrusion] Extrude079  label="Extrude079 - fermi_nuovo_driver_alto"
  Base = -> Sketch139
  Dir = (0,-1,2e-16)
  DirMode = 2
  FaceMakerClass = Part::FaceMakerBullseye
  FaceMakerMode = 3
  LengthFwd = 25.2
  LengthRev = 0
  Solid = true
  Symmetric = true
FEATURE [Sketcher::SketchObject] Sketch140  label="scavo_diodo_nuovo_driver_alto"
  ArcFitTolerance = 1e-06
  AttachmentSupport = -> [XZ_Plane]
  ExternalGeometry = -> [Sketch138]
  FullyConstrained = true
  MakeInternals = false
  MapMode = 5
  Placement = pos=(0,0,0) rot=(1,0,0;1.5708rad)
  sketch-geometry (4):
    g0: LineSegment StartX=-190.79 StartY=17.5638 StartZ=0 EndX=-189.743 EndY=4.8067 EndZ=0
    g1: LineSegment StartX=-193.78 StartY=17.3185 StartZ=0 EndX=-192.733 EndY=4.56137 EndZ=0
    g2: LineSegment StartX=-190.79 StartY=17.5638 StartZ=0 EndX=-193.78 EndY=17.3185 EndZ=0
    g3: LineSegment StartX=-192.733 StartY=4.56137 StartZ=0 EndX=-189.743 EndY=4.8067 EndZ=0
  constraints (11):
    c: Equal(g0,g-3)
    c: Parallel(g0,g-3)
    c: Equal(g1,g-3)
    c: Parallel(g1,g-3)
    c: Coincident(g2,g0)
    c: Distance(g2) = 3
    c: Perpendicular(g0,g2)
    c: Coincident(g1,g2)
    c: Coincident(g3,g1)
    c: Coincident(g3,g0)
    c: Coincident(g0,g-3)
FEATURE [Part::Extrusion] Extrude080  label="Extrude080 - scavo_diodo_nuovo_driver_alto"
  Base = -> Sketch140
  Dir = (0,-1,2e-16)
  DirMode = 2
  FaceMakerClass = Part::FaceMakerBullseye
  FaceMakerMode = 3
  LengthFwd = 4
  LengthRev = 0
  Placement = pos=(0,7.8,0) rot=(0,0,1;0rad)
  Solid = true
  Symmetric = false
FEATURE [Part::MultiFuse] Fusion001
  Refine = true
  Shapes = -> [Cut043,Extrude079]
FEATURE [Part::Cut] Cut044
  Base = -> Fusion001
  Refine = true
  Tool = -> Extrude078
FEATURE [Part::Cut] Cut045
  Base = -> Cut044
  Refine = true
  Tool = -> Extrude080
FEATURE [Sketcher::SketchObject] Sketch141  label="fermi_nuovo_driver"
  ArcFitTolerance = 1e-06
  AttachmentSupport = -> [XZ_Plane]
  ExternalGeometry = -> [Sketch,Sketch137]
  FullyConstrained = true
  MakeInternals = false
  MapMode = 5
  Placement = pos=(0,0,0) rot=(1,0,0;1.5708rad)
  sketch-geometry (17):
    g0: LineSegment [constr] StartX=-156.99 StartY=-23.6885 StartZ=0 EndX=-160.034 EndY=-22.6997 EndZ=0
    g1: LineSegment [constr] StartX=-160.034 StartY=-22.6997 StartZ=0 EndX=-162.815 EndY=-31.2592 EndZ=0
    g2: LineSegment [constr] StartX=-162.815 StartY=-31.2592 StartZ=0 EndX=-164.484 EndY=-36.3949 EndZ=0
    g3: LineSegment StartX=-164.484 StartY=-36.3949 StartZ=0 EndX=-166.576 EndY=-35.715 EndZ=0
    g4: LineSegment StartX=-167.603 StartY=-33.6989 StartZ=0 EndX=-166.923 EndY=-31.6066 EndZ=0
    g5: LineSegment StartX=-164.907 StartY=-30.5793 StartZ=0 EndX=-161.293 EndY=-31.7536 EndZ=0
    g6: LineSegment StartX=-161.293 StartY=-31.7536 StartZ=0 EndX=-162.962 EndY=-36.8893 EndZ=0
    g7: LineSegment StartX=-164.484 StartY=-36.3949 StartZ=0 EndX=-162.962 EndY=-36.8893 EndZ=0
    g8: LineSegment StartX=-165.402 StartY=-32.101 StartZ=0 EndX=-166.082 EndY=-34.1933 EndZ=0
    g9: LineSegment StartX=-166.082 StartY=-34.1933 StartZ=0 EndX=-163.989 EndY=-34.8732 EndZ=0
    g10: LineSegment StartX=-163.989 StartY=-34.8732 StartZ=0 EndX=-163.309 EndY=-32.7809 EndZ=0
    g11: LineSegment StartX=-163.309 StartY=-32.7809 StartZ=0 EndX=-165.402 EndY=-32.101 EndZ=0
    g12: ArcOfCircle CenterX=-165.402 CenterY=-32.101 CenterZ=0 NormalX=0 NormalY=0 NormalZ=1 AngleXU=0 Radius=1.6 StartAngle=1.25664 EndAngle=2.82743
    g13: GeomPoint [constr] X=-166.429 Y=-30.0849 Z=0
    g14: ArcOfCircle CenterX=-166.082 CenterY=-34.1933 CenterZ=0 NormalX=0 NormalY=0 NormalZ=1 AngleXU=0 Radius=1.6 StartAngle=2.82743 EndAngle=4.39823
    g15: GeomPoint [constr] X=-168.098 Y=-35.2206 Z=0
    g16: LineSegment [constr] StartX=-160.034 StartY=-22.6997 StartZ=0 EndX=-164.854 EndY=-37.5361 EndZ=0
  constraints (44):
    c: Coincident(g0,g-4)
    c: PointOnObject(g0,g-3)
    c: Parallel(g0,g-4)
    c: Coincident(g1,g0)
    c: Parallel(g1,g-3)
    c: Coincident(g2,g1)
    c: Distance(g2) = 5.4
    c: Coincident(g3,g2)
    c: Parallel(g2,g-3)
    c: Distance(g15,g13) = 5.4
    c: Perpendicular(g3,g2)
    c: Parallel(g4,g2)
    c: Distance(g5,g13) = 5.4
    c: Distance(g3,g15) = 3.8
    c: Perpendicular(g4,g5)
    c: Coincident(g6,g5)
    c: Distance(g6) = 5.4
    c: Parallel(g6,g4)
    c: Coincident(g7,g2)
    c: Coincident(g7,g6)
    c: Coincident(g8,g9)
    c: Coincident(g9,g10)
    c: Coincident(g10,g11)
    c: Coincident(g11,g8)
    c: Distance(g8,g10) = 2.2
    c: Distance(g9,g11) = 2.2
    c: Perpendicular(g11,g8)
    c: Equal(g8,g10)
    c: Equal(g11,g9)
    c: Tangent(g10,g2)
    c: Distance(g10,g1) = 1.6
    c: PointOnObject(g13,g4)
    c: PointOnObject(g13,g5)
    c: Tangent(g4,g12) = 1.5708
    c: Tangent(g5,g12) = 1.5708
    c: PointOnObject(g15,g4)
    c: Tangent(g4,g14) = 1.5708
    c: Tangent(g3,g14) = 1.5708
    c: Equal(g14,g12)
    c: Coincident(g12,g8)
    c: Coincident(g16,g0)
    c: PointOnObject(g16,g-5)
    c: Parallel(g16,g-3)
    c: Distance(g16,g2) = 1.2
FEATURE [Part::Extrusion] Extrude081  label="Extrude081 - fermi_nuovo_driver"
  Base = -> Sketch141
  Dir = (0,-1,2e-16)
  DirMode = 2
  FaceMakerClass = Part::FaceMakerBullseye
  FaceMakerMode = 3
  LengthFwd = 25.2
  LengthRev = 0
  Solid = true
  Symmetric = true
FEATURE [Part::MultiFuse] Fusion002
  Refine = true
  Shapes = -> [Cut045,Extrude081]
FEATURE [Part::Cut] Cut046
  Base = -> Fusion002
  Refine = true
  Tool = -> Extrude077
FEATURE [Sketcher::SketchObject] Sketch142  label="fermi_rele"
  ArcFitTolerance = 1e-06
  AttachmentSupport = -> [XZ_Plane]
  ExternalGeometry = -> [Sketch,Sketch136]
  FullyConstrained = true
  MakeInternals = false
  MapMode = 5
  Placement = pos=(0,0,0) rot=(1,0,0;1.5708rad)
  sketch-geometry (15):
    g0: LineSegment StartX=-176.936 StartY=-62.4208 StartZ=0 EndX=-177.615 EndY=-64.5131 EndZ=0
    g1: LineSegment StartX=-174.919 StartY=-61.3936 StartZ=0 EndX=-171.305 EndY=-62.5678 EndZ=0
    g2: LineSegment StartX=-171.305 StartY=-62.5678 StartZ=0 EndX=-172.974 EndY=-67.7035 EndZ=0
    g3: LineSegment StartX=-176.588 StartY=-66.5293 StartZ=0 EndX=-172.974 EndY=-67.7035 EndZ=0
    g4: LineSegment StartX=-175.414 StartY=-62.9152 StartZ=0 EndX=-173.322 EndY=-63.5951 EndZ=0
    g5: LineSegment StartX=-175.414 StartY=-62.9152 StartZ=0 EndX=-176.094 EndY=-65.0076 EndZ=0
    g6: LineSegment StartX=-173.322 StartY=-63.5951 StartZ=0 EndX=-174.001 EndY=-65.6874 EndZ=0
    g7: LineSegment StartX=-176.094 StartY=-65.0076 StartZ=0 EndX=-174.001 EndY=-65.6874 EndZ=0
    g8: LineSegment [constr] StartX=-173.322 StartY=-63.5951 StartZ=0 EndX=-172.827 EndY=-62.0734 EndZ=0
    g9: LineSegment [constr] StartX=-173.322 StartY=-63.5951 StartZ=0 EndX=-171.8 EndY=-64.0895 EndZ=0
    g10: LineSegment [constr] StartX=-170.364 StartY=-61.612 StartZ=0 EndX=-172.456 EndY=-60.9321 EndZ=0
    g11: ArcOfCircle CenterX=-175.414 CenterY=-62.9152 CenterZ=0 NormalX=0 NormalY=0 NormalZ=1 AngleXU=0 Radius=1.6 StartAngle=1.25664 EndAngle=2.82743
    g12: GeomPoint [constr] X=-176.441 Y=-60.8991 Z=0
    g13: ArcOfCircle CenterX=-176.094 CenterY=-65.0076 CenterZ=0 NormalX=0 NormalY=0 NormalZ=1 AngleXU=0 Radius=1.6 StartAngle=2.82743 EndAngle=4.39823
    g14: GeomPoint [constr] X=-178.11 Y=-66.0348 Z=0
  constraints (39):
    c: Distance(g14,g12) = 5.4
    c: Distance(g1,g12) = 5.4
    c: Perpendicular(g1,g0)
    c: Coincident(g2,g1)
    c: Parallel(g2,g0)
    c: Coincident(g3,g2)
    c: Parallel(g2,g-3)
    c: Coincident(g5,g4)
    c: Distance(g5) = 2.2
    c: Distance(g4) = 2.2
    c: Perpendicular(g4,g5)
    c: Coincident(g6,g4)
    c: Equal(g6,g5)
    c: Parallel(g6,g5)
    c: Coincident(g7,g5)
    c: Coincident(g7,g6)
    c: Coincident(g8,g4)
    c: Coincident(g9,g4)
    c: Distance(g8) = 1.6
    c: Distance(g9) = 1.6
    c: Parallel(g8,g6)
    c: Parallel(g9,g4)
    c: PointOnObject(g8,g1)
    c: PointOnObject(g9,g2)
    c: Coincident(g10,g-4)
    c: Parallel(g10,g-4)
    c: PointOnObject(g10,g-3)
    c: Tangent(g6,g-3) = 1.5708
    c: Distance(g4,g10) = 2.8
    c: PointOnObject(g12,g1)
    c: Tangent(g1,g11) = 1.5708
    c: Tangent(g0,g11) = -1.5708
    c: PointOnObject(g14,g3)
    c: PointOnObject(g14,g0)
    c: Tangent(g3,g13) = -1.5708
    c: Tangent(g0,g13) = -1.5708
    c: Equal(g11,g13)
    c: Coincident(g11,g4)
    c: Parallel(g3,g1)
FEATURE [Part::Extrusion] Extrude082  label="Extrude082 - fermi_rele"
  Base = -> Sketch142
  Dir = (0,-1,2e-16)
  DirMode = 2
  FaceMakerClass = Part::FaceMakerBullseye
  FaceMakerMode = 3
  LengthFwd = 25.2
  LengthRev = 0
  Solid = true
  Symmetric = true
FEATURE [Part::MultiFuse] Fusion003
  Refine = true
  Shapes = -> [Cut046,Extrude082]
FEATURE [Part::Cut] Cut047
  Base = -> Fusion003
  Refine = true
  Tool = -> Extrude076
FEATURE [Sketcher::SketchObject] Sketch143  label="foro_passaggio_cavi_led_batteria"
  ArcFitTolerance = 1e-06
  AttachmentSupport = -> [XZ_Plane]
  ExternalGeometry = -> [Sketch,Sketch042,Sketch036]
  FullyConstrained = true
  MakeInternals = false
  MapMode = 5
  Placement = pos=(0,0,0) rot=(1,0,0;1.5708rad)
  sketch-geometry (4):
    g0: LineSegment StartX=-207.775 StartY=-41.3701 StartZ=0 EndX=-213.607 EndY=-53.8767 EndZ=0
    g1: LineSegment StartX=-213.607 StartY=-53.8767 StartZ=0 EndX=-211.843 EndY=-59.5559 EndZ=0
    g2: LineSegment StartX=-207.775 StartY=-41.3701 StartZ=0 EndX=-207.775 EndY=-50.8316 EndZ=0
    g3: LineSegment StartX=-207.775 StartY=-50.8316 StartZ=0 EndX=-211.843 EndY=-59.5559 EndZ=0
  constraints (9):
    c: Coincident(g0,g-3)
    c: PointOnObject(g1,g-6)
    c: Coincident(g1,g0)
    c: Coincident(g2,g0)
    c: Coincident(g2,g-7)
    c: Coincident(g3,g2)
    c: Parallel(g3,g0)
    c: Coincident(g3,g1)
    c: Coincident(g0,g-5)
FEATURE [Part::Extrusion] Extrude083  label="Extrude083 - foro_passaggio_cavi_led_batteria"
  Base = -> Sketch143
  Dir = (0,-1,2e-16)
  DirMode = 2
  FaceMakerClass = Part::FaceMakerBullseye
  FaceMakerMode = 3
  LengthFwd = 6
  LengthRev = 0
  Solid = true
  Symmetric = true
FEATURE [Part::Cut] Cut048
  Base = -> Cut047
  Refine = true
  Tool = -> Extrude083
FEATURE [Sketcher::SketchObject] Sketch144  label="foro_areazione_alimentatore"
  ArcFitTolerance = 1e-06
  AttachmentSupport = -> [XZ_Plane]
  ExternalGeometry = -> [Sketch036]
  FullyConstrained = true
  MakeInternals = false
  MapMode = 5
  Placement = pos=(0,0,0) rot=(1,0,0;1.5708rad)
  sketch-geometry (4):
    g0: LineSegment StartX=-211.843 StartY=-60.3701 StartZ=0 EndX=-207.775 EndY=-60.3701 EndZ=0
    g1: LineSegment StartX=-207.775 StartY=-60.3701 StartZ=0 EndX=-207.775 EndY=-70.3701 EndZ=0
    g2: LineSegment StartX=-211.843 StartY=-60.3701 StartZ=0 EndX=-211.843 EndY=-70.3701 EndZ=0
    g3: LineSegment StartX=-207.775 StartY=-70.3701 StartZ=0 EndX=-211.843 EndY=-70.3701 EndZ=0
  constraints (11):
    c: Horizontal(g0)
    c: Distance(g1) = 10
    c: Coincident(g1,g0)
    c: Tangent(g1,g-3)
    c: PointOnObject(g0,g-4)
    c: Coincident(g2,g0)
    c: PointOnObject(g2,g-4)
    c: Coincident(g3,g1)
    c: Horizontal(g3)
    c: Coincident(g3,g2)
    c: DistanceY(g0,g-3) = 19
FEATURE [Part::Extrusion] Extrude084  label="Extrude084 - foro_areazione_alimentatore"
  Base = -> Sketch144
  Dir = (0,-1,2e-16)
  DirMode = 2
  FaceMakerClass = Part::FaceMakerBullseye
  FaceMakerMode = 3
  LengthFwd = 10
  LengthRev = 0
  Solid = true
  Symmetric = true
FEATURE [Part::Cut] Cut049
  Base = -> Cut048
  Refine = true
  Tool = -> Extrude084
FEATURE [Sketcher::SketchObject] Sketch145  label="foro_per_condesatore"
  ArcFitTolerance = 1e-06
  AttachmentSupport = -> [XZ_Plane]
  ExternalGeometry = -> [Sketch,Sketch139]
  FullyConstrained = true
  MakeInternals = false
  MapMode = 5
  Placement = pos=(0,0,0) rot=(1,0,0;1.5708rad)
  sketch-geometry (1):
    g0: Circle CenterX=-182.345 CenterY=7.02342 CenterZ=0 NormalX=0 NormalY=0 NormalZ=1 AngleXU=0 Radius=5.2
  constraints (3):
    c: Diameter(g0) = 10.4
    c: Tangent(g0,g-3)
    c: Tangent(g0,g-4)
FEATURE [Part::Extrusion] Extrude085  label="Extrude085 - foro_per_condesatore"
  Base = -> Sketch145
  Dir = (0,-1,2e-16)
  DirMode = 2
  FaceMakerClass = Part::FaceMakerBullseye
  FaceMakerMode = 3
  LengthFwd = 25.2
  LengthRev = 0
  Solid = true
  Symmetric = true
FEATURE [Part::Cut] Cut050
  Base = -> Cut049
  Refine = true
  Tool = -> Extrude085
FEATURE [Sketcher::SketchObject] Sketch146  label="scavo_pulsante_6x6_per_led_batteria"
  ArcFitTolerance = 1e-06
  AttachmentSupport = -> [XZ_Plane]
  ExternalGeometry = -> [Sketch016]
  FullyConstrained = true
  MakeInternals = false
  MapMode = 5
  Placement = pos=(0,0,0) rot=(1,0,0;1.5708rad)
  sketch-geometry (5):
    g0: LineSegment StartX=-216.643 StartY=-65.8316 StartZ=0 EndX=-216.643 EndY=-72.8316 EndZ=0
    g1: LineSegment StartX=-216.643 StartY=-72.8316 StartZ=0 EndX=-210.243 EndY=-72.8316 EndZ=0
    g2: LineSegment StartX=-210.243 StartY=-72.8316 StartZ=0 EndX=-210.243 EndY=-65.8316 EndZ=0
    g3: LineSegment StartX=-210.243 StartY=-65.8316 StartZ=0 EndX=-216.643 EndY=-65.8316 EndZ=0
    g4: GeomPoint [constr] X=-213.443 Y=-69.3316 Z=0
  constraints (13):
    c: Coincident(g0,g1)
    c: Coincident(g1,g2)
    c: Coincident(g2,g3)
    c: Coincident(g3,g0)
    c: Vertical(g0)
    c: Vertical(g2)
    c: Horizontal(g1)
    c: Horizontal(g3)
    c: Distance(g0,g2) = 6.4
    c: Distance(g1,g3) = 7
    c: Tangent(g1,g-3)
    c: Symmetric(g0,g2,g4)
    c: Vertical(g-3,g4)
FEATURE [Part::Extrusion] Extrude086  label="Extrude086 - scavo_pulsante_6x6_per_led_batteria"
  Base = -> Sketch146
  Dir = (0,-1,2e-16)
  DirMode = 2
  FaceMakerClass = Part::FaceMakerBullseye
  FaceMakerMode = 3
  LengthFwd = 4
  LengthRev = 0
  Placement = pos=(0,12.6,0) rot=(0,0,1;0rad)
  Solid = true
  Symmetric = false
FEATURE [Sketcher::SketchObject] Sketch147  label="scavo_led_stato_batteria"
  ArcFitTolerance = 1e-06
  AttachmentSupport = -> [XZ_Plane]
  ExternalGeometry = -> [Sketch016]
  FullyConstrained = true
  MakeInternals = false
  MapMode = 5
  Placement = pos=(0,0,0) rot=(1,0,0;1.5708rad)
  sketch-geometry (5):
    g0: LineSegment StartX=-215.843 StartY=-56.2316 StartZ=0 EndX=-215.843 EndY=-65.4316 EndZ=0
    g1: LineSegment StartX=-215.843 StartY=-65.4316 StartZ=0 EndX=-211.043 EndY=-65.4316 EndZ=0
    g2: LineSegment StartX=-211.043 StartY=-65.4316 StartZ=0 EndX=-211.043 EndY=-56.2316 EndZ=0
    g3: LineSegment StartX=-211.043 StartY=-56.2316 StartZ=0 EndX=-215.843 EndY=-56.2316 EndZ=0
    g4: GeomPoint [constr] X=-213.443 Y=-60.8316 Z=0
  constraints (13):
    c: Coincident(g0,g1)
    c: Coincident(g1,g2)
    c: Coincident(g2,g3)
    c: Coincident(g3,g0)
    c: Distance(g0,g2) = 4.8
    c: Distance(g1,g3) = 9.2
    c: Equal(g0,g2)
    c: Equal(g1,g3)
    c: Perpendicular(g3,g0)
    c: DistanceY(g-3,g0) = 11.4
    c: Vertical(g2)
    c: Symmetric(g0,g2,g4)
    c: Vertical(g4,g-3)
FEATURE [Part::Extrusion] Extrude087  label="Extrude087 - scavo_led_stato_batteria"
  Base = -> Sketch147
  Dir = (0,-1,2e-16)
  DirMode = 2
  FaceMakerClass = Part::FaceMakerBullseye
  FaceMakerMode = 3
  LengthFwd = 2.2
  LengthRev = 0
  Placement = pos=(0,12.6,0) rot=(0,0,1;0rad)
  Solid = true
  Symmetric = false
FEATURE [Sketcher::SketchObject] Sketch148
  ArcFitTolerance = 1e-06
  AttachmentSupport = -> [Pad016]
  ExternalGeometry = -> [Pad016]
  FullyConstrained = true
  MakeInternals = false
  MapMode = 5
  Placement = pos=(0,0,-80.4316) rot=(1,0,0;3.14159rad)
  sketch-geometry (8):
    g0: LineSegment StartX=-176.685 StartY=3.6 StartZ=0 EndX=-186.685 EndY=3.6 EndZ=0
    g1: LineSegment StartX=-176.685 StartY=3.6 StartZ=0 EndX=-176.685 EndY=-9e-16 EndZ=0
    g2: LineSegment [constr] StartX=-186.685 StartY=3.6 StartZ=0 EndX=-186.685 EndY=-9e-16 EndZ=0
    g3: ArcOfEllipse CenterX=-186.685 CenterY=-9e-16 CenterZ=0 NormalX=0 NormalY=0 NormalZ=1 MajorRadius=10 MinorRadius=3.6 AngleXU=0 StartAngle=0 EndAngle=1.5708
    g4: LineSegment [constr] StartX=-176.685 StartY=-1e-15 StartZ=0 EndX=-196.685 EndY=-1e-15 EndZ=0
    g5: LineSegment [constr] StartX=-186.685 StartY=3.6 StartZ=0 EndX=-186.685 EndY=-3.6 EndZ=0
    g6: GeomPoint [constr] X=-177.356 Y=-1e-15 Z=0
    g7: GeomPoint [constr] X=-196.015 Y=-1e-15 Z=0
  constraints (13):
    c: Distance(g0) = 10
    c: Coincident(g0,g-5)
    c: PointOnObject(g0,g-3)
    c: Coincident(g1,g0)
    c: Coincident(g1,g-5)
    c: Coincident(g2,g0)
    c: Vertical(g2)
    c: PointOnObject(g2,g-4)
    c: InternalAlignment(g4-g7 -> g3) x4
    c: Coincident(g3,g2)
    c: Coincident(g3,g0)
    c: Coincident(g3,g1)
    c: Horizontal(g4)
FEATURE [PartDesign::SubtractivePipe] SubtractivePipe004
  AuxilleryCurvelinear = true
  AuxillerySpineTangent = false
  BaseFeature = -> Pad016
  Binormal = (0,0,0)
  Mode = 0
  Profile = -> Sketch148
  Refine = true
  Spine = -> Pad016 [Edge253]
  SpineTangent = false
  Suppressed = false
  Transformation = 0
  Transition = 0
FEATURE [Sketcher::SketchObject] Sketch149
  ArcFitTolerance = 1e-06
  AttachmentSupport = -> [Pad016]
  ExternalGeometry = -> [Pad016]
  FullyConstrained = true
  MakeInternals = false
  MapMode = 5
  Placement = pos=(0,0,-80.4316) rot=(1,0,0;3.14159rad)
  sketch-geometry (8):
    g0: LineSegment StartX=-215.932 StartY=3.6 StartZ=0 EndX=-205.932 EndY=3.6 EndZ=0
    g1: LineSegment StartX=-215.932 StartY=3.6 StartZ=0 EndX=-215.932 EndY=-4e-16 EndZ=0
    g2: LineSegment [constr] StartX=-205.932 StartY=3.6 StartZ=0 EndX=-205.932 EndY=-9e-16 EndZ=0
    g3: ArcOfEllipse CenterX=-205.932 CenterY=-1e-15 CenterZ=0 NormalX=0 NormalY=0 NormalZ=1 MajorRadius=10 MinorRadius=3.6 AngleXU=-3.14159 StartAngle=4.71239 EndAngle=6.28319
    g4: LineSegment [constr] StartX=-215.932 StartY=-1e-15 StartZ=0 EndX=-195.932 EndY=-1e-15 EndZ=0
    g5: LineSegment [constr] StartX=-205.932 StartY=-3.6 StartZ=0 EndX=-205.932 EndY=3.6 EndZ=0
    g6: GeomPoint [constr] X=-215.262 Y=-2.1e-15 Z=0
    g7: GeomPoint [constr] X=-196.602 Y=-9e-16 Z=0
  constraints (13):
    c: Distance(g0) = 10
    c: Coincident(g0,g-5)
    c: PointOnObject(g0,g-5)
    c: Coincident(g1,g0)
    c: Coincident(g1,g-4)
    c: Coincident(g2,g0)
    c: Vertical(g2)
    c: PointOnObject(g2,g-3)
    c: InternalAlignment(g4-g7 -> g3) x4
    c: Coincident(g3,g2)
    c: Coincident(g3,g0)
    c: Coincident(g3,g1)
    c: Horizontal(g4)
FEATURE [PartDesign::SubtractivePipe] SubtractivePipe005
  AuxilleryCurvelinear = true
  AuxillerySpineTangent = false
  BaseFeature = -> SubtractivePipe004
  Binormal = (0,0,0)
  Mode = 0
  Profile = -> Sketch149
  Refine = true
  Spine = -> Pad016 [Edge251,Edge256,Edge255]
  SpineTangent = false
  Suppressed = false
  Transformation = 0
  Transition = 0
FEATURE [PartDesign::SubtractiveLoft] SubtractiveLoft002
  BaseFeature = -> SubtractivePipe005
  Closed = false
  Profile = -> Sketch129
  Refine = true
  Ruled = false
  Sections = -> [Sketch130]
  Suppressed = false
FEATURE [PartDesign::SubtractiveLoft] SubtractiveLoft003
  BaseFeature = -> SubtractiveLoft002
  Closed = false
  Profile = -> Clone2D001
  Refine = true
  Ruled = false
  Sections = -> [Sketch131]
  Suppressed = false
FEATURE [PartDesign::Chamfer] Chamfer010
  Angle = 45
  Base = -> SubtractiveLoft003 [Edge203,Edge204,Edge202,Edge201,Edge195]
  BaseFeature = -> SubtractiveLoft003
  ChamferType = 0
  FlipDirection = false
  Refine = true
  Size = 1.5
  Size2 = 1
  SupportTransform = false
  Suppressed = false
  UseAllEdges = false
FEATURE [PartDesign::Chamfer] Chamfer011
  Angle = 45
  Base = -> Chamfer010 [Edge15]
  BaseFeature = -> Chamfer010
  ChamferType = 0
  FlipDirection = false
  Refine = true
  Size = 1.6
  Size2 = 1
  SupportTransform = false
  Suppressed = false
  UseAllEdges = false
FEATURE [PartDesign::Chamfer] Chamfer012
  Angle = 45
  Base = -> Chamfer011 [Edge10]
  BaseFeature = -> Chamfer011
  ChamferType = 0
  FlipDirection = false
  Refine = true
  Size = 3.5
  Size2 = 1
  SupportTransform = false
  Suppressed = false
  UseAllEdges = false
FEATURE [PartDesign::Chamfer] Chamfer013
  Angle = 45
  Base = -> Chamfer012 [Edge94]
  BaseFeature = -> Chamfer012
  ChamferType = 0
  FlipDirection = false
  Refine = true
  Size = 1.9
  Size2 = 1
  SupportTransform = false
  Suppressed = false
  UseAllEdges = false
FEATURE [PartDesign::Fillet] Fillet007
  Base = -> Chamfer013 [Edge83]
  BaseFeature = -> Chamfer013
  Radius = 1.1
  Refine = true
  SupportTransform = false
  Suppressed = false
  UseAllEdges = false
FEATURE [PartDesign::Fillet] Fillet008
  Base = -> Fillet007 [Edge75]
  BaseFeature = -> Fillet007
  Radius = 1.9
  Refine = true
  SupportTransform = false
  Suppressed = false
  UseAllEdges = false
FEATURE [PartDesign::Pocket] Pocket011
  BaseFeature = -> Fillet008
  Direction = (0,1,-2e-16)
  Length = 0.8
  Length2 = 5
  Profile = -> Sketch132
  ReferenceAxis = -> Sketch132 [N_Axis]
  Refine = true
  Suppressed = false
  Type = 0
FEATURE [PartDesign::Pocket] Pocket012
  BaseFeature = -> Pocket011
  Direction = (0,1,0)
  Length = 1
  Length2 = 5
  Profile = -> ShapeString
  ReferenceAxis = -> ShapeString [N_Axis]
  Refine = true
  Suppressed = false
  Type = 0
FEATURE [Sketcher::SketchObject] Sketch150
  ArcFitTolerance = 1e-06
  AttachmentSupport = -> [Pad008]
  ExternalGeometry = -> [Pad008]
  FullyConstrained = true
  MakeInternals = false
  MapMode = 5
  Placement = pos=(0,3.6,0) rot=(0,0.707107,0.707107;3.14159rad)
  sketch-geometry (7):
    g0: LineSegment [constr] StartX=210.343 StartY=-66.0316 StartZ=0 EndX=210.343 EndY=-72.8316 EndZ=0
    g1: LineSegment [constr] StartX=210.343 StartY=-72.8316 StartZ=0 EndX=216.543 EndY=-72.8316 EndZ=0
    g2: LineSegment [constr] StartX=216.543 StartY=-72.8316 StartZ=0 EndX=216.543 EndY=-66.0316 EndZ=0
    g3: LineSegment [constr] StartX=216.543 StartY=-66.0316 StartZ=0 EndX=210.343 EndY=-66.0316 EndZ=0
    g4: LineSegment [constr] StartX=210.343 StartY=-72.8316 StartZ=0 EndX=216.543 EndY=-66.0316 EndZ=0
    g5: LineSegment [constr] StartX=210.343 StartY=-66.0316 StartZ=0 EndX=213.443 EndY=-69.4316 EndZ=0
    g6: Circle CenterX=213.443 CenterY=-69.4316 CenterZ=0 NormalX=0 NormalY=0 NormalZ=1 AngleXU=0 Radius=2
  constraints (18):
    c: Coincident(g0,g1)
    c: Coincident(g1,g2)
    c: Coincident(g2,g3)
    c: Coincident(g3,g0)
    c: Vertical(g0)
    c: Vertical(g2)
    c: Horizontal(g1)
    c: Horizontal(g3)
    c: Distance(g0,g2) = 6.2
    c: Distance(g1,g3) = 6.8
    c: DistanceY(g-3,g1) = 4
    c: Coincident(g4,g0)
    c: Coincident(g4,g2)
    c: Coincident(g5,g0)
    c: Symmetric(g0,g2,g5)
    c: Diameter(g6) = 4
    c: Coincident(g6,g5)
    c: Vertical(g5,g-3)
FEATURE [Sketcher::SketchObject] Sketch151
  ArcFitTolerance = 1e-06
  AttachmentSupport = -> [Pad008]
  ExternalGeometry = -> [Pad008]
  FullyConstrained = true
  MakeInternals = false
  MapMode = 5
  Placement = pos=(0,3.6,0) rot=(0,0.707107,0.707107;3.14159rad)
  sketch-geometry (10):
    g0: LineSegment [constr] StartX=211.143 StartY=-56.2316 StartZ=0 EndX=211.143 EndY=-65.4316 EndZ=0
    g1: LineSegment [constr] StartX=211.143 StartY=-65.4316 StartZ=0 EndX=215.743 EndY=-65.4316 EndZ=0
    g2: LineSegment [constr] StartX=215.743 StartY=-65.4316 StartZ=0 EndX=215.743 EndY=-56.2316 EndZ=0
    g3: LineSegment [constr] StartX=215.743 StartY=-56.2316 StartZ=0 EndX=211.143 EndY=-56.2316 EndZ=0
    g4: LineSegment StartX=212.243 StartY=-63.8316 StartZ=0 EndX=214.643 EndY=-63.8316 EndZ=0
    g5: LineSegment StartX=214.643 StartY=-63.8316 StartZ=0 EndX=214.643 EndY=-57.0316 EndZ=0
    g6: LineSegment StartX=214.643 StartY=-57.0316 StartZ=0 EndX=212.243 EndY=-57.0316 EndZ=0
    g7: LineSegment StartX=212.243 StartY=-57.0316 StartZ=0 EndX=212.243 EndY=-63.8316 EndZ=0
    g8: GeomPoint [constr] X=213.443 Y=-60.4316 Z=0
    g9: GeomPoint [constr] X=213.443 Y=-60.8316 Z=0
  constraints (26):
    c: Coincident(g0,g1)
    c: Coincident(g1,g2)
    c: Coincident(g2,g3)
    c: Coincident(g3,g0)
    c: Vertical(g0)
    c: Vertical(g2)
    c: Horizontal(g1)
    c: Horizontal(g3)
    c: Distance(g0,g2) = 4.6
    c: Distance(g1,g3) = 9.2
    c: DistanceY(g-3,g1) = 11.4
    c: Coincident(g4,g5)
    c: Coincident(g5,g6)
    c: Coincident(g6,g7)
    c: Coincident(g7,g4)
    c: Horizontal(g4)
    c: Horizontal(g6)
    c: Vertical(g5)
    c: Vertical(g7)
    c: Symmetric(g6,g4,g8)
    c: Distance(g5,g7) = 2.4
    c: Distance(g4,g6) = 6.8
    c: Symmetric(g2,g0,g9)
    c: Vertical(g8,g9)
    c: DistanceY(g1,g4) = 1.6
    c: Vertical(g9,g-3)
FEATURE [PartDesign::Pocket] Pocket019
  BaseFeature = -> Pocket013
  Direction = (0,-1,2e-16)
  Length = 3.6
  Length2 = 5
  Profile = -> Sketch151
  ReferenceAxis = -> Sketch151 [N_Axis]
  Refine = true
  Suppressed = false
  Type = 0
FEATURE [PartDesign::Pocket] Pocket018
  BaseFeature = -> Pocket019
  Direction = (0,-1,2e-16)
  Length = 3.6
  Length2 = 5
  Profile = -> Sketch150
  ReferenceAxis = -> Sketch150 [N_Axis]
  Refine = true
  Suppressed = false
  Type = 0
FEATURE [PartDesign::Point] DatumPoint
  AttacherType = Attacher::AttachEnginePoint
  AttachmentSupport = -> [Sketch150]
  MapMode = 36
  Placement = pos=(-213.443,3.6,-69.4316) rot=(0,1,0;3.14159rad)
FEATURE [PartDesign::Plane] DatumPlane002
  AttachmentSupport = -> [DatumPoint]
  Length = 265.655
  MapMode = 1
  Placement = pos=(-213.443,3.6,-69.4316) rot=(0,0,1;0rad)
  ResizeMode = 0
  Width = 72.0719
FEATURE [Sketcher::SketchObject] Sketch152
  ArcFitTolerance = 1e-06
  AttachmentSupport = -> [DatumPlane002]
  ExternalGeometry = -> [Sketch150]
  FullyConstrained = true
  MakeInternals = false
  MapMode = 5
  Placement = pos=(-213.443,3.6,-69.4316) rot=(0,0,1;0rad)
  sketch-geometry (7):
    g0: LineSegment StartX=0 StartY=0 StartZ=0 EndX=-4 EndY=5.1e-15 EndZ=0
    g1: ArcOfEllipse CenterX=0 CenterY=0 CenterZ=0 NormalX=0 NormalY=0 NormalZ=1 MajorRadius=4 MinorRadius=3.6 AngleXU=3.14159 StartAngle=2e-16 EndAngle=1.5708
    g2: LineSegment [constr] StartX=-4 StartY=9e-16 StartZ=0 EndX=4 EndY=-9e-16 EndZ=0
    g3: LineSegment [constr] StartX=0 StartY=-3.6 StartZ=0 EndX=0 EndY=3.6 EndZ=0
    g4: GeomPoint [constr] X=-1.74356 Y=2.5e-15 Z=0
    g5: GeomPoint [constr] X=1.74356 Y=-2e-15 Z=0
    g6: LineSegment StartX=0 StartY=0 StartZ=0 EndX=-5.5e-15 EndY=-3.6 EndZ=0
  constraints (11):
    c: PointOnObject(g1,g-2)
    c: Distance(g0) = 4
    c: PointOnObject(g0,g-1)
    c: InternalAlignment(g2-g5 -> g1) x4
    c: Coincident(g1,g0)
    c: Vertical(g3)
    c: Coincident(g1,g-1)
    c: Distance(g6) = 3.6
    c: Coincident(g6,g1)
    c: Coincident(g1,g6)
    c: Coincident(g0,g1)
FEATURE [PartDesign::Groove] Groove
  Angle = 360
  Angle2 = 60
  Axis = (0,1,0)
  Base = (-213.443,3.6,-69.4316)
  BaseFeature = -> Pocket018
  Profile = -> Sketch152
  ReferenceAxis = -> Sketch152 [V_Axis]
  Refine = true
  Reversed = true
  Suppressed = false
  Type = 0
FEATURE [PartDesign::Body] Body006  label="lato SX"
  AllowCompound = false
  Group = -> [Binder,Pad019,Chamfer015,Pocket002,Sketch133,Sketch091,Pad005,Sketch092,Pocket001,Sketch093,Sketch094,Pad006,Sketch095,Pad007,Sketch096,Pad008,Sketch097,Pad009,Chamfer005,Pocket004,Sketch098,Pad010,Chamfer006,Pocket003,SubtractivePipe,SubtractivePipe001,Sketch099,Sketch106,Sketch107,Sketch108,Clone2D,Sketch109,SubtractiveLoft,SubtractiveLoft001,Sketch110,Sketch111,Sketch112,Chamfer016,Chamfer017,+15 more]
  Origin = -> Origin006
  Tip = -> Groove
FEATURE [Sketcher::SketchObject] Sketch153  label="ripieno_per_sostegno_led_batteria"
  ArcFitTolerance = 1e-06
  AttachmentSupport = -> [XZ_Plane]
  ExternalGeometry = -> [Sketch036]
  FullyConstrained = true
  MakeInternals = false
  MapMode = 5
  Placement = pos=(0,0,0) rot=(1,0,0;1.5708rad)
  sketch-geometry (4):
    g0: LineSegment StartX=-217.343 StartY=-54.5944 StartZ=0 EndX=-217.343 EndY=-63.1944 EndZ=0
    g1: LineSegment StartX=-217.343 StartY=-63.1944 StartZ=0 EndX=-211.843 EndY=-63.1944 EndZ=0
    g2: LineSegment StartX=-211.843 StartY=-63.1944 StartZ=0 EndX=-211.843 EndY=-54.5944 EndZ=0
    g3: LineSegment StartX=-211.843 StartY=-54.5944 StartZ=0 EndX=-217.343 EndY=-54.5944 EndZ=0
  constraints (11):
    c: Coincident(g0,g1)
    c: Coincident(g1,g2)
    c: Coincident(g2,g3)
    c: Coincident(g3,g0)
    c: Vertical(g0)
    c: Horizontal(g1)
    c: Horizontal(g3)
    c: Tangent(g2,g-3)
    c: DistanceY(g2,g-3) = 4.5
    c: DistanceX(g3,g3) = 5.5
    c: DistanceY(g0,g0) = 8.6
FEATURE [Part::Extrusion] Extrude088  label="Extrude088 - ripieno_per_sostegno_led_batteria"
  Base = -> Sketch153
  Dir = (0,-1,2e-16)
  DirMode = 2
  FaceMakerClass = Part::FaceMakerBullseye
  FaceMakerMode = 3
  LengthFwd = 4
  LengthRev = 0
  Placement = pos=(0,12.6,0) rot=(0,0,1;0rad)
  Solid = true
  Symmetric = false
FEATURE [Part::MultiFuse] Fusion004
  Refine = true
  Shapes = -> [Cut050,Extrude088]
FEATURE [Part::Cut] Cut051
  Base = -> Fusion004
  Refine = true
  Tool = -> Extrude087
FEATURE [Part::Cut] Cut052
  Base = -> Cut051
  Refine = true
  Tool = -> Extrude086
FEATURE [Sketcher::SketchObject] Sketch154
  ArcFitTolerance = 1e-06
  AttachmentSupport = -> [Pad016]
  ExternalGeometry = -> [Binder001]
  FullyConstrained = true
  MakeInternals = false
  MapMode = 5
  Placement = pos=(0,-3.6,0) rot=(1,0,0;1.5708rad)
  sketch-geometry (25):
    g0: LineSegment StartX=-214.643 StartY=-72.4316 StartZ=0 EndX=-212.243 EndY=-72.4316 EndZ=0
    g1: LineSegment StartX=-212.243 StartY=-72.4316 StartZ=0 EndX=-212.243 EndY=-71.2316 EndZ=0
    g2: LineSegment StartX=-212.243 StartY=-71.2316 StartZ=0 EndX=-214.643 EndY=-71.2316 EndZ=0
    g3: LineSegment StartX=-214.643 StartY=-71.2316 StartZ=0 EndX=-214.643 EndY=-72.4316 EndZ=0
    g4: GeomPoint [constr] X=-213.443 Y=-71.8316 Z=0
    g5: LineSegment StartX=-214.643 StartY=-69.6316 StartZ=0 EndX=-212.243 EndY=-69.6316 EndZ=0
    g6: LineSegment StartX=-212.243 StartY=-69.6316 StartZ=0 EndX=-212.243 EndY=-68.4316 EndZ=0
    g7: LineSegment StartX=-212.243 StartY=-68.4316 StartZ=0 EndX=-214.643 EndY=-68.4316 EndZ=0
    g8: LineSegment StartX=-214.643 StartY=-68.4316 StartZ=0 EndX=-214.643 EndY=-69.6316 EndZ=0
    g9: GeomPoint [constr] X=-213.443 Y=-69.0316 Z=0
    g10: LineSegment StartX=-214.643 StartY=-66.8316 StartZ=0 EndX=-212.243 EndY=-66.8316 EndZ=0
    g11: LineSegment StartX=-212.243 StartY=-66.8316 StartZ=0 EndX=-212.243 EndY=-65.6316 EndZ=0
    g12: LineSegment StartX=-212.243 StartY=-65.6316 StartZ=0 EndX=-214.643 EndY=-65.6316 EndZ=0
    g13: LineSegment StartX=-214.643 StartY=-65.6316 StartZ=0 EndX=-214.643 EndY=-66.8316 EndZ=0
    g14: GeomPoint [constr] X=-213.443 Y=-66.2316 Z=0
    g15: LineSegment StartX=-214.643 StartY=-64.0316 StartZ=0 EndX=-212.243 EndY=-64.0316 EndZ=0
    g16: LineSegment StartX=-212.243 StartY=-64.0316 StartZ=0 EndX=-212.243 EndY=-62.8316 EndZ=0
    g17: LineSegment StartX=-212.243 StartY=-62.8316 StartZ=0 EndX=-214.643 EndY=-62.8316 EndZ=0
    g18: LineSegment StartX=-214.643 StartY=-62.8316 StartZ=0 EndX=-214.643 EndY=-64.0316 EndZ=0
    g19: GeomPoint [constr] X=-213.443 Y=-63.4316 Z=0
    g20: LineSegment StartX=-214.643 StartY=-61.2316 StartZ=0 EndX=-212.243 EndY=-61.2316 EndZ=0
    g21: LineSegment StartX=-212.243 StartY=-61.2316 StartZ=0 EndX=-212.243 EndY=-60.0316 EndZ=0
    g22: LineSegment StartX=-212.243 StartY=-60.0316 StartZ=0 EndX=-214.643 EndY=-60.0316 EndZ=0
    g23: LineSegment StartX=-214.643 StartY=-60.0316 StartZ=0 EndX=-214.643 EndY=-61.2316 EndZ=0
    g24: GeomPoint [constr] X=-213.443 Y=-60.6316 Z=0
  constraints (65):
    c: Coincident(g0,g1)
    c: Coincident(g1,g2)
    c: Coincident(g2,g3)
    c: Coincident(g3,g0)
    c: Horizontal(g0)
    c: Horizontal(g2)
    c: Vertical(g1)
    c: Vertical(g3)
    c: Symmetric(g2,g0,g4)
    c: Distance(g1,g3) = 2.4
    c: Distance(g0,g2) = 1.2
    c: Coincident(g5,g6)
    c: Coincident(g6,g7)
    c: Coincident(g7,g8)
    c: Coincident(g8,g5)
    c: Horizontal(g5)
    c: Horizontal(g7)
    c: Vertical(g6)
    c: Vertical(g8)
    c: Symmetric(g7,g5,g9)
    c: Distance(g6,g8) = 2.4
    c: Distance(g5,g7) = 1.2
    c: Coincident(g10,g11)
    c: Coincident(g11,g12)
    c: Coincident(g12,g13)
    c: Coincident(g13,g10)
    c: Horizontal(g10)
    c: Horizontal(g12)
    c: Vertical(g11)
    c: Vertical(g13)
    c: Symmetric(g12,g10,g14)
    c: Distance(g11,g13) = 2.4
    c: Distance(g10,g12) = 1.2
    c: Coincident(g15,g16)
    c: Coincident(g16,g17)
    c: Coincident(g17,g18)
    c: Coincident(g18,g15)
    c: Horizontal(g15)
    c: Horizontal(g17)
    c: Vertical(g16)
    c: Vertical(g18)
    c: Symmetric(g17,g15,g19)
    c: Distance(g16,g18) = 2.4
    c: Distance(g15,g17) = 1.2
    c: Vertical(g4,g-3)
    c: Vertical(g9,g-3)
    c: Vertical(g14,g-3)
    c: Vertical(g19,g-3)
    c: DistanceY(g-3,g4) = 5
    c: DistanceY(g4,g9) = 2.8
    c: DistanceY(g9,g14) = 2.8
    c: DistanceY(g14,g19) = 2.8
    c: Coincident(g20,g21)
    c: Coincident(g21,g22)
    c: Coincident(g22,g23)
    c: Coincident(g23,g20)
    c: Horizontal(g20)
    c: Horizontal(g22)
    c: Vertical(g21)
    c: Vertical(g23)
    c: Symmetric(g22,g20,g24)
    c: Distance(g21,g23) = 2.4
    c: Distance(g20,g22) = 1.2
    c: DistanceY(g19,g24) = 2.8
    c: Vertical(g-3,g24)
FEATURE [PartDesign::Pocket] Pocket020
  BaseFeature = -> Pocket012
  Direction = (0,1,-2e-16)
  Length = 3.6
  Length2 = 5
  Profile = -> Sketch154
  ReferenceAxis = -> Sketch154 [N_Axis]
  Refine = true
  Suppressed = false
  Type = 0
FEATURE [PartDesign::Body] Body007  label="lato DX"
  AllowCompound = false
  Group = -> [Binder001,Sketch114,Pad011,Chamfer014,Sketch115,Pocket006,Sketch116,Pad012,Sketch117,Pocket007,Sketch118,Pad013,Sketch119,Pocket008,Pad017,Chamfer009,Pocket009,Sketch123,Sketch120,Pad014,Pad018,Chamfer008,Pocket010,Sketch121,Pad015,Sketch122,Pad016,SubtractivePipe004,SubtractivePipe005,Sketch149,Sketch148,Sketch124,Sketch125,Sketch126,Sketch129,Sketch130,Clone2D001,Sketch131,SubtractiveLoft002,+13 more]
  Origin = -> Origin007
  Tip = -> Pocket020
FEATURE [Sketcher::SketchObject] Sketch155  label="fermo per protezione batteria"
  ArcFitTolerance = 1e-06
  AttachmentSupport = -> [XZ_Plane]
  ExternalGeometry = -> [Sketch016,Sketch]
  FullyConstrained = true
  MakeInternals = false
  MapMode = 5
  Placement = pos=(0,0,0) rot=(1,0,0;1.5708rad)
  sketch-geometry (9):
    g0: LineSegment StartX=-183.305 StartY=-72.0316 StartZ=0 EndX=-183.305 EndY=-76.8316 EndZ=0
    g1: LineSegment StartX=-179.305 StartY=-68.8316 StartZ=0 EndX=-179.305 EndY=-72.8316 EndZ=0
    g2: LineSegment StartX=-183.305 StartY=-76.8316 StartZ=0 EndX=-179.305 EndY=-72.8316 EndZ=0
    g3: LineSegment StartX=-179.305 StartY=-68.8316 StartZ=0 EndX=-183.305 EndY=-68.8316 EndZ=0
    g4: LineSegment StartX=-183.305 StartY=-72.0316 StartZ=0 EndX=-181.305 EndY=-72.0316 EndZ=0
    g5: LineSegment StartX=-181.305 StartY=-72.0316 StartZ=0 EndX=-181.305 EndY=-70.4316 EndZ=0
    g6: LineSegment StartX=-181.305 StartY=-70.4316 StartZ=0 EndX=-183.305 EndY=-70.4316 EndZ=0
    g7: LineSegment StartX=-183.305 StartY=-70.4316 StartZ=0 EndX=-183.305 EndY=-68.8316 EndZ=0
    g8: LineSegment [constr] StartX=-183.305 StartY=-72.0316 StartZ=0 EndX=-183.305 EndY=-78.4316 EndZ=0
  constraints (28):
    c: Vertical(g0)
    c: Horizontal(g0,g-3)
    c: Tangent(g0,g-3)
    c: Vertical(g1)
    c: Vertical(g1,g-3)
    c: PointOnObject(g1,g-3)
    c: Coincident(g2,g0)
    c: Coincident(g2,g1)
    c: Coincident(g3,g1)
    c: Horizontal(g3)
    c: Distance(g4) = 2
    c: Coincident(g4,g0)
    c: Horizontal(g4)
    c: Vertical(g3,g0)
    c: Distance(g5) = 1.6
    c: Coincident(g5,g4)
    c: Vertical(g5)
    c: Coincident(g6,g5)
    c: Horizontal(g6)
    c: Coincident(g7,g6)
    c: Coincident(g7,g3)
    c: Vertical(g7)
    c: DistanceY(g7,g7) = 1.6
    c: Vertical(g8)
    c: PointOnObject(g8,g-4)
    c: DistanceY(g8,g8) = 6.4
    c: Horizontal(g8,g0)
    c: Tangent(g8,g-3)
FEATURE [Part::Extrusion] Extrude089  label="Extrude089 - fermo per protezione batteria"
  Base = -> Sketch155
  Dir = (0,-1,2e-16)
  DirMode = 2
  FaceMakerClass = Part::FaceMakerBullseye
  FaceMakerMode = 3
  LengthFwd = 12
  LengthRev = 0
  Solid = true
  Symmetric = true
FEATURE [Sketcher::SketchObject] Sketch156  label="buco per protezione batteria"
  ArcFitTolerance = 1e-06
  AttachmentSupport = -> [XZ_Plane]
  ExternalGeometry = -> [Sketch,Sketch016]
  FullyConstrained = true
  MakeInternals = false
  MapMode = 5
  Placement = pos=(0,0,0) rot=(1,0,0;1.5708rad)
  sketch-geometry (5):
    g0: LineSegment [constr] StartX=-183.305 StartY=-76.8316 StartZ=0 EndX=-183.305 EndY=-78.4316 EndZ=0
    g1: LineSegment StartX=-200.305 StartY=-78.4316 StartZ=0 EndX=-200.305 EndY=-80.4316 EndZ=0
    g2: LineSegment StartX=-200.305 StartY=-80.4316 StartZ=0 EndX=-198.505 EndY=-80.4316 EndZ=0
    g3: LineSegment StartX=-198.505 StartY=-80.4316 StartZ=0 EndX=-198.505 EndY=-78.4316 EndZ=0
    g4: LineSegment StartX=-198.505 StartY=-78.4316 StartZ=0 EndX=-200.305 EndY=-78.4316 EndZ=0
  constraints (15):
    c: Vertical(g0)
    c: Tangent(g0,g-4)
    c: PointOnObject(g0,g-3)
    c: Horizontal(g0,g-4)
    c: Coincident(g1,g2)
    c: Coincident(g2,g3)
    c: Coincident(g3,g4)
    c: Coincident(g4,g1)
    c: Vertical(g1)
    c: Vertical(g3)
    c: Horizontal(g2)
    c: Distance(g1,g3) = 1.8
    c: Distance(g2,g4) = 2
    c: Tangent(g4,g-3)
    c: Distance(g3,g0) = 15.2
FEATURE [PartDesign::Body] Body  label="Struttura pistola"
  AllowCompound = false
  Group = -> [Sketch,Sketch002,Sketch004,DatumPlane,Sketch005,DatumPlane001,CopyCut,Sketch008,Sketch009,Sketch010,Sketch011,Sketch012,Sketch013,Sketch014,Sketch015,Sketch016,Sketch017,Sketch018,Sketch019,Sketch020,Sketch022,Sketch023,Sketch024,Sketch025,Sketch026,Sketch027,Sketch029,Sketch030,Sketch031,Sketch032,Sketch033,Sketch034,Sketch035,Sketch036,Sketch037,Sketch038,Sketch039,Sketch040,Sketch041,Sketch042,+30 more]
  Origin = -> Origin
FEATURE [Part::Extrusion] Extrude090  label="Extrude090 - buco per protezione batteria"
  Base = -> Sketch156
  Dir = (0,-1,2e-16)
  DirMode = 2
  FaceMakerClass = Part::FaceMakerBullseye
  FaceMakerMode = 3
  LengthFwd = 4.8
  LengthRev = 0
  Solid = true
  Symmetric = true
FEATURE [Part::MultiFuse] Fusion005
  Refine = true
  Shapes = -> [Cut052,Extrude089]
FEATURE [Part::Cut] Cut053
  Base = -> Fusion005
  Refine = true
  Tool = -> Extrude090
FEATURE [Sketcher::SketchObject] Sketch157
  ArcFitTolerance = 1e-06
  AttachmentSupport = -> [XY_Plane010]
  FullyConstrained = true
  MakeInternals = false
  MapMode = 5
  sketch-geometry (11):
    g0: LineSegment [constr] StartX=1.8 StartY=8 StartZ=0 EndX=1.8 EndY=-8 EndZ=0
    g1: LineSegment StartX=1.8 StartY=8 StartZ=0 EndX=17 EndY=8 EndZ=0
    g2: LineSegment StartX=1.8 StartY=-8 StartZ=0 EndX=17 EndY=-8 EndZ=0
    g3: LineSegment StartX=19 StartY=6 StartZ=0 EndX=19 EndY=-6 EndZ=0
    g4: LineSegment StartX=19 StartY=6 StartZ=0 EndX=17 EndY=6 EndZ=0
    g5: LineSegment StartX=19 StartY=-6 StartZ=0 EndX=17 EndY=-6 EndZ=0
    g6: LineSegment StartX=17 StartY=8 StartZ=0 EndX=17 EndY=6 EndZ=0
    g7: LineSegment StartX=17 StartY=-8 StartZ=0 EndX=17 EndY=-6 EndZ=0
    g8: LineSegment StartX=0 StartY=8 StartZ=0 EndX=0 EndY=-8 EndZ=0
    g9: LineSegment StartX=1.8 StartY=8 StartZ=0 EndX=0 EndY=8 EndZ=0
    g10: LineSegment StartX=1.8 StartY=-8 StartZ=0 EndX=0 EndY=-8 EndZ=0
  constraints (30):
    c: DistanceY(g0,g0) = 16
    c: Distance(g1) = 15.2
    c: Coincident(g1,g0)
    c: Horizontal(g1)
    c: Coincident(g2,g0)
    c: Horizontal(g2)
    c: Equal(g1,g2)
    c: DistanceY(g3,g3) = 12
    c: Symmetric(g0,g0,g-1)
    c: Symmetric(g3,g3,g-1)
    c: Coincident(g4,g3)
    c: Horizontal(g4)
    c: DistanceX(g4,g4) = 2
    c: Coincident(g5,g3)
    c: Horizontal(g5)
    c: Equal(g4,g5)
    c: Coincident(g6,g1)
    c: Vertical(g6)
    c: Coincident(g7,g2)
    c: Coincident(g7,g5)
    c: Coincident(g4,g6)
    c: Equal(g8,g0)
    c: Coincident(g9,g0)
    c: Horizontal(g9)
    c: DistanceX(g9,g9) = 1.8
    c: Coincident(g10,g0)
    c: Horizontal(g10)
    c: Equal(g9,g10)
    c: Coincident(g8,g9)
    c: Tangent(g8,g-2)
FEATURE [PartDesign::Pad] Pad031
  Direction = (0,0,1)
  Length = 1.4
  Length2 = 10
  Profile = -> Sketch157
  ReferenceAxis = -> Sketch157 [N_Axis]
  Refine = true
  Suppressed = false
  Type = 0
FEATURE [Sketcher::SketchObject] Sketch158
  ArcFitTolerance = 1e-06
  AttachmentSupport = -> [Pad031]
  ExternalGeometry = -> [Pad031]
  FullyConstrained = true
  MakeInternals = false
  MapMode = 5
  Placement = pos=(0,0,1.4) rot=(0,0,1;0rad)
  sketch-geometry (4):
    g0: LineSegment StartX=0 StartY=8 StartZ=0 EndX=0 EndY=-8 EndZ=0
    g1: LineSegment StartX=0 StartY=8 StartZ=0 EndX=1.8 EndY=8 EndZ=0
    g2: LineSegment StartX=1.8 StartY=8 StartZ=0 EndX=1.8 EndY=-8 EndZ=0
    g3: LineSegment StartX=0 StartY=-8 StartZ=0 EndX=1.8 EndY=-8 EndZ=0
  constraints (10):
    c: Coincident(g0,g-3)
    c: Coincident(g0,g-4)
    c: Distance(g1) = 1.8
    c: Coincident(g1,g0)
    c: PointOnObject(g1,g-3)
    c: Coincident(g2,g1)
    c: Vertical(g2)
    c: Coincident(g3,g0)
    c: PointOnObject(g3,g-4)
    c: Coincident(g3,g2)
FEATURE [PartDesign::Pad] Pad032
  BaseFeature = -> Pad031
  Direction = (0,0,1)
  Length = 6.4
  Length2 = 10
  Profile = -> Sketch158
  ReferenceAxis = -> Sketch158 [N_Axis]
  Refine = true
  Suppressed = false
  Type = 0
FEATURE [Sketcher::SketchObject] Sketch159
  ArcFitTolerance = 1e-06
  AttachmentSupport = -> [Pad032]
  ExternalGeometry = -> [Pad032,Pad031]
  FullyConstrained = true
  MakeInternals = false
  MapMode = 5
  Placement = pos=(0,0,7.8) rot=(0,0,1;0rad)
  sketch-geometry (7):
    g0: LineSegment StartX=0.1 StartY=2.2 StartZ=0 EndX=0.1 EndY=-2.2 EndZ=0
    g1: LineSegment StartX=0.1 StartY=-2.2 StartZ=0 EndX=1.7 EndY=-2.2 EndZ=0
    g2: LineSegment StartX=1.7 StartY=-2.2 StartZ=0 EndX=1.7 EndY=2.2 EndZ=0
    g3: LineSegment StartX=1.7 StartY=2.2 StartZ=0 EndX=0.1 EndY=2.2 EndZ=0
    g4: GeomPoint [constr] X=0.9 Y=8 Z=0
    g5: GeomPoint [constr] X=0.9 Y=-8 Z=0
    g6: LineSegment [constr] StartX=0.9 StartY=8 StartZ=0 EndX=0.9 EndY=-8 EndZ=0
  constraints (14):
    c: Coincident(g0,g1)
    c: Coincident(g1,g2)
    c: Coincident(g2,g3)
    c: Coincident(g3,g0)
    c: Vertical(g2)
    c: Horizontal(g1)
    c: Distance(g0,g2) = 1.6
    c: Distance(g1,g3) = 4.4
    c: Symmetric(g0,g0,g-1)
    c: Symmetric(g-4,g-4,g4)
    c: Symmetric(g-3,g-5,g5)
    c: Coincident(g6,g4)
    c: Coincident(g6,g5)
    c: Symmetric(g0,g2,g6)
FEATURE [PartDesign::Pad] Pad033
  BaseFeature = -> Pad032
  Direction = (0,0,1)
  Length = 1.4
  Length2 = 10
  Profile = -> Sketch159
  ReferenceAxis = -> Sketch159 [N_Axis]
  Refine = true
  Suppressed = false
  Type = 0
FEATURE [PartDesign::Body] Body010  label="Protezione_inferiore_batteria"
  AllowCompound = false
  Group = -> [Sketch157,Pad031,Sketch158,Pad032,Sketch159,Pad033]
  Origin = -> Origin010
  Tip = -> Pad033
note: 2 file-system paths scrubbed to <path> (originals preserved in the JSON sidecar)
